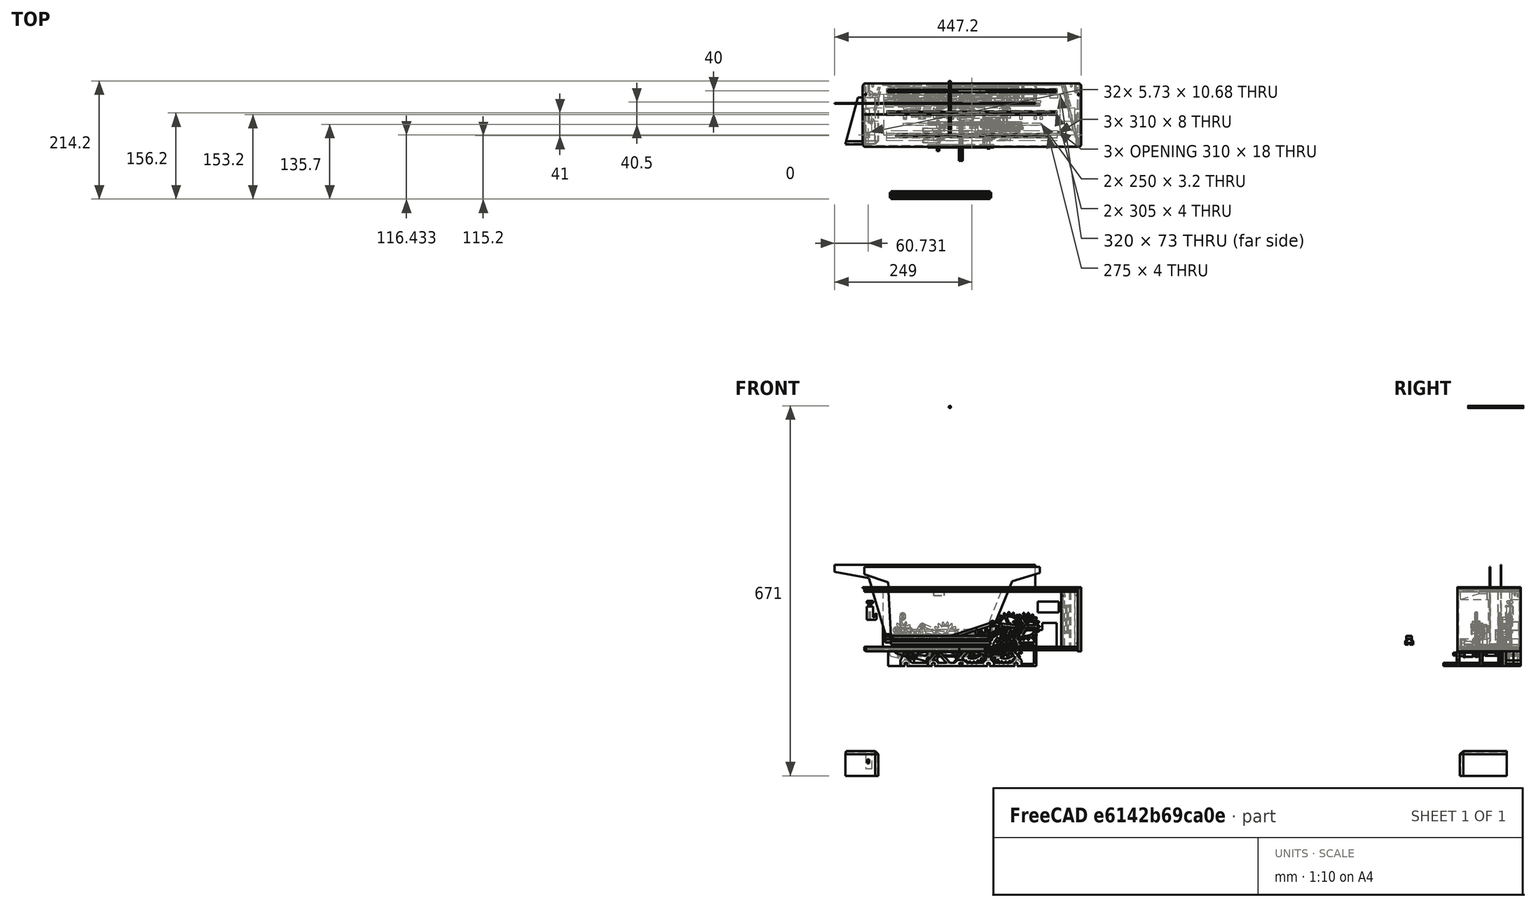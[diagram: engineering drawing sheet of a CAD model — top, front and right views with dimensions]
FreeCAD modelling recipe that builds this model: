
FCSTD DOCUMENT  (FreeCAD 0.22R37668 (Git))
Label: wobbler
License: Creative Commons Attribution-ShareAlike 3.0
LicenseURL: https://creativecommons.org/licenses/by-sa/3.0/
objects: Sketcher::SketchObject×136, PartDesign::Pad×68, PartDesign::Body×68, PartDesign::Pocket×54, PartDesign::FeatureBase×8, PartDesign::Mirrored×7, App::Part×7, PartDesign::FeaturePython×6, PartDesign::Groove×6, PartDesign::Revolution×6, Part::FeaturePython×6, PartDesign::PolarPattern×5, PartDesign::Chamfer×5, PartDesign::MultiTransform×3, Image::ImagePlane×3, PartDesign::Fillet×3, Mesh::Feature×2, PartDesign::LinearPattern×2, PartDesign::Plane×2, App::DocumentObjectGroup×2, +3 more types
note: 532 computed .brp shape members not serialized (recipe doc carries the construction recipe); baked Part::Feature solids carry a one-line shape summary decoded from their .brp

FEATURE [PartDesign::FeaturePython] InvoluteGear  label="M2.5-24T"  # WARN: FeaturePython — macro-defined, semantics opaque (R4)
  AttacherType = Attacher::AttachEngine3D
  Placement = pos=(0,0,0) rot=(1,0,0;1.5708rad)
  Suppressed = false
  angular_backlash = 0.190986
  backlash = 0.1
  beta = 0
  clearance = 0.25
  da = 65
  df = 53.75
  double_helix = false
  dw = 60
  head = 0
  head_fillet = 0
  height = 5
  module = 2.5
  numpoints = 6
  pressure_angle = 20
  properties_from_tool = false
  reversed_backlash = false
  root_fillet = 0
  shift = 0
  simple = false
  teeth = 24
  transverse_pitch = 7.85398
  undercut = false
  version = 0.0.4
  expr: angular_backlash = backlash / dw * 360 ° / pi
  expr: dw = teeth * module
FEATURE [Sketcher::SketchObject] Sketch001
  AttachmentSupport = -> [XY_Plane001]
  FullyConstrained = true
  MapMode = 5
  sketch-geometry (6):
    g0: LineSegment StartX=-2.45 StartY=0 StartZ=0 EndX=-2.45 EndY=-7.9 EndZ=0
    g1: LineSegment StartX=-2.45 StartY=-7.9 StartZ=0 EndX=19.65 EndY=-7.9 EndZ=0
    g2: LineSegment StartX=19.65 StartY=-7.9 StartZ=0 EndX=19.65 EndY=-3 EndZ=0
    g3: LineSegment StartX=19.65 StartY=-3 StartZ=0 EndX=2.45 EndY=-3 EndZ=0
    g4: LineSegment StartX=2.45 StartY=-3 StartZ=0 EndX=2.45 EndY=0 EndZ=0
    g5: LineSegment StartX=2.45 StartY=0 StartZ=0 EndX=-2.45 EndY=0 EndZ=0
  constraints (17):
    c: PointOnObject(g0,g-1)
    c: Vertical(g0)
    c: Coincident(g0,g1)
    c: Horizontal(g1)
    c: Coincident(g1,g2)
    c: Vertical(g2)
    c: Coincident(g2,g3)
    c: Horizontal(g3)
    c: Coincident(g3,g4)
    c: Coincident(g4,g5)
    c: Coincident(g5,g0)
    c: DistanceX(g5,g5) = 4.9
    c: Symmetric(g4,g0,g-2)
    c: Vertical(g4)
    c: DistanceY(g4,g4) = 3
    c: DistanceX(g3,g3) = 17.2
    c: Equal(g2,g5)
FEATURE [PartDesign::Pocket] Pocket
  BaseFeature = -> InvoluteGear
  Direction = (0,0,-1)
  Length = 5.2
  Length2 = 5
  Midplane = true
  Placement = pos=(0,0,0) rot=(1,0,0;1.5708rad)
  Profile = -> Sketch001
  ReferenceAxis = -> Sketch001 [N_Axis]
  Refine = true
  Suppressed = false
  Type = 0
FEATURE [Sketcher::SketchObject] Sketch002
  AttachmentSupport = -> [XZ_Plane002]
  FullyConstrained = true
  MapMode = 5
  Placement = pos=(0,0,0) rot=(1,0,0;1.5708rad)
  sketch-geometry (1):
    g0: Circle CenterX=0 CenterY=0 CenterZ=0 NormalX=0 NormalY=0 NormalZ=1 AngleXU=0 Radius=2.5
  constraints (2):
    c: Coincident(g0,g-1)
    c: Diameter(g0) = 5
FEATURE [PartDesign::Pad] Pad
  Direction = (0,-1,2e-16)
  Length = 56
  Length2 = 10
  Midplane = true
  Placement = pos=(0,0,0) rot=(1,0,0;1.5708rad)
  Profile = -> Sketch002
  ReferenceAxis = -> Sketch002 [N_Axis]
  Refine = true
  Suppressed = false
  Type = 0
FEATURE [Sketcher::SketchObject] Sketch003
  AttachmentSupport = -> [XZ_Plane002]
  FullyConstrained = true
  MapMode = 5
  Placement = pos=(0,0,0) rot=(1,0,0;1.5708rad)
  sketch-geometry (5):
    g0: ArcOfCircle CenterX=17 CenterY=0 CenterZ=0 NormalX=0 NormalY=0 NormalZ=1 AngleXU=0 Radius=7.5 StartAngle=5.94335 EndAngle=7.85398
    g1: ArcOfCircle CenterX=5 CenterY=0 CenterZ=0 NormalX=0 NormalY=0 NormalZ=1 AngleXU=0 Radius=7.5 StartAngle=1.5708 EndAngle=3.14159
    g2: LineSegment StartX=5 StartY=7.5 StartZ=0 EndX=17 EndY=7.5 EndZ=0
    g3: LineSegment StartX=-2.5 StartY=9e-16 StartZ=0 EndX=-2.5 EndY=-2.5 EndZ=0
    g4: LineSegment StartX=-2.5 StartY=-2.5 StartZ=0 EndX=24.0711 EndY=-2.5 EndZ=0
  constraints (15):
    c: PointOnObject(g0,g-1)
    c: PointOnObject(g1,g-1)
    c: PointOnObject(g1,g-1)
    c: Coincident(g2,g0)
    c: Horizontal(g2)
    c: DistanceX(g0) = 17
    c: Diameter(g0) = 15
    c: Tangent(g1,g3) = -1.5708
    c: Coincident(g3,g4)
    c: Coincident(g4,g0)
    c: Horizontal(g4)
    c: DistanceX(g3) = -2.5
    c: DistanceY(g3,g3) = 2.5
    c: Equal(g1,g0)
    c: Tangent(g2,g1) = 1.5708
FEATURE [PartDesign::Pad] Pad001
  BaseFeature = -> Pad
  Direction = (0,-1,2e-16)
  Length = 26
  Length2 = 10
  Midplane = true
  Placement = pos=(0,0,0) rot=(1,0,0;1.5708rad)
  Profile = -> Sketch003
  ReferenceAxis = -> Sketch003 [N_Axis]
  Refine = true
  Suppressed = false
  Type = 0
FEATURE [Sketcher::SketchObject] Sketch004
  AttachmentSupport = -> [XY_Plane002]
  FullyConstrained = true
  MapMode = 5
  sketch-geometry (6):
    g0: LineSegment StartX=-2.5 StartY=18 StartZ=0 EndX=-2.5 EndY=0 EndZ=0
    g1: LineSegment StartX=-2.5 StartY=0 StartZ=0 EndX=19.5 EndY=0 EndZ=0
    g2: LineSegment StartX=19.5 StartY=0 StartZ=0 EndX=19.5 EndY=15 EndZ=0
    g3: LineSegment StartX=19.5 StartY=15 StartZ=0 EndX=2.5 EndY=15 EndZ=0
    g4: LineSegment StartX=2.5 StartY=15 StartZ=0 EndX=2.5 EndY=18 EndZ=0
    g5: LineSegment StartX=2.5 StartY=18 StartZ=0 EndX=-2.5 EndY=18 EndZ=0
  constraints (17):
    c: Vertical(g0)
    c: Coincident(g0,g1)
    c: Horizontal(g1)
    c: Coincident(g1,g2)
    c: Vertical(g2)
    c: Coincident(g2,g3)
    c: Horizontal(g3)
    c: Coincident(g3,g4)
    c: Vertical(g4)
    c: Coincident(g4,g5)
    c: Coincident(g5,g0)
    c: Symmetric(g0,g4,g-2)
    c: DistanceX(g5,g5) = 5
    c: DistanceY(g4,g4) = 3
    c: DistanceY(g0) = 18
    c: PointOnObject(g0,g-1)
    c: DistanceX(g3,g3) = 17
FEATURE [PartDesign::Pad] Pad002
  BaseFeature = -> Pad001
  Direction = (0,0,1)
  Length = 5
  Length2 = 10
  Midplane = true
  Placement = pos=(0,0,0) rot=(1,0,0;1.5708rad)
  Profile = -> Sketch004
  ReferenceAxis = -> Sketch004 [N_Axis]
  Refine = true
  Suppressed = false
  Type = 0
FEATURE [Sketcher::SketchObject] Sketch005
  AttachmentSupport = -> [XZ_Plane002]
  FullyConstrained = true
  MapMode = 5
  Placement = pos=(0,0,0) rot=(1,0,0;1.5708rad)
  sketch-geometry (6):
    g0: ArcOfCircle CenterX=17 CenterY=0 CenterZ=0 NormalX=0 NormalY=0 NormalZ=1 AngleXU=0 Radius=3 StartAngle=5.29807 EndAngle=10.4099
    g1: LineSegment StartX=15.3417 StartY=-2.5 StartZ=0 EndX=-4.65831 EndY=-2.5 EndZ=0
    g2: LineSegment StartX=-4.65831 StartY=-2.5 StartZ=0 EndX=-4.65831 EndY=17.5 EndZ=0
    g3: LineSegment StartX=-4.65831 StartY=17.5 StartZ=0 EndX=38.6583 EndY=17.5 EndZ=0
    g4: LineSegment StartX=38.6583 StartY=17.5 StartZ=0 EndX=38.6583 EndY=-2.5 EndZ=0
    g5: LineSegment StartX=38.6583 StartY=-2.5 StartZ=0 EndX=18.6583 EndY=-2.5 EndZ=0
  constraints (19):
    c: PointOnObject(g0,g-1)
    c: Coincident(g0,g1)
    c: Horizontal(g1)
    c: Coincident(g1,g2)
    c: Vertical(g2)
    c: Coincident(g2,g3)
    c: Horizontal(g3)
    c: Coincident(g3,g4)
    c: Vertical(g4)
    c: Coincident(g4,g5)
    c: Coincident(g5,g0)
    c: Horizontal(g5)
    c: Horizontal(g0,g0)
    c: DistanceY(g1) = -2.5
    c: DistanceX(g0) = 17
    c: Diameter(g0) = 6
    c: Equal(g5,g4)
    c: DistanceX(g1,g1) = 20
    c: Equal(g1,g5)
FEATURE [PartDesign::Pocket] Pocket001
  BaseFeature = -> Pad002
  Direction = (0,1,-2e-16)
  Length = 15
  Length2 = 5
  Midplane = true
  Placement = pos=(0,0,0) rot=(1,0,0;1.5708rad)
  Profile = -> Sketch005
  ReferenceAxis = -> Sketch005 [N_Axis]
  Refine = true
  Suppressed = false
  Type = 0
FEATURE [Sketcher::SketchObject] Sketch006
  AttachmentSupport = -> [XZ_Plane001]
  FullyConstrained = true
  MapMode = 5
  Placement = pos=(0,0,0) rot=(1,0,0;1.5708rad)
  sketch-geometry (7):
    g0: ArcOfCircle CenterX=0 CenterY=0 CenterZ=0 NormalX=0 NormalY=0 NormalZ=1 AngleXU=0 Radius=7 StartAngle=0.608246 EndAngle=1.48615
    g1: ArcOfCircle CenterX=0 CenterY=0 CenterZ=0 NormalX=0 NormalY=0 NormalZ=1 AngleXU=0 Radius=21.5 StartAngle=0.187137 EndAngle=1.90726
    g2: LineSegment StartX=21.1246 StartY=4 StartZ=0 EndX=5.74456 EndY=4 EndZ=0
    g3: LineSegment StartX=0.59182 StartY=6.97494 StartZ=0 EndX=-7.09821 EndY=20.2945 EndZ=0
    g4: LineSegment StartX=0 StartY=0 StartZ=0 EndX=-10.5623 EndY=18.2945 EndZ=0
    g5: LineSegment StartX=-10.5623 StartY=18.2945 StartZ=0 EndX=-7.09821 EndY=20.2945 EndZ=0
    g6: LineSegment StartX=21.1246 StartY=4 StartZ=0 EndX=21.1246 EndY=0 EndZ=0
  constraints (20):
    c: Coincident(g0,g-1)
    c: Coincident(g1,g0)
    c: Coincident(g2,g1)
    c: Coincident(g2,g0)
    c: Coincident(g3,g0)
    c: Coincident(g3,g1)
    c: Coincident(g4,g0)
    c: Coincident(g5,g4)
    c: Coincident(g5,g1)
    c: Parallel(g4,g3)
    c: Perpendicular(g4,g5)
    c: Angle(g-1,g4) = 2.0944
    c: Horizontal(g2)
    c: Coincident(g6,g1)
    c: PointOnObject(g6,g-1)
    c: Vertical(g6)
    c: Equal(g6,g5)
    c: Diameter(g0) = 14
    c: Diameter(g1) = 43
    c: DistanceY(g6,g6) = 4
FEATURE [PartDesign::Pocket] Pocket002  label="120deg-sector"
  BaseFeature = -> Pocket
  Direction = (0,1,-2e-16)
  Length = 5
  Length2 = 5
  Midplane = true
  Placement = pos=(0,0,0) rot=(1,0,0;1.5708rad)
  Profile = -> Sketch006
  ReferenceAxis = -> Sketch006 [N_Axis]
  Refine = true
  Suppressed = false
  Type = 1
FEATURE [PartDesign::PolarPattern] PolarPattern
  Angle = 360
  Axis = -> Sketch006 [N_Axis]
  BaseFeature = -> Pocket002
  Mode = 0
  Occurrences = 3
  Offset = 120
  Originals = -> [Pocket002]
  Placement = pos=(0,0,0) rot=(1,0,0;1.5708rad)
  Refine = true
  Suppressed = false
  TransformMode = 0
FEATURE [PartDesign::Body] Body001  label="M2.5-24t-Crank"
  AllowCompound = false
  Group = -> [InvoluteGear,Sketch001,Pocket,Sketch006,Pocket002,PolarPattern]
  Origin = -> Origin001
  Tip = -> PolarPattern
FEATURE [Sketcher::SketchObject] Sketch007
  AttachmentSupport = -> [XY_Plane003]
  FullyConstrained = true
  MapMode = 5
  sketch-geometry (22):
    g0: Circle CenterX=0 CenterY=0 CenterZ=0 NormalX=0 NormalY=0 NormalZ=1 AngleXU=0 Radius=2.5
    g1: Circle CenterX=10 CenterY=0 CenterZ=0 NormalX=0 NormalY=0 NormalZ=1 AngleXU=0 Radius=2.5
    g2: ArcOfCircle CenterX=0 CenterY=0 CenterZ=0 NormalX=0 NormalY=0 NormalZ=1 AngleXU=0 Radius=5 StartAngle=0.304693 EndAngle=1.7897
    g3: ArcOfCircle CenterX=0 CenterY=0 CenterZ=0 NormalX=0 NormalY=0 NormalZ=1 AngleXU=0 Radius=17 StartAngle=0.438962 EndAngle=2.00604
    g4: ArcOfCircle CenterX=0 CenterY=0 CenterZ=0 NormalX=0 NormalY=0 NormalZ=1 AngleXU=0 Radius=5 StartAngle=2.39909 EndAngle=3.8841
    g5: ArcOfCircle CenterX=0 CenterY=0 CenterZ=0 NormalX=0 NormalY=0 NormalZ=1 AngleXU=0 Radius=17 StartAngle=2.18275 EndAngle=4.10044
    g6: ArcOfCircle CenterX=0 CenterY=0 CenterZ=0 NormalX=0 NormalY=0 NormalZ=1 AngleXU=0 Radius=17 StartAngle=4.27714 EndAngle=5.84422
    g7: ArcOfCircle CenterX=0 CenterY=0 CenterZ=0 NormalX=0 NormalY=0 NormalZ=1 AngleXU=0 Radius=5 StartAngle=4.49348 EndAngle=5.97849
    g8: LineSegment StartX=0 StartY=0 StartZ=0 EndX=-8.46685 EndY=14.665 EndZ=0
    g9: LineSegment StartX=-3.68389 StartY=3.38068 StartZ=0 EndX=-9.76589 EndY=13.915 EndZ=0
    g10: LineSegment StartX=-9.76589 StartY=13.915 StartZ=0 EndX=-7.16781 EndY=15.415 EndZ=0
    g11: LineSegment StartX=-7.16781 StartY=15.415 StartZ=0 EndX=-1.08581 EndY=4.88068 EndZ=0
    g12: LineSegment StartX=-3.68389 StartY=-3.38068 StartZ=0 EndX=-9.76589 EndY=-13.915 EndZ=0
    g13: LineSegment StartX=-7.16781 StartY=-15.415 StartZ=0 EndX=-1.08581 EndY=-4.88068 EndZ=0
    g14: LineSegment StartX=4.7697 StartY=-1.5 StartZ=0 EndX=6.02351 EndY=-1.5 EndZ=0
    g15: LineSegment StartX=4.7697 StartY=1.5 StartZ=0 EndX=6.02351 EndY=1.5 EndZ=0
    g16: LineSegment StartX=15.3883 StartY=7.225 StartZ=0 EndX=8.19375 EndY=3.84707 EndZ=0
    g17: LineSegment StartX=15.3883 StartY=-7.225 StartZ=0 EndX=8.19375 EndY=-3.84707 EndZ=0
    g18: ArcOfCircle CenterX=10 CenterY=0 CenterZ=0 NormalX=0 NormalY=0 NormalZ=1 AngleXU=0 Radius=4.25 StartAngle=2.00976 EndAngle=2.78088
    g19: ArcOfCircle CenterX=10 CenterY=0 CenterZ=0 NormalX=0 NormalY=0 NormalZ=1 AngleXU=0 Radius=4.25 StartAngle=3.50231 EndAngle=4.27343
    g20: LineSegment StartX=0 StartY=0 StartZ=0 EndX=-8.46685 EndY=-14.665 EndZ=0
    g21: LineSegment StartX=-9.76589 StartY=-13.915 StartZ=0 EndX=-7.16781 EndY=-15.415 EndZ=0
  constraints (58):
    c: Coincident(g0,g-1)
    c: PointOnObject(g1,g-1)
    c: DistanceX(g1) = 10
    c: Diameter(g0) = 5
    c: Equal(g0,g1)
    c: Coincident(g2,g0)
    c: Coincident(g3,g0)
    c: Coincident(g4,g0)
    c: Coincident(g5,g0)
    c: Coincident(g6,g0)
    c: Coincident(g7,g0)
    c: Equal(g7,g2)
    c: Equal(g2,g4)
    c: Diameter(g2) = 10
    c: Diameter(g3) = 34
    c: Coincident(g8,g0)
    c: Coincident(g9,g4)
    c: Coincident(g9,g5)
    c: Coincident(g10,g5)
    c: Coincident(g10,g3)
    c: Coincident(g11,g3)
    c: Coincident(g11,g2)
    c: Coincident(g12,g4)
    c: Coincident(g13,g6)
    c: Coincident(g13,g7)
    c: Coincident(g14,g7)
    c: Horizontal(g14)
    c: Coincident(g15,g2)
    c: Horizontal(g15)
    c: Coincident(g16,g3)
    c: Coincident(g17,g6)
    c: Coincident(g18,g1)
    c: Coincident(g18,g15)
    c: Coincident(g19,g1)
    c: Coincident(g19,g14)
    c: Symmetric(g6,g3,g-1)
    c: Tangent(g19,g17) = 1.5708
    c: Tangent(g18,g16) = -1.5708
    c: Symmetric(g14,g15,g-1)
    c: Parallel(g11,g8)
    c: Parallel(g8,g9)
    c: PointOnObject(g8,g10)
    c: Symmetric(g5,g3,g8)
    c: Angle(g-1,g8) = 2.0944
    c: Distance(g10) = 3
    c: DistanceY(g14,g15) = 3
    c: Diameter(g18) = 8.5
    c: Parallel(g13,g12)
    c: Coincident(g20,g0)
    c: Coincident(g21,g6)
    c: Parallel(g13,g20)
    c: PointOnObject(g20,g21)
    c: Equal(g21,g10)
    c: Angle(g20) = -2.0944
    c: Coincident(g5,g12)
    c: PointOnObject(g21,g12)
    c: Symmetric(g21,g6,g20)
    c: Perpendicular(g3,g16)
FEATURE [Sketcher::SketchObject] Sketch008
  AttachmentSupport = -> [XZ_Plane003]
  FullyConstrained = true
  MapMode = 5
  Placement = pos=(0,0,0) rot=(1,0,0;1.5708rad)
  sketch-geometry (4):
    g0: LineSegment StartX=19.2 StartY=6.8 StartZ=0 EndX=19.2 EndY=4.8 EndZ=0
    g1: LineSegment StartX=19.2 StartY=4.8 StartZ=0 EndX=27.2 EndY=4.10009 EndZ=0
    g2: LineSegment StartX=27.2 StartY=4.10009 StartZ=0 EndX=27.2 EndY=6.8 EndZ=0
    g3: LineSegment StartX=27.2 StartY=6.8 StartZ=0 EndX=19.2 EndY=6.8 EndZ=0
  constraints (12):
    c: Coincident(g0,g1)
    c: Coincident(g1,g2)
    c: Coincident(g2,g3)
    c: Coincident(g3,g0)
    c: Vertical(g0)
    c: Vertical(g2)
    c: Horizontal(g3)
    c: DistanceY(g0,g0) = 2
    c: DistanceX(g1,g1) = 8
    c: DistanceX(g0) = 19.2
    c: DistanceY(g0) = 4.8
    c: Angle(g1,g3) = 0.0872665
FEATURE [Sketcher::SketchObject] Sketch009
  AttachmentSupport = -> [XZ_Plane003]
  FullyConstrained = true
  MapMode = 5
  Placement = pos=(0,0,0) rot=(1,0,0;1.5708rad)
  sketch-geometry (14):
    g0: LineSegment StartX=15.5 StartY=1.63397 StartZ=0 EndX=16 EndY=2.5 EndZ=0
    g1: LineSegment StartX=16 StartY=2.5 StartZ=0 EndX=15.5 EndY=3.36603 EndZ=0
    g2: LineSegment StartX=15.5 StartY=3.36603 StartZ=0 EndX=14.5 EndY=3.36603 EndZ=0
    g3: LineSegment StartX=14.5 StartY=3.36603 StartZ=0 EndX=14 EndY=2.5 EndZ=0
    g4: LineSegment StartX=14 StartY=2.5 StartZ=0 EndX=14.5 EndY=1.63397 EndZ=0
    g5: LineSegment StartX=14.5 StartY=1.63397 StartZ=0 EndX=15.5 EndY=1.63397 EndZ=0
    g6: Circle CenterX=15 CenterY=2.5 CenterZ=0 NormalX=0 NormalY=0 NormalZ=1 AngleXU=0 Radius=1
    g7: LineSegment StartX=0.5 StartY=1.63397 StartZ=0 EndX=1 EndY=2.5 EndZ=0
    g8: LineSegment StartX=1 StartY=2.5 StartZ=0 EndX=0.5 EndY=3.36603 EndZ=0
    g9: LineSegment StartX=0.5 StartY=3.36603 StartZ=0 EndX=-0.5 EndY=3.36603 EndZ=0
    g10: LineSegment StartX=-0.5 StartY=3.36603 StartZ=0 EndX=-1 EndY=2.5 EndZ=0
    g11: LineSegment StartX=-1 StartY=2.5 StartZ=0 EndX=-0.5 EndY=1.63397 EndZ=0
    g12: LineSegment StartX=-0.5 StartY=1.63397 StartZ=0 EndX=0.5 EndY=1.63397 EndZ=0
    g13: Circle CenterX=0 CenterY=2.5 CenterZ=0 NormalX=0 NormalY=0 NormalZ=1 AngleXU=0 Radius=1
  constraints (34):
    c: Coincident(g0,g1)
    c: Coincident(g1,g2)
    c: Coincident(g2,g3)
    c: Coincident(g3,g4)
    c: Coincident(g4,g5)
    c: Coincident(g5,g0)
    c: Equal(g0, g1-g5) x5
    c: PointOnObject(g0,g6)
    c: PointOnObject(g1,g6)
    c: PointOnObject(g2,g6)
    c: PointOnObject(g3,g6)
    c: PointOnObject(g4,g6)
    c: PointOnObject(g5,g6)
    c: Horizontal(g5)
    c: Diameter(g6) = 2
    c: DistanceX(g6) = 15
    c: DistanceY(g6) = 2.5
    c: Coincident(g7,g8)
    c: Coincident(g8,g9)
    c: Coincident(g9,g10)
    c: Coincident(g10,g11)
    c: Coincident(g11,g12)
    c: Coincident(g12,g7)
    c: Equal(g7, g8-g12) x5
    c: PointOnObject(g7,g13)
    c: PointOnObject(g8,g13)
    c: PointOnObject(g9,g13)
    c: PointOnObject(g10,g13)
    c: PointOnObject(g11,g13)
    c: PointOnObject(g12,g13)
    c: Horizontal(g12)
    c: Equal(g13,g6)
    c: Horizontal(g13,g6)
    c: PointOnObject(g13,g-2)
FEATURE [Sketcher::SketchObject] Sketch010
  AttachmentOffset = pos=(0,0,5) rot=(0,0,1;0rad)
  AttachmentSupport = -> [XY_Plane003]
  FullyConstrained = true
  MapMode = 5
  Placement = pos=(0,0,5) rot=(0,0,1;0rad)
  sketch-geometry (2):
    g0: Circle CenterX=10 CenterY=0 CenterZ=0 NormalX=0 NormalY=0 NormalZ=1 AngleXU=0 Radius=2.5
    g1: Circle CenterX=10 CenterY=0 CenterZ=0 NormalX=0 NormalY=0 NormalZ=1 AngleXU=0 Radius=4.25
  constraints (5):
    c: PointOnObject(g0,g-1)
    c: Coincident(g1,g0)
    c: DistanceX(g0) = 10
    c: Diameter(g0) = 5
    c: Diameter(g1) = 8.5
FEATURE [Sketcher::SketchObject] Sketch011
  AttachmentSupport = -> [XZ_Plane005]
  FullyConstrained = true
  MapMode = 5
  Placement = pos=(0,0,0) rot=(1,0,0;1.5708rad)
  sketch-geometry (5):
    g0: Circle CenterX=0 CenterY=0 CenterZ=0 NormalX=0 NormalY=0 NormalZ=1 AngleXU=0 Radius=2.65
    g1: ArcOfCircle CenterX=0 CenterY=0 CenterZ=0 NormalX=0 NormalY=0 NormalZ=1 AngleXU=0 Radius=6 StartAngle=6.21647 EndAngle=9.49149
    g2: ArcOfCircle CenterX=0 CenterY=-45 CenterZ=0 NormalX=0 NormalY=0 NormalZ=1 AngleXU=0 Radius=3 StartAngle=3.20831 EndAngle=6.21647
    g3: LineSegment StartX=-5.98665 StartY=-0.4 StartZ=0 EndX=-2.99333 EndY=-45.2 EndZ=0
    g4: LineSegment StartX=2.99333 StartY=-45.2 StartZ=0 EndX=5.98665 EndY=-0.4 EndZ=0
  constraints (11):
    c: PointOnObject(g2,g-2)
    c: Tangent(g4,g1) = -1.5708
    c: Tangent(g3,g1) = -1.5708
    c: Tangent(g4,g2) = -1.5708
    c: Tangent(g3,g2) = -1.5708
    c: Diameter(g0) = 5.3
    c: Diameter(g1) = 12
    c: Diameter(g2) = 6
    c: DistanceY(g2) = -45
    c: Coincident(g1,g0)
    c: Coincident(g0,g-1)
FEATURE [PartDesign::Pad] Pad004
  Direction = (0,-1,2e-16)
  Length = 4
  Length2 = 10
  Placement = pos=(0,0,0) rot=(1,0,0;1.5708rad)
  Profile = -> Sketch011
  ReferenceAxis = -> Sketch011 [N_Axis]
  Suppressed = false
  Type = 0
FEATURE [Sketcher::SketchObject] Sketch012
  AttachmentSupport = -> [XZ_Plane005]
  FullyConstrained = true
  MapMode = 5
  Placement = pos=(0,0,0) rot=(1,0,0;1.5708rad)
  sketch-geometry (1):
    g0: Circle CenterX=0 CenterY=-45 CenterZ=0 NormalX=0 NormalY=0 NormalZ=1 AngleXU=0 Radius=3
  constraints (3):
    c: PointOnObject(g0,g-2)
    c: DistanceY(g0) = -45
    c: Diameter(g0) = 6
FEATURE [PartDesign::Pad] Pad005
  BaseFeature = -> Pad004
  Direction = (0,-1,2e-16)
  Length = 23
  Length2 = 10
  Placement = pos=(0,0,0) rot=(1,0,0;1.5708rad)
  Profile = -> Sketch012
  ReferenceAxis = -> Sketch012 [N_Axis]
  Suppressed = false
  Type = 0
FEATURE [Sketcher::SketchObject] Sketch013
  AttachmentSupport = -> [YZ_Plane005]
  FullyConstrained = true
  MapMode = 5
  Placement = pos=(0,0,0) rot=(0.57735,0.57735,0.57735;2.0944rad)
  sketch-geometry (7):
    g0: LineSegment StartX=-20.134 StartY=-45.5 StartZ=0 EndX=-20.134 EndY=-44.5 EndZ=0
    g1: LineSegment StartX=-20.134 StartY=-44.5 StartZ=0 EndX=-21 EndY=-44 EndZ=0
    g2: LineSegment StartX=-21 StartY=-44 StartZ=0 EndX=-21.866 EndY=-44.5 EndZ=0
    g3: LineSegment StartX=-21.866 StartY=-44.5 StartZ=0 EndX=-21.866 EndY=-45.5 EndZ=0
    g4: LineSegment StartX=-21.866 StartY=-45.5 StartZ=0 EndX=-21 EndY=-46 EndZ=0
    g5: LineSegment StartX=-21 StartY=-46 StartZ=0 EndX=-20.134 EndY=-45.5 EndZ=0
    g6: Circle CenterX=-21 CenterY=-45 CenterZ=0 NormalX=0 NormalY=0 NormalZ=1 AngleXU=0 Radius=1
  constraints (17):
    c: Coincident(g0,g1)
    c: Coincident(g1,g2)
    c: Coincident(g2,g3)
    c: Coincident(g3,g4)
    c: Coincident(g4,g5)
    c: Coincident(g5,g0)
    c: Equal(g0, g1-g5) x5
    c: PointOnObject(g0,g6)
    c: PointOnObject(g1,g6)
    c: PointOnObject(g2,g6)
    c: PointOnObject(g3,g6)
    c: PointOnObject(g4,g6)
    c: PointOnObject(g5,g6)
    c: Vertical(g0)
    c: Diameter(g6) = 2
    c: DistanceY(g6) = -45
    c: DistanceX(g6) = -21
FEATURE [PartDesign::Pocket] Pocket005
  BaseFeature = -> Pad005
  Direction = (-1,0,0)
  Length = 5
  Length2 = 5
  Midplane = true
  Placement = pos=(0,0,0) rot=(1,0,0;1.5708rad)
  Profile = -> Sketch013
  ReferenceAxis = -> Sketch013 [N_Axis]
  Suppressed = false
  Type = 1
FEATURE [PartDesign::Body] Body005  label="Ear"
  AllowCompound = false
  Group = -> [Sketch011,Pad004,Sketch012,Pad005,Sketch013,Pocket005]
  Origin = -> Origin005
  Placement = pos=(-98.8003,-6.5,25.3485) rot=(0,1,0;0.523599rad)
  Tip = -> Pocket005
FEATURE [Sketcher::SketchObject] Sketch014
  AttachmentSupport = -> [XZ_Plane006]
  FullyConstrained = true
  MapMode = 5
  Placement = pos=(0,0,0) rot=(1,0,0;1.5708rad)
  sketch-geometry (2):
    g0: Circle CenterX=0 CenterY=0 CenterZ=0 NormalX=0 NormalY=0 NormalZ=1 AngleXU=0 Radius=3
    g1: Circle CenterX=0 CenterY=0 CenterZ=0 NormalX=0 NormalY=0 NormalZ=1 AngleXU=0 Radius=6
  constraints (4):
    c: Coincident(g0,g-1)
    c: Coincident(g1,g0)
    c: Diameter(g0) = 6
    c: Diameter(g1) = 12
FEATURE [PartDesign::Pad] Pad006
  Direction = (0,-1,2e-16)
  Length = 4
  Length2 = 10
  Midplane = true
  Placement = pos=(0,0,0) rot=(1,0,0;1.5708rad)
  Profile = -> Sketch014
  ReferenceAxis = -> Sketch014 [N_Axis]
  Suppressed = false
  Type = 0
FEATURE [Sketcher::SketchObject] Sketch015
  AttachmentSupport = -> [YZ_Plane006]
  FullyConstrained = true
  MapMode = 5
  Placement = pos=(0,0,0) rot=(0.57735,0.57735,0.57735;2.0944rad)
  sketch-geometry (7):
    g0: LineSegment StartX=0 StartY=-1 StartZ=0 EndX=0.866025 EndY=-0.5 EndZ=0
    g1: LineSegment StartX=0.866025 StartY=-0.5 StartZ=0 EndX=0.866025 EndY=0.5 EndZ=0
    g2: LineSegment StartX=0.866025 StartY=0.5 StartZ=0 EndX=5.8e-13 EndY=1 EndZ=0
    g3: LineSegment StartX=5.8e-13 StartY=1 StartZ=0 EndX=-0.866025 EndY=0.5 EndZ=0
    g4: LineSegment StartX=-0.866025 StartY=0.5 StartZ=0 EndX=-0.866025 EndY=-0.5 EndZ=0
    g5: LineSegment StartX=-0.866025 StartY=-0.5 StartZ=0 EndX=0 EndY=-1 EndZ=0
    g6: Circle CenterX=0 CenterY=0 CenterZ=0 NormalX=0 NormalY=0 NormalZ=1 AngleXU=0 Radius=1
  constraints (16):
    c: Coincident(g0,g1)
    c: Coincident(g1,g2)
    c: Coincident(g2,g3)
    c: Coincident(g3,g4)
    c: Coincident(g4,g5)
    c: Coincident(g5,g0)
    c: Equal(g0, g1-g5) x5
    c: PointOnObject(g0,g6)
    c: PointOnObject(g1,g6)
    c: PointOnObject(g2,g6)
    c: PointOnObject(g3,g6)
    c: PointOnObject(g4,g6)
    c: PointOnObject(g5,g6)
    c: Coincident(g6,g-1)
    c: PointOnObject(g5,g-2)
    c: Diameter(g6) = 2
FEATURE [PartDesign::Pocket] Pocket006
  BaseFeature = -> Pad006
  Direction = (-1,0,0)
  Length = 5
  Length2 = 5
  Midplane = true
  Placement = pos=(0,0,0) rot=(1,0,0;1.5708rad)
  Profile = -> Sketch015
  ReferenceAxis = -> Sketch015 [N_Axis]
  Suppressed = false
  Type = 1
FEATURE [PartDesign::Body] Body006  label="EarDisk"
  AllowCompound = false
  Group = -> [Sketch014,Pad006,Sketch015,Pocket006]
  Origin = -> Origin006
  Placement = pos=(-90.5,-27.5,-4.5) rot=(0,0,1;0rad)
  Tip = -> Pocket006
FEATURE [Sketcher::SketchObject] Sketch016
  AttachmentSupport = -> [YZ_Plane007]
  FullyConstrained = true
  MapMode = 5
  Placement = pos=(0,0,0) rot=(0.57735,0.57735,0.57735;2.0944rad)
  sketch-geometry (27):
    g0: LineSegment StartX=-1 StartY=10.5779 StartZ=0 EndX=-1 EndY=7.57794 EndZ=0
    g1: LineSegment StartX=-1 StartY=7.57794 StartZ=0 EndX=-6.1 EndY=1.5 EndZ=0
    g2: LineSegment StartX=-6.1 StartY=1.5 StartZ=0 EndX=-6.1 EndY=0 EndZ=0
    g3: LineSegment StartX=-6.1 StartY=0 StartZ=0 EndX=6.1 EndY=0 EndZ=0
    g4: LineSegment StartX=6.1 StartY=0 StartZ=0 EndX=6.1 EndY=1.5 EndZ=0
    g5: LineSegment StartX=6.1 StartY=1.5 StartZ=0 EndX=1 EndY=7.57794 EndZ=0
    g6: LineSegment StartX=1 StartY=7.57794 StartZ=0 EndX=1 EndY=10.5779 EndZ=0
    g7: LineSegment StartX=3 StartY=12.2464 StartZ=0 EndX=3 EndY=8.30588 EndZ=0
    g8: LineSegment StartX=3 StartY=8.30588 StartZ=0 EndX=7.2 EndY=3.30052 EndZ=0
    g9: LineSegment StartX=7.2 StartY=3.30052 StartZ=0 EndX=7.2 EndY=-3 EndZ=0
    g10: LineSegment StartX=-7.2 StartY=-3 StartZ=0 EndX=-7.2 EndY=3.30052 EndZ=0
    g11: LineSegment StartX=-7.2 StartY=3.30052 StartZ=0 EndX=-3 EndY=8.30588 EndZ=0
    g12: LineSegment StartX=-3 StartY=8.30588 StartZ=0 EndX=-3 EndY=12.2464 EndZ=0
    g13: LineSegment StartX=-3 StartY=8.30588 StartZ=0 EndX=-1.46791 EndY=7.02031 EndZ=0
    g14: LineSegment StartX=6.1 StartY=0 StartZ=0 EndX=6.1 EndY=-3 EndZ=0
    g15: LineSegment StartX=3 StartY=8.30588 StartZ=0 EndX=1.46791 EndY=7.02031 EndZ=0
    g16: LineSegment StartX=-3 StartY=12.2464 StartZ=0 EndX=-2.4 EndY=12.2464 EndZ=0
    g17: LineSegment StartX=-2.4 StartY=12.2464 StartZ=0 EndX=-1 EndY=10.5779 EndZ=0
    g18: LineSegment StartX=1 StartY=10.5779 StartZ=0 EndX=2.4 EndY=12.2464 EndZ=0
    g19: LineSegment StartX=2.4 StartY=12.2464 StartZ=0 EndX=3 EndY=12.2464 EndZ=0
    g20: LineSegment StartX=2 StartY=-2.0466 StartZ=0 EndX=2 EndY=-1.2 EndZ=0
    g21: LineSegment StartX=2 StartY=-1.2 StartZ=0 EndX=-2 EndY=-1.2 EndZ=0
    g22: LineSegment StartX=-2 StartY=-1.2 StartZ=0 EndX=-2 EndY=-2.0466 EndZ=0
    g23: LineSegment StartX=-2 StartY=-2.0466 StartZ=0 EndX=-1.2 EndY=-3 EndZ=0
    g24: LineSegment StartX=-1.2 StartY=-3 StartZ=0 EndX=-7.2 EndY=-3 EndZ=0
    g25: LineSegment StartX=7.2 StartY=-3 StartZ=0 EndX=1.2 EndY=-3 EndZ=0
    g26: LineSegment StartX=1.2 StartY=-3 StartZ=0 EndX=2 EndY=-2.0466 EndZ=0
  constraints (77):
    c: Coincident(g0,g1)
    c: Coincident(g1,g2)
    c: PointOnObject(g2,g-1)
    c: Vertical(g2)
    c: Coincident(g2,g3)
    c: PointOnObject(g3,g-1)
    c: Coincident(g3,g4)
    c: Vertical(g4)
    c: Coincident(g4,g5)
    c: Coincident(g5,g6)
    c: Vertical(g6)
    c: Coincident(g6,g18)
    c: Coincident(g19,g7)
    c: Vertical(g7)
    c: Coincident(g7,g8)
    c: Coincident(g8,g9)
    c: Vertical(g9)
    c: Coincident(g9,g25)
    c: Vertical(g10)
    c: Coincident(g10,g11)
    c: Coincident(g11,g12)
    c: Vertical(g12)
    c: Coincident(g12,g16)
    c: Coincident(g17,g0)
    c: Vertical(g0)
    c: Coincident(g13,g11)
    c: PointOnObject(g13,g1)
    c: Coincident(g14,g3)
    c: Vertical(g14)
    c: Coincident(g15,g7)
    c: PointOnObject(g15,g5)
    c: Symmetric(g0,g6,g-2)
    c: Symmetric(g4,g1,g-2)
    c: Parallel(g1,g11)
    c: Parallel(g5,g8)
    c: Perpendicular(g1,g13)
    c: Perpendicular(g5,g15)
    c: Equal(g0,g6)
    c: DistanceX(g3,g3) = 12.2
    c: DistanceX(g10,g25) = 14.4
    c: DistanceY(g4,g4) = 1.5
    c: DistanceY(g14,g14) = 3
    c: Angle(g5,g3) = 0.872665
    c: DistanceY(g6,g6) = 3
    c: Equal(g13,g15)
    c: DistanceX(g18,g19) = 2
    c: Symmetric(g9,g10,g-2)
    c: Coincident(g16,g17)
    c: Horizontal(g16)
    c: Coincident(g18,g19)
    c: Horizontal(g19)
    c: Symmetric(g16,g18,g-2)
    c: Equal(g16,g19)
    c: Distance(g15) = 2
    c: DistanceX(g0,g5) = 2
    c: DistanceX(g19,g19) = 0.6
    c: Parallel(g1,g18)
    c: Coincident(g22,g23)
    c: Coincident(g26,g20)
    c: Coincident(g20,g21)
    c: Coincident(g21,g22)
    c: Coincident(g23,g24)
    c: Coincident(g25,g26)
    c: PointOnObject(g14,g25)
    c: Equal(g26,g23)
    c: Horizontal(g25)
    c: DistanceX(g23,g25) = 2.4
    c: Horizontal(g21)
    c: Equal(g20,g22)
    c: Vertical(g22)
    c: Vertical(g20)
    c: Angle(g23,g24) = 0.872665
    c: DistanceY(g25,g20) = 1.8
    c: DistanceX(g21,g21) = 4
    c: Coincident(g24,g10)
    c: Horizontal(g24)
    c: Equal(g24,g25)
FEATURE [PartDesign::Pad] Pad007
  Direction = (1,0,0)
  Length = 180
  Length2 = 10
  Placement = pos=(0,0,0) rot=(0.57735,0.57735,0.57735;2.0944rad)
  Profile = -> Sketch016
  ReferenceAxis = -> Sketch016 [N_Axis]
  Suppressed = false
  Type = 0
FEATURE [Sketcher::SketchObject] Sketch017
  AttachmentSupport = -> [XZ_Plane008]
  FullyConstrained = true
  MapMode = 5
  Placement = pos=(0,0,0) rot=(1,0,0;1.5708rad)
  sketch-geometry (20):
    g0: ArcOfCircle CenterX=52.5 CenterY=0 CenterZ=0 NormalX=0 NormalY=0 NormalZ=1 AngleXU=0 Radius=3.15 StartAngle=5.20871 EndAngle=10.4993
    g1: ArcOfCircle CenterX=52.5 CenterY=0 CenterZ=0 NormalX=0 NormalY=0 NormalZ=1 AngleXU=0 Radius=5 StartAngle=5.31721 EndAngle=6.28319
    g2: ArcOfCircle CenterX=52.5 CenterY=0 CenterZ=0 NormalX=0 NormalY=0 NormalZ=1 AngleXU=0 Radius=5 StartAngle=3.14159 EndAngle=4.10757
    g3: LineSegment StartX=51 StartY=-2.76993 StartZ=0 EndX=49.6569 EndY=-4.11301 EndZ=0
    g4: LineSegment StartX=54 StartY=-2.76993 StartZ=0 EndX=55.3431 EndY=-4.11301 EndZ=0
    g5: LineSegment StartX=52.5 StartY=0 StartZ=0 EndX=52.5 EndY=-1.26993 EndZ=0
    g6: ArcOfCircle CenterX=-52.5 CenterY=0 CenterZ=0 NormalX=0 NormalY=0 NormalZ=1 AngleXU=0 Radius=3.15 StartAngle=5.20871 EndAngle=10.4993
    g7: ArcOfCircle CenterX=-52.5 CenterY=0 CenterZ=0 NormalX=0 NormalY=0 NormalZ=1 AngleXU=0 Radius=5 StartAngle=3.14159 EndAngle=4.10757
    g8: ArcOfCircle CenterX=-52.5 CenterY=0 CenterZ=0 NormalX=0 NormalY=0 NormalZ=1 AngleXU=0 Radius=5 StartAngle=5.31721 EndAngle=6.28319
    g9: LineSegment StartX=-51 StartY=-2.76993 StartZ=0 EndX=-49.6569 EndY=-4.11301 EndZ=0
    g10: LineSegment StartX=-54 StartY=-2.76993 StartZ=0 EndX=-55.3431 EndY=-4.11301 EndZ=0
    g11: LineSegment StartX=-52.5 StartY=0 StartZ=0 EndX=-52.5 EndY=-1.26993 EndZ=0
    g12: LineSegment StartX=-57.5 StartY=6e-16 StartZ=0 EndX=-57.5 EndY=7 EndZ=0
    g13: LineSegment StartX=-57.5 StartY=7 StartZ=0 EndX=-47.5 EndY=7 EndZ=0
    g14: LineSegment StartX=-47.5 StartY=7 StartZ=0 EndX=-47.5 EndY=4 EndZ=0
    g15: LineSegment StartX=-47.5 StartY=4 StartZ=0 EndX=47.5 EndY=4 EndZ=0
    g16: LineSegment StartX=47.5 StartY=4 StartZ=0 EndX=47.5 EndY=7 EndZ=0
    g17: LineSegment StartX=47.5 StartY=7 StartZ=0 EndX=57.5 EndY=7 EndZ=0
    g18: LineSegment StartX=57.5 StartY=7 StartZ=0 EndX=57.5 EndY=-9e-16 EndZ=0
    g19: LineSegment StartX=47.5 StartY=6e-16 StartZ=0 EndX=-47.5 EndY=-1.2e-15 EndZ=0
  constraints (58):
    c: Coincident(g3,g0)
    c: Coincident(g3,g2)
    c: Coincident(g4,g0)
    c: Coincident(g4,g1)
    c: Perpendicular(g3,g4)
    c: Coincident(g0,g2)
    c: Coincident(g0,g1)
    c: PointOnObject(g0,g-1)
    c: Coincident(g5,g0)
    c: Vertical(g5)
    c: Symmetric(g1,g2,g5)
    c: Horizontal(g0,g0)
    c: Diameter(g0) = 6.3
    c: Diameter(g1) = 10
    c: PointOnObject(g5,g4)
    c: DistanceX(g0,g0) = 3
    c: PointOnObject(g1,g-1)
    c: PointOnObject(g2,g-1)
    c: Coincident(g9,g6)
    c: Coincident(g9,g8)
    c: Coincident(g10,g6)
    c: Coincident(g10,g7)
    c: Perpendicular(g9,g10)
    c: Coincident(g6,g8)
    c: Coincident(g6,g7)
    c: Coincident(g11,g6)
    c: Vertical(g11)
    c: Symmetric(g7,g8,g11)
    c: PointOnObject(g11,g10)
    c: Equal(g6,g0)
    c: Equal(g7,g2)
    c: Horizontal(g0,g6)
    c: PointOnObject(g11,g9)
    c: Symmetric(g6,g0,g-2)
    c: DistanceX(g6,g0) = 105
    c: PointOnObject(g7,g-1)
    c: PointOnObject(g8,g-1)
    c: Tangent(g7,g12) = 1.5708
    c: Coincident(g12,g13)
    c: Horizontal(g13)
    c: Coincident(g13,g14)
    c: Vertical(g14)
    c: Coincident(g14,g15)
    c: Horizontal(g15)
    c: Coincident(g15,g16)
    c: Vertical(g16)
    c: Coincident(g16,g17)
    c: Horizontal(g17)
    c: Coincident(g17,g18)
    c: Coincident(g18,g1)
    c: Vertical(g18)
    c: Equal(g18,g12)
    c: Equal(g13,g17)
    c: DistanceY(g15) = 4
    c: DistanceY(g16,g16) = 3
    c: Vertical(g2,g15)
    c: Coincident(g19,g2)
    c: Coincident(g19,g8)
FEATURE [PartDesign::Pad] Pad008
  Direction = (0,-1,2e-16)
  Length = 14.6
  Length2 = 10
  Placement = pos=(0,0,0) rot=(1,0,0;1.5708rad)
  Profile = -> Sketch017
  ReferenceAxis = -> Sketch017 [N_Axis]
  Suppressed = false
  Type = 0
FEATURE [Sketcher::SketchObject] Sketch018
  AttachmentSupport = -> [YZ_Plane008]
  FullyConstrained = true
  MapMode = 5
  Placement = pos=(0,0,0) rot=(0.57735,0.57735,0.57735;2.0944rad)
  sketch-geometry (4):
    g0: LineSegment StartX=-12.5 StartY=1.8 StartZ=0 EndX=-12.5 EndY=0 EndZ=0
    g1: LineSegment StartX=-12.5 StartY=0 StartZ=0 EndX=0 EndY=0 EndZ=0
    g2: LineSegment StartX=0 StartY=0 StartZ=0 EndX=0 EndY=1.8 EndZ=0
    g3: LineSegment StartX=0 StartY=1.8 StartZ=0 EndX=-12.5 EndY=1.8 EndZ=0
  constraints (11):
    c: Coincident(g0,g1)
    c: Coincident(g1,g2)
    c: Coincident(g2,g3)
    c: Coincident(g3,g0)
    c: Vertical(g0)
    c: Vertical(g2)
    c: Horizontal(g1)
    c: Horizontal(g3)
    c: Coincident(g1,g-1)
    c: DistanceX(g1,g1) = 12.5
    c: DistanceY(g2,g2) = 1.8
FEATURE [PartDesign::Pocket] Pocket007
  BaseFeature = -> Pad008
  Direction = (-1,0,0)
  Length = 95
  Length2 = 5
  Midplane = true
  Placement = pos=(0,0,0) rot=(1,0,0;1.5708rad)
  Profile = -> Sketch018
  ReferenceAxis = -> Sketch018 [N_Axis]
  Suppressed = false
  Type = 0
FEATURE [Sketcher::SketchObject] Sketch019
  AttachmentSupport = -> [YZ_Plane008]
  FullyConstrained = true
  MapMode = 5
  Placement = pos=(0,0,0) rot=(0.57735,0.57735,0.57735;2.0944rad)
  sketch-geometry (12):
    g0: LineSegment StartX=-14.6 StartY=8 StartZ=0 EndX=-14.6 EndY=4 EndZ=0
    g1: LineSegment StartX=-14.6 StartY=4 StartZ=0 EndX=-8.4 EndY=4 EndZ=0
    g2: LineSegment StartX=-8.4 StartY=4 StartZ=0 EndX=-8.4 EndY=4.8 EndZ=0
    g3: LineSegment StartX=-8.4 StartY=4.8 StartZ=0 EndX=-9.1 EndY=4.8 EndZ=0
    g4: LineSegment StartX=-9.1 StartY=4.8 StartZ=0 EndX=-9.1 EndY=5.5 EndZ=0
    g5: LineSegment StartX=-9.1 StartY=5.5 StartZ=0 EndX=-5.5 EndY=5.5 EndZ=0
    g6: LineSegment StartX=-5.5 StartY=5.5 StartZ=0 EndX=-5.5 EndY=4.8 EndZ=0
    g7: LineSegment StartX=-5.5 StartY=4.8 StartZ=0 EndX=-6.2 EndY=4.8 EndZ=0
    g8: LineSegment StartX=-6.2 StartY=4.8 StartZ=0 EndX=-6.2 EndY=4 EndZ=0
    g9: LineSegment StartX=-6.2 StartY=4 StartZ=0 EndX=0 EndY=4 EndZ=0
    g10: LineSegment StartX=0 StartY=4 StartZ=0 EndX=0 EndY=8 EndZ=0
    g11: LineSegment StartX=0 StartY=8 StartZ=0 EndX=-14.6 EndY=8 EndZ=0
  constraints (36):
    c: Vertical(g0)
    c: Horizontal(g1)
    c: Coincident(g1,g2)
    c: Vertical(g2)
    c: Coincident(g2,g3)
    c: Horizontal(g3)
    c: Coincident(g3,g4)
    c: Vertical(g4)
    c: Coincident(g4,g5)
    c: Horizontal(g5)
    c: Coincident(g5,g6)
    c: Vertical(g6)
    c: Coincident(g6,g7)
    c: Horizontal(g7)
    c: Coincident(g7,g8)
    c: Vertical(g8)
    c: Coincident(g8,g9)
    c: PointOnObject(g9,g-2)
    c: Horizontal(g9)
    c: Coincident(g9,g10)
    c: PointOnObject(g10,g-2)
    c: Coincident(g10,g11)
    c: Coincident(g11,g0)
    c: Horizontal(g11)
    c: DistanceY(g9) = 4
    c: Horizontal(g8,g1)
    c: Equal(g2,g8)
    c: Equal(g3,g7)
    c: DistanceX(g11,g11) = 14.6
    c: DistanceY(g10,g10) = 4
    c: DistanceY(g6,g6) = 0.7
    c: DistanceY(g8,g8) = 0.8
    c: Coincident(g1,g0)
    c: Equal(g9,g1)
    c: DistanceX(g5,g5) = 3.6
    c: DistanceX(g3,g3) = 0.7
FEATURE [PartDesign::Pocket] Pocket008
  BaseFeature = -> Pocket007
  Direction = (-1,-1e-16,1e-16)
  Length = 5
  Length2 = 5
  Midplane = true
  Placement = pos=(0,0,0) rot=(1,0,0;1.5708rad)
  Profile = -> Sketch019
  ReferenceAxis = -> Sketch019 [N_Axis]
  Suppressed = false
  Type = 1
FEATURE [PartDesign::Body] Body008  label="BottomLink"
  AllowCompound = false
  Group = -> [Sketch017,Pad008,Sketch018,Pocket007,Sketch019,Pocket008]
  Origin = -> Origin008
  Placement = pos=(-52.5,-10.7,0) rot=(0,0,1;0rad)
  Tip = -> Pocket008
FEATURE [PartDesign::FeaturePython] InvoluteGear002  label="M2.5-24T001"  # WARN: FeaturePython — macro-defined, semantics opaque (R4)
  AttacherType = Attacher::AttachEngine3D
  Placement = pos=(0,0,0) rot=(1,0,0;1.5708rad)
  Suppressed = false
  angular_backlash = 0.190986
  backlash = 0.1
  beta = 0
  clearance = 0.25
  da = 65
  df = 53.75
  double_helix = false
  dw = 60
  head = 0
  head_fillet = 0
  height = 5
  module = 2.5
  numpoints = 6
  pressure_angle = 20
  properties_from_tool = false
  reversed_backlash = false
  root_fillet = 0
  shift = 0
  simple = false
  teeth = 24
  transverse_pitch = 7.85398
  undercut = false
  version = 0.0.4
  expr: angular_backlash = backlash / dw * 360 ° / pi
  expr: dw = teeth * module
FEATURE [Sketcher::SketchObject] Sketch021
  AttachmentSupport = -> [XZ_Plane009]
  FullyConstrained = true
  MapMode = 5
  Placement = pos=(0,0,0) rot=(1,0,0;1.5708rad)
  sketch-geometry (14):
    g0: ArcOfCircle CenterX=0 CenterY=0 CenterZ=0 NormalX=0 NormalY=0 NormalZ=1 AngleXU=0 Radius=7 StartAngle=0.608246 EndAngle=1.48615
    g1: ArcOfCircle CenterX=0 CenterY=0 CenterZ=0 NormalX=0 NormalY=0 NormalZ=1 AngleXU=0 Radius=21.5 StartAngle=0.187137 EndAngle=1.90726
    g2: LineSegment StartX=21.1246 StartY=4 StartZ=0 EndX=5.74456 EndY=4 EndZ=0
    g3: LineSegment StartX=0.59182 StartY=6.97494 StartZ=0 EndX=-7.09821 EndY=20.2945 EndZ=0
    g4: LineSegment StartX=0 StartY=0 StartZ=0 EndX=-10.5623 EndY=18.2945 EndZ=0
    g5: LineSegment StartX=-10.5623 StartY=18.2945 StartZ=0 EndX=-7.09821 EndY=20.2945 EndZ=0
    g6: LineSegment StartX=21.1246 StartY=4 StartZ=0 EndX=21.1246 EndY=0 EndZ=0
    g7: LineSegment StartX=0 StartY=-4.15692 StartZ=0 EndX=3.6 EndY=-2.07846 EndZ=0
    g8: LineSegment StartX=3.6 StartY=-2.07846 StartZ=0 EndX=3.6 EndY=2.07846 EndZ=0
    g9: LineSegment StartX=3.6 StartY=2.07846 StartZ=0 EndX=4e-16 EndY=4.15692 EndZ=0
    g10: LineSegment StartX=4e-16 StartY=4.15692 StartZ=0 EndX=-3.6 EndY=2.07846 EndZ=0
    g11: LineSegment StartX=-3.6 StartY=2.07846 StartZ=0 EndX=-3.6 EndY=-2.07846 EndZ=0
    g12: LineSegment StartX=-3.6 StartY=-2.07846 StartZ=0 EndX=0 EndY=-4.15692 EndZ=0
    g13: Circle CenterX=0 CenterY=0 CenterZ=0 NormalX=0 NormalY=0 NormalZ=1 AngleXU=0 Radius=4.15692
  constraints (37):
    c: Coincident(g0,g-1)
    c: Coincident(g1,g0)
    c: Coincident(g2,g1)
    c: Coincident(g2,g0)
    c: Coincident(g3,g0)
    c: Coincident(g3,g1)
    c: Coincident(g4,g0)
    c: Coincident(g5,g4)
    c: Coincident(g5,g1)
    c: Parallel(g4,g3)
    c: Perpendicular(g4,g5)
    c: Angle(g-1,g4) = 2.0944
    c: Horizontal(g2)
    c: Coincident(g6,g1)
    c: PointOnObject(g6,g-1)
    c: Vertical(g6)
    c: Equal(g6,g5)
    c: Diameter(g0) = 14
    c: Diameter(g1) = 43
    c: DistanceY(g6,g6) = 4
    c: Coincident(g7,g8)
    c: Coincident(g8,g9)
    c: Coincident(g9,g10)
    c: Coincident(g10,g11)
    c: Coincident(g11,g12)
    c: Coincident(g12,g7)
    c: Equal(g7, g8-g12) x5
    c: PointOnObject(g7,g13)
    c: PointOnObject(g8,g13)
    c: PointOnObject(g9,g13)
    c: PointOnObject(g10,g13)
    c: PointOnObject(g11,g13)
    c: PointOnObject(g12,g13)
    c: Coincident(g13,g0)
    c: PointOnObject(g12,g-2)
    c: DistanceX(g11,g7) = 7.2
    c: Diameter(g13) = 8.31384
FEATURE [PartDesign::Pocket] Pocket010  label="120deg-sector001"
  BaseFeature = -> InvoluteGear002
  Direction = (0,1,-2e-16)
  Length = 5
  Length2 = 5
  Midplane = true
  Placement = pos=(0,0,0) rot=(1,0,0;1.5708rad)
  Profile = -> Sketch021
  ReferenceAxis = -> Sketch021 [N_Axis]
  Refine = true
  Suppressed = false
  Type = 1
FEATURE [PartDesign::PolarPattern] PolarPattern001
  Angle = 360
  Axis = -> Sketch021 [N_Axis]
  BaseFeature = -> Pocket010
  Mode = 0
  Occurrences = 3
  Offset = 120
  Originals = -> [Pocket010]
  Placement = pos=(0,0,0) rot=(1,0,0;1.5708rad)
  Refine = true
  Suppressed = false
  TransformMode = 0
FEATURE [PartDesign::Body] Body009  label="M2.5-24t-Drive"
  AllowCompound = false
  Group = -> [InvoluteGear002,Sketch021,Pocket010,PolarPattern001]
  Origin = -> Origin009
  Placement = pos=(60,0,0) rot=(0,1,0;0.087266rad)
  Tip = -> PolarPattern001
FEATURE [Sketcher::SketchObject] Sketch022
  AttachmentSupport = -> [XZ_Plane010]
  FullyConstrained = true
  MapMode = 5
  Placement = pos=(0,0,0) rot=(1,0,0;1.5708rad)
  sketch-geometry (8):
    g0: LineSegment StartX=0 StartY=-4.09919 StartZ=0 EndX=3.55 EndY=-2.04959 EndZ=0
    g1: LineSegment StartX=3.55 StartY=-2.04959 StartZ=0 EndX=3.55 EndY=2.04959 EndZ=0
    g2: LineSegment StartX=3.55 StartY=2.04959 StartZ=0 EndX=4e-16 EndY=4.09919 EndZ=0
    g3: LineSegment StartX=4e-16 StartY=4.09919 StartZ=0 EndX=-3.55 EndY=2.04959 EndZ=0
    g4: LineSegment StartX=-3.55 StartY=2.04959 StartZ=0 EndX=-3.55 EndY=-2.04959 EndZ=0
    g5: LineSegment StartX=-3.55 StartY=-2.04959 StartZ=0 EndX=0 EndY=-4.09919 EndZ=0
    g6: Circle CenterX=0 CenterY=0 CenterZ=0 NormalX=0 NormalY=0 NormalZ=1 AngleXU=0 Radius=4.09919
    g7: Circle CenterX=0 CenterY=0 CenterZ=0 NormalX=0 NormalY=0 NormalZ=1 AngleXU=0 Radius=7
  constraints (18):
    c: Coincident(g0,g1)
    c: Coincident(g1,g2)
    c: Coincident(g2,g3)
    c: Coincident(g3,g4)
    c: Coincident(g4,g5)
    c: Coincident(g5,g0)
    c: Equal(g0, g1-g5) x5
    c: PointOnObject(g0,g6)
    c: PointOnObject(g1,g6)
    c: PointOnObject(g2,g6)
    c: PointOnObject(g3,g6)
    c: PointOnObject(g4,g6)
    c: PointOnObject(g5,g6)
    c: Coincident(g6,g-1)
    c: DistanceX(g4,g0) = 7.1
    c: Coincident(g7,g6)
    c: Diameter(g7) = 14
    c: PointOnObject(g0,g-2)
FEATURE [PartDesign::Pad] Pad009
  Direction = (0,-1,2e-16)
  Length = 9
  Length2 = 10
  Placement = pos=(0,0,0) rot=(1,0,0;1.5708rad)
  Profile = -> Sketch022
  ReferenceAxis = -> Sketch022 [N_Axis]
  Suppressed = false
  Type = 0
FEATURE [Sketcher::SketchObject] Sketch023
  AttachmentSupport = -> [XY_Plane010]
  FullyConstrained = true
  MapMode = 5
  sketch-geometry (4):
    g0: LineSegment StartX=5 StartY=-12 StartZ=0 EndX=15 EndY=-12 EndZ=0
    g1: LineSegment StartX=15 StartY=-12 StartZ=0 EndX=15 EndY=-2 EndZ=0
    g2: LineSegment StartX=15 StartY=-2 StartZ=0 EndX=5 EndY=-2 EndZ=0
    g3: LineSegment StartX=5 StartY=-2 StartZ=0 EndX=5 EndY=-12 EndZ=0
  constraints (12):
    c: Coincident(g0,g1)
    c: Coincident(g1,g2)
    c: Coincident(g2,g3)
    c: Coincident(g3,g0)
    c: Horizontal(g0)
    c: Horizontal(g2)
    c: Vertical(g1)
    c: Vertical(g3)
    c: DistanceX(g2) = 5
    c: DistanceY(g2) = -2
    c: DistanceY(g3,g3) = 10
    c: Equal(g3,g0)
FEATURE [PartDesign::Groove] Groove001
  Angle = 360
  Angle2 = 60
  Axis = (0,1,0)
  Base = (0,0,0)
  BaseFeature = -> Pad009
  Placement = pos=(0,0,0) rot=(1,0,0;1.5708rad)
  Profile = -> Sketch023
  ReferenceAxis = -> Sketch023 [V_Axis]
  Suppressed = false
  Type = 0
FEATURE [PartDesign::Body] Body010  label="DriveBushing"
  AllowCompound = false
  Group = -> [Sketch022,Pad009,Sketch023,Groove001]
  Origin = -> Origin010
  Placement = pos=(60,-5,0) rot=(0,0,1;0rad)
  Tip = -> Groove001
FEATURE [Sketcher::SketchObject] Sketch024
  AttachmentSupport = -> [XZ_Plane011]
  FullyConstrained = true
  MapMode = 5
  Placement = pos=(0,0,0) rot=(1,0,0;1.5708rad)
  sketch-geometry (87):
    g0: LineSegment StartX=-30 StartY=-35 StartZ=0 EndX=-30 EndY=-25 EndZ=0
    g1: LineSegment StartX=-30 StartY=-25 StartZ=0 EndX=-3.66638 EndY=3.39966 EndZ=0
    g2: ArcOfCircle CenterX=0 CenterY=0 CenterZ=0 NormalX=0 NormalY=0 NormalZ=1 AngleXU=0 Radius=5 StartAngle=0.635121 EndAngle=2.39392
    g3: ArcOfCircle CenterX=60 CenterY=0 CenterZ=0 NormalX=0 NormalY=0 NormalZ=1 AngleXU=0 Radius=8 StartAngle=0.669738 EndAngle=2.56349
    g4: LineSegment StartX=66.2719 StartY=4.96625 StartZ=0 EndX=90 EndY=-25 EndZ=0
    g5: LineSegment StartX=90 StartY=-25 StartZ=0 EndX=90 EndY=-35 EndZ=0
    g6: LineSegment StartX=90 StartY=-35 StartZ=0 EndX=81.7609 EndY=-35 EndZ=0
    g7: ArcOfCircle CenterX=28.175 CenterY=20.7646 CenterZ=0 NormalX=0 NormalY=0 NormalZ=1 AngleXU=0 Radius=30 StartAngle=3.77671 EndAngle=5.70508
    g8: Circle CenterX=0 CenterY=0 CenterZ=0 NormalX=0 NormalY=0 NormalZ=1 AngleXU=0 Radius=2.7
    g9: Circle CenterX=60 CenterY=0 CenterZ=0 NormalX=0 NormalY=0 NormalZ=1 AngleXU=0 Radius=5.2
    g10: LineSegment StartX=81.7609 StartY=-35 StartZ=0 EndX=83.5218 EndY=-31.95 EndZ=0
    g11: LineSegment StartX=83.5218 StartY=-31.95 StartZ=0 EndX=81.7609 EndY=-28.9 EndZ=0
    g12: LineSegment StartX=81.7609 StartY=-28.9 StartZ=0 EndX=78.2391 EndY=-28.9 EndZ=0
    g13: LineSegment StartX=78.2391 StartY=-28.9 StartZ=0 EndX=76.4782 EndY=-31.95 EndZ=0
    g14: LineSegment StartX=76.4782 StartY=-31.95 StartZ=0 EndX=78.2391 EndY=-35 EndZ=0
    g15: LineSegment StartX=78.2391 StartY=-35 StartZ=0 EndX=81.7609 EndY=-35 EndZ=0
    g16: Circle CenterX=80 CenterY=-31.95 CenterZ=0 NormalX=0 NormalY=0 NormalZ=1 AngleXU=0 Radius=3.52184
    g17: LineSegment StartX=31.7609 StartY=-35 StartZ=0 EndX=33.5218 EndY=-31.95 EndZ=0
    g18: LineSegment StartX=33.5218 StartY=-31.95 StartZ=0 EndX=31.7609 EndY=-28.9 EndZ=0
    g19: LineSegment StartX=31.7609 StartY=-28.9 StartZ=0 EndX=28.2391 EndY=-28.9 EndZ=0
    g20: LineSegment StartX=28.2391 StartY=-28.9 StartZ=0 EndX=26.4782 EndY=-31.95 EndZ=0
    g21: LineSegment StartX=26.4782 StartY=-31.95 StartZ=0 EndX=28.2391 EndY=-35 EndZ=0
    g22: LineSegment StartX=28.2391 StartY=-35 StartZ=0 EndX=31.7609 EndY=-35 EndZ=0
    g23: Circle CenterX=30 CenterY=-31.95 CenterZ=0 NormalX=0 NormalY=0 NormalZ=1 AngleXU=0 Radius=3.52184
    g24: LineSegment StartX=-21.7609 StartY=-35 StartZ=0 EndX=-30 EndY=-35 EndZ=0
    g25: LineSegment StartX=78.2391 StartY=-35 StartZ=0 EndX=31.7609 EndY=-35 EndZ=0
    g26: LineSegment StartX=28.2391 StartY=-35 StartZ=0 EndX=-18.2391 EndY=-35 EndZ=0
    g27: LineSegment StartX=78.716 StartY=-20.4147 StartZ=0 EndX=66.3765 EndY=-4.83115 EndZ=0
    g28: ArcOfCircle CenterX=60 CenterY=0 CenterZ=0 NormalX=0 NormalY=0 NormalZ=1 AngleXU=0 Radius=8 StartAngle=3.77812 EndAngle=5.63481
    g29: LineSegment StartX=41.1694 StartY=-28.9 StartZ=0 EndX=70.2307 EndY=-28.9 EndZ=0
    g30: LineSegment StartX=70.2307 StartY=-28.9 StartZ=0 EndX=78.716 EndY=-20.4147 EndZ=0
    g31: ArcOfCircle CenterX=0 CenterY=0 CenterZ=0 NormalX=0 NormalY=0 NormalZ=1 AngleXU=0 Radius=5 StartAngle=4.16608 EndAngle=5.2157
    g32: LineSegment StartX=-2.59769 StartY=-4.27224 StartZ=0 EndX=-17.5658 EndY=-20.4147 EndZ=0
    g33: LineSegment StartX=-17.5658 StartY=-20.4147 StartZ=0 EndX=-9.08055 EndY=-28.9 EndZ=0
    g34: LineSegment StartX=-9.08055 StartY=-28.9 StartZ=0 EndX=19.3431 EndY=-28.9 EndZ=0
    g35: ArcOfCircle CenterX=28.175 CenterY=20.7646 CenterZ=0 NormalX=0 NormalY=0 NormalZ=1 AngleXU=0 Radius=36 StartAngle=3.91484 EndAngle=4.62408
    g36: ArcOfCircle CenterX=28.175 CenterY=20.7646 CenterZ=0 NormalX=0 NormalY=0 NormalZ=1 AngleXU=0 Radius=36 StartAngle=4.90313 EndAngle=5.49527
    g37: LineSegment StartX=-2.59769 StartY=-4.27224 StartZ=0 EndX=-6.99735 EndY=-0.192648 EndZ=0
    g38: LineSegment StartX=66.3765 StartY=-4.83115 StartZ=0 EndX=71.0804 EndY=-1.10647 EndZ=0
    g39: LineSegment StartX=19.3431 StartY=-28.9 StartZ=0 EndX=25 EndY=-23.2431 EndZ=0
    g40: LineSegment StartX=25 StartY=-23.2431 StartZ=0 EndX=25 EndY=-15.0951 EndZ=0
    g41: LineSegment StartX=35 StartY=-14.5825 StartZ=0 EndX=35 EndY=-22.7306 EndZ=0
    g42: LineSegment StartX=35 StartY=-22.7306 StartZ=0 EndX=41.1694 EndY=-28.9 EndZ=0
    g43: Circle CenterX=30 CenterY=-14.5 CenterZ=0 NormalX=0 NormalY=0 NormalZ=1 AngleXU=0 Radius=3.1
    g44: LineSegment StartX=-30 StartY=-25 StartZ=0 EndX=-33.9 EndY=-28.9 EndZ=0
    g45: LineSegment StartX=-33.9 StartY=-28.9 StartZ=0 EndX=-39.2437 EndY=-28.9 EndZ=0
    g46: LineSegment StartX=-39.2437 StartY=-28.9 StartZ=0 EndX=-57.8988 EndY=-9.53142 EndZ=0
    g47: ArcOfCircle CenterX=-61.5 CenterY=-13 CenterZ=0 NormalX=0 NormalY=0 NormalZ=1 AngleXU=0 Radius=5 StartAngle=0.766636 EndAngle=2.37496
    g48: LineSegment StartX=-65.1012 StartY=-9.53142 StartZ=0 EndX=-80 EndY=-25 EndZ=0
    g49: LineSegment StartX=-80 StartY=-25 StartZ=0 EndX=-80 EndY=-35 EndZ=0
    g50: LineSegment StartX=-80 StartY=-35 StartZ=0 EndX=-71.7609 EndY=-35 EndZ=0
    g51: LineSegment StartX=-18.2391 StartY=-35 StartZ=0 EndX=-16.4782 EndY=-31.95 EndZ=0
    g52: LineSegment StartX=-16.4782 StartY=-31.95 StartZ=0 EndX=-18.2391 EndY=-28.9 EndZ=0
    g53: LineSegment StartX=-18.2391 StartY=-28.9 StartZ=0 EndX=-21.7609 EndY=-28.9 EndZ=0
    g54: LineSegment StartX=-21.7609 StartY=-28.9 StartZ=0 EndX=-23.5218 EndY=-31.95 EndZ=0
    g55: LineSegment StartX=-23.5218 StartY=-31.95 StartZ=0 EndX=-21.7609 EndY=-35 EndZ=0
    g56: LineSegment StartX=-21.7609 StartY=-35 StartZ=0 EndX=-18.2391 EndY=-35 EndZ=0
    g57: Circle CenterX=-20 CenterY=-31.95 CenterZ=0 NormalX=0 NormalY=0 NormalZ=1 AngleXU=0 Radius=3.52184
    g58: LineSegment StartX=-68.2391 StartY=-35 StartZ=0 EndX=-66.4782 EndY=-31.95 EndZ=0
    g59: LineSegment StartX=-66.4782 StartY=-31.95 StartZ=0 EndX=-68.2391 EndY=-28.9 EndZ=0
    g60: LineSegment StartX=-68.2391 StartY=-28.9 StartZ=0 EndX=-71.7609 EndY=-28.9 EndZ=0
    g61: LineSegment StartX=-71.7609 StartY=-28.9 StartZ=0 EndX=-73.5218 EndY=-31.95 EndZ=0
    g62: LineSegment StartX=-73.5218 StartY=-31.95 StartZ=0 EndX=-71.7609 EndY=-35 EndZ=0
    g63: LineSegment StartX=-71.7609 StartY=-35 StartZ=0 EndX=-68.2391 EndY=-35 EndZ=0
    g64: Circle CenterX=-70 CenterY=-31.95 CenterZ=0 NormalX=0 NormalY=0 NormalZ=1 AngleXU=0 Radius=3.52184
    g65: LineSegment StartX=-21.7609 StartY=-35 StartZ=0 EndX=-68.2391 EndY=-35 EndZ=0
    g66: LineSegment StartX=-71.9985 StartY=-23.9 StartZ=0 EndX=-65.9985 EndY=-23.9 EndZ=0
    g67: LineSegment StartX=-46.1857 StartY=-28.9 StartZ=0 EndX=-58.0314 EndY=-16.6012 EndZ=0
    g68: ArcOfCircle CenterX=-61.5 CenterY=-13 CenterZ=0 NormalX=0 NormalY=0 NormalZ=1 AngleXU=0 Radius=5 StartAngle=3.94575 EndAngle=5.47902
    g69: LineSegment StartX=-64.9686 StartY=-16.6012 StartZ=0 EndX=-71.9985 EndY=-23.9 EndZ=0
    g70: Circle CenterX=-61.5 CenterY=-13 CenterZ=0 NormalX=0 NormalY=0 NormalZ=1 AngleXU=0 Radius=2.7
    g71: LineSegment StartX=-65.9985 StartY=-23.9 StartZ=0 EndX=-60.9985 EndY=-28.9 EndZ=0
    g72: LineSegment StartX=-60.9985 StartY=-28.9 StartZ=0 EndX=-46.1857 EndY=-28.9 EndZ=0
    g73: LineSegment StartX=-61.5 StartY=-13 StartZ=0 EndX=-61.5 EndY=-8 EndZ=0
    g74: GeomPoint X=-51.0015 Y=-23.9 Z=0
    g75: Circle CenterX=67.5 CenterY=38 CenterZ=0 NormalX=0 NormalY=0 NormalZ=1 AngleXU=0 Radius=2.7
    g76: ArcOfCircle CenterX=67.5 CenterY=38 CenterZ=0 NormalX=0 NormalY=0 NormalZ=1 AngleXU=0 Radius=5 StartAngle=5.88726 EndAngle=8.36672
    g77: LineSegment StartX=-2.45284 StartY=4.35701 StartZ=0 EndX=65.0472 EndY=42.357 EndZ=0
    g78: LineSegment StartX=90 StartY=-25 StartZ=0 EndX=64.514 EndY=7.18625 EndZ=0
    g79: LineSegment StartX=63.4048 StartY=15.2378 StartZ=0 EndX=72.1132 EndY=36.0717 EndZ=0
    g80: LineSegment StartX=63.143 StartY=35.5472 StartZ=0 EndX=4.3954 EndY=2.47445 EndZ=0
    g81: ArcOfCircle CenterX=67.5 CenterY=38 CenterZ=0 NormalX=0 NormalY=0 NormalZ=1 AngleXU=0 Radius=5 StartAngle=3.65433 EndAngle=4.31647
    g82: LineSegment StartX=65.5717 StartY=33.3868 StartZ=0 EndX=53.9811 EndY=5.65773 EndZ=0
    g83: ArcOfCircle CenterX=28.175 CenterY=20.7646 CenterZ=0 NormalX=0 NormalY=0 NormalZ=1 AngleXU=0 Radius=30 StartAngle=3.79724 EndAngle=5.70508
    g84: ArcOfCircle CenterX=46.6 CenterY=8.743 CenterZ=0 NormalX=0 NormalY=0 NormalZ=1 AngleXU=0 Radius=8 StartAngle=5.70508 EndAngle=5.88726
    g85: ArcOfCircle CenterX=70.7859 CenterY=12.1525 CenterZ=0 NormalX=0 NormalY=0 NormalZ=1 AngleXU=0 Radius=8 StartAngle=2.74567 EndAngle=3.81133
    g86: ArcOfCircle CenterX=-2.21463e-05 CenterY=2.80724e-05 CenterZ=0 NormalX=0 NormalY=0 NormalZ=1 AngleXU=0 Radius=4.99996 StartAngle=2.08354 EndAngle=2.39393
  constraints (224):
    c: Vertical(g0)
    c: Coincident(g0,g1)
    c: Tangent(g1,g2) = 1.5708
    c: Tangent(g3,g4) = 1.5708
    c: Coincident(g4,g5)
    c: Vertical(g5)
    c: Coincident(g5,g6)
    c: Coincident(g24,g0)
    c: Horizontal(g6)
    c: Coincident(g2,g-1)
    c: Diameter(g2) = 10
    c: PointOnObject(g3,g-1)
    c: DistanceX(g3) = 60
    c: Tangent(g7,g2) = 1.5708
    c: Tangent(g7,g3) = 1.5708
    c: Coincident(g8,g2)
    c: Diameter(g8) = 5.4
    c: Coincident(g9,g3)
    c: Diameter(g9) = 10.4
    c: Diameter(g3) = 16
    c: DistanceY(g5,g5) = 10
    c: Equal(g5,g0)
    c: DistanceY(g5) = -35
    c: DistanceX(g0) = -30
    c: DistanceX(g5) = 90
    c: Radius(g7) = 30
    c: PointOnObject(g26,g6)
    c: Coincident(g10,g11)
    c: Coincident(g11,g12)
    c: Coincident(g12,g13)
    c: Coincident(g13,g14)
    c: Coincident(g14,g15)
    c: Coincident(g15,g10)
    c: Equal(g10, g11-g15) x5
    c: PointOnObject(g10,g16)
    c: PointOnObject(g11,g16)
    c: PointOnObject(g12,g16)
    c: PointOnObject(g13,g16)
    c: PointOnObject(g14,g16)
    c: PointOnObject(g15,g16)
    c: Coincident(g17,g18)
    c: Coincident(g18,g19)
    c: Coincident(g19,g20)
    c: Coincident(g20,g21)
    c: Coincident(g21,g22)
    c: Coincident(g22,g17)
    c: Equal(g17, g18-g22) x5
    c: PointOnObject(g17,g23)
    c: PointOnObject(g18,g23)
    c: PointOnObject(g19,g23)
    c: PointOnObject(g20,g23)
    c: PointOnObject(g21,g23)
    c: PointOnObject(g22,g23)
    c: Horizontal(g22)
    c: Equal(g23,g16)
    c: DistanceX(g16,g5) = 10
    c: Coincident(g6,g10)
    c: Horizontal(g15)
    c: Coincident(g14,g25)
    c: Coincident(g25,g17)
    c: Horizontal(g25)
    c: Coincident(g21,g26)
    c: Horizontal(g24)
    c: Equal(g26,g25)
    c: Coincident(g42,g29)
    c: Horizontal(g29)
    c: Coincident(g29,g30)
    c: Coincident(g30,g27)
    c: Coincident(g31,g32)
    c: Coincident(g32,g33)
    c: Coincident(g33,g34)
    c: Coincident(g34,g39)
    c: Horizontal(g34)
    c: Parallel(g32,g1)
    c: Coincident(g31,g2)
    c: Equal(g2,g31)
    c: Coincident(g35,g7)
    c: Coincident(g35,g31)
    c: Coincident(g36,g7)
    c: Coincident(g36,g28)
    c: Coincident(g41,g36)
    c: Coincident(g40,g35)
    c: Equal(g35,g36)
    c: Coincident(g31,g37)
    c: PointOnObject(g37,g1)
    c: Perpendicular(g1,g37)
    c: Coincident(g27,g38)
    c: PointOnObject(g38,g4)
    c: Perpendicular(g4,g38)
    c: Equal(g37,g38)
    c: Distance(g38) = 6
    c: Parallel(g27,g4)
    c: Horizontal(g39,g42)
    c: Horizontal(g42,g18)
    c: Radius(g36) = 36
    c: Coincident(g28,g3)
    c: Equal(g28,g3)
    c: Coincident(g39,g40)
    c: Coincident(g41,g42)
    c: Vertical(g40)
    c: Vertical(g41)
    c: DistanceX(g35,g36) = 10
    c: DistanceX(g23,g36) = 5
    c: Equal(g41,g40)
    c: Angle(g39,g34) = 2.35619
    c: Angle(g29,g42) = 2.35619
    c: Distance(g39) = 8
    c: Angle(g30,g29) = 2.35619
    c: Coincident(g27,g28)
    c: Distance(g30) = 12
    c: Angle(g34,g33) = 2.35619
    c: Equal(g33,g30)
    c: Diameter(g43) = 6.2
    c: Vertical(g43,g23)
    c: DistanceY(g21,g43) = 20.5
    c: Coincident(g0,g44)
    c: Coincident(g44,g45)
    c: Horizontal(g45)
    c: Coincident(g45,g46)
    c: Tangent(g46,g47) = -1.5708
    c: Tangent(g47,g48) = -1.5708
    c: Coincident(g48,g49)
    c: Vertical(g49)
    c: Coincident(g49,g50)
    c: Horizontal(g50)
    c: Coincident(g51,g52)
    c: Coincident(g52,g53)
    c: Coincident(g53,g54)
    c: Coincident(g54,g55)
    c: Coincident(g55,g56)
    c: Coincident(g56,g51)
    c: Equal(g51, g52-g56) x5
    c: PointOnObject(g51,g57)
    c: PointOnObject(g52,g57)
    c: PointOnObject(g53,g57)
    c: PointOnObject(g54,g57)
    c: PointOnObject(g55,g57)
    c: PointOnObject(g56,g57)
    c: DistanceY(g51,g52) = 6.1
    c: Horizontal(g56)
    c: Coincident(g58,g59)
    c: Coincident(g59,g60)
    c: Coincident(g60,g61)
    c: Coincident(g61,g62)
    c: Coincident(g62,g63)
    c: Coincident(g63,g58)
    c: Equal(g58, g59-g63) x5
    c: PointOnObject(g58,g64)
    c: PointOnObject(g59,g64)
    c: PointOnObject(g60,g64)
    c: PointOnObject(g61,g64)
    c: PointOnObject(g62,g64)
    c: PointOnObject(g63,g64)
    c: Horizontal(g63)
    c: Coincident(g51,g26)
    c: Coincident(g55,g24)
    c: DistanceX(g0,g57) = 10
    c: Equal(g64,g57)
    c: Coincident(g24,g65)
    c: Coincident(g65,g58)
    c: Horizontal(g65)
    c: Equal(g65,g26)
    c: Equal(g49,g5)
    c: Coincident(g50,g62)
    c: DistanceX(g49,g64) = 10
    c: DistanceY(g49,g47) = 22
    c: DistanceX(g47) = -61.5
    c: Equal(g47,g2)
    c: Parallel(g44,g39)
    c: Horizontal(g33,g52)
    c: Horizontal(g33,g44)
    c: Horizontal(g66)
    c: Coincident(g66,g71)
    c: Perpendicular(g67,g68) = 4.71239
    c: Coincident(g68,g69)
    c: Coincident(g66,g69)
    c: Parallel(g69,g48)
    c: Horizontal(g67,g45)
    c: Coincident(g68,g47)
    c: Equal(g68,g47)
    c: PointOnObject(g47,g69)
    c: Coincident(g72,g67)
    c: DistanceY(g60,g66) = 5
    c: Coincident(g70,g47)
    c: Equal(g70,g8)
    c: Parallel(g67,g46)
    c: Coincident(g71,g72)
    c: Parallel(g71,g33)
    c: Horizontal(g72)
    c: DistanceX(g66,g66) = 6
    c: Coincident(g73,g47)
    c: PointOnObject(g73,g47)
    c: Vertical(g73)
    c: PointOnObject(g74,g67)
    c: Symmetric(g66,g74,g73)
    c: DistanceX(g75) = 67.5
    c: DistanceY(g75) = 38
    c: Equal(g75,g8)
    c: Coincident(g76,g75)
    c: PointOnObject(g77,g2)
    c: Tangent(g77,g2)
    c: Tangent(g77,g76) = 1.5708
    c: Equal(g76,g2)
    c: Coincident(g4,g78)
    c: Tangent(g79,g76) = -1.5708
    c: PointOnObject(g2,g80)
    c: Perpendicular(g80,g81) = 1.5708
    c: Perpendicular(g81,g82) = 4.71239
    c: Coincident(g3,g83) = 1.5708
    c: Coincident(g83,g80)
    c: Coincident(g83,g7)
    c: Coincident(g81,g75)
    c: Equal(g81,g76)
    c: Coincident(g84,g3)
    c: Tangent(g83,g84)
    c: Tangent(g84,g82) = 1.5708
    c: Equal(g84,g3)
    c: PointOnObject(g78,g4)
    c: Parallel(g79,g82)
    c: Tangent(g85,g79) = 1.5708
    c: Tangent(g85,g78) = 1.5708
    c: Equal(g85,g3)
    c: Coincident(g86,g1)
    c: Tangent(g86,g77) = 1.5708
FEATURE [PartDesign::Pad] Pad010
  Direction = (0,-1,2e-16)
  Length = 5
  Length2 = 10
  Placement = pos=(0,0,0) rot=(1,0,0;1.5708rad)
  Profile = -> Sketch024
  ReferenceAxis = -> Sketch024 [N_Axis]
  Suppressed = false
  Type = 0
FEATURE [PartDesign::Body] Body011  label="Wall001"
  AllowCompound = false
  Group = -> [Sketch024,Pad010]
  Origin = -> Origin011
  Placement = pos=(0,-34,0) rot=(0,0,1;0rad)
  Tip = -> Pad010
FEATURE [Sketcher::SketchObject] Sketch025
  AttachmentSupport = -> [XZ_Plane012]
  FullyConstrained = true
  MapMode = 5
  Placement = pos=(0,0,0) rot=(1,0,0;1.5708rad)
  expr: Constraints[102] = Sketch024.Constraints[102]
  expr: Constraints[109] = Sketch024.Constraints[109]
  expr: Constraints[10] = Sketch024.Constraints[10]
  expr: Constraints[110] = Sketch024.Constraints[110]
  expr: Constraints[112] = Sketch024.Constraints[112]
  expr: Constraints[113] = Sketch024.Constraints[113]
  expr: Constraints[114] = Sketch024.Constraints[114]
  expr: Constraints[115] = Sketch024.Constraints[115]
  expr: Constraints[117] = Sketch024.Constraints[117]
  expr: Constraints[118] = Sketch024.Constraints[118]
  expr: Constraints[12] = Sketch024.Constraints[12]
  expr: Constraints[16] = Sketch024.Constraints[16]
  expr: Constraints[18] = Sketch024.Constraints[18]
  expr: Constraints[19] = Sketch024.Constraints[19]
  expr: Constraints[20] = Sketch024.Constraints[20]
  expr: Constraints[22] = Sketch024.Constraints[22]
  expr: Constraints[23] = Sketch024.Constraints[23]
  expr: Constraints[24] = Sketch024.Constraints[24]
  expr: Constraints[25] = Sketch024.Constraints[25]
  expr: Constraints[292] = <<Sketch024>>.Constraints[122]
  expr: Constraints[293] = <<Sketch024>>.Constraints[120]
  expr: Constraints[63] = Sketch024.Constraints[63]
  expr: Constraints[98] = Sketch024.Constraints[98]
  sketch-geometry (106):
    g0: LineSegment StartX=-30 StartY=-35 StartZ=0 EndX=-30 EndY=-25 EndZ=0
    g1: LineSegment StartX=-30 StartY=-25 StartZ=0 EndX=-3.66638 EndY=3.39966 EndZ=0
    g2: ArcOfCircle CenterX=0 CenterY=0 CenterZ=0 NormalX=0 NormalY=0 NormalZ=1 AngleXU=0 Radius=5 StartAngle=0.635121 EndAngle=2.39392
    g3: ArcOfCircle CenterX=60 CenterY=0 CenterZ=0 NormalX=0 NormalY=0 NormalZ=1 AngleXU=0 Radius=8 StartAngle=0.669738 EndAngle=2.56349
    g4: LineSegment StartX=66.2719 StartY=4.96625 StartZ=0 EndX=90 EndY=-25 EndZ=0
    g5: LineSegment StartX=90 StartY=-25 StartZ=0 EndX=90 EndY=-35 EndZ=0
    g6: LineSegment StartX=90 StartY=-35 StartZ=0 EndX=81.7609 EndY=-35 EndZ=0
    g7: ArcOfCircle CenterX=28.175 CenterY=20.7646 CenterZ=0 NormalX=0 NormalY=0 NormalZ=1 AngleXU=0 Radius=30 StartAngle=3.77671 EndAngle=5.70508
    g8: Circle CenterX=0 CenterY=0 CenterZ=0 NormalX=0 NormalY=0 NormalZ=1 AngleXU=0 Radius=2.7
    g9: Circle CenterX=60 CenterY=0 CenterZ=0 NormalX=0 NormalY=0 NormalZ=1 AngleXU=0 Radius=5.2
    g10: LineSegment StartX=81.7609 StartY=-35 StartZ=0 EndX=83.5218 EndY=-31.95 EndZ=0
    g11: LineSegment StartX=83.5218 StartY=-31.95 StartZ=0 EndX=81.7609 EndY=-28.9 EndZ=0
    g12: LineSegment StartX=81.7609 StartY=-28.9 StartZ=0 EndX=78.2391 EndY=-28.9 EndZ=0
    g13: LineSegment StartX=78.2391 StartY=-28.9 StartZ=0 EndX=76.4782 EndY=-31.95 EndZ=0
    g14: LineSegment StartX=76.4782 StartY=-31.95 StartZ=0 EndX=78.2391 EndY=-35 EndZ=0
    g15: LineSegment StartX=78.2391 StartY=-35 StartZ=0 EndX=81.7609 EndY=-35 EndZ=0
    g16: Circle CenterX=80 CenterY=-31.95 CenterZ=0 NormalX=0 NormalY=0 NormalZ=1 AngleXU=0 Radius=3.52184
    g17: LineSegment StartX=31.7609 StartY=-35 StartZ=0 EndX=33.5218 EndY=-31.95 EndZ=0
    g18: LineSegment StartX=33.5218 StartY=-31.95 StartZ=0 EndX=31.7609 EndY=-28.9 EndZ=0
    g19: LineSegment StartX=31.7609 StartY=-28.9 StartZ=0 EndX=28.2391 EndY=-28.9 EndZ=0
    g20: LineSegment StartX=28.2391 StartY=-28.9 StartZ=0 EndX=26.4782 EndY=-31.95 EndZ=0
    g21: LineSegment StartX=26.4782 StartY=-31.95 StartZ=0 EndX=28.2391 EndY=-35 EndZ=0
    g22: LineSegment StartX=28.2391 StartY=-35 StartZ=0 EndX=31.7609 EndY=-35 EndZ=0
    g23: Circle CenterX=30 CenterY=-31.95 CenterZ=0 NormalX=0 NormalY=0 NormalZ=1 AngleXU=0 Radius=3.52184
    g24: LineSegment StartX=-21.7609 StartY=-35 StartZ=0 EndX=-30 EndY=-35 EndZ=0
    g25: LineSegment StartX=78.2391 StartY=-35 StartZ=0 EndX=31.7609 EndY=-35 EndZ=0
    g26: LineSegment StartX=28.2391 StartY=-35 StartZ=0 EndX=-18.2391 EndY=-35 EndZ=0
    g27: LineSegment StartX=78.716 StartY=-20.4147 StartZ=0 EndX=66.3765 EndY=-4.83115 EndZ=0
    g28: ArcOfCircle CenterX=60 CenterY=0 CenterZ=0 NormalX=0 NormalY=0 NormalZ=1 AngleXU=0 Radius=8 StartAngle=3.77812 EndAngle=5.63481
    g29: LineSegment StartX=41.1694 StartY=-28.9 StartZ=0 EndX=70.2307 EndY=-28.9 EndZ=0
    g30: LineSegment StartX=70.2307 StartY=-28.9 StartZ=0 EndX=78.716 EndY=-20.4147 EndZ=0
    g31: ArcOfCircle CenterX=0 CenterY=0 CenterZ=0 NormalX=0 NormalY=0 NormalZ=1 AngleXU=0 Radius=5 StartAngle=4.16608 EndAngle=5.2157
    g32: LineSegment StartX=-2.59769 StartY=-4.27224 StartZ=0 EndX=-17.5658 EndY=-20.4147 EndZ=0
    g33: LineSegment StartX=-17.5658 StartY=-20.4147 StartZ=0 EndX=-9.08055 EndY=-28.9 EndZ=0
    g34: LineSegment StartX=-9.08055 StartY=-28.9 StartZ=0 EndX=19.3431 EndY=-28.9 EndZ=0
    g35: ArcOfCircle CenterX=28.175 CenterY=20.7646 CenterZ=0 NormalX=0 NormalY=0 NormalZ=1 AngleXU=0 Radius=36 StartAngle=3.91484 EndAngle=4.62408
    g36: ArcOfCircle CenterX=28.175 CenterY=20.7646 CenterZ=0 NormalX=0 NormalY=0 NormalZ=1 AngleXU=0 Radius=36 StartAngle=4.90313 EndAngle=5.49527
    g37: LineSegment StartX=-2.59769 StartY=-4.27224 StartZ=0 EndX=-6.99735 EndY=-0.192648 EndZ=0
    g38: LineSegment StartX=66.3765 StartY=-4.83115 StartZ=0 EndX=71.0804 EndY=-1.10647 EndZ=0
    g39: LineSegment StartX=19.3431 StartY=-28.9 StartZ=0 EndX=25 EndY=-23.2431 EndZ=0
    g40: LineSegment StartX=25 StartY=-23.2431 StartZ=0 EndX=25 EndY=-15.0951 EndZ=0
    g41: LineSegment StartX=35 StartY=-14.5825 StartZ=0 EndX=35 EndY=-22.7306 EndZ=0
    g42: LineSegment StartX=35 StartY=-22.7306 StartZ=0 EndX=41.1694 EndY=-28.9 EndZ=0
    g43: LineSegment StartX=-18.2391 StartY=-35 StartZ=0 EndX=-16.4782 EndY=-31.95 EndZ=0
    g44: LineSegment StartX=-16.4782 StartY=-31.95 StartZ=0 EndX=-18.2391 EndY=-28.9 EndZ=0
    g45: LineSegment StartX=-18.2391 StartY=-28.9 StartZ=0 EndX=-21.7609 EndY=-28.9 EndZ=0
    g46: LineSegment StartX=-21.7609 StartY=-28.9 StartZ=0 EndX=-23.5218 EndY=-31.95 EndZ=0
    g47: LineSegment StartX=-23.5218 StartY=-31.95 StartZ=0 EndX=-21.7609 EndY=-35 EndZ=0
    g48: LineSegment StartX=-21.7609 StartY=-35 StartZ=0 EndX=-18.2391 EndY=-35 EndZ=0
    g49: Circle CenterX=-20 CenterY=-31.95 CenterZ=0 NormalX=0 NormalY=0 NormalZ=1 AngleXU=0 Radius=3.52184
    g50: LineSegment StartX=-68.2391 StartY=-35 StartZ=0 EndX=-66.4782 EndY=-31.95 EndZ=0
    g51: LineSegment StartX=-66.4782 StartY=-31.95 StartZ=0 EndX=-68.2391 EndY=-28.9 EndZ=0
    g52: LineSegment StartX=-68.2391 StartY=-28.9 StartZ=0 EndX=-71.7609 EndY=-28.9 EndZ=0
    g53: LineSegment StartX=-71.7609 StartY=-28.9 StartZ=0 EndX=-73.5218 EndY=-31.95 EndZ=0
    g54: LineSegment StartX=-73.5218 StartY=-31.95 StartZ=0 EndX=-71.7609 EndY=-35 EndZ=0
    g55: LineSegment StartX=-71.7609 StartY=-35 StartZ=0 EndX=-68.2391 EndY=-35 EndZ=0
    g56: Circle CenterX=-70 CenterY=-31.95 CenterZ=0 NormalX=0 NormalY=0 NormalZ=1 AngleXU=0 Radius=3.52184
    g57: LineSegment StartX=-118.239 StartY=-35 StartZ=0 EndX=-116.478 EndY=-31.95 EndZ=0
    g58: LineSegment StartX=-116.478 StartY=-31.95 StartZ=0 EndX=-118.239 EndY=-28.9 EndZ=0
    g59: LineSegment StartX=-118.239 StartY=-28.9 StartZ=0 EndX=-121.761 EndY=-28.9 EndZ=0
    g60: LineSegment StartX=-121.761 StartY=-28.9 StartZ=0 EndX=-123.522 EndY=-31.95 EndZ=0
    g61: LineSegment StartX=-123.522 StartY=-31.95 StartZ=0 EndX=-121.761 EndY=-35 EndZ=0
    g62: LineSegment StartX=-121.761 StartY=-35 StartZ=0 EndX=-118.239 EndY=-35 EndZ=0
    g63: Circle CenterX=-120 CenterY=-31.95 CenterZ=0 NormalX=0 NormalY=0 NormalZ=1 AngleXU=0 Radius=3.52184
    g64: LineSegment StartX=-21.7609 StartY=-35 StartZ=0 EndX=-68.2391 EndY=-35 EndZ=0
    g65: LineSegment StartX=-71.7609 StartY=-35 StartZ=0 EndX=-118.239 EndY=-35 EndZ=0
    g66: LineSegment StartX=-121.761 StartY=-35 StartZ=0 EndX=-130 EndY=-35 EndZ=0
    g67: LineSegment StartX=-130 StartY=-35 StartZ=0 EndX=-130 EndY=-25 EndZ=0
    g68: LineSegment StartX=-130 StartY=-25 StartZ=0 EndX=-94.3834 EndY=39.9054 EndZ=0
    g69: ArcOfCircle CenterX=-90 CenterY=37.5 CenterZ=0 NormalX=0 NormalY=0 NormalZ=1 AngleXU=0 Radius=5 StartAngle=1.17601 EndAngle=2.63971
    g70: LineSegment StartX=-88.0769 StartY=42.1154 StartZ=0 EndX=1.92308 EndY=4.61538 EndZ=0
    g71: ArcOfCircle CenterX=0 CenterY=0 CenterZ=0 NormalX=0 NormalY=0 NormalZ=1 AngleXU=0 Radius=5 StartAngle=0.635121 EndAngle=1.17601
    g72: LineSegment StartX=-92.4054 StartY=33.1166 StartZ=0 EndX=-120.228 EndY=-17.5863 EndZ=0
    g73: LineSegment StartX=-120.228 StartY=-17.5863 StartZ=0 EndX=-108.915 EndY=-28.9 EndZ=0
    g74: LineSegment StartX=-108.915 StartY=-28.9 StartZ=0 EndX=-80.7658 EndY=-28.9 EndZ=0
    g75: LineSegment StartX=-80.7658 StartY=-28.9 StartZ=0 EndX=-75.109 EndY=-23.2431 EndZ=0
    g76: LineSegment StartX=-75.109 StartY=-23.2431 StartZ=0 EndX=-91.2041 EndY=32.6471 EndZ=0
    g77: ArcOfCircle CenterX=-90 CenterY=37.5 CenterZ=0 NormalX=0 NormalY=0 NormalZ=1 AngleXU=0 Radius=5 StartAngle=4.21051 EndAngle=4.46918
    g78: ArcOfCircle CenterX=-90 CenterY=37.5 CenterZ=0 NormalX=0 NormalY=0 NormalZ=1 AngleXU=0 Radius=5 StartAngle=5.51638 EndAngle=5.88839
    g79: LineSegment StartX=-85.3846 StartY=35.5769 StartZ=0 EndX=-53.0769 EndY=22.1154 EndZ=0
    g80: ArcOfCircle CenterX=-48.4615 CenterY=20.1923 CenterZ=0 NormalX=0 NormalY=0 NormalZ=1 AngleXU=0 Radius=5 StartAngle=2.7468 EndAngle=3.79707
    g81: LineSegment StartX=-63.9906 StartY=-23.9503 StartZ=0 EndX=-59.0409 EndY=-28.9 EndZ=0
    g82: LineSegment StartX=-59.0409 StartY=-28.9 StartZ=0 EndX=-34.0658 EndY=-28.9 EndZ=0
    g83: LineSegment StartX=-34.0658 StartY=-28.9 StartZ=0 EndX=-27.8862 EndY=-22.7203 EndZ=0
    g84: LineSegment StartX=-27.8862 StartY=-22.7203 StartZ=0 EndX=-48.1487 EndY=14.4013 EndZ=0
    g85: LineSegment StartX=-48.1487 StartY=14.4013 StartZ=0 EndX=-63.9906 EndY=-23.9503 EndZ=0
    g86: LineSegment StartX=-24.3005 StartY=-18.8534 StartZ=0 EndX=-4.91845 EndY=2.04935 EndZ=0
    g87: LineSegment StartX=0 StartY=0 StartZ=0 EndX=-90 EndY=37.5 EndZ=0
    g88: LineSegment StartX=-90 StartY=37.5 StartZ=0 EndX=-70 EndY=-31.95 EndZ=0
    g89: LineSegment StartX=-70 StartY=-31.95 StartZ=0 EndX=-48.4615 EndY=20.1923 EndZ=0
    g90: GeomPoint X=-64.9569 Y=-26.2895 Z=0
    g91: GeomPoint X=-74.3829 Y=-25.7643 Z=0
    g92: LineSegment StartX=-74.3829 StartY=-25.7643 StartZ=0 EndX=-69.5782 EndY=-24.3806 EndZ=0
    g93: LineSegment StartX=-69.5782 StartY=-24.3806 StartZ=0 EndX=-64.9569 EndY=-26.2895 EndZ=0
    g94: LineSegment StartX=-120.228 StartY=-17.5863 StartZ=0 EndX=-124.612 EndY=-15.1809 EndZ=0
    g95: LineSegment StartX=-70.2926 StartY=-21.9 StartZ=0 EndX=-86.3994 EndY=34.0308 EndZ=0
    g96: LineSegment StartX=-52.4253 StartY=17.1446 StartZ=0 EndX=-68.5535 EndY=-21.9 EndZ=0
    g97: LineSegment StartX=-70.2926 StartY=-21.9 StartZ=0 EndX=-68.5535 EndY=-21.9 EndZ=0
    g98: LineSegment StartX=-48.4615 StartY=20.1923 StartZ=0 EndX=-20 EndY=-31.95 EndZ=0
    g99: LineSegment StartX=-24.3005 StartY=-18.8534 StartZ=0 EndX=-28.6893 EndY=-21.2489 EndZ=0
    g100: LineSegment StartX=-44.1925 StartY=17.5893 StartZ=0 EndX=-24.3005 EndY=-18.8534 EndZ=0
    g101: LineSegment StartX=-4.91845 StartY=2.04935 StartZ=0 EndX=-43.8462 EndY=18.2692 EndZ=0
    g102: ArcOfCircle CenterX=-48.4615 CenterY=20.1923 CenterZ=0 NormalX=0 NormalY=0 NormalZ=1 AngleXU=0 Radius=5 StartAngle=5.73563 EndAngle=5.88839
    g103: Circle CenterX=-48.4615 CenterY=20.1923 CenterZ=0 NormalX=0 NormalY=0 NormalZ=1 AngleXU=0 Radius=2.7
    g104: Circle CenterX=-90 CenterY=37.5 CenterZ=0 NormalX=0 NormalY=0 NormalZ=1 AngleXU=0 Radius=2.7
    g105: Circle CenterX=30 CenterY=-14.5 CenterZ=0 NormalX=0 NormalY=0 NormalZ=1 AngleXU=0 Radius=3.1
  constraints (274):
    c: Vertical(g0)
    c: Coincident(g0,g1)
    c: Tangent(g1,g2) = 1.5708
    c: Tangent(g3,g4) = 1.5708
    c: Coincident(g4,g5)
    c: Vertical(g5)
    c: Coincident(g5,g6)
    c: Coincident(g24,g0)
    c: Horizontal(g6)
    c: Coincident(g2,g-1)
    c: Diameter(g2) = 10
    c: PointOnObject(g3,g-1)
    c: DistanceX(g3) = 60
    c: Tangent(g7,g2) = 1.5708
    c: Tangent(g7,g3) = 1.5708
    c: Coincident(g8,g2)
    c: Diameter(g8) = 5.4
    c: Coincident(g9,g3)
    c: Diameter(g9) = 10.4
    c: Diameter(g3) = 16
    c: DistanceY(g5,g5) = 10
    c: Equal(g5,g0)
    c: DistanceY(g5) = -35
    c: DistanceX(g0) = -30
    c: DistanceX(g5) = 90
    c: Radius(g7) = 30
    c: PointOnObject(g26,g6)
    c: Coincident(g10,g11)
    c: Coincident(g11,g12)
    c: Coincident(g12,g13)
    c: Coincident(g13,g14)
    c: Coincident(g14,g15)
    c: Coincident(g15,g10)
    c: Equal(g10, g11-g15) x5
    c: PointOnObject(g10,g16)
    c: PointOnObject(g11,g16)
    c: PointOnObject(g12,g16)
    c: PointOnObject(g13,g16)
    c: PointOnObject(g14,g16)
    c: PointOnObject(g15,g16)
    c: Coincident(g17,g18)
    c: Coincident(g18,g19)
    c: Coincident(g19,g20)
    c: Coincident(g20,g21)
    c: Coincident(g21,g22)
    c: Coincident(g22,g17)
    c: Equal(g17, g18-g22) x5
    c: PointOnObject(g17,g23)
    c: PointOnObject(g18,g23)
    c: PointOnObject(g19,g23)
    c: PointOnObject(g20,g23)
    c: PointOnObject(g21,g23)
    c: PointOnObject(g22,g23)
    c: Horizontal(g22)
    c: Equal(g23,g16)
    c: DistanceX(g16,g5) = 10
    c: Coincident(g6,g10)
    c: Horizontal(g15)
    c: Coincident(g14,g25)
    c: Coincident(g25,g17)
    c: Horizontal(g25)
    c: Coincident(g21,g26)
    c: Horizontal(g24)
    c: Equal(g26,g25)
    c: Coincident(g42,g29)
    c: Horizontal(g29)
    c: Coincident(g29,g30)
    c: Coincident(g30,g27)
    c: Coincident(g31,g32)
    c: Coincident(g32,g33)
    c: Coincident(g33,g34)
    c: Coincident(g34,g39)
    c: Horizontal(g34)
    c: Parallel(g32,g1)
    c: Coincident(g31,g2)
    c: Equal(g2,g31)
    c: Coincident(g35,g7)
    c: Coincident(g35,g31)
    c: Coincident(g36,g7)
    c: Coincident(g36,g28)
    c: Coincident(g41,g36)
    c: Coincident(g40,g35)
    c: Equal(g35,g36)
    c: Coincident(g31,g37)
    c: PointOnObject(g37,g1)
    c: Perpendicular(g1,g37)
    c: Coincident(g27,g38)
    c: PointOnObject(g38,g4)
    c: Perpendicular(g4,g38)
    c: Equal(g37,g38)
    c: Distance(g38) = 6
    c: Parallel(g27,g4)
    c: Horizontal(g39,g42)
    c: Horizontal(g42,g18)
    c: Radius(g36) = 36
    c: Coincident(g28,g3)
    c: Equal(g28,g3)
    c: Coincident(g39,g40)
    c: Coincident(g41,g42)
    c: Vertical(g40)
    c: Vertical(g41)
    c: DistanceX(g35,g36) = 10
    c: DistanceX(g23,g36) = 5
    c: Equal(g41,g40)
    c: Angle(g39,g34) = 2.35619
    c: Angle(g29,g42) = 2.35619
    c: Distance(g39) = 8
    c: Angle(g30,g29) = 2.35619
    c: Coincident(g27,g28)
    c: Distance(g30) = 12
    c: Angle(g34,g33) = 2.35619
    c: Equal(g33,g30)
    c: Coincident(g43,g44)
    c: Coincident(g44,g45)
    c: Coincident(g45,g46)
    c: Coincident(g46,g47)
    c: Coincident(g47,g48)
    c: Coincident(g48,g43)
    c: Equal(g43, g44-g48) x5
    c: PointOnObject(g43,g49)
    c: PointOnObject(g44,g49)
    c: PointOnObject(g45,g49)
    c: PointOnObject(g46,g49)
    c: PointOnObject(g47,g49)
    c: PointOnObject(g48,g49)
    c: Horizontal(g48)
    c: Coincident(g50,g51)
    c: Coincident(g51,g52)
    c: Coincident(g52,g53)
    c: Coincident(g53,g54)
    c: Coincident(g54,g55)
    c: Coincident(g55,g50)
    c: Equal(g50, g51-g55) x5
    c: PointOnObject(g50,g56)
    c: PointOnObject(g51,g56)
    c: PointOnObject(g52,g56)
    c: PointOnObject(g53,g56)
    c: PointOnObject(g54,g56)
    c: PointOnObject(g55,g56)
    c: Horizontal(g55)
    c: Coincident(g57,g58)
    c: Coincident(g58,g59)
    c: Coincident(g59,g60)
    c: Coincident(g60,g61)
    c: Coincident(g61,g62)
    c: Coincident(g62,g57)
    c: Equal(g57, g58-g62) x5
    c: PointOnObject(g57,g63)
    c: PointOnObject(g58,g63)
    c: PointOnObject(g59,g63)
    c: PointOnObject(g60,g63)
    c: PointOnObject(g61,g63)
    c: PointOnObject(g62,g63)
    c: DistanceY(g57,g58) = 6.1
    c: Horizontal(g62)
    c: Coincident(g24,g64)
    c: Coincident(g64,g50)
    c: Horizontal(g64)
    c: Coincident(g54,g65)
    c: Coincident(g65,g57)
    c: Horizontal(g65)
    c: Coincident(g61,g66)
    c: Horizontal(g66)
    c: Coincident(g66,g67)
    c: Vertical(g67)
    c: Coincident(g67,g68)
    c: Tangent(g68,g69) = 1.5708
    c: Tangent(g69,g70) = 1.5708
    c: DistanceX(g69) = -90
    c: DistanceY(g69) = 37.5
    c: Equal(g67,g5)
    c: Equal(g6,g66)
    c: Coincident(g24,g47)
    c: Coincident(g43,g26)
    c: Equal(g23,g49)
    c: DistanceX(g0,g49) = 10
    c: Equal(g56,g49)
    c: Equal(g64,g26)
    c: Equal(g65,g64)
    c: Coincident(g71,g2)
    c: Coincident(g71,g2)
    c: Tangent(g70,g71) = 1.5708
    c: Equal(g71,g69)
    c: Coincident(g72,g73)
    c: Coincident(g73,g74)
    c: Horizontal(g74)
    c: Coincident(g74,g75)
    c: Coincident(g75,g76)
    c: Coincident(g77,g72)
    c: Coincident(g78,g79)
    c: Perpendicular(g79,g80) = 4.71239
    c: Coincident(g80,g96)
    c: Coincident(g81,g82)
    c: Horizontal(g82)
    c: Coincident(g82,g83)
    c: Coincident(g83,g84)
    c: Coincident(g84,g85)
    c: Coincident(g85,g81)
    c: PointOnObject(g100,g1)
    c: Coincident(g100,g86)
    c: PointOnObject(g86,g1)
    c: Coincident(g87,g2)
    c: Coincident(g87,g69)
    c: PointOnObject(g78,g87)
    c: PointOnObject(g79,g87)
    c: PointOnObject(g101,g87)
    c: Parallel(g72,g68)
    c: Coincident(g78,g77)
    c: Coincident(g95,g78)
    c: Coincident(g77,g76)
    c: Equal(g77,g78)
    c: Coincident(g77,g69)
    c: PointOnObject(g69,g72)
    c: Equal(g77,g69)
    c: Horizontal(g74,g52)
    c: Parallel(g83,g39)
    c: Parallel(g33,g81)
    c: Parallel(g83,g75)
    c: Coincident(g88,g69)
    c: Coincident(g88,g89)
    c: Coincident(g89,g80)
    c: Equal(g80,g69)
    c: Distance(g80,g69) = 45
    c: Parallel(g85,g89)
    c: PointOnObject(g90,g85)
    c: PointOnObject(g91,g76)
    c: Parallel(g76,g88)
    c: Symmetric(g92,g91,g88)
    c: Symmetric(g92,g90,g89)
    c: Coincident(g92,g91)
    c: Coincident(g92,g93)
    c: Coincident(g93,g90)
    c: Equal(g93,g92)
    c: Coincident(g72,g94)
    c: PointOnObject(g94,g68)
    c: Perpendicular(g68,g94)
    c: Equal(g94,g92)
    c: Parallel(g95,g76)
    c: Parallel(g85,g96)
    c: PointOnObject(g92,g95)
    c: PointOnObject(g92,g96)
    c: Coincident(g95,g97)
    c: Coincident(g97,g96)
    c: Horizontal(g97)
    c: Horizontal(g82,g33)
    c: Coincident(g98,g80)
    c: Coincident(g98,g49)
    c: Coincident(g100,g99)
    c: PointOnObject(g99,g84)
    c: Symmetric(g99,g100,g98)
    c: Equal(g99,g93)
    c: Parallel(g84,g98)
    c: Coincident(g86,g101)
    c: Parallel(g100,g84)
    c: PointOnObject(g101,g87)
    c: Coincident(g102,g80)
    c: Coincident(g102,g100)
    c: Coincident(g102,g101)
    c: Equal(g102,g80)
    c: Coincident(g88,g56)
    c: DistanceY(g51,g96) = 7
    c: Distance(g75) = 8
    c: Distance(g81) = 7
    c: Parallel(g73,g81)
    c: Distance(g73) = 16
    c: PointOnObject(g83,g1)
    c: Coincident(g103,g80)
    c: Coincident(g104,g69)
    c: Equal(g104,g103)
    c: Equal(g49,g63)
    c: Equal(g103,g8)
    c: Vertical(g105,g23)
    c: DistanceY(g21,g105) = 20.5
    c: Diameter(g105) = 6.2
FEATURE [PartDesign::Pad] Pad011
  Direction = (0,-1,2e-16)
  Length = 6
  Length2 = 10
  Placement = pos=(0,0,0) rot=(1,0,0;1.5708rad)
  Profile = -> Sketch025
  ReferenceAxis = -> Sketch025 [N_Axis]
  Suppressed = false
  Type = 0
FEATURE [Sketcher::SketchObject] Sketch026
  AttachmentSupport = -> [XZ_Plane012]
  FullyConstrained = true
  MapMode = 5
  Placement = pos=(0,0,0) rot=(1,0,0;1.5708rad)
  sketch-geometry (7):
    g0: Circle CenterX=0 CenterY=0 CenterZ=0 NormalX=0 NormalY=0 NormalZ=1 AngleXU=0 Radius=2.7
    g1: Circle CenterX=-48.4615 CenterY=20.1923 CenterZ=0 NormalX=0 NormalY=0 NormalZ=1 AngleXU=0 Radius=2.7
    g2: Circle CenterX=-90 CenterY=37.5 CenterZ=0 NormalX=0 NormalY=0 NormalZ=1 AngleXU=0 Radius=2.7
    g3: Circle CenterX=0 CenterY=0 CenterZ=0 NormalX=0 NormalY=0 NormalZ=1 AngleXU=0 Radius=5
    g4: Circle CenterX=-48.4615 CenterY=20.1923 CenterZ=0 NormalX=0 NormalY=0 NormalZ=1 AngleXU=0 Radius=5
    g5: Circle CenterX=-90 CenterY=37.5 CenterZ=0 NormalX=0 NormalY=0 NormalZ=1 AngleXU=0 Radius=5
    g6: LineSegment StartX=0 StartY=0 StartZ=0 EndX=-90 EndY=37.5 EndZ=0
  constraints (16):
    c: Coincident(g0,g-1)
    c: Equal(g2,g1)
    c: Equal(g1,g0)
    c: Coincident(g3,g0)
    c: Coincident(g4,g1)
    c: Coincident(g5,g2)
    c: Equal(g5,g4)
    c: Equal(g4,g3)
    c: Coincident(g6,g0)
    c: Coincident(g6,g2)
    c: PointOnObject(g1,g6)
    c: Diameter(g0) = 5.4
    c: Diameter(g3) = 10
    c: Distance(g2,g1) = 45
    c: DistanceX(g2) = -90
    c: DistanceY(g2) = 37.5
FEATURE [PartDesign::Pad] Pad012
  BaseFeature = -> Pad011
  Direction = (0,-1,2e-16)
  Length = 8
  Length2 = 10
  Placement = pos=(0,0,0) rot=(1,0,0;1.5708rad)
  Profile = -> Sketch026
  ReferenceAxis = -> Sketch026 [N_Axis]
  Suppressed = false
  Type = 0
FEATURE [PartDesign::Body] Body012  label="Wall002"
  AllowCompound = false
  Group = -> [Sketch025,Pad011,Sketch026,Pad012]
  Origin = -> Origin012
  Placement = pos=(0,8.5,0) rot=(0,0,1;0rad)
  Tip = -> Pad012
FEATURE [Sketcher::SketchObject] Sketch027
  AttachmentSupport = -> [XZ_Plane013]
  FullyConstrained = true
  MapMode = 5
  Placement = pos=(0,0,0) rot=(1,0,0;1.5708rad)
  sketch-geometry (7):
    g0: LineSegment StartX=3.4641 StartY=0 StartZ=0 EndX=1.73205 EndY=3 EndZ=0
    g1: LineSegment StartX=1.73205 StartY=3 StartZ=0 EndX=-1.73205 EndY=3 EndZ=0
    g2: LineSegment StartX=-1.73205 StartY=3 StartZ=0 EndX=-3.4641 EndY=1.69e-14 EndZ=0
    g3: LineSegment StartX=-3.4641 StartY=1.69e-14 StartZ=0 EndX=-1.73205 EndY=-3 EndZ=0
    g4: LineSegment StartX=-1.73205 StartY=-3 StartZ=0 EndX=1.73205 EndY=-3 EndZ=0
    g5: LineSegment StartX=1.73205 StartY=-3 StartZ=0 EndX=3.4641 EndY=0 EndZ=0
    g6: Circle CenterX=0 CenterY=0 CenterZ=0 NormalX=0 NormalY=0 NormalZ=1 AngleXU=0 Radius=3.4641
  constraints (16):
    c: Coincident(g0,g1)
    c: Coincident(g1,g2)
    c: Coincident(g2,g3)
    c: Coincident(g3,g4)
    c: Coincident(g4,g5)
    c: Coincident(g5,g0)
    c: Equal(g0, g1-g5) x5
    c: PointOnObject(g0,g6)
    c: PointOnObject(g1,g6)
    c: PointOnObject(g2,g6)
    c: PointOnObject(g3,g6)
    c: PointOnObject(g4,g6)
    c: PointOnObject(g5,g6)
    c: Coincident(g6,g-1)
    c: PointOnObject(g5,g-1)
    c: DistanceY(g4,g0) = 6
FEATURE [PartDesign::Pad] Pad013
  Direction = (0,-1,2e-16)
  Length = 115
  Length2 = 10
  Placement = pos=(0,0,0) rot=(1,0,0;1.5708rad)
  Profile = -> Sketch027
  ReferenceAxis = -> Sketch027 [N_Axis]
  Suppressed = false
  Type = 0
FEATURE [PartDesign::Body] Body013  label="HexRod6mm"
  AllowCompound = false
  Group = -> [Sketch027,Pad013]
  Origin = -> Origin013
  Placement = pos=(-20,10,-32) rot=(0,0,1;0rad)
  Tip = -> Pad013
FEATURE [Sketcher::SketchObject] Sketch028
  AttachmentSupport = -> [XZ_Plane014]
  FullyConstrained = true
  MapMode = 5
  Placement = pos=(0,0,0) rot=(1,0,0;1.5708rad)
  sketch-geometry (7):
    g0: LineSegment StartX=4.04145 StartY=0 StartZ=0 EndX=2.02073 EndY=3.5 EndZ=0
    g1: LineSegment StartX=2.02073 StartY=3.5 StartZ=0 EndX=-2.02073 EndY=3.5 EndZ=0
    g2: LineSegment StartX=-2.02073 StartY=3.5 StartZ=0 EndX=-4.04145 EndY=3.6e-15 EndZ=0
    g3: LineSegment StartX=-4.04145 StartY=3.6e-15 StartZ=0 EndX=-2.02073 EndY=-3.5 EndZ=0
    g4: LineSegment StartX=-2.02073 StartY=-3.5 StartZ=0 EndX=2.02073 EndY=-3.5 EndZ=0
    g5: LineSegment StartX=2.02073 StartY=-3.5 StartZ=0 EndX=4.04145 EndY=0 EndZ=0
    g6: Circle CenterX=0 CenterY=0 CenterZ=0 NormalX=0 NormalY=0 NormalZ=1 AngleXU=0 Radius=4.04145
  constraints (16):
    c: Coincident(g0,g1)
    c: Coincident(g1,g2)
    c: Coincident(g2,g3)
    c: Coincident(g3,g4)
    c: Coincident(g4,g5)
    c: Coincident(g5,g0)
    c: Equal(g0, g1-g5) x5
    c: PointOnObject(g0,g6)
    c: PointOnObject(g1,g6)
    c: PointOnObject(g2,g6)
    c: PointOnObject(g3,g6)
    c: PointOnObject(g4,g6)
    c: PointOnObject(g5,g6)
    c: Coincident(g6,g-1)
    c: PointOnObject(g5,g-1)
    c: DistanceY(g4,g0) = 7
FEATURE [PartDesign::Pad] Pad014
  Direction = (0,-1,2e-16)
  Length = 80
  Length2 = 10
  Placement = pos=(0,0,0) rot=(1,0,0;1.5708rad)
  Profile = -> Sketch028
  ReferenceAxis = -> Sketch028 [N_Axis]
  Suppressed = false
  Type = 0
FEATURE [PartDesign::Body] Body014  label="HexRod7mm"
  AllowCompound = false
  Group = -> [Sketch028,Pad014]
  Origin = -> Origin014
  Placement = pos=(60,33,0) rot=(0,0,1;0rad)
  Tip = -> Pad014
FEATURE [Sketcher::SketchObject] Sketch029
  AttachmentSupport = -> [XZ_Plane002]
  FullyConstrained = true
  MapMode = 5
  Placement = pos=(0,0,0) rot=(1,0,0;1.5708rad)
  expr: Constraints[13] = Sketch005.Constraints[13]
  expr: Constraints[14] = Sketch005.Constraints[14]
  expr: Constraints[15] = Sketch005.Constraints[15] + 6 mm
  expr: Constraints[17] = Sketch005.Constraints[17]
  sketch-geometry (6):
    g0: ArcOfCircle CenterX=17 CenterY=0 CenterZ=0 NormalX=0 NormalY=0 NormalZ=1 AngleXU=0 Radius=6 StartAngle=5.85341 EndAngle=9.85455
    g1: LineSegment StartX=11.5456 StartY=-2.5 StartZ=0 EndX=-8.45436 EndY=-2.5 EndZ=0
    g2: LineSegment StartX=-8.45436 StartY=-2.5 StartZ=0 EndX=-8.45436 EndY=17.5 EndZ=0
    g3: LineSegment StartX=-8.45436 StartY=17.5 StartZ=0 EndX=42.4544 EndY=17.5 EndZ=0
    g4: LineSegment StartX=42.4544 StartY=17.5 StartZ=0 EndX=42.4544 EndY=-2.5 EndZ=0
    g5: LineSegment StartX=42.4544 StartY=-2.5 StartZ=0 EndX=22.4544 EndY=-2.5 EndZ=0
  constraints (19):
    c: PointOnObject(g0,g-1)
    c: Coincident(g0,g1)
    c: Horizontal(g1)
    c: Coincident(g1,g2)
    c: Vertical(g2)
    c: Coincident(g2,g3)
    c: Horizontal(g3)
    c: Coincident(g3,g4)
    c: Vertical(g4)
    c: Coincident(g4,g5)
    c: Coincident(g5,g0)
    c: Horizontal(g5)
    c: Horizontal(g0,g0)
    c: DistanceY(g1) = -2.5
    c: DistanceX(g0) = 17
    c: Diameter(g0) = 12
    c: Equal(g5,g4)
    c: DistanceX(g1,g1) = 20
    c: Equal(g1,g5)
FEATURE [PartDesign::Pocket] Pocket011
  BaseFeature = -> Pocket001
  Direction = (0,1,-2e-16)
  Length = 16
  Length2 = 5
  Midplane = true
  Placement = pos=(0,0,0) rot=(1,0,0;1.5708rad)
  Profile = -> Sketch029
  ReferenceAxis = -> Sketch029 [N_Axis]
  Suppressed = false
  Type = 0
FEATURE [PartDesign::Body] Body002  label="CrankShaft"
  AllowCompound = false
  Group = -> [Sketch002,Pad,Sketch003,Pad001,Sketch004,Pad002,Sketch005,Pocket001,Sketch029,Pocket011]
  Origin = -> Origin002
  Placement = pos=(0,-18,0) rot=(0,1,0;2.79253rad)
  Tip = -> Pocket011
FEATURE [Sketcher::SketchObject] Sketch030
  AttachmentSupport = -> [XZ_Plane015]
  FullyConstrained = true
  MapMode = 5
  Placement = pos=(0,0,0) rot=(1,0,0;1.5708rad)
  sketch-geometry (2):
    g0: Circle CenterX=0 CenterY=0 CenterZ=0 NormalX=0 NormalY=0 NormalZ=1 AngleXU=0 Radius=2.6
    g1: Circle CenterX=0 CenterY=0 CenterZ=0 NormalX=0 NormalY=0 NormalZ=1 AngleXU=0 Radius=5
  constraints (4):
    c: Coincident(g0,g-1)
    c: Coincident(g1,g0)
    c: Diameter(g1) = 10
    c: Diameter(g0) = 5.2
FEATURE [PartDesign::Pad] Pad015
  Direction = (0,-1,2e-16)
  Length = 0.4
  Length2 = 10
  Placement = pos=(0,0,0) rot=(1,0,0;1.5708rad)
  Profile = -> Sketch030
  ReferenceAxis = -> Sketch030 [N_Axis]
  Suppressed = false
  Type = 0
FEATURE [PartDesign::Body] Body015  label="Washer5mm"
  AllowCompound = false
  Group = -> [Sketch030,Pad015]
  Origin = -> Origin015
  Tip = -> Pad015
FEATURE [Sketcher::SketchObject] Sketch031
  AttachmentSupport = -> [XY_Plane016]
  FullyConstrained = true
  MapMode = 5
  sketch-geometry (6):
    g0: LineSegment StartX=0 StartY=-1.5 StartZ=0 EndX=4.5 EndY=-1.5 EndZ=0
    g1: LineSegment StartX=4.5 StartY=-1.5 StartZ=0 EndX=4.5 EndY=0 EndZ=0
    g2: LineSegment StartX=4.5 StartY=0 StartZ=0 EndX=2.5 EndY=0 EndZ=0
    g3: LineSegment StartX=2.5 StartY=0 StartZ=0 EndX=2.5 EndY=10.5 EndZ=0
    g4: LineSegment StartX=2.5 StartY=10.5 StartZ=0 EndX=0 EndY=10.5 EndZ=0
    g5: LineSegment StartX=0 StartY=10.5 StartZ=0 EndX=0 EndY=-1.5 EndZ=0
  constraints (18):
    c: PointOnObject(g0,g-2)
    c: Horizontal(g0)
    c: Coincident(g0,g1)
    c: PointOnObject(g1,g-1)
    c: Coincident(g1,g2)
    c: PointOnObject(g2,g-1)
    c: Coincident(g2,g3)
    c: Vertical(g3)
    c: Coincident(g3,g4)
    c: PointOnObject(g4,g-2)
    c: Horizontal(g4)
    c: Coincident(g4,g5)
    c: Coincident(g5,g0)
    c: DistanceX(g3) = 2.5
    c: DistanceY(g3,g3) = 10.5
    c: Vertical(g1)
    c: DistanceY(g1,g1) = 1.5
    c: DistanceX(g2,g2) = 2
FEATURE [PartDesign::Revolution] Revolution
  Angle = 360
  Angle2 = 60
  Axis = (0,1,0)
  Base = (0,0,0)
  Profile = -> Sketch031
  ReferenceAxis = -> Sketch031 [V_Axis]
  Reversed = true
  Suppressed = false
  Type = 0
FEATURE [Sketcher::SketchObject] Sketch032
  AttachmentSupport = -> [XY_Plane016]
  FullyConstrained = true
  MapMode = 5
  sketch-geometry (15):
    g0: LineSegment StartX=-5.5 StartY=0 StartZ=0 EndX=-5.5 EndY=-3 EndZ=0
    g1: LineSegment StartX=-5.5 StartY=-3 StartZ=0 EndX=-2.5 EndY=-3 EndZ=0
    g2: LineSegment StartX=-2.5 StartY=-3 StartZ=0 EndX=-2.5 EndY=0 EndZ=0
    g3: LineSegment StartX=-2.5 StartY=0 StartZ=0 EndX=-5.5 EndY=0 EndZ=0
    g4: LineSegment StartX=2.5 StartY=0 StartZ=0 EndX=2.5 EndY=-3 EndZ=0
    g5: LineSegment StartX=2.5 StartY=-3 StartZ=0 EndX=5.5 EndY=-3 EndZ=0
    g6: LineSegment StartX=5.5 StartY=-3 StartZ=0 EndX=5.5 EndY=0 EndZ=0
    g7: LineSegment StartX=5.5 StartY=0 StartZ=0 EndX=2.5 EndY=0 EndZ=0
    g8: LineSegment StartX=1 StartY=7.42265 StartZ=0 EndX=1 EndY=8.57735 EndZ=0
    g9: LineSegment StartX=1 StartY=8.57735 StartZ=0 EndX=0 EndY=9.1547 EndZ=0
    g10: LineSegment StartX=0 StartY=9.1547 StartZ=0 EndX=-1 EndY=8.57735 EndZ=0
    g11: LineSegment StartX=-1 StartY=8.57735 StartZ=0 EndX=-1 EndY=7.42265 EndZ=0
    g12: LineSegment StartX=-1 StartY=7.42265 StartZ=0 EndX=0 EndY=6.8453 EndZ=0
    g13: LineSegment StartX=0 StartY=6.8453 StartZ=0 EndX=1 EndY=7.42265 EndZ=0
    g14: Circle CenterX=0 CenterY=8 CenterZ=0 NormalX=0 NormalY=0 NormalZ=1 AngleXU=0 Radius=1.1547
  constraints (40):
    c: Coincident(g0,g1)
    c: Coincident(g1,g2)
    c: Coincident(g2,g3)
    c: Coincident(g3,g0)
    c: Vertical(g0)
    c: Vertical(g2)
    c: Horizontal(g1)
    c: Horizontal(g3)
    c: PointOnObject(g0,g-1)
    c: Coincident(g4,g5)
    c: Coincident(g5,g6)
    c: Coincident(g6,g7)
    c: Coincident(g7,g4)
    c: Vertical(g4)
    c: Vertical(g6)
    c: Horizontal(g5)
    c: Horizontal(g7)
    c: Equal(g6,g5)
    c: Equal(g5,g1)
    c: Equal(g1,g2)
    c: Symmetric(g2,g4,g-2)
    c: DistanceX(g2,g4) = 5
    c: DistanceX(g7,g7) = 3
    c: Coincident(g8,g9)
    c: Coincident(g9,g10)
    c: Coincident(g10,g11)
    c: Coincident(g11,g12)
    c: Coincident(g12,g13)
    c: Coincident(g13,g8)
    c: Equal(g8, g9-g13) x5
    c: PointOnObject(g8,g14)
    c: PointOnObject(g9,g14)
    c: PointOnObject(g10,g14)
    c: PointOnObject(g11,g14)
    c: PointOnObject(g12,g14)
    c: PointOnObject(g13,g14)
    c: PointOnObject(g14,g-2)
    c: Vertical(g8)
    c: DistanceX(g11,g8) = 2
    c: DistanceY(g14) = 8
FEATURE [PartDesign::Pocket] Pocket012
  BaseFeature = -> Revolution
  Direction = (0,0,-1)
  Length = 5
  Length2 = 5
  Midplane = true
  Profile = -> Sketch032
  ReferenceAxis = -> Sketch032 [N_Axis]
  Suppressed = false
  Type = 1
FEATURE [PartDesign::Body] Body016  label="EarPin"
  AllowCompound = false
  Group = -> [Sketch031,Revolution,Sketch032,Pocket012]
  Origin = -> Origin016
  Placement = pos=(-75,-10.5,38) rot=(0,0,1;0rad)
  Tip = -> Pocket012
FEATURE [Sketcher::SketchObject] Sketch033
  AttachmentSupport = -> [XY_Plane017]
  FullyConstrained = true
  MapMode = 5
  sketch-geometry (6):
    g0: LineSegment StartX=0 StartY=-2 StartZ=0 EndX=5.5 EndY=-2 EndZ=0
    g1: LineSegment StartX=5.5 StartY=-2 StartZ=0 EndX=5.5 EndY=0 EndZ=0
    g2: LineSegment StartX=5.5 StartY=0 StartZ=0 EndX=2.5 EndY=0 EndZ=0
    g3: LineSegment StartX=2.5 StartY=0 StartZ=0 EndX=2.5 EndY=13.5 EndZ=0
    g4: LineSegment StartX=2.5 StartY=13.5 StartZ=0 EndX=0 EndY=13.5 EndZ=0
    g5: LineSegment StartX=0 StartY=13.5 StartZ=0 EndX=0 EndY=-2 EndZ=0
  constraints (18):
    c: PointOnObject(g0,g-2)
    c: Horizontal(g0)
    c: Coincident(g0,g1)
    c: PointOnObject(g1,g-1)
    c: Coincident(g1,g2)
    c: PointOnObject(g2,g-1)
    c: Coincident(g2,g3)
    c: Vertical(g3)
    c: Coincident(g3,g4)
    c: PointOnObject(g4,g-2)
    c: Horizontal(g4)
    c: Coincident(g4,g5)
    c: Coincident(g5,g0)
    c: DistanceX(g3) = 2.5
    c: DistanceY(g3,g3) = 13.5
    c: Vertical(g1)
    c: DistanceY(g1,g1) = 2
    c: DistanceX(g2,g2) = 3
FEATURE [PartDesign::Revolution] Revolution001
  Angle = 360
  Angle2 = 60
  Axis = (0,1,0)
  Base = (0,0,0)
  Profile = -> Sketch033
  ReferenceAxis = -> Sketch033 [V_Axis]
  Reversed = true
  Suppressed = false
  Type = 0
FEATURE [Sketcher::SketchObject] Sketch034
  AttachmentSupport = -> [XY_Plane017]
  FullyConstrained = true
  MapMode = 5
  sketch-geometry (11):
    g0: LineSegment StartX=2.5 StartY=0 StartZ=0 EndX=2.5 EndY=-4 EndZ=0
    g1: LineSegment StartX=2.5 StartY=-4 StartZ=0 EndX=6.5 EndY=-4 EndZ=0
    g2: LineSegment StartX=6.5 StartY=-4 StartZ=0 EndX=6.5 EndY=0 EndZ=0
    g3: LineSegment StartX=6.5 StartY=0 StartZ=0 EndX=2.5 EndY=0 EndZ=0
    g4: LineSegment StartX=1 StartY=10.4226 StartZ=0 EndX=1 EndY=11.5774 EndZ=0
    g5: LineSegment StartX=1 StartY=11.5774 StartZ=0 EndX=-3.6595e-12 EndY=12.1547 EndZ=0
    g6: LineSegment StartX=-3.6595e-12 StartY=12.1547 StartZ=0 EndX=-1 EndY=11.5774 EndZ=0
    g7: LineSegment StartX=-1 StartY=11.5774 StartZ=0 EndX=-1 EndY=10.4226 EndZ=0
    g8: LineSegment StartX=-1 StartY=10.4226 StartZ=0 EndX=-2.93721e-11 EndY=9.8453 EndZ=0
    g9: LineSegment StartX=-2.93721e-11 StartY=9.8453 StartZ=0 EndX=1 EndY=10.4226 EndZ=0
    g10: Circle CenterX=0 CenterY=11 CenterZ=0 NormalX=0 NormalY=0 NormalZ=1 AngleXU=0 Radius=1.1547
  constraints (29):
    c: Coincident(g0,g1)
    c: Coincident(g1,g2)
    c: Coincident(g2,g3)
    c: Coincident(g3,g0)
    c: Vertical(g0)
    c: Vertical(g2)
    c: Horizontal(g1)
    c: Horizontal(g3)
    c: Equal(g2,g1)
    c: DistanceX(g3,g3) = 4
    c: Coincident(g4,g5)
    c: Coincident(g5,g6)
    c: Coincident(g6,g7)
    c: Coincident(g7,g8)
    c: Coincident(g8,g9)
    c: Coincident(g9,g4)
    c: Equal(g4, g5-g9) x5
    c: PointOnObject(g4,g10)
    c: PointOnObject(g5,g10)
    c: PointOnObject(g6,g10)
    c: PointOnObject(g7,g10)
    c: PointOnObject(g8,g10)
    c: PointOnObject(g9,g10)
    c: PointOnObject(g10,g-2)
    c: Vertical(g4)
    c: DistanceX(g7,g4) = 2
    c: DistanceY(g10) = 11
    c: DistanceX(g0) = 2.5
    c: PointOnObject(g0,g-1)
FEATURE [PartDesign::Pocket] Pocket013
  BaseFeature = -> Revolution001
  Direction = (0,0,-1)
  Length = 5
  Length2 = 5
  Midplane = true
  Profile = -> Sketch034
  ReferenceAxis = -> Sketch034 [N_Axis]
  Suppressed = false
  Type = 1
FEATURE [PartDesign::Body] Body017  label="WheelPin"
  AllowCompound = false
  Group = -> [Sketch033,Revolution001,Sketch034,Pocket013]
  Origin = -> Origin017
  Placement = pos=(-90,8.5,37.5) rot=(0,0,1;3.14159rad)
  Tip = -> Pocket013
FEATURE [PartDesign::FeaturePython] InvoluteGear003  label="m2.5-13T"  # WARN: FeaturePython — macro-defined, semantics opaque (R4)
  AttacherType = Attacher::AttachEngine3D
  Placement = pos=(0,0,0) rot=(1,0,0;1.5708rad)
  Suppressed = false
  angular_backlash = 0.352589
  backlash = 0.1
  beta = 0
  clearance = 0.25
  da = 37.5
  df = 26.25
  double_helix = false
  dw = 32.5
  head = 0
  head_fillet = 0
  height = 5
  module = 2.5
  numpoints = 6
  pressure_angle = 20
  properties_from_tool = false
  reversed_backlash = false
  root_fillet = 0
  shift = 0
  simple = false
  teeth = 13
  transverse_pitch = 7.85398
  undercut = false
  version = 0.0.4
  expr: angular_backlash = backlash / dw * 360 ° / pi
  expr: dw = teeth * module
FEATURE [Sketcher::SketchObject] Sketch035
  AttachmentSupport = -> [XZ_Plane019]
  FullyConstrained = true
  MapMode = 5
  Placement = pos=(0,0,0) rot=(1,0,0;1.5708rad)
  sketch-geometry (14):
    g0: ArcOfCircle CenterX=0 CenterY=0 CenterZ=0 NormalX=0 NormalY=0 NormalZ=1 AngleXU=0 Radius=6 StartAngle=0.339837 EndAngle=1.75456
    g1: ArcOfCircle CenterX=0 CenterY=0 CenterZ=0 NormalX=0 NormalY=0 NormalZ=1 AngleXU=0 Radius=11 StartAngle=0.182835 EndAngle=1.91156
    g2: LineSegment StartX=10.8167 StartY=2 StartZ=0 EndX=5.65685 EndY=2 EndZ=0
    g3: LineSegment StartX=-1.09638 StartY=5.89898 StartZ=0 EndX=-3.67628 EndY=10.3675 EndZ=0
    g4: LineSegment StartX=0 StartY=0 StartZ=0 EndX=-5.40833 EndY=9.3675 EndZ=0
    g5: LineSegment StartX=-5.40833 StartY=9.3675 StartZ=0 EndX=-3.67628 EndY=10.3675 EndZ=0
    g6: LineSegment StartX=10.8167 StartY=2 StartZ=0 EndX=10.8167 EndY=0 EndZ=0
    g7: LineSegment StartX=0 StartY=-4.15692 StartZ=0 EndX=3.6 EndY=-2.07846 EndZ=0
    g8: LineSegment StartX=3.6 StartY=-2.07846 StartZ=0 EndX=3.6 EndY=2.07846 EndZ=0
    g9: LineSegment StartX=3.6 StartY=2.07846 StartZ=0 EndX=-4e-16 EndY=4.15692 EndZ=0
    g10: LineSegment StartX=-4e-16 StartY=4.15692 StartZ=0 EndX=-3.6 EndY=2.07846 EndZ=0
    g11: LineSegment StartX=-3.6 StartY=2.07846 StartZ=0 EndX=-3.6 EndY=-2.07846 EndZ=0
    g12: LineSegment StartX=-3.6 StartY=-2.07846 StartZ=0 EndX=0 EndY=-4.15692 EndZ=0
    g13: Circle CenterX=0 CenterY=0 CenterZ=0 NormalX=0 NormalY=0 NormalZ=1 AngleXU=0 Radius=4.15692
  constraints (37):
    c: Coincident(g0,g-1)
    c: Coincident(g1,g0)
    c: Coincident(g2,g1)
    c: Coincident(g2,g0)
    c: Coincident(g3,g0)
    c: Coincident(g3,g1)
    c: Coincident(g4,g0)
    c: Coincident(g5,g4)
    c: Coincident(g5,g1)
    c: Parallel(g4,g3)
    c: Perpendicular(g4,g5)
    c: Angle(g-1,g4) = 2.0944
    c: Horizontal(g2)
    c: Coincident(g6,g1)
    c: PointOnObject(g6,g-1)
    c: Vertical(g6)
    c: Equal(g6,g5)
    c: Diameter(g0) = 12
    c: Diameter(g1) = 22
    c: DistanceY(g6,g6) = 2
    c: Coincident(g7,g8)
    c: Coincident(g8,g9)
    c: Coincident(g9,g10)
    c: Coincident(g10,g11)
    c: Coincident(g11,g12)
    c: Coincident(g12,g7)
    c: Equal(g7, g8-g12) x5
    c: PointOnObject(g7,g13)
    c: PointOnObject(g8,g13)
    c: PointOnObject(g9,g13)
    c: PointOnObject(g10,g13)
    c: PointOnObject(g11,g13)
    c: PointOnObject(g12,g13)
    c: Coincident(g13,g0)
    c: PointOnObject(g12,g-2)
    c: DistanceX(g11,g7) = 7.2
    c: Diameter(g13) = 8.31384
FEATURE [PartDesign::Pocket] Pocket014  label="120deg-sector002"
  BaseFeature = -> InvoluteGear003
  Direction = (0,1,-2e-16)
  Length = 5
  Length2 = 5
  Midplane = true
  Placement = pos=(0,0,0) rot=(1,0,0;1.5708rad)
  Profile = -> Sketch035
  ReferenceAxis = -> Sketch035 [N_Axis]
  Refine = true
  Suppressed = false
  Type = 1
FEATURE [PartDesign::PolarPattern] PolarPattern002
  Angle = 360
  Axis = -> Sketch035 [N_Axis]
  BaseFeature = -> Pocket014
  Mode = 0
  Occurrences = 3
  Offset = 120
  Originals = -> [Pocket014]
  Placement = pos=(0,0,0) rot=(1,0,0;1.5708rad)
  Refine = true
  Suppressed = false
  TransformMode = 0
FEATURE [PartDesign::Body] Body019  label="M2.5-13T"
  AllowCompound = false
  Group = -> [InvoluteGear003,Sketch035,Pocket014,PolarPattern002]
  Origin = -> Origin019
  Placement = pos=(60,-42,0) rot=(0,1,0;3.22886rad)
  Tip = -> PolarPattern002
FEATURE [Sketcher::SketchObject] Sketch036
  AttachmentSupport = -> [XZ_Plane020]
  FullyConstrained = true
  MapMode = 5
  Placement = pos=(0,0,0) rot=(1,0,0;1.5708rad)
  sketch-geometry (2):
    g0: ArcOfCircle CenterX=0 CenterY=0 CenterZ=0 NormalX=0 NormalY=0 NormalZ=1 AngleXU=0 Radius=3 StartAngle=5.23599 EndAngle=10.472
    g1: LineSegment StartX=-1.5 StartY=-2.59808 StartZ=0 EndX=1.5 EndY=-2.59808 EndZ=0
  constraints (6):
    c: Coincident(g0,g-1)
    c: Coincident(g0,g1)
    c: Coincident(g1,g0)
    c: Horizontal(g1)
    c: Diameter(g0) = 6
    c: DistanceX(g1,g1) = 3
FEATURE [PartDesign::Pad] Pad016
  Direction = (0,-1,2e-16)
  Length = 50
  Length2 = 10
  Placement = pos=(0,0,0) rot=(1,0,0;1.5708rad)
  Profile = -> Sketch036
  ReferenceAxis = -> Sketch036 [N_Axis]
  Suppressed = false
  Type = 0
FEATURE [PartDesign::Body] Body020  label="Pin6mm"
  AllowCompound = false
  Group = -> [Sketch036,Pad016]
  Origin = -> Origin020
  Placement = pos=(30,-32.5,-14.5) rot=(0,0,1;0rad)
  Tip = -> Pad016
FEATURE [Sketcher::SketchObject] Sketch037
  AttachmentSupport = -> [XZ_Plane021]
  FullyConstrained = true
  MapMode = 5
  Placement = pos=(0,0,0) rot=(1,0,0;1.5708rad)
  sketch-geometry (11):
    g0: ArcOfCircle CenterX=0 CenterY=0 CenterZ=0 NormalX=0 NormalY=0 NormalZ=1 AngleXU=0 Radius=3.15 StartAngle=5.20871 EndAngle=10.4993
    g1: ArcOfCircle CenterX=0 CenterY=0 CenterZ=0 NormalX=0 NormalY=0 NormalZ=1 AngleXU=0 Radius=5 StartAngle=5.31721 EndAngle=6.05405
    g2: ArcOfCircle CenterX=0 CenterY=0 CenterZ=0 NormalX=0 NormalY=0 NormalZ=1 AngleXU=0 Radius=5 StartAngle=3.37072 EndAngle=4.10757
    g3: LineSegment StartX=-1.5 StartY=-2.76993 StartZ=0 EndX=-2.84308 EndY=-4.11301 EndZ=0
    g4: LineSegment StartX=1.5 StartY=-2.76993 StartZ=0 EndX=2.84308 EndY=-4.11301 EndZ=0
    g5: LineSegment StartX=0 StartY=0 StartZ=0 EndX=0 EndY=-1.26993 EndZ=0
    g6: LineSegment StartX=-7 StartY=8 StartZ=0 EndX=-7 EndY=11 EndZ=0
    g7: LineSegment StartX=-7 StartY=11 StartZ=0 EndX=7 EndY=11 EndZ=0
    g8: LineSegment StartX=-7 StartY=8 StartZ=0 EndX=-4.86932 EndY=-1.13566 EndZ=0
    g9: LineSegment StartX=7 StartY=11 StartZ=0 EndX=7 EndY=8 EndZ=0
    g10: LineSegment StartX=7 StartY=8 StartZ=0 EndX=4.86932 EndY=-1.13566 EndZ=0
  constraints (29):
    c: Coincident(g3,g0)
    c: Coincident(g3,g2)
    c: Coincident(g4,g0)
    c: Coincident(g4,g1)
    c: Perpendicular(g3,g4)
    c: Coincident(g0,g2)
    c: Coincident(g0,g1)
    c: Coincident(g5,g0)
    c: Vertical(g5)
    c: Symmetric(g1,g2,g5)
    c: Horizontal(g0,g0)
    c: Diameter(g0) = 6.3
    c: Diameter(g1) = 10
    c: PointOnObject(g5,g4)
    c: DistanceX(g0,g0) = 3
    c: Vertical(g6)
    c: Coincident(g6,g7)
    c: Coincident(g7,g9)
    c: DistanceY(g6) = 8
    c: DistanceY(g6,g6) = 3
    c: Coincident(g0,g-1)
    c: Coincident(g6,g8)
    c: Coincident(g9,g10)
    c: Vertical(g9)
    c: Equal(g9,g6)
    c: Tangent(g10,g1) = 1.5708
    c: Tangent(g8,g2) = -1.5708
    c: Symmetric(g6,g7,g-2)
    c: DistanceX(g7,g7) = 14
FEATURE [PartDesign::Pad] Pad017
  Direction = (0,-1,2e-16)
  Length = 14.6
  Length2 = 10
  Placement = pos=(0,0,0) rot=(1,0,0;1.5708rad)
  Profile = -> Sketch037
  ReferenceAxis = -> Sketch037 [N_Axis]
  Suppressed = false
  Type = 0
FEATURE [Sketcher::SketchObject] Sketch039
  AttachmentSupport = -> [YZ_Plane021]
  FullyConstrained = true
  MapMode = 5
  Placement = pos=(0,0,0) rot=(0.57735,0.57735,0.57735;2.0944rad)
  sketch-geometry (12):
    g0: LineSegment StartX=-14.6 StartY=12 StartZ=0 EndX=-14.6 EndY=8 EndZ=0
    g1: LineSegment StartX=-14.6 StartY=8 StartZ=0 EndX=-8.4 EndY=8 EndZ=0
    g2: LineSegment StartX=-8.4 StartY=8 StartZ=0 EndX=-8.4 EndY=8.8 EndZ=0
    g3: LineSegment StartX=-8.4 StartY=8.8 StartZ=0 EndX=-9.1 EndY=8.8 EndZ=0
    g4: LineSegment StartX=-9.1 StartY=8.8 StartZ=0 EndX=-9.1 EndY=9.5 EndZ=0
    g5: LineSegment StartX=-9.1 StartY=9.5 StartZ=0 EndX=-5.5 EndY=9.5 EndZ=0
    g6: LineSegment StartX=-5.5 StartY=9.5 StartZ=0 EndX=-5.5 EndY=8.8 EndZ=0
    g7: LineSegment StartX=-5.5 StartY=8.8 StartZ=0 EndX=-6.2 EndY=8.8 EndZ=0
    g8: LineSegment StartX=-6.2 StartY=8.8 StartZ=0 EndX=-6.2 EndY=8 EndZ=0
    g9: LineSegment StartX=-6.2 StartY=8 StartZ=0 EndX=0 EndY=8 EndZ=0
    g10: LineSegment StartX=0 StartY=8 StartZ=0 EndX=0 EndY=12 EndZ=0
    g11: LineSegment StartX=0 StartY=12 StartZ=0 EndX=-14.6 EndY=12 EndZ=0
  constraints (36):
    c: Vertical(g0)
    c: Horizontal(g1)
    c: Coincident(g1,g2)
    c: Vertical(g2)
    c: Coincident(g2,g3)
    c: Horizontal(g3)
    c: Coincident(g3,g4)
    c: Vertical(g4)
    c: Coincident(g4,g5)
    c: Horizontal(g5)
    c: Coincident(g5,g6)
    c: Vertical(g6)
    c: Coincident(g6,g7)
    c: Horizontal(g7)
    c: Coincident(g7,g8)
    c: Vertical(g8)
    c: Coincident(g8,g9)
    c: PointOnObject(g9,g-2)
    c: Horizontal(g9)
    c: Coincident(g9,g10)
    c: PointOnObject(g10,g-2)
    c: Coincident(g10,g11)
    c: Coincident(g11,g0)
    c: Horizontal(g11)
    c: DistanceY(g9) = 8
    c: Horizontal(g8,g1)
    c: Equal(g2,g8)
    c: Equal(g3,g7)
    c: DistanceX(g11,g11) = 14.6
    c: DistanceY(g10,g10) = 4
    c: DistanceY(g6,g6) = 0.7
    c: DistanceY(g8,g8) = 0.8
    c: Coincident(g1,g0)
    c: Equal(g9,g1)
    c: DistanceX(g5,g5) = 3.6
    c: DistanceX(g3,g3) = 0.7
FEATURE [PartDesign::Pocket] Pocket016
  BaseFeature = -> Pad017
  Direction = (-1,0,0)
  Length = 5
  Length2 = 5
  Midplane = true
  Placement = pos=(0,0,0) rot=(1,0,0;1.5708rad)
  Profile = -> Sketch039
  ReferenceAxis = -> Sketch039 [N_Axis]
  Suppressed = false
  Type = 1
FEATURE [PartDesign::Body] Body021  label="BottomHinge"
  AllowCompound = false
  Group = -> [Sketch037,Pad017,Sketch039,Pocket016]
  Origin = -> Origin021
  Placement = pos=(30,-51.7,-14.5) rot=(0,0,1;0rad)
  Tip = -> Pocket016
FEATURE [Sketcher::SketchObject] Sketch040
  AttachmentSupport = -> [XZ_Plane022]
  FullyConstrained = true
  MapMode = 5
  Placement = pos=(0,0,0) rot=(1,0,0;1.5708rad)
  sketch-geometry (2):
    g0: Circle CenterX=0 CenterY=0 CenterZ=0 NormalX=0 NormalY=0 NormalZ=1 AngleXU=0 Radius=3.05
    g1: Circle CenterX=0 CenterY=0 CenterZ=0 NormalX=0 NormalY=0 NormalZ=1 AngleXU=0 Radius=6
  constraints (4):
    c: Coincident(g0,g-1)
    c: Coincident(g1,g0)
    c: Diameter(g0) = 6.1
    c: Diameter(g1) = 12
FEATURE [PartDesign::Pad] Pad018
  Direction = (0,-1,2e-16)
  Length = 0.6
  Length2 = 10
  Placement = pos=(0,0,0) rot=(1,0,0;1.5708rad)
  Profile = -> Sketch040
  ReferenceAxis = -> Sketch040 [N_Axis]
  Suppressed = false
  Type = 0
FEATURE [PartDesign::Body] Body022  label="Washer6mm"
  AllowCompound = false
  Group = -> [Sketch040,Pad018]
  Origin = -> Origin022
  Placement = pos=(30,-67,-14.5) rot=(0,0,1;0rad)
  Tip = -> Pad018
FEATURE [Sketcher::SketchObject] Sketch041
  AttachmentSupport = -> [XZ_Plane023]
  FullyConstrained = true
  MapMode = 5
  Placement = pos=(0,0,0) rot=(1,0,0;1.5708rad)
  sketch-geometry (1):
    g0: Circle CenterX=0 CenterY=0 CenterZ=0 NormalX=0 NormalY=0 NormalZ=1 AngleXU=0 Radius=2.5
  constraints (2):
    c: Coincident(g0,g-1)
    c: Diameter(g0) = 5
FEATURE [PartDesign::Pad] Pad019
  Direction = (0,-1,2e-16)
  Length = 56
  Length2 = 10
  Midplane = true
  Placement = pos=(0,0,0) rot=(1,0,0;1.5708rad)
  Profile = -> Sketch041
  ReferenceAxis = -> Sketch041 [N_Axis]
  Refine = true
  Suppressed = false
  Type = 0
FEATURE [Sketcher::SketchObject] Sketch042
  AttachmentSupport = -> [XZ_Plane023]
  FullyConstrained = true
  MapMode = 5
  Placement = pos=(0,0,0) rot=(1,0,0;1.5708rad)
  sketch-geometry (5):
    g0: ArcOfCircle CenterX=-4.57107 CenterY=0 CenterZ=0 NormalX=0 NormalY=0 NormalZ=1 AngleXU=0 Radius=7.5 StartAngle=5.94335 EndAngle=7.85398
    g1: LineSegment StartX=-30 StartY=7.5 StartZ=0 EndX=-4.57109 EndY=7.5 EndZ=0
    g2: LineSegment StartX=-33.3952 StartY=-2.5 StartZ=0 EndX=2.5 EndY=-2.5 EndZ=0
    g3: ArcOfCircle CenterX=-30 CenterY=0 CenterZ=0 NormalX=0 NormalY=0 NormalZ=1 AngleXU=0 Radius=7.5 StartAngle=1.5708 EndAngle=3.09252
    g4: LineSegment StartX=-33.3952 StartY=-2.5 StartZ=0 EndX=-37.491 EndY=0.367882 EndZ=0
  constraints (16):
    c: PointOnObject(g0,g-1)
    c: PointOnObject(g3,g-1)
    c: Coincident(g1,g0)
    c: Horizontal(g1)
    c: Diameter(g0) = 15
    c: Coincident(g2,g0)
    c: Horizontal(g2)
    c: Tangent(g1,g3) = 1.5708
    c: DistanceX(g0) = 2.5
    c: DistanceX(g3) = -30
    c: DistanceY(g0) = -2.5
    c: Equal(g3,g0)
    c: Coincident(g2,g4)
    c: Coincident(g4,g3)
    c: Angle(g4,g-1) = 0.610865
    c: Distance(g4) = 5
FEATURE [PartDesign::Pad] Pad020
  BaseFeature = -> Pad019
  Direction = (0,-1,2e-16)
  Length = 26
  Length2 = 10
  Midplane = true
  Placement = pos=(0,0,0) rot=(1,0,0;1.5708rad)
  Profile = -> Sketch042
  ReferenceAxis = -> Sketch042 [N_Axis]
  Refine = true
  Suppressed = false
  Type = 0
FEATURE [Sketcher::SketchObject] Sketch043
  AttachmentOffset = pos=(0,0,-13) rot=(0,0,1;0rad)
  AttachmentSupport = -> [XZ_Plane023]
  FullyConstrained = true
  MapMode = 5
  Placement = pos=(0,13,-2.9e-15) rot=(1,0,0;1.5708rad)
  sketch-geometry (7):
    g0: ArcOfCircle CenterX=-9.36516 CenterY=23.1796 CenterZ=0 NormalX=0 NormalY=0 NormalZ=1 AngleXU=0 Radius=5 StartAngle=0.306362 EndAngle=2.80949
    g1: LineSegment StartX=-22.2 StartY=1.3 StartZ=0 EndX=-14.092 EndY=24.8098 EndZ=0
    g2: LineSegment StartX=2.8 StartY=1.3 StartZ=0 EndX=-4.59798 EndY=24.6876 EndZ=0
    g3: LineSegment StartX=-9.36516 StartY=23.1796 StartZ=0 EndX=0 EndY=0 EndZ=0
    g4: Circle CenterX=-9.36516 CenterY=23.1796 CenterZ=0 NormalX=0 NormalY=0 NormalZ=1 AngleXU=0 Radius=2.7
    g5: LineSegment StartX=-22.2 StartY=1.3 StartZ=0 EndX=2.8 EndY=1.3 EndZ=0
    g6: LineSegment StartX=0 StartY=0 StartZ=0 EndX=134.442 EndY=54.318 EndZ=0
  constraints (18):
    c: Tangent(g0,g1) = 1.5708
    c: Tangent(g0,g2) = -1.5708
    c: Coincident(g3,g0)
    c: Distance(g3) = 25
    c: Angle(g-2,g3) = 0.383972
    c: Diameter(g0) = 10
    c: Coincident(g4,g0)
    c: Diameter(g4) = 5.4
    c: Coincident(g1,g5)
    c: Coincident(g5,g2)
    c: DistanceX(g2) = 2.8
    c: DistanceX(g5,g5) = 25
    c: Coincident(g3,g-1)
    c: Horizontal(g5)
    c: DistanceY(g2) = 1.3
    c: Coincident(g3,g6)
    c: Distance(g6) = 145
    c: Perpendicular(g3,g6)
FEATURE [PartDesign::Pad] Pad021  label="CrankEar"
  BaseFeature = -> Pad020
  Direction = (0,-1,2e-16)
  Length = 4
  Length2 = 10
  Placement = pos=(0,0,0) rot=(1,0,0;1.5708rad)
  Profile = -> Sketch043
  ReferenceAxis = -> Sketch043 [N_Axis]
  Refine = true
  Suppressed = false
  Type = 0
FEATURE [Sketcher::SketchObject] Sketch044
  AttachmentSupport = -> [XZ_Plane023]
  FullyConstrained = true
  MapMode = 5
  Placement = pos=(0,0,0) rot=(1,0,0;1.5708rad)
  sketch-geometry (6):
    g0: LineSegment StartX=-71.6583 StartY=-2.5 StartZ=0 EndX=-71.6583 EndY=37.5 EndZ=0
    g1: LineSegment StartX=-71.6583 StartY=37.5 StartZ=0 EndX=11.6583 EndY=37.5 EndZ=0
    g2: LineSegment StartX=11.6583 StartY=37.5 StartZ=0 EndX=11.6583 EndY=-2.5 EndZ=0
    g3: LineSegment StartX=11.6583 StartY=-2.5 StartZ=0 EndX=-28.3417 EndY=-2.5 EndZ=0
    g4: ArcOfCircle CenterX=-30 CenterY=0 CenterZ=0 NormalX=0 NormalY=0 NormalZ=1 AngleXU=0 Radius=3 StartAngle=5.29807 EndAngle=10.4099
    g5: LineSegment StartX=-31.6583 StartY=-2.5 StartZ=0 EndX=-71.6583 EndY=-2.5 EndZ=0
  constraints (19):
    c: PointOnObject(g4,g-1)
    c: Vertical(g0)
    c: Coincident(g0,g1)
    c: Horizontal(g1)
    c: Coincident(g1,g2)
    c: Vertical(g2)
    c: Coincident(g2,g3)
    c: Coincident(g3,g4)
    c: Horizontal(g3)
    c: DistanceY(g0) = -2.5
    c: Equal(g3,g2)
    c: DistanceX(g4) = -30
    c: Diameter(g4) = 6
    c: Coincident(g4,g5)
    c: Coincident(g5,g0)
    c: Horizontal(g5)
    c: Horizontal(g4,g3)
    c: Equal(g3,g5)
    c: DistanceX(g5,g5) = 40
FEATURE [PartDesign::Pocket] Pocket017
  BaseFeature = -> Pad021
  Direction = (0,1,-2e-16)
  Length = 15
  Length2 = 5
  Midplane = true
  Placement = pos=(0,0,0) rot=(1,0,0;1.5708rad)
  Profile = -> Sketch044
  ReferenceAxis = -> Sketch044 [N_Axis]
  Refine = true
  Suppressed = false
  Type = 0
FEATURE [Sketcher::SketchObject] Sketch045
  AttachmentSupport = -> [XZ_Plane023]
  FullyConstrained = true
  MapMode = 5
  Placement = pos=(0,0,0) rot=(1,0,0;1.5708rad)
  expr: Constraints[11] = Sketch044.Constraints[11]
  expr: Constraints[18] = Sketch044.Constraints[18]
  expr: Constraints[9] = Sketch044.Constraints[9]
  sketch-geometry (6):
    g0: LineSegment StartX=-77.0711 StartY=-2.5 StartZ=0 EndX=-77.0711 EndY=37.5 EndZ=0
    g1: LineSegment StartX=-77.0711 StartY=37.5 StartZ=0 EndX=17.0711 EndY=37.5 EndZ=0
    g2: LineSegment StartX=17.0711 StartY=37.5 StartZ=0 EndX=17.0711 EndY=-2.5 EndZ=0
    g3: LineSegment StartX=17.0711 StartY=-2.5 StartZ=0 EndX=-22.9289 EndY=-2.5 EndZ=0
    g4: ArcOfCircle CenterX=-30 CenterY=0 CenterZ=0 NormalX=0 NormalY=0 NormalZ=1 AngleXU=0 Radius=7.5 StartAngle=5.94335 EndAngle=9.76461
    g5: LineSegment StartX=-37.0711 StartY=-2.5 StartZ=0 EndX=-77.0711 EndY=-2.5 EndZ=0
  constraints (19):
    c: PointOnObject(g4,g-1)
    c: Vertical(g0)
    c: Coincident(g0,g1)
    c: Horizontal(g1)
    c: Coincident(g1,g2)
    c: Vertical(g2)
    c: Coincident(g2,g3)
    c: Coincident(g3,g4)
    c: Horizontal(g3)
    c: DistanceY(g0) = -2.5
    c: Equal(g3,g2)
    c: DistanceX(g4) = -30
    c: Diameter(g4) = 15
    c: Coincident(g4,g5)
    c: Coincident(g5,g0)
    c: Horizontal(g5)
    c: Horizontal(g4,g3)
    c: Equal(g3,g5)
    c: DistanceX(g5,g5) = 40
FEATURE [PartDesign::Pocket] Pocket018
  BaseFeature = -> Pocket017
  Direction = (0,1,-2e-16)
  Length = 16
  Length2 = 5
  Midplane = true
  Placement = pos=(0,0,0) rot=(1,0,0;1.5708rad)
  Profile = -> Sketch045
  ReferenceAxis = -> Sketch045 [N_Axis]
  Refine = true
  Suppressed = false
  Type = 0
FEATURE [PartDesign::Body] Body023  label="CrankShaftL"
  AllowCompound = false
  Group = -> [Sketch041,Pad019,Sketch042,Pad020,Sketch043,Pad021,Sketch044,Pocket017,Sketch045,Pocket018]
  Origin = -> Origin023
  Placement = pos=(-61.5,-59,-13) rot=(0,1,0;0.698132rad)
  Tip = -> Pocket018
FEATURE [Sketcher::SketchObject] Sketch046
  AttachmentSupport = -> [XZ_Plane025]
  FullyConstrained = false
  MapMode = 5
  Placement = pos=(0,0,0) rot=(1,0,0;1.5708rad)
  expr: Constraints[104] = Sketch024.Constraints[150]
  expr: Constraints[126] = Sketch024.Constraints[172]
  expr: Constraints[134] = Sketch024.Constraints[180]
  expr: Constraints[135] = Sketch024.Constraints[181]
  expr: Constraints[136] = Sketch024.Constraints[182]
  expr: Constraints[150] = Sketch024.Constraints[198]
  expr: Constraints[156] = Sketch024.Constraints[205]
  expr: Constraints[47] = Sketch024.Constraints[63]
  expr: Constraints[5] = Sketch024.Constraints[20]
  expr: Constraints[68] = Sketch024.Constraints[109]
  expr: Constraints[69] = Sketch024.Constraints[110]
  expr: Constraints[71] = Sketch024.Constraints[112]
  expr: Constraints[72] = Sketch024.Constraints[113]
  expr: Constraints[73] = Sketch024.Constraints[114]
  expr: Constraints[74] = Sketch024.Constraints[118]
  expr: Constraints[75] = Sketch024.Constraints[120]
  expr: Constraints[77] = Sketch024.Constraints[122]
  expr: Constraints[7] = Sketch024.Constraints[22]
  expr: Constraints[8] = Sketch024.Constraints[23]
  expr: Constraints[9] = Sketch024.Constraints[24]
  sketch-geometry (64):
    g0: LineSegment StartX=-30 StartY=-35 StartZ=0 EndX=-30 EndY=-25 EndZ=0
    g1: LineSegment StartX=90 StartY=-25 StartZ=0 EndX=90 EndY=-35 EndZ=0
    g2: LineSegment StartX=90 StartY=-35 StartZ=0 EndX=81.7609 EndY=-35 EndZ=0
    g3: LineSegment StartX=81.7609 StartY=-35 StartZ=0 EndX=83.5218 EndY=-31.95 EndZ=0
    g4: LineSegment StartX=83.5218 StartY=-31.95 StartZ=0 EndX=81.7609 EndY=-28.9 EndZ=0
    g5: LineSegment StartX=81.7609 StartY=-28.9 StartZ=0 EndX=78.2391 EndY=-28.9 EndZ=0
    g6: LineSegment StartX=78.2391 StartY=-28.9 StartZ=0 EndX=76.4782 EndY=-31.95 EndZ=0
    g7: LineSegment StartX=76.4782 StartY=-31.95 StartZ=0 EndX=78.2391 EndY=-35 EndZ=0
    g8: LineSegment StartX=78.2391 StartY=-35 StartZ=0 EndX=81.7609 EndY=-35 EndZ=0
    g9: Circle CenterX=80 CenterY=-31.95 CenterZ=0 NormalX=0 NormalY=0 NormalZ=1 AngleXU=0 Radius=3.52184
    g10: LineSegment StartX=31.7609 StartY=-35 StartZ=0 EndX=33.5218 EndY=-31.95 EndZ=0
    g11: LineSegment StartX=33.5218 StartY=-31.95 StartZ=0 EndX=31.7609 EndY=-28.9 EndZ=0
    g12: LineSegment StartX=31.7609 StartY=-28.9 StartZ=0 EndX=28.2391 EndY=-28.9 EndZ=0
    g13: LineSegment StartX=28.2391 StartY=-28.9 StartZ=0 EndX=26.4782 EndY=-31.95 EndZ=0
    g14: LineSegment StartX=26.4782 StartY=-31.95 StartZ=0 EndX=28.2391 EndY=-35 EndZ=0
    g15: LineSegment StartX=28.2391 StartY=-35 StartZ=0 EndX=31.7609 EndY=-35 EndZ=0
    g16: Circle CenterX=30 CenterY=-31.95 CenterZ=0 NormalX=0 NormalY=0 NormalZ=1 AngleXU=0 Radius=3.52184
    g17: LineSegment StartX=-21.7609 StartY=-35 StartZ=0 EndX=-30 EndY=-35 EndZ=0
    g18: LineSegment StartX=78.2391 StartY=-35 StartZ=0 EndX=31.7609 EndY=-35 EndZ=0
    g19: LineSegment StartX=28.2391 StartY=-35 StartZ=0 EndX=-18.2391 EndY=-35 EndZ=0
    g20: LineSegment StartX=40.6569 StartY=-28.9 StartZ=0 EndX=70.2307 EndY=-28.9 EndZ=0
    g21: LineSegment StartX=-26 StartY=-23.9 StartZ=0 EndX=-14 EndY=-23.9 EndZ=0
    g22: LineSegment StartX=-14 StartY=-23.9 StartZ=0 EndX=-9 EndY=-28.9 EndZ=0
    g23: LineSegment StartX=-9 StartY=-28.9 StartZ=0 EndX=19.3431 EndY=-28.9 EndZ=0
    g24: LineSegment StartX=19.3431 StartY=-28.9 StartZ=0 EndX=25 EndY=-23.2431 EndZ=0
    g25: LineSegment StartX=25 StartY=-23.2431 StartZ=0 EndX=25 EndY=-14.5 EndZ=0
    g26: LineSegment StartX=35 StartY=-14.5 StartZ=0 EndX=35 EndY=-23.2431 EndZ=0
    g27: LineSegment StartX=35 StartY=-23.2431 StartZ=0 EndX=40.6569 EndY=-28.9 EndZ=0
    g28: Circle CenterX=30 CenterY=-14.5 CenterZ=0 NormalX=0 NormalY=0 NormalZ=1 AngleXU=0 Radius=3.1
    g29: LineSegment StartX=-26 StartY=-23.9 StartZ=0 EndX=-31 EndY=-28.9 EndZ=0
    g30: LineSegment StartX=-31 StartY=-28.9 StartZ=0 EndX=-39.2437 EndY=-28.9 EndZ=0
    g31: LineSegment StartX=-39.2437 StartY=-28.9 StartZ=0 EndX=-57.8988 EndY=-9.53142 EndZ=0
    g32: ArcOfCircle CenterX=-61.5 CenterY=-13 CenterZ=0 NormalX=0 NormalY=0 NormalZ=1 AngleXU=0 Radius=5 StartAngle=0.766636 EndAngle=2.37496
    g33: LineSegment StartX=-65.1012 StartY=-9.53142 StartZ=0 EndX=-80 EndY=-25 EndZ=0
    g34: LineSegment StartX=-80 StartY=-25 StartZ=0 EndX=-80 EndY=-35 EndZ=0
    g35: LineSegment StartX=-80 StartY=-35 StartZ=0 EndX=-71.7609 EndY=-35 EndZ=0
    g36: LineSegment StartX=-18.2391 StartY=-35 StartZ=0 EndX=-16.4782 EndY=-31.95 EndZ=0
    g37: LineSegment StartX=-16.4782 StartY=-31.95 StartZ=0 EndX=-18.2391 EndY=-28.9 EndZ=0
    g38: LineSegment StartX=-18.2391 StartY=-28.9 StartZ=0 EndX=-21.7609 EndY=-28.9 EndZ=0
    g39: LineSegment StartX=-21.7609 StartY=-28.9 StartZ=0 EndX=-23.5218 EndY=-31.95 EndZ=0
    g40: LineSegment StartX=-23.5218 StartY=-31.95 StartZ=0 EndX=-21.7609 EndY=-35 EndZ=0
    g41: LineSegment StartX=-21.7609 StartY=-35 StartZ=0 EndX=-18.2391 EndY=-35 EndZ=0
    g42: Circle CenterX=-20 CenterY=-31.95 CenterZ=0 NormalX=0 NormalY=0 NormalZ=1 AngleXU=0 Radius=3.52184
    g43: LineSegment StartX=-68.2391 StartY=-35 StartZ=0 EndX=-66.4782 EndY=-31.95 EndZ=0
    g44: LineSegment StartX=-66.4782 StartY=-31.95 StartZ=0 EndX=-68.2391 EndY=-28.9 EndZ=0
    g45: LineSegment StartX=-68.2391 StartY=-28.9 StartZ=0 EndX=-71.7609 EndY=-28.9 EndZ=0
    g46: LineSegment StartX=-71.7609 StartY=-28.9 StartZ=0 EndX=-73.5218 EndY=-31.95 EndZ=0
    g47: LineSegment StartX=-73.5218 StartY=-31.95 StartZ=0 EndX=-71.7609 EndY=-35 EndZ=0
    g48: LineSegment StartX=-71.7609 StartY=-35 StartZ=0 EndX=-68.2391 EndY=-35 EndZ=0
    g49: Circle CenterX=-70 CenterY=-31.95 CenterZ=0 NormalX=0 NormalY=0 NormalZ=1 AngleXU=0 Radius=3.52184
    g50: LineSegment StartX=-21.7609 StartY=-35 StartZ=0 EndX=-68.2391 EndY=-35 EndZ=0
    g51: LineSegment StartX=-71.9985 StartY=-23.9 StartZ=0 EndX=-65.9985 EndY=-23.9 EndZ=0
    g52: LineSegment StartX=-46.1857 StartY=-28.9 StartZ=0 EndX=-58.0314 EndY=-16.6012 EndZ=0
    g53: ArcOfCircle CenterX=-61.5 CenterY=-13 CenterZ=0 NormalX=0 NormalY=0 NormalZ=1 AngleXU=0 Radius=5 StartAngle=3.94575 EndAngle=5.47902
    g54: LineSegment StartX=-64.9686 StartY=-16.6012 StartZ=0 EndX=-71.9985 EndY=-23.9 EndZ=0
    g55: Circle CenterX=-61.5 CenterY=-13 CenterZ=0 NormalX=0 NormalY=0 NormalZ=1 AngleXU=0 Radius=2.7
    g56: LineSegment StartX=-65.9985 StartY=-23.9 StartZ=0 EndX=-60.9985 EndY=-28.9 EndZ=0
    g57: LineSegment StartX=-60.9985 StartY=-28.9 StartZ=0 EndX=-46.1857 EndY=-28.9 EndZ=0
    g58: LineSegment StartX=-61.5 StartY=-13 StartZ=0 EndX=-61.5 EndY=-8 EndZ=0
    g59: GeomPoint X=-51.0015 Y=-23.9 Z=0
    g60: ArcOfCircle CenterX=30 CenterY=-14.5 CenterZ=0 NormalX=0 NormalY=0 NormalZ=1 AngleXU=0 Radius=5 StartAngle=6.28319 EndAngle=9.42478
    g61: LineSegment StartX=35 StartY=-23.2431 StartZ=0 EndX=40 EndY=-28.2431 EndZ=0
    g62: LineSegment StartX=40 StartY=-28.2431 StartZ=0 EndX=40 EndY=-35 EndZ=0
    g63: LineSegment StartX=40 StartY=-35 StartZ=0 EndX=31.7609 EndY=-35 EndZ=0
  constraints (165):
    c: Vertical(g0)
    c: Vertical(g1)
    c: Coincident(g1,g2)
    c: Coincident(g17,g0)
    c: Horizontal(g2)
    c: DistanceY(g1,g1) = 10
    c: Equal(g1,g0)
    c: DistanceY(g1) = -35
    c: DistanceX(g0) = -30
    c: DistanceX(g1) = 90
    c: PointOnObject(g19,g2)
    c: Coincident(g3,g4)
    c: Coincident(g4,g5)
    c: Coincident(g5,g6)
    c: Coincident(g6,g7)
    c: Coincident(g7,g8)
    c: Coincident(g8,g3)
    c: Equal(g3, g4-g8) x5
    c: PointOnObject(g3,g9)
    c: PointOnObject(g4,g9)
    c: PointOnObject(g5,g9)
    c: PointOnObject(g6,g9)
    c: PointOnObject(g7,g9)
    c: PointOnObject(g8,g9)
    c: Coincident(g10,g11)
    c: Coincident(g11,g12)
    c: Coincident(g12,g13)
    c: Coincident(g13,g14)
    c: Coincident(g14,g15)
    c: Coincident(g15,g10)
    c: Equal(g10, g11-g15) x5
    c: PointOnObject(g10,g16)
    c: PointOnObject(g11,g16)
    c: PointOnObject(g12,g16)
    c: PointOnObject(g13,g16)
    c: PointOnObject(g14,g16)
    c: PointOnObject(g15,g16)
    c: Horizontal(g15)
    c: Equal(g16,g9)
    c: DistanceX(g9,g1) = 10
    c: Coincident(g2,g3)
    c: Horizontal(g8)
    c: Coincident(g7,g18)
    c: Coincident(g18,g10)
    c: Horizontal(g18)
    c: Coincident(g14,g19)
    c: Horizontal(g17)
    c: Equal(g19,g18)
    c: Coincident(g27,g20)
    c: Horizontal(g20)
    c: Coincident(g21,g22)
    c: Coincident(g22,g23)
    c: Coincident(g23,g24)
    c: Horizontal(g23)
    c: Horizontal(g24,g27)
    c: Horizontal(g27,g11)
    c: Coincident(g24,g25)
    c: Coincident(g26,g27)
    c: Vertical(g25)
    c: Vertical(g26)
    c: DistanceX(g25,g26) = 10
    c: DistanceX(g16,g26) = 5
    c: Equal(g26,g25)
    c: Angle(g24,g23) = 2.35619
    c: Angle(g20,g27) = 2.35619
    c: Distance(g24) = 8
    c: Angle(g23,g22) = 2.35619
    c: Diameter(g28) = 6.2
    c: Vertical(g28,g16)
    c: DistanceY(g14,g28) = 20.5
    c: Coincident(g29,g30)
    c: Horizontal(g30)
    c: Coincident(g30,g31)
    c: Tangent(g31,g32) = -1.5708
    c: Tangent(g32,g33) = -1.5708
    c: Coincident(g33,g34)
    c: Vertical(g34)
    c: Coincident(g34,g35)
    c: Horizontal(g35)
    c: Coincident(g36,g37)
    c: Coincident(g37,g38)
    c: Coincident(g38,g39)
    c: Coincident(g39,g40)
    c: Coincident(g40,g41)
    c: Coincident(g41,g36)
    c: Equal(g36, g37-g41) x5
    c: PointOnObject(g36,g42)
    c: PointOnObject(g37,g42)
    c: PointOnObject(g38,g42)
    c: PointOnObject(g39,g42)
    c: PointOnObject(g40,g42)
    c: PointOnObject(g41,g42)
    c: DistanceY(g36,g37) = 6.1
    c: Horizontal(g41)
    c: Coincident(g43,g44)
    c: Coincident(g44,g45)
    c: Coincident(g45,g46)
    c: Coincident(g46,g47)
    c: Coincident(g47,g48)
    c: Coincident(g48,g43)
    c: Equal(g43, g44-g48) x5
    c: PointOnObject(g43,g49)
    c: PointOnObject(g44,g49)
    c: PointOnObject(g45,g49)
    c: PointOnObject(g46,g49)
    c: PointOnObject(g47,g49)
    c: PointOnObject(g48,g49)
    c: Horizontal(g48)
    c: Coincident(g36,g19)
    c: Coincident(g40,g17)
    c: DistanceX(g0,g42) = 10
    c: Equal(g49,g42)
    c: Coincident(g17,g50)
    c: Coincident(g50,g43)
    c: Horizontal(g50)
    c: Equal(g50,g19)
    c: Equal(g34,g1)
    c: Coincident(g35,g47)
    c: DistanceX(g34,g49) = 10
    c: DistanceY(g34,g32) = 22
    c: DistanceX(g32) = -61.5
    c: Horizontal(g22,g37)
    c: Horizontal(g22,g29)
    c: Horizontal(g51)
    c: Coincident(g51,g56)
    c: Perpendicular(g52,g53) = 4.71239
    c: Coincident(g53,g54)
    c: Coincident(g51,g54)
    c: Parallel(g54,g33)
    c: Horizontal(g52,g30)
    c: Coincident(g53,g32)
    c: Equal(g53,g32)
    c: PointOnObject(g32,g54)
    c: Coincident(g57,g52)
    c: DistanceY(g45,g51) = 5
    c: Coincident(g55,g32)
    c: Parallel(g52,g31)
    c: Coincident(g56,g57)
    c: Parallel(g56,g22)
    c: Horizontal(g57)
    c: DistanceX(g51,g51) = 6
    c: Coincident(g58,g32)
    c: PointOnObject(g58,g32)
    c: Vertical(g58)
    c: PointOnObject(g59,g52)
    c: Symmetric(g51,g59,g58)
    c: Horizontal(g21)
    c: Horizontal(g51,g21)
    c: Diameter(g55) = 5.4
    c: Diameter(g32) = 10
    c: DistanceX(g21,g21) = 12
    c: Coincident(g60,g28)
    c: Coincident(g60,g26)
    c: Tangent(g60,g25) = 1.5708
    c: Coincident(g26,g61)
    c: PointOnObject(g61,g27)
    c: Coincident(g61,g62)
    c: PointOnObject(g62,g18)
    c: Vertical(g62)
    c: Coincident(g62,g63)
    c: Coincident(g63,g10)
    c: DistanceX(g16,g62) = 10
    c: Coincident(g29,g21)
    c: Parallel(g29,g24)
    c: DistanceX(g42,g21) = 6
FEATURE [PartDesign::Pad] Pad022
  Direction = (0,-1,2e-16)
  Length = 5
  Length2 = 10
  Placement = pos=(0,0,0) rot=(1,0,0;1.5708rad)
  Profile = -> Sketch046
  ReferenceAxis = -> Sketch046 [N_Axis]
  Suppressed = false
  Type = 0
FEATURE [PartDesign::Body] Body025  label="Wall000"
  AllowCompound = false
  Group = -> [Sketch046,Pad022]
  Origin = -> Origin025
  Placement = pos=(0,-75.5,0) rot=(0,0,1;0rad)
  Tip = -> Pad022
FEATURE [Sketcher::SketchObject] Sketch047
  AttachmentSupport = -> [XZ_Plane026]
  FullyConstrained = true
  MapMode = 5
  Placement = pos=(0,0,0) rot=(1,0,0;1.5708rad)
  sketch-geometry (6):
    g0: ArcOfCircle CenterX=0 CenterY=0 CenterZ=0 NormalX=0 NormalY=0 NormalZ=1 AngleXU=0 Radius=5 StartAngle=3.66519 EndAngle=8.90118
    g1: ArcOfCircle CenterX=-45 CenterY=0 CenterZ=0 NormalX=0 NormalY=0 NormalZ=1 AngleXU=0 Radius=5 StartAngle=0.523599 EndAngle=5.75959
    g2: LineSegment StartX=-4.33013 StartY=-2.5 StartZ=0 EndX=-40.6699 EndY=-2.5 EndZ=0
    g3: LineSegment StartX=-4.33013 StartY=2.5 StartZ=0 EndX=-40.6699 EndY=2.5 EndZ=0
    g4: Circle CenterX=0 CenterY=0 CenterZ=0 NormalX=0 NormalY=0 NormalZ=1 AngleXU=0 Radius=2.7
    g5: Circle CenterX=-45 CenterY=0 CenterZ=0 NormalX=0 NormalY=0 NormalZ=1 AngleXU=0 Radius=2.7
  constraints (17):
    c: Equal(g0,g1)
    c: Coincident(g0,g-1)
    c: PointOnObject(g1,g-1)
    c: Coincident(g4,g0)
    c: Coincident(g5,g1)
    c: Equal(g5,g4)
    c: Diameter(g4) = 5.4
    c: Diameter(g0) = 10
    c: Coincident(g3,g0)
    c: Coincident(g0,g2)
    c: DistanceY(g0,g0) = 5
    c: DistanceY(g0) = 2.5
    c: Coincident(g3,g1)
    c: Horizontal(g3)
    c: Coincident(g2,g1)
    c: Horizontal(g2)
    c: DistanceX(g1,g0) = 45
FEATURE [PartDesign::Pad] Pad023
  Direction = (0,-1,2e-16)
  Length = 4
  Length2 = 10
  Placement = pos=(0,0,0) rot=(1,0,0;1.5708rad)
  Profile = -> Sketch047
  ReferenceAxis = -> Sketch047 [N_Axis]
  Suppressed = false
  Type = 0
FEATURE [PartDesign::Body] Body026  label="RockerLinkUpper"
  AllowCompound = false
  Group = -> [Sketch047,Pad023]
  Origin = -> Origin026
  Placement = pos=(82.4877,-48,36.2) rot=(0,1,0;0.122173rad)
  Tip = -> Pad023
FEATURE [Sketcher::SketchObject] Sketch048
  AttachmentSupport = -> [XZ_Plane029]
  FullyConstrained = true
  MapMode = 5
  Placement = pos=(0,0,0) rot=(1,0,0;1.5708rad)
  sketch-geometry (6):
    g0: ArcOfCircle CenterX=0 CenterY=0 CenterZ=0 NormalX=0 NormalY=0 NormalZ=1 AngleXU=0 Radius=5 StartAngle=3.66519 EndAngle=8.90118
    g1: ArcOfCircle CenterX=-95 CenterY=0 CenterZ=0 NormalX=0 NormalY=0 NormalZ=1 AngleXU=0 Radius=5 StartAngle=0.523599 EndAngle=5.75959
    g2: LineSegment StartX=-4.33013 StartY=-2.5 StartZ=0 EndX=-90.6699 EndY=-2.5 EndZ=0
    g3: LineSegment StartX=-4.33013 StartY=2.5 StartZ=0 EndX=-90.6699 EndY=2.5 EndZ=0
    g4: Circle CenterX=0 CenterY=0 CenterZ=0 NormalX=0 NormalY=0 NormalZ=1 AngleXU=0 Radius=2.6
    g5: Circle CenterX=-95 CenterY=0 CenterZ=0 NormalX=0 NormalY=0 NormalZ=1 AngleXU=0 Radius=2.6
  constraints (17):
    c: Equal(g0,g1)
    c: Coincident(g0,g-1)
    c: PointOnObject(g1,g-1)
    c: Coincident(g4,g0)
    c: Coincident(g5,g1)
    c: Equal(g5,g4)
    c: Diameter(g4) = 5.2
    c: Diameter(g0) = 10
    c: Coincident(g3,g0)
    c: Coincident(g0,g2)
    c: DistanceY(g0,g0) = 5
    c: DistanceY(g0) = 2.5
    c: Coincident(g3,g1)
    c: Horizontal(g3)
    c: Coincident(g2,g1)
    c: Horizontal(g2)
    c: DistanceX(g1,g0) = 95
FEATURE [PartDesign::Pad] Pad024
  Direction = (0,-1,2e-16)
  Length = 4
  Length2 = 10
  Placement = pos=(0,0,0) rot=(1,0,0;1.5708rad)
  Profile = -> Sketch048
  ReferenceAxis = -> Sketch048 [N_Axis]
  Refine = true
  Suppressed = false
  Type = 0
FEATURE [Sketcher::SketchObject] Sketch049
  AttachmentSupport = -> [XZ_Plane029]
  FullyConstrained = true
  MapMode = 5
  Placement = pos=(0,0,0) rot=(1,0,0;1.5708rad)
  expr: Constraints[0] = Sketch048.Constraints[6]
  expr: Constraints[1] = Sketch048.Constraints[6]
  expr: Constraints[6] = Sketch048.Constraints[7]
  sketch-geometry (4):
    g0: Circle CenterX=0 CenterY=0 CenterZ=0 NormalX=0 NormalY=0 NormalZ=1 AngleXU=0 Radius=2.6
    g1: Circle CenterX=-95 CenterY=0 CenterZ=0 NormalX=0 NormalY=0 NormalZ=1 AngleXU=0 Radius=2.6
    g2: Circle CenterX=0 CenterY=0 CenterZ=0 NormalX=0 NormalY=0 NormalZ=1 AngleXU=0 Radius=5
    g3: Circle CenterX=-95 CenterY=0 CenterZ=0 NormalX=0 NormalY=0 NormalZ=1 AngleXU=0 Radius=5
  constraints (9):
    c: Diameter(g0) = 5.2
    c: Diameter(g1) = 5.2
    c: Diameter(g2) = 10
    c: Coincident(g0,g2)
    c: Coincident(g0,g-1)
    c: Coincident(g3,g1)
    c: Diameter(g3) = 10
    c: PointOnObject(g1,g-1)
    c: DistanceX(g1) = -95
FEATURE [PartDesign::Pad] Pad025
  BaseFeature = -> Pad024
  Direction = (0,-1,2e-16)
  Length = 3
  Length2 = 10
  Placement = pos=(0,0,0) rot=(1,0,0;1.5708rad)
  Profile = -> Sketch049
  ReferenceAxis = -> Sketch049 [N_Axis]
  Refine = true
  Reversed = true
  Suppressed = false
  Type = 0
FEATURE [Sketcher::SketchObject] Sketch050
  AttachmentSupport = -> [XY_Plane029]
  FullyConstrained = true
  MapMode = 5
  sketch-geometry (14):
    g0: LineSegment StartX=0.5 StartY=-1.86603 StartZ=0 EndX=1 EndY=-1 EndZ=0
    g1: LineSegment StartX=1 StartY=-1 StartZ=0 EndX=0.5 EndY=-0.133975 EndZ=0
    g2: LineSegment StartX=0.5 StartY=-0.133975 StartZ=0 EndX=-0.5 EndY=-0.133975 EndZ=0
    g3: LineSegment StartX=-0.5 StartY=-0.133975 StartZ=0 EndX=-1 EndY=-1 EndZ=0
    g4: LineSegment StartX=-1 StartY=-1 StartZ=0 EndX=-0.5 EndY=-1.86603 EndZ=0
    g5: LineSegment StartX=-0.5 StartY=-1.86603 StartZ=0 EndX=0.5 EndY=-1.86603 EndZ=0
    g6: Circle CenterX=0 CenterY=-1 CenterZ=0 NormalX=0 NormalY=0 NormalZ=1 AngleXU=0 Radius=1
    g7: LineSegment StartX=-94.5 StartY=-1.86603 StartZ=0 EndX=-94 EndY=-1 EndZ=0
    g8: LineSegment StartX=-94 StartY=-1 StartZ=0 EndX=-94.5 EndY=-0.133975 EndZ=0
    g9: LineSegment StartX=-94.5 StartY=-0.133975 StartZ=0 EndX=-95.5 EndY=-0.133975 EndZ=0
    g10: LineSegment StartX=-95.5 StartY=-0.133975 StartZ=0 EndX=-96 EndY=-1 EndZ=0
    g11: LineSegment StartX=-96 StartY=-1 StartZ=0 EndX=-95.5 EndY=-1.86603 EndZ=0
    g12: LineSegment StartX=-95.5 StartY=-1.86603 StartZ=0 EndX=-94.5 EndY=-1.86603 EndZ=0
    g13: Circle CenterX=-95 CenterY=-1 CenterZ=0 NormalX=0 NormalY=0 NormalZ=1 AngleXU=0 Radius=1
  constraints (34):
    c: Coincident(g0,g1)
    c: Coincident(g1,g2)
    c: Coincident(g2,g3)
    c: Coincident(g3,g4)
    c: Coincident(g4,g5)
    c: Coincident(g5,g0)
    c: Equal(g0, g1-g5) x5
    c: PointOnObject(g0,g6)
    c: PointOnObject(g1,g6)
    c: PointOnObject(g2,g6)
    c: PointOnObject(g3,g6)
    c: PointOnObject(g4,g6)
    c: PointOnObject(g5,g6)
    c: Horizontal(g5)
    c: Diameter(g6) = 2
    c: Coincident(g7,g8)
    c: Coincident(g8,g9)
    c: Coincident(g9,g10)
    c: Coincident(g10,g11)
    c: Coincident(g11,g12)
    c: Coincident(g12,g7)
    c: Equal(g7, g8-g12) x5
    c: PointOnObject(g7,g13)
    c: PointOnObject(g8,g13)
    c: PointOnObject(g9,g13)
    c: PointOnObject(g10,g13)
    c: PointOnObject(g11,g13)
    c: PointOnObject(g12,g13)
    c: Horizontal(g12)
    c: Equal(g13,g6)
    c: PointOnObject(g6,g-2)
    c: DistanceY(g6,g-1) = 1
    c: Horizontal(g13,g6)
    c: DistanceX(g13,g6) = 95
FEATURE [PartDesign::Pocket] Pocket019
  BaseFeature = -> Pad025
  Direction = (0,0,-1)
  Length = 5
  Length2 = 5
  Midplane = true
  Placement = pos=(0,0,0) rot=(1,0,0;1.5708rad)
  Profile = -> Sketch050
  ReferenceAxis = -> Sketch050 [N_Axis]
  Suppressed = false
  Type = 1
FEATURE [PartDesign::Body] Body027  label="RockerLinkLower"
  AllowCompound = false
  Group = -> [Sketch048,Pad024,Sketch049,Pad025,Sketch050,Pocket019]
  Origin = -> Origin029
  Placement = pos=(37.4855,-42,41.8972) rot=(0,1,0;5.96903rad)
  Tip = -> Pocket019
FEATURE [Sketcher::SketchObject] Sketch051
  AttachmentSupport = -> [XY_Plane030]
  FullyConstrained = true
  MapMode = 5
  sketch-geometry (6):
    g0: LineSegment StartX=0 StartY=-1.5 StartZ=0 EndX=4.5 EndY=-1.5 EndZ=0
    g1: LineSegment StartX=4.5 StartY=-1.5 StartZ=0 EndX=4.5 EndY=0 EndZ=0
    g2: LineSegment StartX=4.5 StartY=0 StartZ=0 EndX=2.5 EndY=0 EndZ=0
    g3: LineSegment StartX=2.5 StartY=0 StartZ=0 EndX=2.5 EndY=17.5 EndZ=0
    g4: LineSegment StartX=2.5 StartY=17.5 StartZ=0 EndX=0 EndY=17.5 EndZ=0
    g5: LineSegment StartX=0 StartY=17.5 StartZ=0 EndX=0 EndY=-1.5 EndZ=0
  constraints (18):
    c: PointOnObject(g0,g-2)
    c: Horizontal(g0)
    c: Coincident(g0,g1)
    c: PointOnObject(g1,g-1)
    c: Coincident(g1,g2)
    c: PointOnObject(g2,g-1)
    c: Coincident(g2,g3)
    c: Vertical(g3)
    c: Coincident(g3,g4)
    c: PointOnObject(g4,g-2)
    c: Horizontal(g4)
    c: Coincident(g4,g5)
    c: Coincident(g5,g0)
    c: DistanceX(g3) = 2.5
    c: DistanceY(g3,g3) = 17.5
    c: Vertical(g1)
    c: DistanceY(g1,g1) = 1.5
    c: DistanceX(g2,g2) = 2
FEATURE [PartDesign::Revolution] Revolution002
  Angle = 360
  Angle2 = 60
  Axis = (0,1,0)
  Base = (0,0,0)
  Profile = -> Sketch051
  ReferenceAxis = -> Sketch051 [V_Axis]
  Reversed = true
  Suppressed = false
  Type = 0
FEATURE [Sketcher::SketchObject] Sketch052
  AttachmentSupport = -> [XY_Plane030]
  FullyConstrained = true
  MapMode = 5
  sketch-geometry (15):
    g0: LineSegment StartX=-5.5 StartY=0 StartZ=0 EndX=-5.5 EndY=-3 EndZ=0
    g1: LineSegment StartX=-5.5 StartY=-3 StartZ=0 EndX=-2.5 EndY=-3 EndZ=0
    g2: LineSegment StartX=-2.5 StartY=-3 StartZ=0 EndX=-2.5 EndY=0 EndZ=0
    g3: LineSegment StartX=-2.5 StartY=0 StartZ=0 EndX=-5.5 EndY=0 EndZ=0
    g4: LineSegment StartX=2.5 StartY=0 StartZ=0 EndX=2.5 EndY=-3 EndZ=0
    g5: LineSegment StartX=2.5 StartY=-3 StartZ=0 EndX=5.5 EndY=-3 EndZ=0
    g6: LineSegment StartX=5.5 StartY=-3 StartZ=0 EndX=5.5 EndY=0 EndZ=0
    g7: LineSegment StartX=5.5 StartY=0 StartZ=0 EndX=2.5 EndY=0 EndZ=0
    g8: LineSegment StartX=1 StartY=7.42265 StartZ=0 EndX=1 EndY=8.57735 EndZ=0
    g9: LineSegment StartX=1 StartY=8.57735 StartZ=0 EndX=0 EndY=9.1547 EndZ=0
    g10: LineSegment StartX=0 StartY=9.1547 StartZ=0 EndX=-1 EndY=8.57735 EndZ=0
    g11: LineSegment StartX=-1 StartY=8.57735 StartZ=0 EndX=-1 EndY=7.42265 EndZ=0
    g12: LineSegment StartX=-1 StartY=7.42265 StartZ=0 EndX=0 EndY=6.8453 EndZ=0
    g13: LineSegment StartX=0 StartY=6.8453 StartZ=0 EndX=1 EndY=7.42265 EndZ=0
    g14: Circle CenterX=0 CenterY=8 CenterZ=0 NormalX=0 NormalY=0 NormalZ=1 AngleXU=0 Radius=1.1547
  constraints (40):
    c: Coincident(g0,g1)
    c: Coincident(g1,g2)
    c: Coincident(g2,g3)
    c: Coincident(g3,g0)
    c: Vertical(g0)
    c: Vertical(g2)
    c: Horizontal(g1)
    c: Horizontal(g3)
    c: PointOnObject(g0,g-1)
    c: Coincident(g4,g5)
    c: Coincident(g5,g6)
    c: Coincident(g6,g7)
    c: Coincident(g7,g4)
    c: Vertical(g4)
    c: Vertical(g6)
    c: Horizontal(g5)
    c: Horizontal(g7)
    c: Equal(g6,g5)
    c: Equal(g5,g1)
    c: Equal(g1,g2)
    c: Symmetric(g2,g4,g-2)
    c: DistanceX(g2,g4) = 5
    c: DistanceX(g7,g7) = 3
    c: Coincident(g8,g9)
    c: Coincident(g9,g10)
    c: Coincident(g10,g11)
    c: Coincident(g11,g12)
    c: Coincident(g12,g13)
    c: Coincident(g13,g8)
    c: Equal(g8, g9-g13) x5
    c: PointOnObject(g8,g14)
    c: PointOnObject(g9,g14)
    c: PointOnObject(g10,g14)
    c: PointOnObject(g11,g14)
    c: PointOnObject(g12,g14)
    c: PointOnObject(g13,g14)
    c: PointOnObject(g14,g-2)
    c: Vertical(g8)
    c: DistanceX(g11,g8) = 2
    c: DistanceY(g14) = 8
FEATURE [PartDesign::Pocket] Pocket020
  BaseFeature = -> Revolution002
  Direction = (0,0,-1)
  Length = 5
  Length2 = 5
  Midplane = true
  Profile = -> Sketch052
  ReferenceAxis = -> Sketch052 [N_Axis]
  Suppressed = false
  Type = 1
FEATURE [PartDesign::Body] Body028  label="EarPinLong"
  AllowCompound = false
  Group = -> [Sketch051,Revolution002,Sketch052,Pocket020]
  Origin = -> Origin030
  Placement = pos=(9,-52.5,26.5) rot=(0,0,1;0rad)
  Tip = -> Pocket020
FEATURE [PartDesign::FeatureBase] Clone003
  BaseFeature = -> Body016
  Suppressed = false
FEATURE [PartDesign::Body] Body029  label="EarPin001"
  AllowCompound = false
  Group = -> [Clone003]
  Origin = -> Origin031
  Placement = pos=(52,-53,37.5) rot=(0,0,1;0rad)
  Tip = -> Clone003
FEATURE [Sketcher::SketchObject] Sketch053
  AttachmentSupport = -> [XZ_Plane007]
  FullyConstrained = true
  MapMode = 5
  Placement = pos=(0,0,0) rot=(1,0,0;1.5708rad)
  sketch-geometry (14):
    g0: LineSegment StartX=3.5 StartY=9 StartZ=0 EndX=3 EndY=9.86603 EndZ=0
    g1: LineSegment StartX=3 StartY=9.86603 StartZ=0 EndX=2 EndY=9.86603 EndZ=0
    g2: LineSegment StartX=2 StartY=9.86603 StartZ=0 EndX=1.5 EndY=9 EndZ=0
    g3: LineSegment StartX=1.5 StartY=9 StartZ=0 EndX=2 EndY=8.13397 EndZ=0
    g4: LineSegment StartX=2 StartY=8.13397 StartZ=0 EndX=3 EndY=8.13397 EndZ=0
    g5: LineSegment StartX=3 StartY=8.13397 StartZ=0 EndX=3.5 EndY=9 EndZ=0
    g6: Circle CenterX=2.5 CenterY=9 CenterZ=0 NormalX=0 NormalY=0 NormalZ=1 AngleXU=0 Radius=1
    g7: LineSegment StartX=178 StartY=8.13397 StartZ=0 EndX=178.5 EndY=9 EndZ=0
    g8: LineSegment StartX=178.5 StartY=9 StartZ=0 EndX=178 EndY=9.86603 EndZ=0
    g9: LineSegment StartX=178 StartY=9.86603 StartZ=0 EndX=177 EndY=9.86603 EndZ=0
    g10: LineSegment StartX=177 StartY=9.86603 StartZ=0 EndX=176.5 EndY=9 EndZ=0
    g11: LineSegment StartX=176.5 StartY=9 StartZ=0 EndX=177 EndY=8.13397 EndZ=0
    g12: LineSegment StartX=177 StartY=8.13397 StartZ=0 EndX=178 EndY=8.13397 EndZ=0
    g13: Circle CenterX=177.5 CenterY=9 CenterZ=0 NormalX=0 NormalY=0 NormalZ=1 AngleXU=0 Radius=1
  constraints (34):
    c: Coincident(g0,g1)
    c: Coincident(g1,g2)
    c: Coincident(g2,g3)
    c: Coincident(g3,g4)
    c: Coincident(g4,g5)
    c: Coincident(g5,g0)
    c: Equal(g0, g1-g5) x5
    c: PointOnObject(g0,g6)
    c: PointOnObject(g1,g6)
    c: PointOnObject(g2,g6)
    c: PointOnObject(g3,g6)
    c: PointOnObject(g4,g6)
    c: PointOnObject(g5,g6)
    c: Diameter(g6) = 2
    c: Coincident(g7,g8)
    c: Coincident(g8,g9)
    c: Coincident(g9,g10)
    c: Coincident(g10,g11)
    c: Coincident(g11,g12)
    c: Coincident(g12,g7)
    c: Equal(g7, g8-g12) x5
    c: PointOnObject(g7,g13)
    c: PointOnObject(g8,g13)
    c: PointOnObject(g9,g13)
    c: PointOnObject(g10,g13)
    c: PointOnObject(g11,g13)
    c: PointOnObject(g12,g13)
    c: Equal(g6,g13)
    c: Horizontal(g12)
    c: Horizontal(g4)
    c: Horizontal(g6,g13)
    c: DistanceY(g6) = 9
    c: DistanceX(g6) = 2.5
    c: DistanceX(g6,g13) = 175
FEATURE [PartDesign::Pocket] Pocket021
  BaseFeature = -> Pad007
  Direction = (0,1,-2e-16)
  Length = 5
  Length2 = 5
  Midplane = true
  Placement = pos=(0,0,0) rot=(0.57735,0.57735,0.57735;2.0944rad)
  Profile = -> Sketch053
  ReferenceAxis = -> Sketch053 [N_Axis]
  Suppressed = false
  Type = 1
FEATURE [PartDesign::Body] Body007  label="LED-Base"
  AllowCompound = false
  Group = -> [Sketch016,Pad007,Sketch053,Pocket021]
  Origin = -> Origin007
  Placement = pos=(-147,-18,7) rot=(0,0,1;0rad)
  Tip = -> Pocket021
FEATURE [PartDesign::FeatureBase] Clone002
  BaseFeature = -> Body007
  Placement = pos=(-127,-18,7) rot=(0,0,1;0rad)
  Suppressed = false
FEATURE [PartDesign::Body] Body024  label="LED-Base001"
  AllowCompound = false
  Group = -> [Clone002]
  Origin = -> Origin024
  Placement = pos=(-30,18,4) rot=(0,-1,0;0rad)
  Tip = -> Clone002
FEATURE [PartDesign::FeaturePython] InvoluteGear001  label="M2,5_18T"  # WARN: FeaturePython — macro-defined, semantics opaque (R4)
  AttacherType = Attacher::AttachEngine3D
  Placement = pos=(0,7e-15,0) rot=(0,0,1;0rad)
  Suppressed = false
  angular_backlash = 0.254648
  backlash = 0.1
  beta = 0
  clearance = 0.25
  da = 50
  df = 38.75
  double_helix = false
  dw = 45
  head = 0
  head_fillet = 0
  height = 5
  module = 2.5
  numpoints = 6
  pressure_angle = 25
  properties_from_tool = false
  reversed_backlash = false
  root_fillet = 0
  shift = 0
  simple = false
  teeth = 18
  transverse_pitch = 7.85398
  undercut = false
  version = 0.0.4
  expr: angular_backlash = backlash / dw * 360 ° / pi
  expr: dw = teeth * module
FEATURE [PartDesign::Pocket] Pocket003
  BaseFeature = -> InvoluteGear001
  Direction = (0,0,-1)
  Length = 5
  Length2 = 5
  Midplane = true
  Placement = pos=(0,7e-15,0) rot=(0,0,1;0rad)
  Profile = -> Sketch007
  ReferenceAxis = -> Sketch007 [N_Axis]
  Refine = true
  Suppressed = false
  Type = 1
FEATURE [PartDesign::Pad] Pad003
  BaseFeature = -> Pocket003
  Direction = (0,0,1)
  Length = 1
  Length2 = 10
  Placement = pos=(0,7e-15,0) rot=(0,0,1;0rad)
  Profile = -> Sketch010
  ReferenceAxis = -> Sketch010 [N_Axis]
  Refine = true
  Suppressed = false
  Type = 0
FEATURE [PartDesign::Groove] Groove
  Angle = 360
  Angle2 = 60
  Axis = (0,2e-16,1)
  Base = (0,0,0)
  BaseFeature = -> Pad003
  Placement = pos=(0,7e-15,0) rot=(0,0,1;0rad)
  Profile = -> Sketch008
  ReferenceAxis = -> Sketch008 [V_Axis]
  Refine = true
  Suppressed = false
  Type = 0
FEATURE [PartDesign::Pocket] Pocket004
  BaseFeature = -> Groove
  Direction = (0,1,-2e-16)
  Length = 11
  Length2 = 5
  Midplane = true
  Placement = pos=(0,7e-15,0) rot=(0,0,1;0rad)
  Profile = -> Sketch009
  ReferenceAxis = -> Sketch009 [N_Axis]
  Refine = true
  Suppressed = false
  Type = 0
FEATURE [PartDesign::Body] Body003  label="M2.5-18T-11mm"
  AllowCompound = false
  Group = -> [InvoluteGear001,Sketch007,Pocket003,Sketch008,Sketch010,Pad003,Groove,Sketch009,Pocket004]
  Origin = -> Origin003
  Placement = pos=(-90,0,37.5) rot=(0.345437,0.663579,-0.663579;2.47638rad)
  Tip = -> Pocket004
FEATURE [PartDesign::FeatureBase] Clone
  BaseFeature = -> Body003
  Placement = pos=(0,0,0) rot=(1,0,0;1.5708rad)
  Suppressed = false
FEATURE [PartDesign::Body] Body004  label="M2.5-18T001"
  AllowCompound = false
  Group = -> [Clone]
  Origin = -> Origin004
  Placement = pos=(-48.5,0,20) rot=(0,1,0;1.0472rad)
  Tip = -> Clone
FEATURE [PartDesign::FeatureBase] Clone001
  BaseFeature = -> Clone
  Placement = pos=(0,0,0) rot=(1,0,0;1.5708rad)
  Suppressed = false
FEATURE [PartDesign::Body] Body018  label="M2.5-18T002"
  AllowCompound = false
  Group = -> [Clone001]
  Origin = -> Origin018
  Placement = pos=(67.5,-43,38) rot=(0,-1,0;6.14356rad)
  Tip = -> Clone001
FEATURE [Sketcher::SketchObject] Sketch057
  AttachmentSupport = -> [XZ_Plane033]
  FullyConstrained = false
  MapMode = 5
  Placement = pos=(0,0,0) rot=(1,0,0;1.5708rad)
  sketch-geometry (16):
    g0: LineSegment StartX=22 StartY=0 StartZ=0 EndX=22 EndY=6.61508 EndZ=0
    g1: LineSegment StartX=-8.07244 StartY=11 StartZ=0 EndX=-12 EndY=0 EndZ=0
    g2: ArcOfCircle CenterX=4.7 CenterY=4 CenterZ=0 NormalX=0 NormalY=0 NormalZ=1 AngleXU=0 Radius=2.75 StartAngle=2.96706 EndAngle=5.63448
    g3: LineSegment StartX=22 StartY=6.61508 StartZ=0 EndX=12.7 EndY=10 EndZ=0
    g4: LineSegment StartX=1.99178 StartY=4.47753 StartZ=0 EndX=3.09965 EndY=10.7606 EndZ=0
    g5: LineSegment StartX=3.09965 StartY=10.7606 StartZ=0 EndX=2.44187 EndY=11 EndZ=0
    g6: ArcOfCircle CenterX=-5.15813 CenterY=5 CenterZ=0 NormalX=0 NormalY=0 NormalZ=1 AngleXU=0 Radius=2.75 StartAngle=3.05433 EndAngle=5.66865
    g7: LineSegment StartX=-7.89767 StartY=5.23968 StartZ=0 EndX=-7.41465 EndY=10.7606 EndZ=0
    g8: LineSegment StartX=-7.41465 StartY=10.7606 StartZ=0 EndX=-8.07244 EndY=11 EndZ=0
    g9: LineSegment StartX=-12 StartY=0 StartZ=0 EndX=22 EndY=0 EndZ=0
    g10: LineSegment StartX=12.7 StartY=10 StartZ=0 EndX=6.89138 EndY=2.33857 EndZ=0
    g11: ArcOfCircle CenterX=29.1832 CenterY=-10.0025 CenterZ=0 NormalX=0 NormalY=0 NormalZ=1 AngleXU=0 Radius=47.5 StartAngle=2.55294 EndAngle=2.94151
    g12: ArcOfCircle CenterX=-8.24272 CenterY=14.9834 CenterZ=0 NormalX=0 NormalY=0 NormalZ=1 AngleXU=0 Radius=2.5 StartAngle=5.69453 EndAngle=8.83612
    g13: ArcOfCircle CenterX=-14.919 CenterY=-1.05864 CenterZ=0 NormalX=0 NormalY=0 NormalZ=1 AngleXU=0 Radius=2.5 StartAngle=2.94151 EndAngle=6.0831
    g14: ArcOfCircle CenterX=29.1832 CenterY=-10.0025 CenterZ=0 NormalX=0 NormalY=0 NormalZ=1 AngleXU=0 Radius=42.5 StartAngle=2.55294 EndAngle=2.94151
    g15: LineSegment StartX=-2.91128 StartY=3.4144 StartZ=0 EndX=2.44187 EndY=11 EndZ=0
  constraints (42):
    c: PointOnObject(g9,g-1)
    c: Coincident(g8,g1)
    c: Diameter(g2) = 5.5
    c: Coincident(g0,g3)
    c: Coincident(g4,g5)
    c: Equal(g2,g6)
    c: Coincident(g7,g8)
    c: Equal(g8,g5)
    c: Coincident(g1,g9)
    c: DistanceY(g5) = 11
    c: DistanceY(g1,g1) = 11
    c: Horizontal(g9)
    c: Coincident(g9,g0)
    c: Vertical(g0)
    c: DistanceY(g3) = 10
    c: Angle(g3,g0) = 1.91986
    c: DistanceY(g2) = 4
    c: Parallel(g5,g3)
    c: Tangent(g2,g4) = 1.5708
    c: Distance(g5) = 0.7
    c: Tangent(g6,g7) = 1.5708
    c: DistanceY(g6) = 5
    c: Parallel(g8,g5)
    c: DistanceX(g0) = 22
    c: DistanceX(g3) = 12.7
    c: DistanceX(g2) = 4.7
    c: Coincident(g3,g10)
    c: Tangent(g10,g2) = 1.5708
    c: Coincident(g11,g14)
    c: Tangent(g14,g13) = 1.5708
    c: Tangent(g14,g12) = 1.5708
    c: Tangent(g11,g13) = -1.5708
    c: Tangent(g11,g12) = -1.5708
    c: Diameter(g12) = 5
    c: Radius(g14) = 42.5
    c: Tangent(g6,g15) = -1.5708
    c: Coincident(g15,g5)
    c: DistanceX(g6,g5) = 7.6
    c: Angle(g9,g7) = 1.48353
    c: Angle(g9,g4) = 1.39626
    c: DistanceX(g1) = -12
    c: DistanceX(g1,g3) = 24.7
FEATURE [PartDesign::Pad] Pad029
  Direction = (0,-1,2e-16)
  Length = 5
  Length2 = 4
  Midplane = true
  Placement = pos=(0,0,0) rot=(1,0,0;1.5708rad)
  Profile = -> Sketch057
  ReferenceAxis = -> Sketch057 [N_Axis]
  Refine = true
  Suppressed = false
  Type = 4
FEATURE [Sketcher::SketchObject] Sketch058
  AttachmentSupport = -> [YZ_Plane033]
  FullyConstrained = true
  MapMode = 5
  Placement = pos=(0,0,0) rot=(0.57735,0.57735,0.57735;2.0944rad)
  sketch-geometry (8):
    g0: LineSegment StartX=0 StartY=0 StartZ=0 EndX=0 EndY=-5.2 EndZ=0
    g1: LineSegment StartX=0 StartY=-5.2 StartZ=0 EndX=-4 EndY=-4.8 EndZ=0
    g2: ArcOfCircle CenterX=0 CenterY=-4.88005 CenterZ=0 NormalX=0 NormalY=0 NormalZ=1 AngleXU=0 Radius=4 StartAngle=4.61272 EndAngle=6.28319
    g3: LineSegment StartX=-4 StartY=-4.8 StartZ=0 EndX=-5 EndY=-5.4 EndZ=0
    g4: LineSegment StartX=-5 StartY=-5.4 StartZ=0 EndX=-5 EndY=-8.4 EndZ=0
    g5: LineSegment StartX=-5 StartY=-8.4 StartZ=0 EndX=-0.398015 EndY=-8.8602 EndZ=0
    g6: LineSegment StartX=4 StartY=-4.88005 StartZ=0 EndX=4 EndY=0 EndZ=0
    g7: LineSegment StartX=4 StartY=0 StartZ=0 EndX=0 EndY=0 EndZ=0
  constraints (22):
    c: Radius(g2) = 4
    c: PointOnObject(g2,g-2)
    c: Coincident(g1,g0)
    c: Coincident(g0,g-1)
    c: DistanceY(g0,g0) = 5.2
    c: Vertical(g0)
    c: Coincident(g1,g3)
    c: Coincident(g3,g4)
    c: Vertical(g4)
    c: Coincident(g4,g5)
    c: Tangent(g2,g6) = -1.5708
    c: Coincident(g6,g7)
    c: Coincident(g7,g0)
    c: Horizontal(g7)
    c: DistanceY(g1) = -4.8
    c: DistanceX(g1) = -4
    c: DistanceX(g3,g1) = 1
    c: DistanceY(g3,g1) = 0.6
    c: DistanceY(g4,g4) = 3
    c: Tangent(g5,g2) = -1.5708
    c: Vertical(g6)
    c: Parallel(g5,g1)
FEATURE [Sketcher::SketchObject] Sketch059
  AttachmentSupport = -> [XY_Plane033]
  FullyConstrained = true
  MapMode = 5
  sketch-geometry (4):
    g0: LineSegment StartX=-23 StartY=0 StartZ=0 EndX=-3 EndY=0 EndZ=0
    g1: LineSegment StartX=-3 StartY=0 StartZ=0 EndX=-3 EndY=20 EndZ=0
    g2: LineSegment StartX=-3 StartY=20 StartZ=0 EndX=-23 EndY=20 EndZ=0
    g3: LineSegment StartX=-23 StartY=20 StartZ=0 EndX=-23 EndY=0 EndZ=0
  constraints (12):
    c: PointOnObject(g0,g-1)
    c: Coincident(g1,g2)
    c: Horizontal(g2)
    c: Coincident(g2,g3)
    c: Coincident(g3,g0)
    c: Vertical(g3)
    c: Equal(g2,g3)
    c: DistanceX(g0,g0) = 20
    c: Coincident(g1,g0)
    c: PointOnObject(g0,g-1)
    c: Vertical(g1)
    c: DistanceX(g0) = -3
FEATURE [PartDesign::Pocket] Pocket024
  BaseFeature = -> Pad029
  Direction = (0,0,-1)
  Length = 5
  Length2 = 5
  Midplane = true
  Placement = pos=(0,0,0) rot=(1,0,0;1.5708rad)
  Profile = -> Sketch059
  ReferenceAxis = -> Sketch059 [N_Axis]
  Refine = true
  Suppressed = false
  Type = 1
FEATURE [PartDesign::Pad] Pad030
  BaseFeature = -> Pocket024
  Direction = (1,0,0)
  Length = 22
  Length2 = 3
  Placement = pos=(0,0,0) rot=(1,0,0;1.5708rad)
  Profile = -> Sketch058
  ReferenceAxis = -> Sketch058 [N_Axis]
  Refine = true
  Suppressed = false
  Type = 4
FEATURE [PartDesign::Body] Body031  label="3Humps_25mm"
  AllowCompound = false
  Group = -> [Sketch057,Pad029,Sketch058,Sketch059,Pocket024,Pad030]
  Origin = -> Origin033
  Placement = pos=(27.4,-39,21.2) rot=(0,-1,0;0.511381rad)
  Tip = -> Pad030
FEATURE [Sketcher::SketchObject] Sketch060
  AttachmentSupport = -> [XZ_Plane034]
  FullyConstrained = true
  MapMode = 5
  Placement = pos=(0,0,0) rot=(1,0,0;1.5708rad)
  sketch-geometry (12):
    g0: LineSegment StartX=22 StartY=0 StartZ=0 EndX=22 EndY=8.59271 EndZ=0
    g1: LineSegment StartX=-5.31908 StartY=15 StartZ=0 EndX=-10.7786 EndY=0 EndZ=0
    g2: ArcOfCircle CenterX=6.55679 CenterY=2.6 CenterZ=0 NormalX=0 NormalY=0 NormalZ=1 AngleXU=0 Radius=2.5 StartAngle=3.14159 EndAngle=5.93412
    g3: LineSegment StartX=22 StartY=8.59271 StartZ=0 EndX=12.6386 EndY=12 EndZ=0
    g4: LineSegment StartX=12.6386 StartY=12 StartZ=0 EndX=8.90602 EndY=1.74495 EndZ=0
    g5: LineSegment StartX=4.05679 StartY=2.6 StartZ=0 EndX=4.05679 EndY=13.829 EndZ=0
    g6: LineSegment StartX=4.05679 StartY=13.829 StartZ=0 EndX=3.58694 EndY=14 EndZ=0
    g7: LineSegment StartX=3.58694 StartY=14 StartZ=0 EndX=-4e-16 EndY=4.14495 EndZ=0
    g8: ArcOfCircle CenterX=-2.34923 CenterY=5 CenterZ=0 NormalX=0 NormalY=0 NormalZ=1 AngleXU=0 Radius=2.5 StartAngle=3.14159 EndAngle=5.93412
    g9: LineSegment StartX=-4.84923 StartY=5 StartZ=0 EndX=-4.84923 EndY=14.829 EndZ=0
    g10: LineSegment StartX=-4.84923 StartY=14.829 StartZ=0 EndX=-5.31908 EndY=15 EndZ=0
    g11: LineSegment StartX=-10.7786 StartY=0 StartZ=0 EndX=22 EndY=0 EndZ=0
  constraints (34):
    c: PointOnObject(g11,g-1)
    c: Coincident(g10,g1)
    c: Diameter(g2) = 5
    c: Coincident(g0,g3)
    c: Coincident(g3,g4)
    c: Tangent(g4,g2) = 1.5708
    c: Coincident(g5,g6)
    c: Coincident(g6,g7)
    c: Tangent(g7,g8) = 1.5708
    c: Equal(g2,g8)
    c: Coincident(g9,g10)
    c: Equal(g10,g6)
    c: Coincident(g1,g11)
    c: DistanceY(g6) = 14
    c: DistanceY(g1,g1) = 15
    c: PointOnObject(g7,g-2)
    c: Horizontal(g11)
    c: Coincident(g11,g0)
    c: Vertical(g0)
    c: DistanceY(g3) = 12
    c: Angle(g3,g0) = 1.91986
    c: Perpendicular(g4,g3)
    c: DistanceY(g2) = 2.6
    c: Vertical(g5)
    c: Parallel(g6,g3)
    c: Tangent(g2,g5) = 1.5708
    c: Distance(g6) = 0.5
    c: Tangent(g8,g9) = 1.5708
    c: DistanceY(g8) = 5
    c: Vertical(g9)
    c: Parallel(g10,g6)
    c: Parallel(g7,g1)
    c: Parallel(g7,g4)
    c: DistanceX(g0) = 22
FEATURE [PartDesign::Pad] Pad031
  Direction = (0,-1,2e-16)
  Length = 5
  Length2 = 4
  Midplane = true
  Placement = pos=(0,0,0) rot=(1,0,0;1.5708rad)
  Profile = -> Sketch060
  ReferenceAxis = -> Sketch060 [N_Axis]
  Refine = true
  Suppressed = false
  Type = 4
FEATURE [Sketcher::SketchObject] Sketch061
  AttachmentSupport = -> [YZ_Plane034]
  FullyConstrained = true
  MapMode = 5
  Placement = pos=(0,0,0) rot=(0.57735,0.57735,0.57735;2.0944rad)
  sketch-geometry (8):
    g0: LineSegment StartX=0 StartY=0 StartZ=0 EndX=0 EndY=-5.2 EndZ=0
    g1: LineSegment StartX=0 StartY=-5.2 StartZ=0 EndX=-4 EndY=-4.8 EndZ=0
    g2: ArcOfCircle CenterX=0 CenterY=-4.88005 CenterZ=0 NormalX=0 NormalY=0 NormalZ=1 AngleXU=0 Radius=4 StartAngle=4.61272 EndAngle=6.28319
    g3: LineSegment StartX=-4 StartY=-4.8 StartZ=0 EndX=-5 EndY=-5.4 EndZ=0
    g4: LineSegment StartX=-5 StartY=-5.4 StartZ=0 EndX=-5 EndY=-8.4 EndZ=0
    g5: LineSegment StartX=-5 StartY=-8.4 StartZ=0 EndX=-0.398015 EndY=-8.8602 EndZ=0
    g6: LineSegment StartX=4 StartY=-4.88005 StartZ=0 EndX=4 EndY=0 EndZ=0
    g7: LineSegment StartX=4 StartY=0 StartZ=0 EndX=0 EndY=0 EndZ=0
  constraints (22):
    c: Radius(g2) = 4
    c: PointOnObject(g2,g-2)
    c: Coincident(g1,g0)
    c: Coincident(g0,g-1)
    c: DistanceY(g0,g0) = 5.2
    c: Vertical(g0)
    c: Coincident(g1,g3)
    c: Coincident(g3,g4)
    c: Vertical(g4)
    c: Coincident(g4,g5)
    c: Tangent(g2,g6) = -1.5708
    c: Coincident(g6,g7)
    c: Coincident(g7,g0)
    c: Horizontal(g7)
    c: DistanceY(g1) = -4.8
    c: DistanceX(g1) = -4
    c: DistanceX(g3,g1) = 1
    c: DistanceY(g3,g1) = 0.6
    c: DistanceY(g4,g4) = 3
    c: Tangent(g5,g2) = -1.5708
    c: Vertical(g6)
    c: Parallel(g5,g1)
FEATURE [Sketcher::SketchObject] Sketch062
  AttachmentSupport = -> [XY_Plane034]
  FullyConstrained = true
  MapMode = 5
  sketch-geometry (4):
    g0: LineSegment StartX=-20 StartY=0 StartZ=0 EndX=0 EndY=0 EndZ=0
    g1: LineSegment StartX=0 StartY=0 StartZ=0 EndX=0 EndY=20 EndZ=0
    g2: LineSegment StartX=0 StartY=20 StartZ=0 EndX=-20 EndY=20 EndZ=0
    g3: LineSegment StartX=-20 StartY=20 StartZ=0 EndX=-20 EndY=0 EndZ=0
  constraints (11):
    c: PointOnObject(g0,g-1)
    c: Coincident(g0,g-1)
    c: Coincident(g0,g1)
    c: PointOnObject(g1,g-2)
    c: Coincident(g1,g2)
    c: Horizontal(g2)
    c: Coincident(g2,g3)
    c: Coincident(g3,g0)
    c: Vertical(g3)
    c: Equal(g2,g3)
    c: DistanceX(g0,g0) = 20
FEATURE [PartDesign::Pocket] Pocket025
  BaseFeature = -> Pad031
  Direction = (0,0,-1)
  Length = 5
  Length2 = 5
  Midplane = true
  Placement = pos=(0,0,0) rot=(1,0,0;1.5708rad)
  Profile = -> Sketch062
  ReferenceAxis = -> Sketch062 [N_Axis]
  Refine = true
  Suppressed = false
  Type = 1
FEATURE [PartDesign::Pad] Pad032
  BaseFeature = -> Pocket025
  Direction = (1,0,0)
  Length = 22
  Length2 = 10
  Placement = pos=(0,0,0) rot=(1,0,0;1.5708rad)
  Profile = -> Sketch061
  ReferenceAxis = -> Sketch061 [N_Axis]
  Refine = true
  Suppressed = false
  Type = 0
FEATURE [PartDesign::Body] Body032  label="3Humps_24mm"
  AllowCompound = false
  Group = -> [Sketch060,Pad031,Sketch061,Sketch062,Pocket025,Pad032]
  Origin = -> Origin034
  Placement = pos=(28.0394,-30,21.317) rot=(0,-1,0;0.523599rad)
  Tip = -> Pad032
FEATURE [Sketcher::SketchObject] Sketch063
  AttachmentSupport = -> [XZ_Plane035]
  FullyConstrained = false
  MapMode = 5
  Placement = pos=(0,0,0) rot=(1,0,0;1.5708rad)
  sketch-geometry (16):
    g0: LineSegment StartX=24 StartY=0 StartZ=0 EndX=24 EndY=5.3812 EndZ=0
    g1: LineSegment StartX=-8.11244 StartY=14 StartZ=0 EndX=-13 EndY=0 EndZ=0
    g2: ArcOfCircle CenterX=8.4 CenterY=4 CenterZ=0 NormalX=0 NormalY=0 NormalZ=1 AngleXU=0 Radius=2.75 StartAngle=3.14159 EndAngle=5.66865
    g3: LineSegment StartX=24 StartY=5.3812 StartZ=0 EndX=16 EndY=10 EndZ=0
    g4: LineSegment StartX=5.65 StartY=4 StartZ=0 EndX=5.65 EndY=13.65 EndZ=0
    g5: LineSegment StartX=5.65 StartY=13.65 StartZ=0 EndX=5.04378 EndY=14 EndZ=0
    g6: ArcOfCircle CenterX=-4.75622 CenterY=5 CenterZ=0 NormalX=0 NormalY=0 NormalZ=1 AngleXU=0 Radius=2.75 StartAngle=3.14159 EndAngle=5.66344
    g7: LineSegment StartX=-7.50622 StartY=5 StartZ=0 EndX=-7.50622 EndY=13.65 EndZ=0
    g8: LineSegment StartX=-7.50622 StartY=13.65 StartZ=0 EndX=-8.11244 EndY=14 EndZ=0
    g9: LineSegment StartX=-13 StartY=0 StartZ=0 EndX=24 EndY=0 EndZ=0
    g10: LineSegment StartX=16 StartY=10 StartZ=0 EndX=10.6469 EndY=2.4144 EndZ=0
    g11: ArcOfCircle CenterX=28.4031 CenterY=-7.65518 CenterZ=0 NormalX=0 NormalY=0 NormalZ=1 AngleXU=0 Radius=47.5 StartAngle=2.23011 EndAngle=2.97894
    g12: ArcOfCircle CenterX=0.837411 CenterY=27.9135 CenterZ=0 NormalX=0 NormalY=0 NormalZ=1 AngleXU=0 Radius=2.5 StartAngle=5.3717 EndAngle=8.51329
    g13: ArcOfCircle CenterX=-16.0029 CenterY=-0.368111 CenterZ=0 NormalX=0 NormalY=0 NormalZ=1 AngleXU=0 Radius=2.5 StartAngle=2.97894 EndAngle=6.12053
    g14: ArcOfCircle CenterX=28.4031 CenterY=-7.65518 CenterZ=0 NormalX=0 NormalY=0 NormalZ=1 AngleXU=0 Radius=42.5 StartAngle=2.23011 EndAngle=2.97894
    g15: LineSegment StartX=-2.51765 StartY=3.40272 StartZ=0 EndX=5.04378 EndY=14 EndZ=0
  constraints (42):
    c: PointOnObject(g9,g-1)
    c: Coincident(g8,g1)
    c: Diameter(g2) = 5.5
    c: Coincident(g0,g3)
    c: Coincident(g4,g5)
    c: Equal(g2,g6)
    c: Coincident(g7,g8)
    c: Equal(g8,g5)
    c: Coincident(g1,g9)
    c: DistanceY(g5) = 14
    c: DistanceY(g1,g1) = 14
    c: Horizontal(g9)
    c: Coincident(g9,g0)
    c: Vertical(g0)
    c: DistanceY(g3) = 10
    c: Angle(g3,g0) = 2.0944
    c: DistanceY(g2) = 4
    c: Parallel(g5,g3)
    c: Tangent(g2,g4) = 1.5708
    c: Distance(g5) = 0.7
    c: Tangent(g6,g7) = 1.5708
    c: DistanceY(g6) = 5
    c: Parallel(g8,g5)
    c: DistanceX(g0) = 24
    c: DistanceX(g3) = 16
    c: Coincident(g3,g10)
    c: Tangent(g10,g2) = 1.5708
    c: Coincident(g11,g14)
    c: Tangent(g14,g13) = 1.5708
    c: Tangent(g14,g12) = 1.5708
    c: Tangent(g11,g13) = -1.5708
    c: Tangent(g11,g12) = -1.5708
    c: Diameter(g12) = 5
    c: Radius(g14) = 42.5
    c: Tangent(g6,g15) = -1.5708
    c: Coincident(g15,g5)
    c: DistanceX(g6,g5) = 9.8
    c: Angle(g9,g7) = 1.5708
    c: Angle(g9,g4) = 1.5708
    c: DistanceX(g1) = -13
    c: DistanceX(g1,g3) = 29
    c: DistanceX(g2,g3) = 7.6
FEATURE [PartDesign::Pad] Pad033
  Direction = (0,-1,2e-16)
  Length = 5
  Length2 = 3
  Midplane = true
  Placement = pos=(0,0,0) rot=(1,0,0;1.5708rad)
  Profile = -> Sketch063
  ReferenceAxis = -> Sketch063 [N_Axis]
  Refine = true
  Suppressed = false
  Type = 4
FEATURE [Sketcher::SketchObject] Sketch064
  AttachmentSupport = -> [YZ_Plane035]
  FullyConstrained = true
  MapMode = 5
  Placement = pos=(0,0,0) rot=(0.57735,0.57735,0.57735;2.0944rad)
  sketch-geometry (8):
    g0: LineSegment StartX=0 StartY=0 StartZ=0 EndX=0 EndY=-5.2 EndZ=0
    g1: LineSegment StartX=0 StartY=-5.2 StartZ=0 EndX=-4 EndY=-4.7 EndZ=0
    g2: ArcOfCircle CenterX=-1 CenterY=-4.76887 CenterZ=0 NormalX=0 NormalY=0 NormalZ=1 AngleXU=0 Radius=4 StartAngle=4.58803 EndAngle=6.28319
    g3: LineSegment StartX=-4 StartY=-4.7 StartZ=0 EndX=-5 EndY=-5.3 EndZ=0
    g4: LineSegment StartX=-5 StartY=-5.3 StartZ=0 EndX=-5 EndY=-8.3 EndZ=0
    g5: LineSegment StartX=-5 StartY=-8.3 StartZ=0 EndX=-1.49614 EndY=-8.73798 EndZ=0
    g6: LineSegment StartX=3 StartY=-4.76887 StartZ=0 EndX=3 EndY=0 EndZ=0
    g7: LineSegment StartX=3 StartY=0 StartZ=0 EndX=0 EndY=0 EndZ=0
  constraints (22):
    c: Radius(g2) = 4
    c: Coincident(g1,g0)
    c: Coincident(g0,g-1)
    c: DistanceY(g0,g0) = 5.2
    c: Vertical(g0)
    c: Coincident(g1,g3)
    c: Coincident(g3,g4)
    c: Vertical(g4)
    c: Coincident(g4,g5)
    c: Tangent(g2,g6) = -1.5708
    c: Coincident(g6,g7)
    c: Coincident(g7,g0)
    c: Horizontal(g7)
    c: DistanceY(g1) = -4.7
    c: DistanceX(g1) = -4
    c: DistanceX(g3,g1) = 1
    c: DistanceY(g3,g1) = 0.6
    c: DistanceY(g4,g4) = 3
    c: Tangent(g5,g2) = -1.5708
    c: Vertical(g6)
    c: Parallel(g5,g1)
    c: DistanceX(g2) = -1
FEATURE [Sketcher::SketchObject] Sketch065
  AttachmentSupport = -> [XY_Plane035]
  FullyConstrained = true
  MapMode = 5
  sketch-geometry (4):
    g0: LineSegment StartX=-19 StartY=0 StartZ=0 EndX=1 EndY=0 EndZ=0
    g1: LineSegment StartX=1 StartY=0 StartZ=0 EndX=1 EndY=20 EndZ=0
    g2: LineSegment StartX=1 StartY=20 StartZ=0 EndX=-19 EndY=20 EndZ=0
    g3: LineSegment StartX=-19 StartY=20 StartZ=0 EndX=-19 EndY=0 EndZ=0
  constraints (12):
    c: PointOnObject(g0,g-1)
    c: Coincident(g1,g2)
    c: Horizontal(g2)
    c: Coincident(g2,g3)
    c: Coincident(g3,g0)
    c: Vertical(g3)
    c: Equal(g2,g3)
    c: DistanceX(g0,g0) = 20
    c: Coincident(g1,g0)
    c: PointOnObject(g0,g-1)
    c: Vertical(g1)
    c: DistanceX(g0) = 1
FEATURE [PartDesign::Pocket] Pocket026
  BaseFeature = -> Pad033
  Direction = (0,0,-1)
  Length = 5
  Length2 = 5
  Midplane = true
  Placement = pos=(0,0,0) rot=(1,0,0;1.5708rad)
  Profile = -> Sketch065
  ReferenceAxis = -> Sketch065 [N_Axis]
  Refine = true
  Suppressed = false
  Type = 1
FEATURE [PartDesign::Pad] Pad034
  BaseFeature = -> Pocket026
  Direction = (1,0,0)
  Length = 24
  Length2 = 2
  Placement = pos=(0,0,0) rot=(1,0,0;1.5708rad)
  Profile = -> Sketch064
  ReferenceAxis = -> Sketch064 [N_Axis]
  Refine = true
  Suppressed = false
  Type = 4
FEATURE [PartDesign::Body] Body033  label="3Humps_29mm"
  AllowCompound = false
  Group = -> [Sketch063,Pad033,Sketch064,Sketch065,Pocket026,Pad034]
  Origin = -> Origin035
  Placement = pos=(27.4,-34,21.2) rot=(0,-1,0;0.511381rad)
  Tip = -> Pad034
FEATURE [Sketcher::SketchObject] Sketch066
  AttachmentSupport = -> [XZ_Plane036]
  FullyConstrained = true
  MapMode = 5
  Placement = pos=(0,0,0) rot=(1,0,0;1.5708rad)
  sketch-geometry (4):
    g0: LineSegment StartX=-1.5 StartY=-4 StartZ=0 EndX=-1.5 EndY=3 EndZ=0
    g1: LineSegment StartX=-1.5 StartY=3 StartZ=0 EndX=1.5 EndY=3 EndZ=0
    g2: LineSegment StartX=-1.5 StartY=-4 StartZ=0 EndX=1.5 EndY=-4 EndZ=0
    g3: LineSegment StartX=1.5 StartY=3 StartZ=0 EndX=1.5 EndY=-4 EndZ=0
  constraints (11):
    c: Vertical(g0)
    c: Coincident(g0,g1)
    c: Coincident(g1,g3)
    c: DistanceY(g0,g0) = 7
    c: Coincident(g0,g2)
    c: Vertical(g3)
    c: Equal(g3,g0)
    c: Symmetric(g0,g1,g-2)
    c: DistanceX(g1,g1) = 3
    c: Coincident(g2,g3)
    c: DistanceY(g2) = -4
FEATURE [PartDesign::Pad] Pad035
  Direction = (0,-1,2e-16)
  Length = 14.6
  Length2 = 10
  Placement = pos=(0,0,0) rot=(1,0,0;1.5708rad)
  Profile = -> Sketch066
  ReferenceAxis = -> Sketch066 [N_Axis]
  Suppressed = false
  Type = 0
FEATURE [Sketcher::SketchObject] Sketch067
  AttachmentSupport = -> [YZ_Plane036]
  FullyConstrained = true
  MapMode = 5
  Placement = pos=(0,0,0) rot=(0.57735,0.57735,0.57735;2.0944rad)
  sketch-geometry (12):
    g0: LineSegment StartX=-14.6 StartY=4 StartZ=0 EndX=-14.6 EndY=0 EndZ=0
    g1: LineSegment StartX=-14.6 StartY=0 StartZ=0 EndX=-8.5 EndY=0 EndZ=0
    g2: LineSegment StartX=-8.5 StartY=0 StartZ=0 EndX=-8.5 EndY=0.8 EndZ=0
    g3: LineSegment StartX=-8.5 StartY=0.8 StartZ=0 EndX=-9.2 EndY=0.8 EndZ=0
    g4: LineSegment StartX=-9.2 StartY=0.8 StartZ=0 EndX=-9.2 EndY=1.7 EndZ=0
    g5: LineSegment StartX=-9.2 StartY=1.7 StartZ=0 EndX=-5.4 EndY=1.7 EndZ=0
    g6: LineSegment StartX=-5.4 StartY=1.7 StartZ=0 EndX=-5.4 EndY=0.8 EndZ=0
    g7: LineSegment StartX=-5.4 StartY=0.8 StartZ=0 EndX=-6.1 EndY=0.8 EndZ=0
    g8: LineSegment StartX=-6.1 StartY=0.8 StartZ=0 EndX=-6.1 EndY=0 EndZ=0
    g9: LineSegment StartX=-6.1 StartY=0 StartZ=0 EndX=0 EndY=0 EndZ=0
    g10: LineSegment StartX=0 StartY=0 StartZ=0 EndX=0 EndY=4 EndZ=0
    g11: LineSegment StartX=0 StartY=4 StartZ=0 EndX=-14.6 EndY=4 EndZ=0
  constraints (35):
    c: Vertical(g0)
    c: Horizontal(g1)
    c: Coincident(g1,g2)
    c: Vertical(g2)
    c: Coincident(g2,g3)
    c: Horizontal(g3)
    c: Coincident(g3,g4)
    c: Vertical(g4)
    c: Coincident(g4,g5)
    c: Horizontal(g5)
    c: Coincident(g5,g6)
    c: Vertical(g6)
    c: Coincident(g6,g7)
    c: Horizontal(g7)
    c: Coincident(g7,g8)
    c: Vertical(g8)
    c: Coincident(g8,g9)
    c: Horizontal(g9)
    c: Coincident(g9,g10)
    c: PointOnObject(g10,g-2)
    c: Coincident(g10,g11)
    c: Coincident(g11,g0)
    c: Horizontal(g11)
    c: Horizontal(g8,g1)
    c: Equal(g2,g8)
    c: Equal(g3,g7)
    c: DistanceX(g11,g11) = 14.6
    c: DistanceY(g10,g10) = 4
    c: DistanceY(g6,g6) = 0.9
    c: DistanceY(g8,g8) = 0.8
    c: Coincident(g1,g0)
    c: Equal(g9,g1)
    c: DistanceX(g5,g5) = 3.8
    c: DistanceX(g3,g3) = 0.7
    c: Coincident(g9,g-1)
FEATURE [PartDesign::Pocket] Pocket027
  BaseFeature = -> Pad035
  Direction = (-1,0,0)
  Length = 5
  Length2 = 5
  Midplane = true
  Placement = pos=(0,0,0) rot=(1,0,0;1.5708rad)
  Profile = -> Sketch067
  ReferenceAxis = -> Sketch067 [N_Axis]
  Suppressed = false
  Type = 1
FEATURE [PartDesign::Body] Body034  label="BottoomLock"
  AllowCompound = false
  Group = -> [Sketch066,Pad035,Sketch067,Pocket027]
  Origin = -> Origin036
  Placement = pos=(39,-51.7,-6.5) rot=(0,0,1;0rad)
  Tip = -> Pocket027
FEATURE [Mesh::Feature] Motor_GW370_Motor_Gearbox  label="Motor-GW370-Motor+Gearbox"
  Placement = pos=(-100,-29.5,-7.7) rot=(-0.092692,0.704063,-0.704063;3.32645rad)
FEATURE [Sketcher::SketchObject] Sketch076
  AttachmentSupport = -> [XZ_Plane039]
  FullyConstrained = true
  MapMode = 5
  Placement = pos=(0,0,0) rot=(1,0,0;1.5708rad)
  sketch-geometry (14):
    g0: LineSegment StartX=24 StartY=13.5 StartZ=0 EndX=-9 EndY=13.5 EndZ=0
    g1: ArcOfCircle CenterX=-9 CenterY=9 CenterZ=0 NormalX=0 NormalY=0 NormalZ=1 AngleXU=0 Radius=4.5 StartAngle=1.5708 EndAngle=4.71239
    g2: LineSegment StartX=-9 StartY=4.5 StartZ=0 EndX=1.8e-15 EndY=4.5 EndZ=0
    g3: ArcOfCircle CenterX=0 CenterY=0 CenterZ=0 NormalX=0 NormalY=0 NormalZ=1 AngleXU=0 Radius=4.5 StartAngle=4.71239 EndAngle=7.85398
    g4: LineSegment StartX=-8e-16 StartY=-4.5 StartZ=0 EndX=-9 EndY=-4.5 EndZ=0
    g5: ArcOfCircle CenterX=-9 CenterY=-9 CenterZ=0 NormalX=0 NormalY=0 NormalZ=1 AngleXU=0 Radius=4.5 StartAngle=1.5708 EndAngle=4.71239
    g6: LineSegment StartX=-9 StartY=-13.5 StartZ=0 EndX=24 EndY=-13.5 EndZ=0
    g7: ArcOfCircle CenterX=24 CenterY=-9 CenterZ=0 NormalX=0 NormalY=0 NormalZ=1 AngleXU=0 Radius=4.5 StartAngle=4.71239 EndAngle=6.28319
    g8: LineSegment StartX=28.5 StartY=-9 StartZ=0 EndX=28.5 EndY=9 EndZ=0
    g9: ArcOfCircle CenterX=24 CenterY=9 CenterZ=0 NormalX=0 NormalY=0 NormalZ=1 AngleXU=0 Radius=4.5 StartAngle=-1.421e-13 EndAngle=1.5708
    g10: Circle CenterX=-9 CenterY=9 CenterZ=0 NormalX=0 NormalY=0 NormalZ=1 AngleXU=0 Radius=1.75
    g11: Circle CenterX=-9 CenterY=-9 CenterZ=0 NormalX=0 NormalY=0 NormalZ=1 AngleXU=0 Radius=1.75
    g12: Circle CenterX=24 CenterY=-9 CenterZ=0 NormalX=0 NormalY=0 NormalZ=1 AngleXU=0 Radius=1.75
    g13: Circle CenterX=24 CenterY=9 CenterZ=0 NormalX=0 NormalY=0 NormalZ=1 AngleXU=0 Radius=1.75
  constraints (33):
    c: Horizontal(g0)
    c: Tangent(g0,g1) = -1.5708
    c: Tangent(g1,g2) = -1.5708
    c: Tangent(g2,g3) = 1.5708
    c: Tangent(g3,g4) = 1.5708
    c: Tangent(g4,g5) = -1.5708
    c: Tangent(g5,g6) = -1.5708
    c: Tangent(g6,g7) = -1.5708
    c: Tangent(g7,g8) = -1.5708
    c: Tangent(g8,g9) = -1.5708
    c: Coincident(g9,g0)
    c: Horizontal(g6)
    c: Horizontal(g2)
    c: Horizontal(g4)
    c: Equal(g5,g1)
    c: Equal(g2,g4)
    c: Equal(g6,g0)
    c: Vertical(g8)
    c: Equal(g9,g7)
    c: Equal(g7,g5)
    c: Coincident(g3,g-1)
    c: Coincident(g10,g1)
    c: Coincident(g11,g5)
    c: Coincident(g12,g7)
    c: Coincident(g13,g9)
    c: Equal(g13,g12)
    c: Equal(g12,g11)
    c: Equal(g11,g10)
    c: Diameter(g10) = 3.5
    c: Diameter(g5) = 9
    c: DistanceY(g5,g1) = 18
    c: DistanceX(g5) = -9
    c: DistanceX(g5,g7) = 33
FEATURE [PartDesign::Pad] Pad036
  Direction = (0,-1,2e-16)
  Length = 7
  Length2 = 10
  Placement = pos=(0,0,0) rot=(1,0,0;1.5708rad)
  Profile = -> Sketch076
  ReferenceAxis = -> Sketch076 [N_Axis]
  Suppressed = false
  Type = 0
FEATURE [Sketcher::SketchObject] Sketch077
  AttachmentSupport = -> [YZ_Plane039]
  FullyConstrained = true
  MapMode = 5
  Placement = pos=(0,0,0) rot=(0.57735,0.57735,0.57735;2.0944rad)
  sketch-geometry (4):
    g0: LineSegment StartX=-7 StartY=0 StartZ=0 EndX=-7 EndY=6.5 EndZ=0
    g1: LineSegment StartX=-7 StartY=6.5 StartZ=0 EndX=0 EndY=4 EndZ=0
    g2: LineSegment StartX=0 StartY=4 StartZ=0 EndX=0 EndY=0 EndZ=0
    g3: LineSegment StartX=0 StartY=0 StartZ=0 EndX=-7 EndY=0 EndZ=0
  constraints (11):
    c: PointOnObject(g0,g-1)
    c: Vertical(g0)
    c: Coincident(g0,g1)
    c: PointOnObject(g1,g-2)
    c: Coincident(g1,g2)
    c: Coincident(g2,g-1)
    c: Coincident(g2,g3)
    c: Coincident(g3,g0)
    c: DistanceX(g3,g3) = 7
    c: DistanceY(g0,g0) = 6.5
    c: DistanceY(g2,g2) = 4
FEATURE [PartDesign::Groove] Groove002
  Angle = 360
  Angle2 = 60
  Axis = (0,1,0)
  Base = (0,0,0)
  BaseFeature = -> Pad036
  Placement = pos=(0,0,0) rot=(1,0,0;1.5708rad)
  Profile = -> Sketch077
  ReferenceAxis = -> Sketch077 [H_Axis]
  Reversed = true
  Suppressed = false
  Type = 0
FEATURE [Sketcher::SketchObject] Sketch078
  AttachmentOffset = pos=(0,-9,-9) rot=(0,0,1;0rad)
  AttachmentSupport = -> [YZ_Plane039]
  FullyConstrained = true
  MapMode = 5
  Placement = pos=(-9,0,-9) rot=(0.57735,0.57735,0.57735;2.0944rad)
  sketch-geometry (4):
    g0: LineSegment StartX=-8 StartY=0 StartZ=0 EndX=-3.2 EndY=0 EndZ=0
    g1: LineSegment StartX=-3.2 StartY=0 StartZ=0 EndX=-6 EndY=2.8 EndZ=0
    g2: LineSegment StartX=-6 StartY=2.8 StartZ=0 EndX=-8 EndY=2.8 EndZ=0
    g3: LineSegment StartX=-8 StartY=2.8 StartZ=0 EndX=-8 EndY=0 EndZ=0
  constraints (12):
    c: Horizontal(g0)
    c: Coincident(g0,g1)
    c: Coincident(g1,g2)
    c: Horizontal(g2)
    c: Coincident(g2,g3)
    c: Vertical(g3)
    c: Coincident(g0,g3)
    c: PointOnObject(g0,g-1)
    c: DistanceX(g2,g2) = 2
    c: Angle(g1,g0) = 0.785398
    c: DistanceY(g3,g3) = 2.8
    c: DistanceX(g1) = -6
FEATURE [PartDesign::Groove] Groove003
  Angle = 360
  Angle2 = 60
  Axis = (0,1,0)
  Base = (-9,0,-9)
  BaseFeature = -> Groove002
  Placement = pos=(0,0,0) rot=(1,0,0;1.5708rad)
  Profile = -> Sketch078
  ReferenceAxis = -> Sketch078 [H_Axis]
  Reversed = true
  Suppressed = false
  Type = 0
FEATURE [PartDesign::Mirrored] Mirrored
  MirrorPlane = -> XY_Plane039
  Placement = pos=(0,0,0) rot=(1,0,0;1.5708rad)
  Suppressed = false
  TransformMode = 0
FEATURE [PartDesign::LinearPattern] LinearPattern
  Direction = -> Sketch078 [N_Axis]
  Length = 33
  Mode = 0
  Occurrences = 2
  Offset = 33
  Placement = pos=(0,0,0) rot=(1,0,0;1.5708rad)
  Suppressed = false
  TransformMode = 0
FEATURE [PartDesign::MultiTransform] MultiTransform
  BaseFeature = -> Groove003
  Originals = -> [Groove003]
  Placement = pos=(0,0,0) rot=(1,0,0;1.5708rad)
  Suppressed = false
  TransformMode = 0
  Transformations = -> [Mirrored,LinearPattern]
FEATURE [Sketcher::SketchObject] Sketch079
  AttachmentSupport = -> [XZ_Plane039]
  FullyConstrained = true
  MapMode = 5
  Placement = pos=(0,0,0) rot=(1,0,0;1.5708rad)
  sketch-geometry (5):
    g0: LineSegment StartX=8.53463 StartY=14 StartZ=0 EndX=4.2 EndY=-14 EndZ=0
    g1: LineSegment StartX=4.2 StartY=-14 StartZ=0 EndX=10.8 EndY=-14 EndZ=0
    g2: LineSegment StartX=13.7346 StartY=14 StartZ=0 EndX=8.53463 EndY=14 EndZ=0
    g3: LineSegment StartX=10.8 StartY=-14 StartZ=0 EndX=9.49426 EndY=-13.3911 EndZ=0
    g4: LineSegment StartX=9.49426 StartY=-13.3911 StartZ=0 EndX=13.7346 EndY=14 EndZ=0
  constraints (15):
    c: Coincident(g0,g1)
    c: Horizontal(g1)
    c: Coincident(g1,g3)
    c: Coincident(g4,g2)
    c: Coincident(g2,g0)
    c: Horizontal(g2)
    c: DistanceY(g4) = 14
    c: DistanceX(g0) = 4.2
    c: DistanceX(g1,g1) = 6.6
    c: Angle(g0,g-2) = 0.153589
    c: DistanceY(g0) = -14
    c: Coincident(g3,g4)
    c: Parallel(g0,g4)
    c: DistanceX(g2,g2) = 5.2
    c: Angle(g3,g1) = 0.436332
FEATURE [PartDesign::Pocket] Pocket034
  BaseFeature = -> MultiTransform
  Direction = (0,1,-2e-16)
  Length = 6
  Length2 = 5
  Placement = pos=(0,0,0) rot=(1,0,0;1.5708rad)
  Profile = -> Sketch079
  ReferenceAxis = -> Sketch079 [N_Axis]
  Reversed = true
  Suppressed = false
  Type = 0
FEATURE [PartDesign::Body] Body037  label="MotorPlate24T"
  AllowCompound = false
  Group = -> [Sketch076,Pad036,Sketch077,Groove002,Sketch078,Groove003,MultiTransform,Mirrored,LinearPattern,Sketch079,Pocket034]
  Origin = -> Origin039
  Placement = pos=(-124.6,8.5,-2) rot=(0,1,0;0.349066rad)
  Tip = -> Pocket034
FEATURE [Sketcher::SketchObject] Sketch080
  AttachmentSupport = -> [XZ_Plane040]
  FullyConstrained = false
  MapMode = 5
  Placement = pos=(0,0,0) rot=(1,0,0;1.5708rad)
  sketch-geometry (11):
    g0: LineSegment StartX=-173.201 StartY=491.297 StartZ=0 EndX=-221.879 EndY=94.2695 EndZ=0
    g1: LineSegment StartX=-221.879 StartY=94.2695 StartZ=0 EndX=125.519 EndY=51.6764 EndZ=0
    g2: LineSegment StartX=125.519 StartY=51.6764 StartZ=0 EndX=174.197 EndY=448.703 EndZ=0
    g3: LineSegment StartX=0.497956 StartY=470 StartZ=0 EndX=-48.1799 EndY=72.973 EndZ=0
    g4: LineSegment StartX=-173.201 StartY=491.297 StartZ=0 EndX=174.197 EndY=448.703 EndZ=0
    g5: LineSegment StartX=-137.511 StartY=83.9255 StartZ=0 EndX=-142.987 EndY=39.26 EndZ=0
    g6: LineSegment StartX=-142.987 StartY=39.26 StartZ=0 EndX=35.6749 EndY=17.3549 EndZ=0
    g7: LineSegment StartX=35.6749 StartY=17.3549 StartZ=0 EndX=41.1512 EndY=62.0204 EndZ=0
    g8: ArcOfCircle CenterX=-1.56e-14 CenterY=465.939 CenterZ=0 NormalX=0 NormalY=0 NormalZ=1 AngleXU=0 Radius=450 StartAngle=4.43091 EndAngle=4.99387
    g9: GeomPoint X=-102.5 Y=4 Z=0
    g10: GeomPoint X=102.5 Y=4 Z=0
  constraints (31):
    c: Coincident(g0,g1)
    c: Coincident(g1,g2)
    c: Perpendicular(g2,g1)
    c: Parallel(g2,g0)
    c: Distance(g2) = 400
    c: Symmetric(g2,g0,g3)
    c: Symmetric(g1,g1,g3)
    c: Equal(g0,g2)
    c: Distance(g1) = 350
    c: Coincident(g0,g4)
    c: Coincident(g4,g2)
    c: PointOnObject(g5,g1)
    c: Coincident(g5,g6)
    c: Coincident(g6,g7)
    c: Parallel(g7,g5)
    c: Parallel(g5,g0)
    c: Parallel(g6,g1)
    c: Symmetric(g5,g7,g3)
    c: Distance(g6) = 180
    c: Distance(g5) = 45
    c: Symmetric(g8,g8,g-2)
    c: DistanceX(g8,g8) = 250
    c: DistanceY(g8) = 33.6482
    c: Radius(g8) = 450
    c: DistanceX(g3) = -48.1799
    c: Symmetric(g10,g9,g-2)
    c: DistanceY(g9) = 4
    c: DistanceX(g9,g10) = 205
    c: PointOnObject(g5,g8)
    c: PointOnObject(g6,g8)
    c: DistanceY(g3) = 470
FEATURE [PartDesign::Body] Body038  label="BackRocker"
  AllowCompound = false
  Group = -> [Sketch080]
  Origin = -> Origin040
  Placement = pos=(-40,0,-35) rot=(0,0,1;0rad)
FEATURE [PartDesign::Mirrored] Mirrored001
  MirrorPlane = -> XY_Plane041
  Placement = pos=(0,0,0) rot=(1,0,0;1.5708rad)
  Suppressed = false
  TransformMode = 0
FEATURE [Sketcher::SketchObject] Sketch081
  AttachmentSupport = -> [XZ_Plane041]
  FullyConstrained = true
  MapMode = 5
  Placement = pos=(0,0,0) rot=(1,0,0;1.5708rad)
  sketch-geometry (16):
    g0: LineSegment StartX=24 StartY=13.55 StartZ=0 EndX=-9 EndY=13.55 EndZ=0
    g1: ArcOfCircle CenterX=-9 CenterY=9.05 CenterZ=0 NormalX=0 NormalY=0 NormalZ=1 AngleXU=0 Radius=4.5 StartAngle=1.5708 EndAngle=3.14159
    g2: ArcOfCircle CenterX=-9 CenterY=-9.05 CenterZ=0 NormalX=0 NormalY=0 NormalZ=1 AngleXU=0 Radius=4.5 StartAngle=3.14159 EndAngle=4.71239
    g3: LineSegment StartX=-9 StartY=-13.55 StartZ=0 EndX=24 EndY=-13.55 EndZ=0
    g4: ArcOfCircle CenterX=24 CenterY=-9.05 CenterZ=0 NormalX=0 NormalY=0 NormalZ=1 AngleXU=0 Radius=4.5 StartAngle=4.71239 EndAngle=6.28319
    g5: LineSegment StartX=28.5 StartY=-9.05 StartZ=0 EndX=28.5 EndY=9.05 EndZ=0
    g6: ArcOfCircle CenterX=24 CenterY=9.05 CenterZ=0 NormalX=0 NormalY=0 NormalZ=1 AngleXU=0 Radius=4.5 StartAngle=0 EndAngle=1.5708
    g7: Circle CenterX=-9 CenterY=9.05 CenterZ=0 NormalX=0 NormalY=0 NormalZ=1 AngleXU=0 Radius=1.7
    g8: Circle CenterX=-9 CenterY=-9.05 CenterZ=0 NormalX=0 NormalY=0 NormalZ=1 AngleXU=0 Radius=1.7
    g9: Circle CenterX=24 CenterY=-9.05 CenterZ=0 NormalX=0 NormalY=0 NormalZ=1 AngleXU=0 Radius=1.7
    g10: Circle CenterX=24 CenterY=9.05 CenterZ=0 NormalX=0 NormalY=0 NormalZ=1 AngleXU=0 Radius=1.7
    g11: LineSegment StartX=-13.5 StartY=-9.05 StartZ=0 EndX=-13.5 EndY=9.05 EndZ=0
    g12: ArcOfCircle CenterX=0 CenterY=0 CenterZ=0 NormalX=0 NormalY=0 NormalZ=1 AngleXU=0 Radius=5 StartAngle=1.5708 EndAngle=4.71239
    g13: ArcOfCircle CenterX=15 CenterY=0 CenterZ=0 NormalX=0 NormalY=0 NormalZ=1 AngleXU=0 Radius=5 StartAngle=4.71239 EndAngle=7.85398
    g14: LineSegment StartX=-8e-16 StartY=5 StartZ=0 EndX=15 EndY=5 EndZ=0
    g15: LineSegment StartX=-9e-16 StartY=-5 StartZ=0 EndX=15 EndY=-5 EndZ=0
  constraints (37):
    c: Horizontal(g0)
    c: Tangent(g0,g1) = -1.5708
    c: Tangent(g2,g3) = -1.5708
    c: Tangent(g3,g4) = -1.5708
    c: Tangent(g4,g5) = -1.5708
    c: Tangent(g5,g6) = -1.5708
    c: Coincident(g6,g0)
    c: Horizontal(g3)
    c: Equal(g2,g1)
    c: Equal(g3,g0)
    c: Vertical(g5)
    c: Equal(g6,g4)
    c: Equal(g4,g2)
    c: Coincident(g7,g1)
    c: Coincident(g8,g2)
    c: Coincident(g9,g4)
    c: Coincident(g10,g6)
    c: Equal(g10,g9)
    c: Equal(g9,g8)
    c: Equal(g8,g7)
    c: Diameter(g7) = 3.4
    c: Diameter(g2) = 9
    c: DistanceY(g2,g1) = 18.1
    c: DistanceX(g2) = -9
    c: DistanceX(g2,g4) = 33
    c: Symmetric(g2,g1,g-1)
    c: Tangent(g2,g11) = 1.5708
    c: Tangent(g11,g1) = 1.5708
    c: Tangent(g12,g14) = 1.5708
    c: Tangent(g12,g15) = -1.5708
    c: Tangent(g13,g14) = 1.5708
    c: Tangent(g13,g15) = -1.5708
    c: Equal(g12,g13)
    c: Coincident(g12,g-1)
    c: PointOnObject(g13,g-1)
    c: Diameter(g13) = 10
    c: DistanceX(g13,g4) = 9
FEATURE [PartDesign::Pad] Pad037
  Direction = (0,-1,2e-16)
  Length = 7
  Length2 = 10
  Placement = pos=(0,0,0) rot=(1,0,0;1.5708rad)
  Profile = -> Sketch081
  ReferenceAxis = -> Sketch081 [N_Axis]
  Suppressed = false
  Type = 0
FEATURE [Sketcher::SketchObject] Sketch082
  AttachmentSupport = -> [YZ_Plane041]
  FullyConstrained = true
  MapMode = 5
  Placement = pos=(0,0,0) rot=(0.57735,0.57735,0.57735;2.0944rad)
  sketch-geometry (4):
    g0: LineSegment StartX=-7 StartY=0 StartZ=0 EndX=-7 EndY=7.5 EndZ=0
    g1: LineSegment StartX=-7 StartY=7.5 StartZ=0 EndX=0 EndY=5 EndZ=0
    g2: LineSegment StartX=0 StartY=5 StartZ=0 EndX=0 EndY=0 EndZ=0
    g3: LineSegment StartX=0 StartY=0 StartZ=0 EndX=-7 EndY=0 EndZ=0
  constraints (11):
    c: PointOnObject(g0,g-1)
    c: Vertical(g0)
    c: Coincident(g0,g1)
    c: PointOnObject(g1,g-2)
    c: Coincident(g1,g2)
    c: Coincident(g2,g-1)
    c: Coincident(g2,g3)
    c: Coincident(g3,g0)
    c: DistanceX(g3,g3) = 7
    c: DistanceY(g0,g0) = 7.5
    c: DistanceY(g2,g2) = 5
FEATURE [PartDesign::Groove] Groove004
  Angle = 360
  Angle2 = 60
  Axis = (0,1,0)
  Base = (0,0,0)
  BaseFeature = -> Pad037
  Placement = pos=(0,0,0) rot=(1,0,0;1.5708rad)
  Profile = -> Sketch082
  ReferenceAxis = -> Sketch082 [H_Axis]
  Reversed = true
  Suppressed = false
  Type = 0
FEATURE [Sketcher::SketchObject] Sketch083
  AttachmentOffset = pos=(0,-9,-9) rot=(0,0,1;0rad)
  AttachmentSupport = -> [YZ_Plane041]
  FullyConstrained = true
  MapMode = 5
  Placement = pos=(-9,0,-9) rot=(0.57735,0.57735,0.57735;2.0944rad)
  sketch-geometry (4):
    g0: LineSegment StartX=-8.5 StartY=0 StartZ=0 EndX=-3.5 EndY=0 EndZ=0
    g1: LineSegment StartX=-3.5 StartY=0 StartZ=0 EndX=-6.5 EndY=3 EndZ=0
    g2: LineSegment StartX=-6.5 StartY=3 StartZ=0 EndX=-8.5 EndY=3 EndZ=0
    g3: LineSegment StartX=-8.5 StartY=3 StartZ=0 EndX=-8.5 EndY=0 EndZ=0
  constraints (12):
    c: Horizontal(g0)
    c: Coincident(g0,g1)
    c: Coincident(g1,g2)
    c: Horizontal(g2)
    c: Coincident(g2,g3)
    c: Vertical(g3)
    c: Coincident(g0,g3)
    c: PointOnObject(g0,g-1)
    c: DistanceX(g2,g2) = 2
    c: Angle(g1,g0) = 0.785398
    c: DistanceY(g3,g3) = 3
    c: DistanceX(g1) = -6.5
FEATURE [PartDesign::Groove] Groove005
  Angle = 360
  Angle2 = 60
  Axis = (0,1,0)
  Base = (-9,0,-9)
  BaseFeature = -> Groove004
  Placement = pos=(0,0,0) rot=(1,0,0;1.5708rad)
  Profile = -> Sketch083
  ReferenceAxis = -> Sketch083 [H_Axis]
  Reversed = true
  Suppressed = false
  Type = 0
FEATURE [PartDesign::LinearPattern] LinearPattern001
  Direction = -> Sketch083 [N_Axis]
  Length = 33
  Mode = 0
  Occurrences = 2
  Offset = 33
  Placement = pos=(0,0,0) rot=(1,0,0;1.5708rad)
  Suppressed = false
  TransformMode = 0
FEATURE [PartDesign::MultiTransform] MultiTransform001
  BaseFeature = -> Groove005
  Originals = -> [Groove005]
  Placement = pos=(0,0,0) rot=(1,0,0;1.5708rad)
  Suppressed = false
  TransformMode = 0
  Transformations = -> [Mirrored001,LinearPattern001]
FEATURE [Sketcher::SketchObject] Sketch084
  AttachmentSupport = -> [XZ_Plane041]
  FullyConstrained = true
  MapMode = 5
  Placement = pos=(0,0,0) rot=(1,0,0;1.5708rad)
  sketch-geometry (8):
    g0: LineSegment StartX=14.4 StartY=14 StartZ=0 EndX=28.003 EndY=-8.55 EndZ=0
    g1: LineSegment StartX=28.003 StartY=-8.55 StartZ=0 EndX=24.8565 EndY=-14 EndZ=0
    g2: LineSegment StartX=20.4 StartY=14 StartZ=0 EndX=14.4 EndY=14 EndZ=0
    g3: LineSegment StartX=24.8565 StartY=-14 StartZ=0 EndX=37.2907 EndY=-14 EndZ=0
    g4: LineSegment StartX=37.2907 StartY=-14 StartZ=0 EndX=20.4 EndY=14 EndZ=0
    g5: LineSegment StartX=-13.9 StartY=14 StartZ=0 EndX=-9.9 EndY=14 EndZ=0
    g6: LineSegment StartX=-9.9 StartY=14 StartZ=0 EndX=-13.9 EndY=-2.40866 EndZ=0
    g7: LineSegment StartX=-13.9 StartY=-2.40866 StartZ=0 EndX=-13.9 EndY=14 EndZ=0
  constraints (24):
    c: Coincident(g0,g1)
    c: Coincident(g1,g3)
    c: Coincident(g4,g2)
    c: Coincident(g2,g0)
    c: Horizontal(g2)
    c: DistanceY(g4) = 14
    c: Angle(g0,g-2) = -0.542797
    c: DistanceY(g0) = -8.55
    c: Coincident(g3,g4)
    c: Parallel(g0,g4)
    c: DistanceX(g2,g2) = 6
    c: Horizontal(g5)
    c: Coincident(g5,g6)
    c: Coincident(g7,g5)
    c: Vertical(g7)
    c: Angle(g6,g-2) = 0.23911
    c: DistanceX(g0) = 14.4
    c: Horizontal(g3)
    c: Angle(g3,g1) = 1.0472
    c: DistanceY(g1) = -14
    c: DistanceX(g5) = -9.9
    c: DistanceY(g5) = 14
    c: Coincident(g6,g7)
    c: DistanceX(g5,g5) = 4
FEATURE [PartDesign::Pocket] Pocket035
  BaseFeature = -> MultiTransform001
  Direction = (0,1,-2e-16)
  Length = 6
  Length2 = 5
  Placement = pos=(0,0,0) rot=(1,0,0;1.5708rad)
  Profile = -> Sketch084
  ReferenceAxis = -> Sketch084 [N_Axis]
  Reversed = true
  Suppressed = false
  Type = 0
FEATURE [PartDesign::Body] Body039  label="MotorPlate19T"
  AllowCompound = false
  Group = -> [Sketch081,Pad037,Sketch082,Groove004,Sketch083,Groove005,MultiTransform001,Mirrored001,LinearPattern001,Sketch084,Pocket035]
  Origin = -> Origin041
  Placement = pos=(-100,8.5,-7.7) rot=(0,1,0;0.261799rad)
  Tip = -> Pocket035
FEATURE [Mesh::Feature] Motor_GW370_Motor_Gearbox001  label="Motor-GW370-Motor+Gearbox001"
  Placement = pos=(98,-30,36.8) rot=(0.57735,-0.57735,0.57735;2.0944rad)
FEATURE [Sketcher::SketchObject] Sketch085
  AttachmentSupport = -> [XZ_Plane042]
  FullyConstrained = true
  MapMode = 5
  Placement = pos=(0,0,0) rot=(1,0,0;1.5708rad)
  sketch-geometry (36):
    g0: LineSegment StartX=-16.25 StartY=-71.8 StartZ=0 EndX=18.5 EndY=-71.8 EndZ=0
    g1: LineSegment StartX=18.5 StartY=-71.8 StartZ=0 EndX=18.5 EndY=13.25 EndZ=0
    g2: LineSegment StartX=14.25 StartY=17.5 StartZ=0 EndX=-14.25 EndY=17.5 EndZ=0
    g3: ArcOfCircle CenterX=14.25 CenterY=13.25 CenterZ=0 NormalX=0 NormalY=0 NormalZ=1 AngleXU=0 Radius=4.25 StartAngle=1e-16 EndAngle=1.5708
    g4: GeomPoint X=18.5 Y=17.5 Z=0
    g5: ArcOfCircle CenterX=-14.25 CenterY=13.25 CenterZ=0 NormalX=0 NormalY=0 NormalZ=1 AngleXU=0 Radius=4.25 StartAngle=1.5708 EndAngle=3.14159
    g6: GeomPoint X=-18.5 Y=17.5 Z=0
    g7: LineSegment StartX=-18.5 StartY=13.25 StartZ=0 EndX=-18.5 EndY=-24 EndZ=0
    g8: LineSegment StartX=-77 StartY=-50.6741 StartZ=0 EndX=-77 EndY=-71.8 EndZ=0
    g9: LineSegment StartX=-16.25 StartY=-71.8 StartZ=0 EndX=-14.4891 EndY=-68.75 EndZ=0
    g10: LineSegment StartX=-14.4891 StartY=-68.75 StartZ=0 EndX=-16.25 EndY=-65.7 EndZ=0
    g11: LineSegment StartX=-16.25 StartY=-65.7 StartZ=0 EndX=-19.7718 EndY=-65.7 EndZ=0
    g12: LineSegment StartX=-19.7718 StartY=-65.7 StartZ=0 EndX=-21.5328 EndY=-68.75 EndZ=0
    g13: LineSegment StartX=-21.5328 StartY=-68.75 StartZ=0 EndX=-19.7718 EndY=-71.8 EndZ=0
    g14: LineSegment StartX=-19.7718 StartY=-71.8 StartZ=0 EndX=-16.25 EndY=-71.8 EndZ=0
    g15: Circle CenterX=-18.0109 CenterY=-68.75 CenterZ=0 NormalX=0 NormalY=0 NormalZ=1 AngleXU=0 Radius=3.52184
    g16: LineSegment StartX=-66.25 StartY=-71.8 StartZ=0 EndX=-64.4891 EndY=-68.75 EndZ=0
    g17: LineSegment StartX=-64.4891 StartY=-68.75 StartZ=0 EndX=-66.25 EndY=-65.7 EndZ=0
    g18: LineSegment StartX=-66.25 StartY=-65.7 StartZ=0 EndX=-69.7718 EndY=-65.7 EndZ=0
    g19: LineSegment StartX=-69.7718 StartY=-65.7 StartZ=0 EndX=-71.5328 EndY=-68.75 EndZ=0
    g20: LineSegment StartX=-71.5328 StartY=-68.75 StartZ=0 EndX=-69.7718 EndY=-71.8 EndZ=0
    g21: LineSegment StartX=-69.7718 StartY=-71.8 StartZ=0 EndX=-66.25 EndY=-71.8 EndZ=0
    g22: Circle CenterX=-68.0109 CenterY=-68.75 CenterZ=0 NormalX=0 NormalY=0 NormalZ=1 AngleXU=0 Radius=3.52184
    g23: LineSegment StartX=-66.25 StartY=-71.8 StartZ=0 EndX=-19.7718 EndY=-71.8 EndZ=0
    g24: LineSegment StartX=-77 StartY=-71.8 StartZ=0 EndX=-69.7718 EndY=-71.8 EndZ=0
    g25: LineSegment StartX=-18.5 StartY=-24 StartZ=0 EndX=-28.531 EndY=-41.3743 EndZ=0
    g26: LineSegment StartX=-14 StartY=13 StartZ=0 EndX=-14 EndY=-29 EndZ=0
    g27: LineSegment StartX=-14 StartY=-29 StartZ=0 EndX=14 EndY=-29 EndZ=0
    g28: LineSegment StartX=14 StartY=-29 StartZ=0 EndX=14 EndY=13 EndZ=0
    g29: LineSegment StartX=14 StartY=13 StartZ=0 EndX=-14 EndY=13 EndZ=0
    g30: ArcOfCircle CenterX=-138 CenterY=398.2 CenterZ=0 NormalX=0 NormalY=0 NormalZ=1 AngleXU=0 Radius=453 StartAngle=4.84746 EndAngle=4.95646
    g31: LineSegment StartX=-14 StartY=-33 StartZ=0 EndX=-14 EndY=-61.2 EndZ=0
    g32: LineSegment StartX=-14 StartY=-61.2 StartZ=0 EndX=-7.4 EndY=-67.8 EndZ=0
    g33: LineSegment StartX=-7.4 StartY=-67.8 StartZ=0 EndX=14 EndY=-67.8 EndZ=0
    g34: LineSegment StartX=14 StartY=-67.8 StartZ=0 EndX=14 EndY=-33 EndZ=0
    g35: LineSegment StartX=14 StartY=-33 StartZ=0 EndX=-14 EndY=-33 EndZ=0
  constraints (93):
    c: Coincident(g0,g1)
    c: Vertical(g1)
    c: Horizontal(g0)
    c: Symmetric(g6,g4,g-2)
    c: DistanceX(g6,g4) = 37
    c: DistanceY(g0) = -71.8
    c: DistanceY(g4) = 17.5
    c: PointOnObject(g4,g1)
    c: PointOnObject(g4,g2)
    c: Tangent(g1,g3) = -1.5708
    c: Tangent(g2,g3) = -1.5708
    c: PointOnObject(g6,g2)
    c: Tangent(g2,g5) = -1.5708
    c: Equal(g5,g3)
    c: Radius(g3) = 4.25
    c: Coincident(g7,g25)
    c: Vertical(g7)
    c: PointOnObject(g6,g7)
    c: Vertical(g8)
    c: DistanceX(g8) = -77
    c: Horizontal(g8,g0)
    c: Coincident(g9,g10)
    c: Coincident(g10,g11)
    c: Coincident(g11,g12)
    c: Coincident(g12,g13)
    c: Coincident(g13,g14)
    c: Coincident(g14,g9)
    c: Equal(g9, g10-g14) x5
    c: PointOnObject(g9,g15)
    c: PointOnObject(g10,g15)
    c: PointOnObject(g11,g15)
    c: PointOnObject(g12,g15)
    c: PointOnObject(g13,g15)
    c: PointOnObject(g14,g15)
    c: Coincident(g14,g0)
    c: Horizontal(g14)
    c: DistanceY(g0,g10) = 6.1
    c: Coincident(g16,g17)
    c: Coincident(g17,g18)
    c: Coincident(g18,g19)
    c: Coincident(g19,g20)
    c: Coincident(g20,g21)
    c: Coincident(g21,g16)
    c: Equal(g16, g17-g21) x5
    c: PointOnObject(g16,g22)
    c: PointOnObject(g17,g22)
    c: PointOnObject(g18,g22)
    c: PointOnObject(g19,g22)
    c: PointOnObject(g20,g22)
    c: PointOnObject(g21,g22)
    c: Equal(g22,g15)
    c: Horizontal(g21)
    c: Coincident(g16,g23)
    c: Coincident(g23,g13)
    c: Horizontal(g23)
    c: DistanceX(g22,g15) = 50
    c: Coincident(g8,g24)
    c: Coincident(g24,g20)
    c: DistanceX(g0,g0) = 34.75
    c: Angle(g25,g-2) = 0.523599
    c: DistanceY(g7) = -24
    c: Tangent(g7,g5) = -1.5708
    c: Coincident(g26,g27)
    c: Coincident(g27,g28)
    c: Coincident(g28,g29)
    c: Coincident(g29,g26)
    c: Vertical(g26)
    c: Vertical(g28)
    c: Horizontal(g27)
    c: Symmetric(g28,g26,g-2)
    c: DistanceX(g29,g29) = 28
    c: DistanceY(g28) = 13
    c: DistanceY(g28,g28) = 42
    c: DistanceX(g30) = -138
    c: DistanceY(g8,g30) = 470
    c: Radius(g30) = 453
    c: Coincident(g30,g25)
    c: Coincident(g8,g30)
    c: Vertical(g31)
    c: Coincident(g31,g32)
    c: Coincident(g32,g33)
    c: Horizontal(g33)
    c: Coincident(g33,g34)
    c: Vertical(g34)
    c: Coincident(g34,g35)
    c: Coincident(g35,g31)
    c: Horizontal(g35)
    c: Vertical(g34,g27)
    c: Equal(g35,g27)
    c: DistanceY(g0,g33) = 4
    c: DistanceY(g34,g27) = 4
    c: Angle(g32) = -0.785398
    c: DistanceY(g31,g31) = 28.2
FEATURE [PartDesign::Pad] Pad038
  Direction = (0,-1,2e-16)
  Length = 33
  Length2 = 10
  Placement = pos=(0,0,0) rot=(1,0,0;1.5708rad)
  Profile = -> Sketch085
  ReferenceAxis = -> Sketch085 [N_Axis]
  Reversed = true
  Suppressed = false
  Type = 0
FEATURE [Sketcher::SketchObject] Sketch086
  AttachmentSupport = -> [XZ_Plane042]
  FullyConstrained = true
  MapMode = 5
  Placement = pos=(0,0,0) rot=(1,0,0;1.5708rad)
  sketch-geometry (12):
    g0: LineSegment StartX=-8 StartY=-71.8 StartZ=0 EndX=-8 EndY=-61.8 EndZ=0
    g1: LineSegment StartX=-8 StartY=-61.8 StartZ=0 EndX=-27 EndY=-37.8 EndZ=0
    g2: LineSegment StartX=-27 StartY=-37.8 StartZ=0 EndX=-79 EndY=-37.8 EndZ=0
    g3: LineSegment StartX=-79 StartY=-37.8 StartZ=0 EndX=-79 EndY=-71.8 EndZ=0
    g4: LineSegment StartX=-79 StartY=-71.8 StartZ=0 EndX=-8 EndY=-71.8 EndZ=0
    g5: LineSegment StartX=-27.8 StartY=-65.6 StartZ=0 EndX=-19.4122 EndY=-57.2122 EndZ=0
    g6: LineSegment StartX=-19.4122 StartY=-57.2122 StartZ=0 EndX=-30.0302 EndY=-43.8 EndZ=0
    g7: LineSegment StartX=-30.0302 StartY=-43.8 StartZ=0 EndX=-62.9 EndY=-51.6 EndZ=0
    g8: LineSegment StartX=-62.9 StartY=-51.6 StartZ=0 EndX=-62.9 EndY=-59.5 EndZ=0
    g9: LineSegment StartX=-62.9 StartY=-59.5 StartZ=0 EndX=-56.8 EndY=-65.6 EndZ=0
    g10: LineSegment StartX=-56.8 StartY=-65.6 StartZ=0 EndX=-27.8 EndY=-65.6 EndZ=0
    g11: LineSegment StartX=-19.4122 StartY=-57.2122 StartZ=0 EndX=-14.6295 EndY=-53.4259 EndZ=0
  constraints (36):
    c: Vertical(g0)
    c: Coincident(g0,g1)
    c: Coincident(g1,g2)
    c: Horizontal(g2)
    c: Coincident(g2,g3)
    c: Vertical(g3)
    c: Coincident(g3,g4)
    c: Coincident(g4,g0)
    c: Horizontal(g4)
    c: DistanceX(g0) = -8
    c: DistanceY(g0) = -71.8
    c: DistanceX(g4,g4) = 71
    c: DistanceY(g0,g0) = 10
    c: DistanceX(g0,g1) = -19
    c: DistanceY(g0,g1) = 24
    c: Coincident(g5,g6)
    c: Coincident(g6,g7)
    c: Coincident(g7,g8)
    c: Vertical(g8)
    c: Coincident(g8,g9)
    c: Coincident(g9,g10)
    c: Coincident(g10,g5)
    c: Horizontal(g10)
    c: DistanceY(g0,g5) = 6.2
    c: Angle(g5) = 0.785398
    c: DistanceX(g5,g0) = 19.8
    c: Parallel(g6,g1)
    c: Coincident(g5,g11)
    c: PointOnObject(g11,g1)
    c: Perpendicular(g11,g1)
    c: Distance(g11) = 6.1
    c: Angle(g9) = -0.785398
    c: DistanceX(g10,g10) = 29
    c: DistanceX(g9,g9) = 6.1
    c: DistanceY(g8,g8) = 7.9
    c: DistanceY(g6,g1) = 6
FEATURE [PartDesign::Pocket] Pocket036  label="Wall3Cuts"
  BaseFeature = -> Pad038
  Direction = (0,1,-2e-16)
  Length = 6.2
  Length2 = 5
  Placement = pos=(0,0,0) rot=(1,0,0;1.5708rad)
  Profile = -> Sketch086
  ReferenceAxis = -> Sketch086 [N_Axis]
  Suppressed = false
  Type = 0
FEATURE [Sketcher::SketchObject] Sketch087
  AttachmentOffset = pos=(0,0,-6.5) rot=(0,0,1;0rad)
  AttachmentSupport = -> [XZ_Plane042]
  FullyConstrained = true
  MapMode = 5
  Placement = pos=(0,6.5,-1.4e-15) rot=(1,0,0;1.5708rad)
  sketch-geometry (14):
    g0: LineSegment StartX=-16.5 StartY=-31 StartZ=0 EndX=-16.5 EndY=13.2 EndZ=0
    g1: ArcOfCircle CenterX=-14.5 CenterY=13.2 CenterZ=0 NormalX=0 NormalY=0 NormalZ=1 AngleXU=0 Radius=2 StartAngle=1.5708 EndAngle=3.14159
    g2: LineSegment StartX=-14.5 StartY=15.2 StartZ=0 EndX=14.5 EndY=15.2 EndZ=0
    g3: ArcOfCircle CenterX=14.5 CenterY=13.2 CenterZ=0 NormalX=0 NormalY=0 NormalZ=1 AngleXU=0 Radius=2 StartAngle=0 EndAngle=1.5708
    g4: LineSegment StartX=16.5 StartY=13.2 StartZ=0 EndX=16.5 EndY=-31 EndZ=0
    g5: LineSegment StartX=16.5 StartY=-31 StartZ=0 EndX=14.5 EndY=-31 EndZ=0
    g6: LineSegment StartX=-16.5 StartY=-31 StartZ=0 EndX=-12.5 EndY=-31 EndZ=0
    g7: LineSegment StartX=-12.5 StartY=-31 StartZ=0 EndX=-12.5 EndY=-60 EndZ=0
    g8: LineSegment StartX=25.5 StartY=-81.7279 StartZ=0 EndX=25.5 EndY=-35 EndZ=0
    g9: LineSegment StartX=25.5 StartY=-35 StartZ=0 EndX=14.5 EndY=-35 EndZ=0
    g10: LineSegment StartX=14.5 StartY=-35 StartZ=0 EndX=14.5 EndY=-31 EndZ=0
    g11: LineSegment StartX=-3.5 StartY=-81.7279 StartZ=0 EndX=25.5 EndY=-81.7279 EndZ=0
    g12: LineSegment StartX=-12.5 StartY=-60 StartZ=0 EndX=-3.5 EndY=-69 EndZ=0
    g13: LineSegment StartX=-3.5 StartY=-69 StartZ=0 EndX=-3.5 EndY=-81.7279 EndZ=0
  constraints (39):
    c: Vertical(g0)
    c: Tangent(g0,g1) = 1.5708
    c: Tangent(g1,g2) = 1.5708
    c: Tangent(g2,g3) = 1.5708
    c: Tangent(g3,g4) = 1.5708
    c: Coincident(g4,g5)
    c: Horizontal(g5)
    c: Equal(g1,g3)
    c: Radius(g3) = 2
    c: Symmetric(g2,g1,g-2)
    c: DistanceX(g0,g3) = 33
    c: Vertical(g4)
    c: DistanceY(g2) = 15.2
    c: DistanceY(g4,g2) = 46.2
    c: Coincident(g0,g6)
    c: Coincident(g6,g7)
    c: Vertical(g7)
    c: Coincident(g7,g12)
    c: Coincident(g11,g8)
    c: Vertical(g8)
    c: Coincident(g8,g9)
    c: Horizontal(g9)
    c: Coincident(g9,g10)
    c: Coincident(g10,g5)
    c: Vertical(g10)
    c: Horizontal(g6)
    c: Horizontal(g4,g0)
    c: DistanceX(g6,g6) = 4
    c: DistanceY(g7,g7) = 29
    c: Equal(g6,g10)
    c: DistanceX(g5,g5) = 2
    c: Coincident(g13,g11)
    c: Horizontal(g11)
    c: Coincident(g12,g13)
    c: Angle(g-2,g12) = 0.785398
    c: Vertical(g13)
    c: DistanceX(g7,g12) = 9
    c: Equal(g7,g11)
    c: Equal(g13,g12)
FEATURE [PartDesign::Pocket] Pocket037  label="MotorCut"
  BaseFeature = -> Pocket036
  Direction = (0,1,-2e-16)
  Length = 5
  Length2 = 5
  Placement = pos=(0,0,0) rot=(1,0,0;1.5708rad)
  Profile = -> Sketch087
  ReferenceAxis = -> Sketch087 [N_Axis]
  Suppressed = false
  Type = 1
FEATURE [Sketcher::SketchObject] Sketch088
  AttachmentOffset = pos=(0,0,-7) rot=(0,0,1;0rad)
  AttachmentSupport = -> [XY_Plane042]
  FullyConstrained = true
  MapMode = 5
  Placement = pos=(0,0,-7) rot=(0,0,1;0rad)
  sketch-geometry (8):
    g0: LineSegment StartX=-19.7 StartY=14 StartZ=0 EndX=-19.7 EndY=11.8 EndZ=0
    g1: LineSegment StartX=-19.7 StartY=11.8 StartZ=0 EndX=-17.5 EndY=11.8 EndZ=0
    g2: LineSegment StartX=-17.5 StartY=11.8 StartZ=0 EndX=-17.5 EndY=14 EndZ=0
    g3: LineSegment StartX=-17.5 StartY=14 StartZ=0 EndX=-19.7 EndY=14 EndZ=0
    g4: LineSegment StartX=17.5 StartY=14 StartZ=0 EndX=17.5 EndY=11.8 EndZ=0
    g5: LineSegment StartX=17.5 StartY=11.8 StartZ=0 EndX=19.7 EndY=11.8 EndZ=0
    g6: LineSegment StartX=19.7 StartY=11.8 StartZ=0 EndX=19.7 EndY=14 EndZ=0
    g7: LineSegment StartX=19.7 StartY=14 StartZ=0 EndX=17.5 EndY=14 EndZ=0
  constraints (23):
    c: Coincident(g0,g1)
    c: Coincident(g1,g2)
    c: Coincident(g2,g3)
    c: Coincident(g3,g0)
    c: Vertical(g0)
    c: Vertical(g2)
    c: Horizontal(g1)
    c: Horizontal(g3)
    c: Coincident(g4,g5)
    c: Coincident(g5,g6)
    c: Coincident(g6,g7)
    c: Coincident(g7,g4)
    c: Vertical(g4)
    c: Vertical(g6)
    c: Horizontal(g5)
    c: Horizontal(g7)
    c: Equal(g5,g6)
    c: Equal(g1,g0)
    c: Equal(g0,g5)
    c: Symmetric(g4,g1,g-2)
    c: DistanceY(g6,g6) = 2.2
    c: DistanceX(g2,g4) = 35
    c: DistanceY(g6) = 14
FEATURE [PartDesign::Pocket] Pocket038  label="MotorMountCut"
  BaseFeature = -> Pocket037
  Direction = (0,0,-1)
  Length = 6
  Length2 = 5
  Placement = pos=(0,0,0) rot=(1,0,0;1.5708rad)
  Profile = -> Sketch088
  ReferenceAxis = -> Sketch088 [N_Axis]
  Reversed = true
  Suppressed = false
  Type = 1
FEATURE [Sketcher::SketchObject] Sketch089
  AttachmentSupport = -> [XY_Plane043]
  FullyConstrained = true
  MapMode = 5
  sketch-geometry (16):
    g0: LineSegment StartX=-17 StartY=0 StartZ=0 EndX=-17 EndY=-2 EndZ=0
    g1: LineSegment StartX=-17 StartY=-2 StartZ=0 EndX=-18.5 EndY=-2 EndZ=0
    g2: LineSegment StartX=-16 StartY=17 StartZ=0 EndX=16 EndY=17 EndZ=0
    g3: LineSegment StartX=18.5 StartY=-2 StartZ=0 EndX=17 EndY=-2 EndZ=0
    g4: LineSegment StartX=17 StartY=-2 StartZ=0 EndX=17 EndY=0 EndZ=0
    g5: LineSegment StartX=17 StartY=0 StartZ=0 EndX=18.5 EndY=0 EndZ=0
    g6: LineSegment StartX=16 StartY=15 StartZ=0 EndX=-16 EndY=15 EndZ=0
    g7: LineSegment StartX=-18.5 StartY=5.7e-15 StartZ=0 EndX=-17 EndY=0 EndZ=0
    g8: ArcOfCircle CenterX=-16 CenterY=15 CenterZ=0 NormalX=0 NormalY=0 NormalZ=1 AngleXU=0 Radius=2 StartAngle=1.5708 EndAngle=2.8113
    g9: ArcOfCircle CenterX=16 CenterY=15 CenterZ=0 NormalX=0 NormalY=0 NormalZ=1 AngleXU=0 Radius=2 StartAngle=0.330297 EndAngle=1.5708
    g10: ArcOfCircle CenterX=-27.75 CenterY=0 CenterZ=0 NormalX=0 NormalY=0 NormalZ=1 AngleXU=0 Radius=46.25 StartAngle=0 EndAngle=0.330297
    g11: ArcOfCircle CenterX=27.75 CenterY=0 CenterZ=0 NormalX=0 NormalY=0 NormalZ=1 AngleXU=0 Radius=46.25 StartAngle=2.8113 EndAngle=3.14159
    g12: ArcOfCircle CenterX=-27.75 CenterY=0 CenterZ=0 NormalX=0 NormalY=0 NormalZ=1 AngleXU=0 Radius=48.25 StartAngle=0 EndAngle=0.330297
    g13: ArcOfCircle CenterX=27.75 CenterY=0 CenterZ=0 NormalX=0 NormalY=0 NormalZ=1 AngleXU=0 Radius=48.25 StartAngle=2.8113 EndAngle=3.14159
    g14: ArcOfCircle CenterX=18.5 CenterY=0 CenterZ=0 NormalX=0 NormalY=0 NormalZ=1 AngleXU=0 Radius=2 StartAngle=4.71239 EndAngle=6.28319
    g15: ArcOfCircle CenterX=-18.5 CenterY=5.7e-15 CenterZ=0 NormalX=0 NormalY=0 NormalZ=1 AngleXU=0 Radius=2 StartAngle=3.14159 EndAngle=4.71239
  constraints (41):
    c: PointOnObject(g0,g-1)
    c: Vertical(g0)
    c: Coincident(g0,g1)
    c: Horizontal(g1)
    c: Horizontal(g2)
    c: Coincident(g3,g4)
    c: Vertical(g4)
    c: Coincident(g4,g5)
    c: PointOnObject(g5,g-1)
    c: Horizontal(g6)
    c: PointOnObject(g7,g-1)
    c: Coincident(g7,g0)
    c: Horizontal(g3)
    c: Symmetric(g4,g0,g-2)
    c: Equal(g7,g5)
    c: DistanceX(g0,g4) = 34
    c: DistanceY(g4,g4) = 2
    c: DistanceX(g5,g5) = 1.5
    c: Tangent(g2,g8) = 1.5708
    c: Tangent(g2,g9) = 1.5708
    c: Coincident(g8,g6)
    c: DistanceY(g5,g6) = 15
    c: PointOnObject(g10,g-1)
    c: Coincident(g10,g5)
    c: Coincident(g10,g6)
    c: PointOnObject(g11,g-1)
    c: Coincident(g11,g7)
    c: Coincident(g11,g6)
    c: Equal(g11,g10)
    c: DistanceX(g6,g6) = 32
    c: Coincident(g12,g10)
    c: Coincident(g13,g11)
    c: Tangent(g13,g8) = -1.5708
    c: Tangent(g12,g9) = -1.5708
    c: Coincident(g9,g6)
    c: Coincident(g14,g5)
    c: Tangent(g14,g3) = 1.5708
    c: Tangent(g14,g12) = -1.5708
    c: Coincident(g15,g7)
    c: Tangent(g15,g1) = 1.5708
    c: Tangent(g15,g13) = -1.5708
FEATURE [PartDesign::Pad] Pad039
  Direction = (0,0,1)
  Length = 15
  Length2 = 10
  Profile = -> Sketch089
  ReferenceAxis = -> Sketch089 [N_Axis]
  Suppressed = false
  Type = 0
FEATURE [PartDesign::Body] Body041  label="MotorMountClip"
  AllowCompound = false
  Group = -> [Sketch089,Pad039]
  Origin = -> Origin043
  Placement = pos=(98,16.5,30) rot=(0,0,1;0rad)
  Tip = -> Pad039
FEATURE [Sketcher::SketchObject] Sketch090
  AttachmentOffset = pos=(0,0,-16) rot=(0,0,1;0rad)
  AttachmentSupport = -> [XZ_Plane042]
  FullyConstrained = true
  MapMode = 5
  Placement = pos=(0,16,-3.6e-15) rot=(1,0,0;1.5708rad)
  sketch-geometry (6):
    g0: LineSegment StartX=-31 StartY=27 StartZ=0 EndX=-31 EndY=-42 EndZ=0
    g1: LineSegment StartX=31 StartY=-73 StartZ=0 EndX=31 EndY=27 EndZ=0
    g2: LineSegment StartX=31 StartY=27 StartZ=0 EndX=-31 EndY=27 EndZ=0
    g3: LineSegment StartX=-31 StartY=-42 StartZ=0 EndX=0 EndY=-42 EndZ=0
    g4: LineSegment StartX=0 StartY=-42 StartZ=0 EndX=0 EndY=-73 EndZ=0
    g5: LineSegment StartX=0 StartY=-73 StartZ=0 EndX=31 EndY=-73 EndZ=0
  constraints (17):
    c: Coincident(g0,g3)
    c: Coincident(g5,g1)
    c: Coincident(g1,g2)
    c: Coincident(g2,g0)
    c: Vertical(g0)
    c: Vertical(g1)
    c: Symmetric(g0,g1,g-2)
    c: Coincident(g3,g4)
    c: Horizontal(g3)
    c: Coincident(g4,g5)
    c: PointOnObject(g4,g-2)
    c: Horizontal(g5)
    c: Vertical(g4)
    c: DistanceX(g3,g3) = 31
    c: DistanceY(g0) = -42
    c: Equal(g4,g3)
    c: DistanceY(g1,g1) = 100
FEATURE [PartDesign::Pocket] Pocket039
  BaseFeature = -> Pocket038
  Direction = (0,1,-2e-16)
  Length = 5
  Length2 = 5
  Placement = pos=(0,0,0) rot=(1,0,0;1.5708rad)
  Profile = -> Sketch090
  ReferenceAxis = -> Sketch090 [N_Axis]
  Suppressed = false
  Type = 1
FEATURE [Sketcher::SketchObject] Sketch091
  AttachmentOffset = pos=(0,0,-19.5) rot=(0,0,1;0rad)
  AttachmentSupport = -> [XZ_Plane042]
  FullyConstrained = true
  MapMode = 5
  Placement = pos=(0,19.5,-4.3e-15) rot=(1,0,0;1.5708rad)
  expr: Constraints[0] = Sketch085.Constraints[5]
  expr: Constraints[2] = Sketch085.Constraints[19]
  expr: Constraints[5] = Sketch085.Constraints[81]
  expr: Constraints[6] = Sketch085.Constraints[82]
  expr: Constraints[7] = Sketch085.Constraints[83] + 7 mm
  sketch-geometry (7):
    g0: LineSegment StartX=-77 StartY=-57.7375 StartZ=0 EndX=-77 EndY=-71.8 EndZ=0
    g1: LineSegment StartX=-77 StartY=-71.8 StartZ=0 EndX=0 EndY=-71.8 EndZ=0
    g2: ArcOfCircle CenterX=-138 CenterY=398.2 CenterZ=0 NormalX=0 NormalY=0 NormalZ=1 AngleXU=0 Radius=460 StartAngle=4.84539 EndAngle=5.01708
    g3: ArcOfCircle CenterX=-138 CenterY=398.2 CenterZ=0 NormalX=0 NormalY=0 NormalZ=1 AngleXU=0 Radius=464.5 StartAngle=4.71239 EndAngle=4.95386
    g4: ArcOfCircle CenterX=-138 CenterY=-61.8 CenterZ=0 NormalX=0 NormalY=0 NormalZ=1 AngleXU=0 Radius=4.5 StartAngle=1.5708 EndAngle=4.71239
    g5: ArcOfCircle CenterX=-28 CenterY=-48.4542 CenterZ=0 NormalX=0 NormalY=0 NormalZ=1 AngleXU=0 Radius=4.5 StartAngle=4.95386 EndAngle=8.09545
    g6: ArcOfCircle CenterX=-138 CenterY=398.2 CenterZ=0 NormalX=0 NormalY=0 NormalZ=1 AngleXU=0 Radius=455.5 StartAngle=4.71239 EndAngle=4.95386
  constraints (21):
    c: DistanceY(g1) = -71.8
    c: Vertical(g0)
    c: DistanceX(g0) = -77
    c: Horizontal(g0,g1)
    c: Coincident(g0,g1)
    c: DistanceX(g2) = -138
    c: DistanceY(g0,g2) = 470
    c: Radius(g2) = 460
    c: Coincident(g0,g2)
    c: PointOnObject(g2,g-2)
    c: PointOnObject(g1,g-2)
    c: Coincident(g3,g6)
    c: Tangent(g6,g5) = 1.5708
    c: Tangent(g6,g4) = 1.5708
    c: Tangent(g3,g5) = -1.5708
    c: Tangent(g3,g4) = -1.5708
    c: Diameter(g5) = 9
    c: PointOnObject(g5,g2)
    c: DistanceX(g2,g5) = 110
    c: Vertical(g4,g2)
    c: Coincident(g3,g2)
FEATURE [PartDesign::Pocket] Pocket040  label="Groove006"
  BaseFeature = -> Pocket039
  Direction = (0,1,-2e-16)
  Length = 23
  Length2 = 5
  Midplane = true
  Placement = pos=(0,0,0) rot=(1,0,0;1.5708rad)
  Profile = -> Sketch091
  ReferenceAxis = -> Sketch091 [N_Axis]
  Suppressed = false
  Type = 0
FEATURE [Sketcher::SketchObject] Sketch092
  AttachmentOffset = pos=(0,19.5,0) rot=(0,0,1;0rad)
  AttachmentSupport = -> [XY_Plane042]
  FullyConstrained = true
  MapMode = 5
  Placement = pos=(0,19.5,0) rot=(0,0,1;0rad)
  sketch-geometry (4):
    g0: LineSegment StartX=-102.5 StartY=7.5 StartZ=0 EndX=-102.5 EndY=-7.5 EndZ=0
    g1: LineSegment StartX=-102.5 StartY=-7.5 StartZ=0 EndX=-22.5 EndY=-7.5 EndZ=0
    g2: LineSegment StartX=-22.5 StartY=-7.5 StartZ=0 EndX=-22.5 EndY=7.5 EndZ=0
    g3: LineSegment StartX=-22.5 StartY=7.5 StartZ=0 EndX=-102.5 EndY=7.5 EndZ=0
  constraints (11):
    c: Coincident(g0,g1)
    c: Coincident(g1,g2)
    c: Coincident(g2,g3)
    c: Coincident(g3,g0)
    c: Vertical(g0)
    c: Horizontal(g1)
    c: Horizontal(g3)
    c: Symmetric(g1,g2,g-1)
    c: DistanceY(g0,g0) = 15
    c: DistanceX(g1,g1) = 80
    c: DistanceX(g1) = -22.5
FEATURE [PartDesign::Pocket] Pocket041
  BaseFeature = -> Pocket040
  Direction = (0,0,-1)
  Length = 5
  Length2 = 5
  Placement = pos=(0,0,0) rot=(1,0,0;1.5708rad)
  Profile = -> Sketch092
  ReferenceAxis = -> Sketch092 [N_Axis]
  Suppressed = false
  Type = 1
FEATURE [PartDesign::Plane] DatumPlane
  AttachmentOffset = pos=(0,0,-2.5) rot=(0,0,1;0rad)
  AttachmentSupport = -> [Sketch091]
  Length = 60
  MapMode = 2
  Placement = pos=(0,22,-4.9e-15) rot=(1,0,0;1.5708rad)
  ResizeMode = 0
  Support = -> [Sketch091]
  Width = 60
FEATURE [PartDesign::FeaturePython] InvoluteGear006  label="M2.5-18T003"  # WARN: FeaturePython — macro-defined, semantics opaque (R4)
  AttacherType = Attacher::AttachEngine3D
  Placement = pos=(0,0,0) rot=(1,0,0;1.5708rad)
  Suppressed = false
  angular_backlash = 0.254648
  backlash = 0.1
  beta = 0
  clearance = 0.25
  da = 50
  df = 38.75
  double_helix = false
  dw = 45
  head = 0
  head_fillet = 0
  height = 5
  module = 2.5
  numpoints = 6
  pressure_angle = 20
  properties_from_tool = false
  reversed_backlash = false
  root_fillet = 0
  shift = 0
  simple = false
  teeth = 18
  transverse_pitch = 7.85398
  undercut = false
  version = 0.0.4
  expr: angular_backlash = backlash / dw * 360 ° / pi
  expr: dw = teeth * module
FEATURE [Sketcher::SketchObject] Sketch093
  AttachmentSupport = -> [XZ_Plane044]
  FullyConstrained = true
  MapMode = 5
  Placement = pos=(0,0,0) rot=(1,0,0;1.5708rad)
  sketch-geometry (7):
    g0: ArcOfCircle CenterX=0 CenterY=0 CenterZ=0 NormalX=0 NormalY=0 NormalZ=1 AngleXU=0 Radius=6 StartAngle=0.429775 EndAngle=1.66462
    g1: ArcOfCircle CenterX=0 CenterY=0 CenterZ=0 NormalX=0 NormalY=0 NormalZ=1 AngleXU=0 Radius=17 StartAngle=0.147594 EndAngle=1.9468
    g2: LineSegment StartX=16.8152 StartY=2.5 StartZ=0 EndX=5.45436 EndY=2.5 EndZ=0
    g3: LineSegment StartX=-0.562115 StartY=5.97361 StartZ=0 EndX=-6.24252 EndY=15.8124 EndZ=0
    g4: LineSegment StartX=0 StartY=0 StartZ=0 EndX=-8.40759 EndY=14.5624 EndZ=0
    g5: LineSegment StartX=-8.40759 StartY=14.5624 StartZ=0 EndX=-6.24252 EndY=15.8124 EndZ=0
    g6: LineSegment StartX=16.8152 StartY=2.5 StartZ=0 EndX=16.8152 EndY=0 EndZ=0
  constraints (20):
    c: Coincident(g2,g1)
    c: Coincident(g2,g0)
    c: Coincident(g3,g0)
    c: Coincident(g3,g1)
    c: Coincident(g5,g4)
    c: Coincident(g5,g1)
    c: Parallel(g4,g3)
    c: Perpendicular(g4,g5)
    c: Angle(g-1,g4) = 2.0944
    c: Horizontal(g2)
    c: Coincident(g6,g1)
    c: PointOnObject(g6,g-1)
    c: Vertical(g6)
    c: Equal(g6,g5)
    c: Diameter(g0) = 12
    c: Diameter(g1) = 34
    c: DistanceY(g6,g6) = 2.5
    c: Coincident(g0,g4)
    c: Coincident(g0,g1)
    c: Coincident(g0,g-1)
FEATURE [PartDesign::Pocket] Pocket042  label="120deg-sector005"
  BaseFeature = -> InvoluteGear006
  Direction = (0,1,-2e-16)
  Length = 5
  Length2 = 5
  Midplane = true
  Placement = pos=(0,0,0) rot=(1,0,0;1.5708rad)
  Profile = -> Sketch093
  ReferenceAxis = -> Sketch093 [N_Axis]
  Refine = true
  Suppressed = false
  Type = 1
FEATURE [PartDesign::PolarPattern] PolarPattern005
  Angle = 360
  Axis = -> Sketch093 [N_Axis]
  BaseFeature = -> Pocket042
  Mode = 0
  Occurrences = 3
  Offset = 120
  Originals = -> [Pocket042]
  Placement = pos=(0,0,0) rot=(1,0,0;1.5708rad)
  Refine = true
  Suppressed = false
  TransformMode = 0
FEATURE [Sketcher::SketchObject] Sketch094
  AttachmentSupport = -> [XZ_Plane044]
  FullyConstrained = true
  MapMode = 5
  Placement = pos=(0,0,0) rot=(1,0,0;1.5708rad)
  sketch-geometry (2):
    g0: ArcOfCircle CenterX=0 CenterY=0 CenterZ=0 NormalX=0 NormalY=0 NormalZ=1 AngleXU=0 Radius=3.05 StartAngle=3.75155 EndAngle=8.81482
    g1: LineSegment StartX=-2.5 StartY=-1.74714 StartZ=0 EndX=-2.5 EndY=1.74714 EndZ=0
  constraints (6):
    c: Coincident(g0,g-1)
    c: Coincident(g0,g1)
    c: Coincident(g1,g0)
    c: Diameter(g0) = 6.1
    c: Vertical(g1)
    c: DistanceX(g0) = -2.5
FEATURE [Sketcher::SketchObject] Sketch095
  AttachmentSupport = -> [XY_Plane044]
  FullyConstrained = true
  MapMode = 5
  sketch-geometry (4):
    g0: LineSegment StartX=0 StartY=0 StartZ=0 EndX=6 EndY=0 EndZ=0
    g1: LineSegment StartX=6 StartY=0 StartZ=0 EndX=4 EndY=6 EndZ=0
    g2: LineSegment StartX=4 StartY=6 StartZ=0 EndX=0 EndY=6 EndZ=0
    g3: LineSegment StartX=0 StartY=6 StartZ=0 EndX=0 EndY=0 EndZ=0
  constraints (11):
    c: Coincident(g-1,g0)
    c: Horizontal(g0)
    c: Coincident(g0,g1)
    c: Coincident(g1,g2)
    c: PointOnObject(g2,g-2)
    c: Horizontal(g2)
    c: Coincident(g2,g3)
    c: Coincident(g3,g0)
    c: DistanceX(g0,g0) = 6
    c: DistanceY(g3,g3) = 6
    c: DistanceX(g2,g2) = 4
FEATURE [PartDesign::Revolution] Revolution005
  Angle = 360
  Angle2 = 60
  Axis = (0,1,0)
  Base = (0,0,0)
  BaseFeature = -> PolarPattern005
  Placement = pos=(0,0,0) rot=(1,0,0;1.5708rad)
  Profile = -> Sketch095
  ReferenceAxis = -> Sketch095 [V_Axis]
  Reversed = true
  Suppressed = false
  Type = 0
FEATURE [PartDesign::Pocket] Pocket043  label="D6Shaft002"
  BaseFeature = -> Revolution005
  Direction = (0,1,-2e-16)
  Length = 5
  Length2 = 5
  Midplane = true
  Placement = pos=(0,0,0) rot=(1,0,0;1.5708rad)
  Profile = -> Sketch094
  ReferenceAxis = -> Sketch094 [N_Axis]
  Suppressed = false
  Type = 1
FEATURE [Sketcher::SketchObject] Sketch096
  AttachmentSupport = -> [YZ_Plane044]
  FullyConstrained = true
  MapMode = 5
  Placement = pos=(0,0,0) rot=(0.57735,0.57735,0.57735;2.0944rad)
  sketch-geometry (7):
    g0: LineSegment StartX=-1.17209 StartY=0 StartZ=0 EndX=-1.83605 EndY=1.15 EndZ=0
    g1: LineSegment StartX=-1.83605 StartY=1.15 StartZ=0 EndX=-3.16395 EndY=1.15 EndZ=0
    g2: LineSegment StartX=-3.16395 StartY=1.15 StartZ=0 EndX=-3.82791 EndY=1.423e-13 EndZ=0
    g3: LineSegment StartX=-3.82791 StartY=1.423e-13 StartZ=0 EndX=-3.16395 EndY=-1.15 EndZ=0
    g4: LineSegment StartX=-3.16395 StartY=-1.15 StartZ=0 EndX=-1.83605 EndY=-1.15 EndZ=0
    g5: LineSegment StartX=-1.83605 StartY=-1.15 StartZ=0 EndX=-1.17209 EndY=0 EndZ=0
    g6: Circle CenterX=-2.5 CenterY=0 CenterZ=0 NormalX=0 NormalY=0 NormalZ=1 AngleXU=0 Radius=1.32791
  constraints (17):
    c: Coincident(g0,g1)
    c: Coincident(g1,g2)
    c: Coincident(g2,g3)
    c: Coincident(g3,g4)
    c: Coincident(g4,g5)
    c: Coincident(g5,g0)
    c: Equal(g0, g1-g5) x5
    c: PointOnObject(g0,g6)
    c: PointOnObject(g1,g6)
    c: PointOnObject(g2,g6)
    c: PointOnObject(g3,g6)
    c: PointOnObject(g4,g6)
    c: PointOnObject(g5,g6)
    c: PointOnObject(g6,g-1)
    c: DistanceX(g6) = -2.5
    c: PointOnObject(g0,g-1)
    c: DistanceY(g4,g0) = 2.3
FEATURE [PartDesign::Pocket] Pocket044
  BaseFeature = -> Pocket043
  Direction = (-1,0,0)
  Length = 24
  Length2 = 5
  Midplane = true
  Placement = pos=(0,0,0) rot=(1,0,0;1.5708rad)
  Profile = -> Sketch096
  ReferenceAxis = -> Sketch096 [N_Axis]
  Suppressed = false
  Type = 0
FEATURE [PartDesign::Body] Body042  label="M2,5-18T-D6mm"
  AllowCompound = false
  Group = -> [InvoluteGear006,Sketch093,Pocket042,PolarPattern005,Sketch094,Sketch095,Revolution005,Pocket043,Sketch096,Pocket044]
  Origin = -> Origin044
  Placement = pos=(98,0,36.8) rot=(0,0,1;0rad)
  Tip = -> Pocket044
FEATURE [Sketcher::SketchObject] Sketch097
  AttachmentSupport = -> [XZ_Plane045]
  FullyConstrained = true
  MapMode = 5
  Placement = pos=(0,0,0) rot=(1,0,0;1.5708rad)
  sketch-geometry (26):
    g0: ArcOfCircle CenterX=0 CenterY=470 CenterZ=0 NormalX=0 NormalY=0 NormalZ=1 AngleXU=0 Radius=453 StartAngle=4.47935 EndAngle=4.5684
    g1: LineSegment StartX=-112 StartY=23.4073 StartZ=0 EndX=-112 EndY=0 EndZ=0
    g2: LineSegment StartX=-112 StartY=0 StartZ=0 EndX=-81.7609 EndY=0 EndZ=0
    g3: LineSegment StartX=-65 StartY=21.6876 StartZ=0 EndX=-65 EndY=6.1 EndZ=0
    g4: LineSegment StartX=-65 StartY=6.1 StartZ=0 EndX=-37.4218 EndY=6.1 EndZ=0
    g5: LineSegment StartX=-37.4218 StartY=6.1 StartZ=0 EndX=-33.5218 EndY=10 EndZ=0
    g6: LineSegment StartX=-33.5218 StartY=10 StartZ=0 EndX=-26.4782 EndY=10 EndZ=0
    g7: LineSegment StartX=-26.4782 StartY=10 StartZ=0 EndX=-22.5782 EndY=6.1 EndZ=0
    g8: LineSegment StartX=-22.5782 StartY=6.1 StartZ=0 EndX=-22.5782 EndY=0 EndZ=0
    g9: LineSegment StartX=-22.5782 StartY=0 StartZ=0 EndX=-28.2391 EndY=0 EndZ=0
    g10: LineSegment StartX=-28.2391 StartY=0 StartZ=0 EndX=-26.4782 EndY=3.05 EndZ=0
    g11: LineSegment StartX=-26.4782 StartY=3.05 StartZ=0 EndX=-28.2391 EndY=6.1 EndZ=0
    g12: LineSegment StartX=-28.2391 StartY=6.1 StartZ=0 EndX=-31.7609 EndY=6.1 EndZ=0
    g13: LineSegment StartX=-31.7609 StartY=6.1 StartZ=0 EndX=-33.5218 EndY=3.05 EndZ=0
    g14: LineSegment StartX=-33.5218 StartY=3.05 StartZ=0 EndX=-31.7609 EndY=0 EndZ=0
    g15: LineSegment StartX=-31.7609 StartY=0 StartZ=0 EndX=-28.2391 EndY=0 EndZ=0
    g16: Circle CenterX=-30 CenterY=3.05 CenterZ=0 NormalX=0 NormalY=0 NormalZ=1 AngleXU=0 Radius=3.52184
    g17: LineSegment StartX=-31.7609 StartY=0 StartZ=0 EndX=-78.2391 EndY=0 EndZ=0
    g18: LineSegment StartX=-78.2391 StartY=0 StartZ=0 EndX=-76.4782 EndY=3.05 EndZ=0
    g19: LineSegment StartX=-76.4782 StartY=3.05 StartZ=0 EndX=-78.2391 EndY=6.1 EndZ=0
    g20: LineSegment StartX=-78.2391 StartY=6.1 StartZ=0 EndX=-81.7609 EndY=6.1 EndZ=0
    g21: LineSegment StartX=-81.7609 StartY=6.1 StartZ=0 EndX=-83.5218 EndY=3.05 EndZ=0
    g22: LineSegment StartX=-83.5218 StartY=3.05 StartZ=0 EndX=-81.7609 EndY=0 EndZ=0
    g23: LineSegment StartX=-81.7609 StartY=0 StartZ=0 EndX=-78.2391 EndY=0 EndZ=0
    g24: Circle CenterX=-80 CenterY=3.05 CenterZ=0 NormalX=0 NormalY=0 NormalZ=1 AngleXU=0 Radius=3.52184
    g25: ArcOfCircle CenterX=-106 CenterY=23.4073 CenterZ=0 NormalX=0 NormalY=0 NormalZ=1 AngleXU=0 Radius=6 StartAngle=1.33776 EndAngle=3.14159
  constraints (68):
    c: PointOnObject(g0,g-2)
    c: DistanceY(g0) = 470
    c: Radius(g0) = 453
    c: Coincident(g1,g2)
    c: PointOnObject(g2,g-1)
    c: Horizontal(g2)
    c: Coincident(g0,g3)
    c: Vertical(g3)
    c: Coincident(g3,g4)
    c: Horizontal(g4)
    c: Coincident(g4,g5)
    c: Coincident(g5,g6)
    c: Horizontal(g6)
    c: Coincident(g6,g7)
    c: Coincident(g7,g8)
    c: PointOnObject(g8,g-1)
    c: Coincident(g8,g9)
    c: Horizontal(g9)
    c: DistanceY(g4) = 6.1
    c: Angle(g5) = 0.785398
    c: DistanceY(g5) = 10
    c: Vertical(g8)
    c: Horizontal(g7,g4)
    c: Angle(g7) = -0.785398
    c: Coincident(g10,g11)
    c: Coincident(g11,g12)
    c: Coincident(g12,g13)
    c: Coincident(g13,g14)
    c: Coincident(g14,g15)
    c: Coincident(g15,g10)
    c: Equal(g10, g11-g15) x5
    c: PointOnObject(g10,g16)
    c: PointOnObject(g11,g16)
    c: PointOnObject(g12,g16)
    c: PointOnObject(g13,g16)
    c: PointOnObject(g14,g16)
    c: PointOnObject(g15,g16)
    c: Coincident(g15,g9)
    c: Horizontal(g15)
    c: Horizontal(g12,g4)
    c: Vertical(g13,g5)
    c: Vertical(g10,g6)
    c: DistanceX(g16) = -30
    c: Coincident(g14,g17)
    c: Horizontal(g17)
    c: Coincident(g18,g19)
    c: Coincident(g19,g20)
    c: Coincident(g20,g21)
    c: Coincident(g21,g22)
    c: Coincident(g22,g23)
    c: Coincident(g23,g18)
    c: Equal(g18, g19-g23) x5
    c: PointOnObject(g18,g24)
    c: PointOnObject(g19,g24)
    c: PointOnObject(g20,g24)
    c: PointOnObject(g21,g24)
    c: PointOnObject(g22,g24)
    c: PointOnObject(g23,g24)
    c: Coincident(g23,g17)
    c: Equal(g24,g16)
    c: DistanceX(g24,g16) = 50
    c: Coincident(g2,g22)
    c: DistanceX(g24,g3) = 15
    c: Vertical(g1)
    c: DistanceX(g1) = -112
    c: Tangent(g25,g1) = -1.5708
    c: Tangent(g25,g0) = 1.5708
    c: Radius(g25) = 6
FEATURE [PartDesign::Pad] Pad040
  Direction = (0,-1,2e-16)
  Length = 27
  Length2 = 10
  Placement = pos=(0,0,0) rot=(1,0,0;1.5708rad)
  Profile = -> Sketch097
  ReferenceAxis = -> Sketch097 [N_Axis]
  Reversed = true
  Suppressed = false
  Type = 0
FEATURE [Sketcher::SketchObject] Sketch098
  AttachmentOffset = pos=(0,0,-13.5) rot=(0,0,1;0rad)
  AttachmentSupport = -> [XZ_Plane045]
  FullyConstrained = true
  MapMode = 5
  Placement = pos=(0,13.5,-3e-15) rot=(1,0,0;1.5708rad)
  expr: Constraints[1] = Sketch097.Constraints[1]
  expr: Constraints[2] = Sketch097.Constraints[2] + 7 mm
  sketch-geometry (5):
    g0: ArcOfCircle CenterX=0 CenterY=470 CenterZ=0 NormalX=0 NormalY=0 NormalZ=1 AngleXU=0 Radius=460 StartAngle=4.4821 EndAngle=4.71239
    g1: ArcOfCircle CenterX=0 CenterY=470 CenterZ=0 NormalX=0 NormalY=0 NormalZ=1 AngleXU=0 Radius=464.5 StartAngle=4.4821 EndAngle=4.62532
    g2: ArcOfCircle CenterX=-105 CenterY=22.144 CenterZ=0 NormalX=0 NormalY=0 NormalZ=1 AngleXU=0 Radius=4.5 StartAngle=1.34051 EndAngle=4.4821
    g3: ArcOfCircle CenterX=-40 CenterY=11.7424 CenterZ=0 NormalX=0 NormalY=0 NormalZ=1 AngleXU=0 Radius=4.5 StartAngle=4.62532 EndAngle=7.76692
    g4: ArcOfCircle CenterX=0 CenterY=470 CenterZ=0 NormalX=0 NormalY=0 NormalZ=1 AngleXU=0 Radius=455.5 StartAngle=4.4821 EndAngle=4.62532
  constraints (14):
    c: PointOnObject(g0,g-2)
    c: DistanceY(g0) = 470
    c: Radius(g0) = 460
    c: PointOnObject(g0,g-2)
    c: DistanceX(g0) = -105
    c: Coincident(g1,g4)
    c: Tangent(g4,g3) = 1.5708
    c: Tangent(g4,g2) = 1.5708
    c: Tangent(g1,g3) = -1.5708
    c: Tangent(g1,g2) = -1.5708
    c: Coincident(g2,g0)
    c: Diameter(g2) = 9
    c: Coincident(g1,g0)
    c: DistanceX(g3) = -40
FEATURE [PartDesign::Pocket] Pocket045  label="RockerGroove"
  BaseFeature = -> Pad040
  Direction = (0,1,-2e-16)
  Length = 23
  Length2 = 5
  Midplane = true
  Placement = pos=(0,0,0) rot=(1,0,0;1.5708rad)
  Profile = -> Sketch098
  ReferenceAxis = -> Sketch098 [N_Axis]
  Suppressed = false
  Type = 0
FEATURE [Sketcher::SketchObject] Sketch099
  AttachmentOffset = pos=(0,0,-13.5) rot=(0,0,1;0rad)
  AttachmentSupport = -> [XZ_Plane045]
  FullyConstrained = true
  MapMode = 5
  Placement = pos=(0,13.5,-3e-15) rot=(1,0,0;1.5708rad)
  sketch-geometry (10):
    g0: LineSegment StartX=-73.1 StartY=0 StartZ=0 EndX=-37.4 EndY=0 EndZ=0
    g1: LineSegment StartX=-37.4 StartY=0 StartZ=0 EndX=-37.4 EndY=90 EndZ=0
    g2: LineSegment StartX=-37.4 StartY=90 StartZ=0 EndX=-127.4 EndY=90 EndZ=0
    g3: LineSegment StartX=-73.1 StartY=0 StartZ=0 EndX=-73.1 EndY=6.1 EndZ=0
    g4: LineSegment StartX=-73.1 StartY=6.1 StartZ=0 EndX=-77 EndY=10 EndZ=0
    g5: LineSegment StartX=-77 StartY=10 StartZ=0 EndX=-83 EndY=10 EndZ=0
    g6: LineSegment StartX=-83 StartY=10 StartZ=0 EndX=-86.9 EndY=6.1 EndZ=0
    g7: LineSegment StartX=-86.9 StartY=6.1 StartZ=0 EndX=-86.9 EndY=0 EndZ=0
    g8: LineSegment StartX=-86.9 StartY=0 StartZ=0 EndX=-127.4 EndY=0 EndZ=0
    g9: LineSegment StartX=-127.4 StartY=0 StartZ=0 EndX=-127.4 EndY=90 EndZ=0
  constraints (30):
    c: Coincident(g0,g1)
    c: Coincident(g1,g2)
    c: Vertical(g1)
    c: Horizontal(g0)
    c: Horizontal(g2)
    c: PointOnObject(g0,g-1)
    c: DistanceX(g0) = -37.4
    c: Coincident(g0,g3)
    c: Vertical(g3)
    c: Coincident(g3,g4)
    c: Coincident(g4,g5)
    c: Horizontal(g5)
    c: Coincident(g5,g6)
    c: Coincident(g6,g7)
    c: PointOnObject(g7,g-1)
    c: Vertical(g7)
    c: Coincident(g7,g8)
    c: Horizontal(g8)
    c: Coincident(g8,g9)
    c: Coincident(g9,g2)
    c: Vertical(g9)
    c: DistanceX(g2,g2) = 90
    c: Angle(g6) = -2.35619
    c: Angle(g4) = 2.35619
    c: Equal(g4,g6)
    c: DistanceY(g4) = 10
    c: DistanceX(g5,g5) = 6
    c: DistanceX(g4) = -77
    c: DistanceY(g3,g3) = 6.1
    c: Equal(g2,g9)
FEATURE [PartDesign::Pocket] Pocket046
  BaseFeature = -> Pocket045
  Direction = (0,1,-2e-16)
  Length = 15
  Length2 = 5
  Midplane = true
  Placement = pos=(0,0,0) rot=(1,0,0;1.5708rad)
  Profile = -> Sketch099
  ReferenceAxis = -> Sketch099 [N_Axis]
  Suppressed = false
  Type = 0
FEATURE [PartDesign::Plane] DatumPlane001
  AttachmentOffset = pos=(0,0,-22) rot=(0,0,1;0rad)
  AttachmentSupport = -> [XZ_Plane045]
  Length = 1543.67
  MapMode = 5
  Placement = pos=(0,22,-4.9e-15) rot=(1,0,0;1.5708rad)
  ResizeMode = 0
  Support = -> [XZ_Plane045]
  Width = 2163.64
FEATURE [Sketcher::SketchObject] Sketch100
  AttachmentSupport = -> [YZ_Plane046]
  FullyConstrained = true
  MapMode = 5
  Placement = pos=(0,0,0) rot=(0.57735,0.57735,0.57735;2.0944rad)
  sketch-geometry (12):
    g0: LineSegment StartX=-7 StartY=0 StartZ=0 EndX=-7 EndY=-1.8 EndZ=0
    g1: LineSegment StartX=-7 StartY=-1.8 StartZ=0 EndX=7 EndY=-1.8 EndZ=0
    g2: LineSegment StartX=7 StartY=-1.8 StartZ=0 EndX=7 EndY=0 EndZ=0
    g3: LineSegment StartX=7 StartY=0 StartZ=0 EndX=1.2 EndY=0 EndZ=0
    g4: LineSegment StartX=1.85 StartY=1.6 StartZ=0 EndX=-1.85 EndY=1.6 EndZ=0
    g5: LineSegment StartX=-1.2 StartY=0 StartZ=0 EndX=-7 EndY=0 EndZ=0
    g6: LineSegment StartX=-1.2 StartY=0.2 StartZ=0 EndX=-1.2 EndY=0 EndZ=0
    g7: LineSegment StartX=1.2 StartY=0 StartZ=0 EndX=1.2 EndY=0.2 EndZ=0
    g8: LineSegment StartX=1.2 StartY=0.2 StartZ=0 EndX=1.85 EndY=1 EndZ=0
    g9: LineSegment StartX=1.85 StartY=1 StartZ=0 EndX=1.85 EndY=1.6 EndZ=0
    g10: LineSegment StartX=-1.85 StartY=1.6 StartZ=0 EndX=-1.85 EndY=1 EndZ=0
    g11: LineSegment StartX=-1.85 StartY=1 StartZ=0 EndX=-1.2 EndY=0.2 EndZ=0
  constraints (33):
    c: PointOnObject(g0,g-1)
    c: Vertical(g0)
    c: Coincident(g0,g1)
    c: Horizontal(g1)
    c: Coincident(g1,g2)
    c: Coincident(g2,g3)
    c: PointOnObject(g3,g-1)
    c: Coincident(g3,g7)
    c: Coincident(g9,g4)
    c: Coincident(g4,g10)
    c: Coincident(g6,g5)
    c: Coincident(g5,g0)
    c: Symmetric(g0,g2,g-2)
    c: Vertical(g2)
    c: DistanceX(g1,g1) = 14
    c: Symmetric(g6,g3,g-2)
    c: Symmetric(g4,g9,g-2)
    c: DistanceY(g2,g2) = 1.8
    c: DistanceY(g9) = 1.6
    c: DistanceX(g6,g3) = 2.4
    c: Coincident(g11,g6)
    c: Coincident(g7,g8)
    c: Coincident(g8,g9)
    c: Coincident(g10,g11)
    c: Equal(g6,g7)
    c: Vertical(g7)
    c: Vertical(g6)
    c: Vertical(g10)
    c: Vertical(g9)
    c: Equal(g9,g10)
    c: DistanceY(g9,g9) = 0.6
    c: DistanceY(g7,g7) = 0.2
    c: DistanceX(g4,g4) = 3.7
FEATURE [PartDesign::Pad] Pad041  label="Prfofile"
  Direction = (1,0,0)
  Length = 182
  Length2 = 10
  Midplane = true
  Placement = pos=(0,0,0) rot=(0.57735,0.57735,0.57735;2.0944rad)
  Profile = -> Sketch100
  ReferenceAxis = -> Sketch100 [N_Axis]
  Refine = true
  Suppressed = false
  Type = 0
FEATURE [Sketcher::SketchObject] Sketch101
  AttachmentSupport = -> [XZ_Plane046]
  FullyConstrained = true
  MapMode = 5
  Placement = pos=(0,0,0) rot=(1,0,0;1.5708rad)
  sketch-geometry (4):
    g0: ArcOfCircle CenterX=-91.5 CenterY=0 CenterZ=0 NormalX=0 NormalY=0 NormalZ=1 AngleXU=0 Radius=3.25 StartAngle=5.69621 EndAngle=10.0118
    g1: LineSegment StartX=-94.206 StartY=-1.8 StartZ=0 EndX=-88.794 EndY=-1.8 EndZ=0
    g2: ArcOfCircle CenterX=91.5 CenterY=0 CenterZ=0 NormalX=0 NormalY=0 NormalZ=1 AngleXU=0 Radius=3.25 StartAngle=5.69621 EndAngle=10.0118
    g3: LineSegment StartX=94.206 StartY=-1.8 StartZ=0 EndX=88.794 EndY=-1.8 EndZ=0
  constraints (13):
    c: PointOnObject(g0,g-1)
    c: Coincident(g0,g1)
    c: Coincident(g1,g0)
    c: Horizontal(g1)
    c: Diameter(g0) = 6.5
    c: DistanceY(g0) = -1.8
    c: Coincident(g2,g3)
    c: Coincident(g3,g2)
    c: Horizontal(g3)
    c: Horizontal(g2,g0)
    c: Equal(g0,g2)
    c: Symmetric(g0,g2,g-2)
    c: DistanceX(g0,g2) = 183
FEATURE [PartDesign::Pad] Pad042  label="Shafts"
  BaseFeature = -> Pad041
  Direction = (0,-1,2e-16)
  Length = 21.6
  Length2 = 10
  Midplane = true
  Placement = pos=(0,0,0) rot=(0.57735,0.57735,0.57735;2.0944rad)
  Profile = -> Sketch101
  ReferenceAxis = -> Sketch101 [N_Axis]
  Refine = true
  Suppressed = false
  Type = 0
FEATURE [Sketcher::SketchObject] Sketch102
  AttachmentSupport = -> [XZ_Plane046]
  FullyConstrained = true
  MapMode = 5
  Placement = pos=(0,0,0) rot=(1,0,0;1.5708rad)
  sketch-geometry (12):
    g0: LineSegment StartX=-90.2 StartY=4 StartZ=0 EndX=-90.2 EndY=0 EndZ=0
    g1: LineSegment StartX=-90.2 StartY=0 StartZ=0 EndX=-70 EndY=0 EndZ=0
    g2: LineSegment StartX=-70 StartY=0 StartZ=0 EndX=-70 EndY=4 EndZ=0
    g3: LineSegment StartX=-70 StartY=4 StartZ=0 EndX=-90.2 EndY=4 EndZ=0
    g4: LineSegment StartX=-50 StartY=4 StartZ=0 EndX=-50 EndY=0 EndZ=0
    g5: LineSegment StartX=-50 StartY=0 StartZ=0 EndX=50 EndY=0 EndZ=0
    g6: LineSegment StartX=50 StartY=0 StartZ=0 EndX=50 EndY=4 EndZ=0
    g7: LineSegment StartX=50 StartY=4 StartZ=0 EndX=-50 EndY=4 EndZ=0
    g8: LineSegment StartX=70 StartY=4 StartZ=0 EndX=70 EndY=0 EndZ=0
    g9: LineSegment StartX=70 StartY=0 StartZ=0 EndX=90.2 EndY=0 EndZ=0
    g10: LineSegment StartX=90.2 StartY=0 StartZ=0 EndX=90.2 EndY=4 EndZ=0
    g11: LineSegment StartX=90.2 StartY=4 StartZ=0 EndX=70 EndY=4 EndZ=0
  constraints (35):
    c: Coincident(g0,g1)
    c: Coincident(g1,g2)
    c: Coincident(g2,g3)
    c: Coincident(g3,g0)
    c: Vertical(g0)
    c: Vertical(g2)
    c: Horizontal(g1)
    c: Horizontal(g3)
    c: PointOnObject(g1,g-1)
    c: Coincident(g4,g5)
    c: Coincident(g5,g6)
    c: Coincident(g6,g7)
    c: Coincident(g7,g4)
    c: Vertical(g4)
    c: Vertical(g6)
    c: Horizontal(g5)
    c: PointOnObject(g5,g-1)
    c: Coincident(g8,g9)
    c: Coincident(g9,g10)
    c: Coincident(g10,g11)
    c: Coincident(g11,g8)
    c: Vertical(g8)
    c: Vertical(g10)
    c: Horizontal(g9)
    c: Horizontal(g11)
    c: PointOnObject(g9,g-1)
    c: Equal(g11,g3)
    c: Symmetric(g4,g6,g-2)
    c: DistanceX(g7,g7) = 100
    c: DistanceX(g2,g4) = 20
    c: DistanceX(g6,g8) = 20
    c: Equal(g8,g6)
    c: Equal(g2,g4)
    c: DistanceX(g0,g10) = 180.4
    c: DistanceY(g6,g6) = 4
FEATURE [Sketcher::SketchObject] Sketch103
  AttachmentOffset = pos=(0,0,7) rot=(0,0,1;0rad)
  AttachmentSupport = -> [XZ_Plane046]
  FullyConstrained = true
  MapMode = 5
  Placement = pos=(0,-7,1.6e-15) rot=(1,0,0;1.5708rad)
  sketch-geometry (2):
    g0: ArcOfCircle CenterX=40 CenterY=0.4 CenterZ=0 NormalX=0 NormalY=0 NormalZ=1 AngleXU=0 Radius=2.5 StartAngle=5.20732 EndAngle=10.5006
    g1: LineSegment StartX=38.8126 StartY=-1.8 StartZ=0 EndX=41.1874 EndY=-1.8 EndZ=0
  constraints (7):
    c: Coincident(g0,g1)
    c: Coincident(g1,g0)
    c: Horizontal(g1)
    c: DistanceY(g0) = -1.8
    c: Diameter(g0) = 5
    c: DistanceY(g0) = 0.4
    c: DistanceX(g0) = 40
FEATURE [PartDesign::Pad] Pad043  label="DriverPin"
  BaseFeature = -> Pad042
  Direction = (0,-1,2e-16)
  Length = 5.5
  Length2 = 10
  Placement = pos=(0,0,0) rot=(0.57735,0.57735,0.57735;2.0944rad)
  Profile = -> Sketch103
  ReferenceAxis = -> Sketch103 [N_Axis]
  Refine = true
  Suppressed = false
  Type = 0
FEATURE [PartDesign::Chamfer] Chamfer
  Angle = 45
  Base = -> Pocket041 [Edge213,Edge121]
  BaseFeature = -> Pocket041
  ChamferType = 1
  FlipDirection = false
  Placement = pos=(0,0,0) rot=(1,0,0;1.5708rad)
  Size = 1
  Size2 = 3
  SupportTransform = false
  Suppressed = false
  UseAllEdges = false
FEATURE [PartDesign::Body] Body040  label="RightMotorMount"
  AllowCompound = false
  Group = -> [Sketch085,Pad038,Sketch086,Pocket036,Sketch087,Pocket037,Sketch088,Pocket038,Sketch090,Pocket039,Sketch091,Pocket040,Sketch092,Pocket041,DatumPlane,Chamfer]
  Origin = -> Origin042
  Placement = pos=(98,2.5,36.8) rot=(0,0,1;0rad)
  Tip = -> Chamfer
FEATURE [Part::FeaturePython] Slice  # WARN: FeaturePython — macro-defined, semantics opaque (R4)
  Base = -> Body040
  Mode = 1
  Tolerance = 0
  Tools = -> [DatumPlane]
FEATURE [Part::FeaturePython] Slice_child0  label="MotorMountSlice0"  # WARN: FeaturePython — macro-defined, semantics opaque (R4)
  Base = -> Slice
  FilterType = 1
  Invert = false
  OverrideMaxVal = 0
  WindowFrom = 80
  WindowTo = 100
  items = 0
FEATURE [Part::FeaturePython] Slice_child1  label="MotorMountSlice1"  # WARN: FeaturePython — macro-defined, semantics opaque (R4)
  Base = -> Slice
  FilterType = 1
  Invert = false
  OverrideMaxVal = 0
  WindowFrom = 80
  WindowTo = 100
  items = 1
FEATURE [App::DocumentObjectGroup] GrExplode_Slice  label="Exploded Slice"
  Group = -> [Slice_child0,Slice_child1]
FEATURE [PartDesign::Chamfer] Chamfer001
  Angle = 45
  Base = -> Pocket046 [Edge31]
  BaseFeature = -> Pocket046
  ChamferType = 1
  FlipDirection = false
  Placement = pos=(0,0,0) rot=(1,0,0;1.5708rad)
  Size = 1
  Size2 = 3
  SupportTransform = false
  Suppressed = false
  UseAllEdges = false
FEATURE [PartDesign::Chamfer] Chamfer002
  Angle = 45
  Base = -> Chamfer001 [Edge121]
  BaseFeature = -> Chamfer001
  ChamferType = 1
  FlipDirection = false
  Placement = pos=(0,0,0) rot=(1,0,0;1.5708rad)
  Size = 3
  Size2 = 1
  SupportTransform = false
  Suppressed = false
  UseAllEdges = false
FEATURE [PartDesign::Body] Body043  label="LeftRockerGroove"
  AllowCompound = false
  Group = -> [Sketch097,Pad040,Sketch098,Pocket045,Sketch099,Pocket046,Chamfer001,Chamfer002]
  Origin = -> Origin045
  Placement = pos=(-40,8.5,-35) rot=(0,0,1;0rad)
  Tip = -> Chamfer002
FEATURE [Part::FeaturePython] Slice001  # WARN: FeaturePython — macro-defined, semantics opaque (R4)
  Base = -> Body043
  Mode = 1
  Tolerance = 0
  Tools = -> [DatumPlane001]
FEATURE [Part::FeaturePython] Slice001_child0  label="LeftRockGrooveSlice1"  # WARN: FeaturePython — macro-defined, semantics opaque (R4)
  Base = -> Slice001
  FilterType = 1
  Invert = false
  OverrideMaxVal = 0
  WindowFrom = 80
  WindowTo = 100
  items = 0
FEATURE [Part::FeaturePython] Slice001_child1  label="LeftRockGrooveSlice2"  # WARN: FeaturePython — macro-defined, semantics opaque (R4)
  Base = -> Slice001
  FilterType = 1
  Invert = false
  OverrideMaxVal = 0
  WindowFrom = 80
  WindowTo = 100
  items = 1
FEATURE [App::DocumentObjectGroup] GrExplode_Slice001  label="Exploded Slice001"
  Group = -> [Slice001_child0,Slice001_child1]
FEATURE [PartDesign::FeatureBase] Clone004
  BaseFeature = -> Body007
  Suppressed = false
FEATURE [PartDesign::Body] Body045  label="LED-Base002"
  AllowCompound = false
  Group = -> [Clone004]
  Origin = -> Origin047
  Placement = pos=(-130,22,-12.7) rot=(0,0,1;0rad)
  Tip = -> Clone004
FEATURE [Sketcher::SketchObject] Sketch104
  AttachmentSupport = -> [YZ_Plane048]
  FullyConstrained = true
  MapMode = 5
  Placement = pos=(0,0,0) rot=(0.57735,0.57735,0.57735;2.0944rad)
  sketch-geometry (6):
    g0: LineSegment StartX=-1.9 StartY=2.2 StartZ=0 EndX=-1.9 EndY=3.43431 EndZ=0
    g1: LineSegment StartX=-1.9 StartY=3.43431 StartZ=0 EndX=-1.33431 EndY=4 EndZ=0
    g2: LineSegment StartX=-1.33431 StartY=4 StartZ=0 EndX=1.33431 EndY=4 EndZ=0
    g3: LineSegment StartX=1.33431 StartY=4 StartZ=0 EndX=1.9 EndY=3.43431 EndZ=0
    g4: LineSegment StartX=1.9 StartY=3.43431 StartZ=0 EndX=1.9 EndY=2.2 EndZ=0
    g5: LineSegment StartX=1.9 StartY=2.2 StartZ=0 EndX=-1.9 EndY=2.2 EndZ=0
  constraints (17):
    c: Coincident(g0,g1)
    c: Coincident(g1,g2)
    c: Horizontal(g2)
    c: Coincident(g2,g3)
    c: Coincident(g3,g4)
    c: Vertical(g4)
    c: Coincident(g4,g5)
    c: Coincident(g5,g0)
    c: Vertical(g0)
    c: Symmetric(g0,g4,g-2)
    c: DistanceX(g5,g5) = 3.8
    c: DistanceY(g4) = 2.2
    c: Angle(g1) = 0.785398
    c: Angle(g3) = -0.785398
    c: Equal(g0,g4)
    c: DistanceY(g2) = 4
    c: Distance(g3) = 0.8
FEATURE [PartDesign::Revolution] Revolution006
  Angle = 360
  Angle2 = 60
  Axis = (0,1,0)
  Base = (0,0,0)
  Placement = pos=(0,0,0) rot=(0.57735,0.57735,0.57735;2.0944rad)
  Profile = -> Sketch104
  ReferenceAxis = -> Sketch104 [H_Axis]
  Suppressed = false
  Type = 0
FEATURE [PartDesign::Body] Body046  label="RockerRoller"
  AllowCompound = false
  Group = -> [Sketch104,Revolution006]
  Origin = -> Origin048
  Placement = pos=(-131.5,12.5,-15.8) rot=(0,0,1;0rad)
  Tip = -> Revolution006
FEATURE [Sketcher::SketchObject] Sketch105
  AttachmentOffset = pos=(0,0,7.3) rot=(0,0,1;0rad)
  AttachmentSupport = -> [XZ_Plane046]
  FullyConstrained = true
  MapMode = 5
  Placement = pos=(0,-7.3,1.6e-15) rot=(1,0,0;1.5708rad)
  sketch-geometry (6):
    g0: LineSegment StartX=-90.6282 StartY=-1.8 StartZ=0 EndX=-92.3718 EndY=-1.8 EndZ=0
    g1: ArcOfCircle CenterX=-91.5 CenterY=0 CenterZ=0 NormalX=0 NormalY=0 NormalZ=1 AngleXU=0 Radius=2 StartAngle=5.16342 EndAngle=10.5445
    g2: LineSegment StartX=-96.5 StartY=5 StartZ=0 EndX=-96.5 EndY=-5 EndZ=0
    g3: LineSegment StartX=-96.5 StartY=-5 StartZ=0 EndX=-86.5 EndY=-5 EndZ=0
    g4: LineSegment StartX=-86.5 StartY=-5 StartZ=0 EndX=-86.5 EndY=5 EndZ=0
    g5: LineSegment StartX=-86.5 StartY=5 StartZ=0 EndX=-96.5 EndY=5 EndZ=0
  constraints (18):
    c: Horizontal(g0)
    c: Coincident(g1,g0)
    c: Diameter(g1) = 4
    c: DistanceY(g0) = -1.8
    c: PointOnObject(g1,g-1)
    c: DistanceX(g1) = -91.5
    c: Coincident(g1,g0)
    c: Coincident(g2,g3)
    c: Coincident(g3,g4)
    c: Coincident(g4,g5)
    c: Coincident(g5,g2)
    c: Vertical(g2)
    c: Vertical(g4)
    c: Horizontal(g3)
    c: Horizontal(g5)
    c: Symmetric(g2,g3,g1)
    c: Equal(g4,g5)
    c: DistanceX(g5,g5) = 10
FEATURE [PartDesign::Pocket] Pocket047  label="Fenders"
  BaseFeature = -> Pad043
  Direction = (0,1,-2e-16)
  Length = 5
  Length2 = 5
  Placement = pos=(0,0,0) rot=(0.57735,0.57735,0.57735;2.0944rad)
  Profile = -> Sketch105
  ReferenceAxis = -> Sketch105 [N_Axis]
  Refine = true
  Reversed = true
  Suppressed = false
  Type = 0
FEATURE [PartDesign::Mirrored] Mirrored002
  MirrorPlane = -> XZ_Plane046
  Placement = pos=(0,0,0) rot=(0.57735,0.57735,0.57735;2.0944rad)
  Suppressed = false
  TransformMode = 0
FEATURE [PartDesign::Mirrored] Mirrored003
  MirrorPlane = -> YZ_Plane046
  Placement = pos=(0,0,0) rot=(0.57735,0.57735,0.57735;2.0944rad)
  Suppressed = false
  TransformMode = 0
FEATURE [PartDesign::MultiTransform] MultiTransform002
  BaseFeature = -> Pocket047
  Originals = -> [Pocket047]
  Placement = pos=(0,0,0) rot=(0.57735,0.57735,0.57735;2.0944rad)
  Refine = true
  Suppressed = false
  TransformMode = 0
  Transformations = -> [Mirrored002,Mirrored003]
FEATURE [PartDesign::Pocket] Pocket048  label="TopFlat"
  BaseFeature = -> MultiTransform002
  Direction = (0,1,-2e-16)
  Length = 14.4
  Length2 = 5
  Midplane = true
  Placement = pos=(0,0,0) rot=(0.57735,0.57735,0.57735;2.0944rad)
  Profile = -> Sketch102
  ReferenceAxis = -> Sketch102 [N_Axis]
  Suppressed = false
  Type = 0
FEATURE [PartDesign::Body] Body044  label="BotLinkRocker"
  AllowCompound = false
  Group = -> [Sketch100,Pad041,Sketch101,Pad042,Sketch102,Sketch105,Sketch103,Pad043,Pocket047,MultiTransform002,Mirrored002,Mirrored003,Pocket048]
  Origin = -> Origin046
  Placement = pos=(-40,22,-15.8) rot=(0,0,1;0rad)
  Tip = -> Pocket048
FEATURE [PartDesign::FeaturePython] InvoluteGear007  label="m2.5-11T"  # WARN: FeaturePython — macro-defined, semantics opaque (R4)
  AttacherType = Attacher::AttachEngine3D
  Placement = pos=(0,0,0) rot=(1,0,0;1.5708rad)
  Suppressed = false
  angular_backlash = 0.416697
  backlash = 0.1
  beta = 0
  clearance = 0.25
  da = 32.5
  df = 21.25
  double_helix = false
  dw = 27.5
  head = 0
  head_fillet = 0
  height = 5
  module = 2.5
  numpoints = 6
  pressure_angle = 20
  properties_from_tool = false
  reversed_backlash = false
  root_fillet = 0
  shift = 0
  simple = false
  teeth = 11
  transverse_pitch = 7.85398
  undercut = false
  version = 0.0.4
  expr: angular_backlash = backlash / dw * 360 ° / pi
  expr: dw = teeth * module
FEATURE [Sketcher::SketchObject] Sketch106
  AttachmentSupport = -> [XZ_Plane049]
  FullyConstrained = true
  MapMode = 5
  Placement = pos=(0,0,0) rot=(1,0,0;1.5708rad)
  sketch-geometry (8):
    g0: ArcOfCircle CenterX=0 CenterY=0 CenterZ=0 NormalX=0 NormalY=0 NormalZ=1 AngleXU=0 Radius=4.5 StartAngle=0.339837 EndAngle=1.75456
    g1: ArcOfCircle CenterX=0 CenterY=0 CenterZ=0 NormalX=0 NormalY=0 NormalZ=1 AngleXU=0 Radius=8.5 StartAngle=0.1774 EndAngle=1.917
    g2: LineSegment StartX=8.3666 StartY=1.5 StartZ=0 EndX=4.24264 EndY=1.5 EndZ=0
    g3: LineSegment StartX=-0.822282 StartY=4.42423 StartZ=0 EndX=-2.88426 EndY=7.99569 EndZ=0
    g4: LineSegment StartX=0 StartY=0 StartZ=0 EndX=-4.1833 EndY=7.24569 EndZ=0
    g5: LineSegment StartX=-4.1833 StartY=7.24569 StartZ=0 EndX=-2.88426 EndY=7.99569 EndZ=0
    g6: LineSegment StartX=8.3666 StartY=1.5 StartZ=0 EndX=8.3666 EndY=0 EndZ=0
    g7: Circle CenterX=0 CenterY=0 CenterZ=0 NormalX=0 NormalY=0 NormalZ=1 AngleXU=0 Radius=2.5
  constraints (22):
    c: Coincident(g2,g1)
    c: Coincident(g2,g0)
    c: Coincident(g3,g0)
    c: Coincident(g3,g1)
    c: Coincident(g5,g4)
    c: Coincident(g5,g1)
    c: Parallel(g4,g3)
    c: Perpendicular(g4,g5)
    c: Angle(g-1,g4) = 2.0944
    c: Horizontal(g2)
    c: Coincident(g6,g1)
    c: PointOnObject(g6,g-1)
    c: Vertical(g6)
    c: Equal(g6,g5)
    c: Diameter(g0) = 9
    c: Diameter(g1) = 17
    c: DistanceY(g6,g6) = 1.5
    c: Diameter(g7) = 5
    c: Coincident(g0,g1)
    c: Coincident(g0,g7)
    c: Coincident(g0,g4)
    c: Coincident(g0,g-1)
FEATURE [Sketcher::SketchObject] Sketch107
  AttachmentSupport = -> [XZ_Plane050]
  FullyConstrained = true
  MapMode = 5
  Placement = pos=(0,0,0) rot=(1,0,0;1.5708rad)
  sketch-geometry (19):
    g0: ArcOfCircle CenterX=0 CenterY=0 CenterZ=0 NormalX=0 NormalY=0 NormalZ=1 AngleXU=0 Radius=5 StartAngle=0.699038 EndAngle=3.32416
    g1: ArcOfCircle CenterX=35.5 CenterY=7.5 CenterZ=0 NormalX=0 NormalY=0 NormalZ=1 AngleXU=0 Radius=27 StartAngle=3.84063 EndAngle=5.12642
    g2: ArcOfCircle CenterX=47.569 CenterY=-19.9652 CenterZ=0 NormalX=0 NormalY=0 NormalZ=1 AngleXU=0 Radius=3 StartAngle=0.313861 EndAngle=1.98482
    g3: ArcOfCircle CenterX=52.2 CenterY=-34.2325 CenterZ=0 NormalX=0 NormalY=0 NormalZ=1 AngleXU=0 Radius=3 StartAngle=4.98301 EndAngle=6.59705
    g4: LineSegment StartX=50.4225 StartY=-19.039 StartZ=0 EndX=55.0534 EndY=-33.3063 EndZ=0
    g5: ArcOfCircle CenterX=40.6222 CenterY=7.5 CenterZ=0 NormalX=0 NormalY=0 NormalZ=1 AngleXU=0 Radius=46.3087 StartAngle=3.32416 EndAngle=4.98301
    g6: Circle CenterX=0 CenterY=0 CenterZ=0 NormalX=0 NormalY=0 NormalZ=1 AngleXU=0 Radius=2.65
    g7: LineSegment StartX=35.5 StartY=7.5 StartZ=0 EndX=50.2059 EndY=-37.8062 EndZ=0
    g8: LineSegment StartX=55.0534 StartY=-33.3063 StartZ=0 EndX=49.3466 EndY=-35.1587 EndZ=0
    g9: LineSegment StartX=3.82731 StartY=3.21741 StartZ=0 EndX=14.8325 EndY=-9.874 EndZ=0
    g10: LineSegment StartX=10.2436 StartY=-23.3673 StartZ=0 EndX=15.1261 EndY=-14.1846 EndZ=0
    g11: ArcOfCircle CenterX=59.9551 CenterY=34.2547 CenterZ=0 NormalX=0 NormalY=0 NormalZ=1 AngleXU=0 Radius=66 StartAngle=3.79128 EndAngle=3.96568
    g12: ArcOfCircle CenterX=4.33525 CenterY=-8 CenterZ=0 NormalX=0 NormalY=0 NormalZ=1 AngleXU=0 Radius=3.85 StartAngle=0.649683 EndAngle=3.54528
    g13: ArcOfCircle CenterX=40.6222 CenterY=7.5 CenterZ=0 NormalX=0 NormalY=0 NormalZ=1 AngleXU=0 Radius=43.3087 StartAngle=3.54528 EndAngle=3.93497
    g14: ArcOfCircle CenterX=35.5 CenterY=7.5 CenterZ=0 NormalX=0 NormalY=0 NormalZ=1 AngleXU=0 Radius=30 StartAngle=4.32548 EndAngle=4.83229
    g15: LineSegment StartX=39.0883 StartY=-22.2846 StartZ=0 EndX=43.4481 EndY=-35.7164 EndZ=0
    g16: ArcOfCircle CenterX=40.6222 CenterY=7.5 CenterZ=0 NormalX=0 NormalY=0 NormalZ=1 AngleXU=0 Radius=43.3087 StartAngle=4.18965 EndAngle=4.77769
    g17: LineSegment StartX=39.0883 StartY=-22.2846 StartZ=0 EndX=44.5883 EndY=-20.4994 EndZ=0
    g18: LineSegment StartX=19 StartY=-30.025 StartZ=0 EndX=24.1802 EndY=-20.2824 EndZ=0
  constraints (53):
    c: Coincident(g0,g-1)
    c: Equal(g3,g2)
    c: Radius(g2) = 3
    c: Tangent(g4,g3) = 1.5708
    c: Tangent(g2,g4) = 1.5708
    c: Tangent(g2,g1) = 1.5708
    c: DistanceX(g1) = 35.5
    c: DistanceY(g1) = 7.5
    c: Radius(g1) = 27
    c: Distance(g3,g2) = 15
    c: Diameter(g0) = 10
    c: Coincident(g6,g0)
    c: Diameter(g6) = 5.3
    c: Coincident(g7,g1)
    c: PointOnObject(g7,g5)
    c: Parallel(g7,g4)
    c: Tangent(g5,g0) = -1.5708
    c: Tangent(g5,g3) = -1.5708
    c: Coincident(g3,g8)
    c: PointOnObject(g8,g7)
    c: Perpendicular(g8,g7)
    c: Distance(g8) = 6
    c: DistanceX(g3) = 52.2
    c: Tangent(g0,g9) = 1.5708
    c: Tangent(g9,g1) = -1.5708
    c: Horizontal(g5,g1)
    c: Tangent(g11,g12) = 1.5708
    c: Tangent(g12,g13) = -1.5708
    c: Coincident(g13,g10)
    c: Coincident(g15,g16)
    c: Coincident(g14,g15)
    c: Parallel(g15,g7)
    c: Coincident(g14,g17)
    c: PointOnObject(g17,g7)
    c: Perpendicular(g17,g7)
    c: DistanceX(g17,g17) = 5.5
    c: Coincident(g16,g5)
    c: Coincident(g14,g1)
    c: PointOnObject(g3,g16)
    c: PointOnObject(g2,g14)
    c: Coincident(g16,g18)
    c: Coincident(g18,g14)
    c: DistanceX(g16) = 19
    c: Angle(g18) = 1.0821
    c: Parallel(g18,g10)
    c: Equal(g13,g16)
    c: Coincident(g13,g5)
    c: Distance(g10,g16) = 11
    c: Coincident(g11,g10)
    c: Distance(g10) = 10.4
    c: Diameter(g12) = 7.7
    c: DistanceY(g12) = -8
    c: Radius(g11) = 66
FEATURE [PartDesign::Pad] Pad044  label="Contour"
  Direction = (0,-1,2e-16)
  Length = 12
  Length2 = 10
  Placement = pos=(0,0,0) rot=(1,0,0;1.5708rad)
  Profile = -> Sketch107
  ReferenceAxis = -> Sketch107 [N_Axis]
  Suppressed = false
  Type = 0
FEATURE [Sketcher::SketchObject] Sketch108
  AttachmentSupport = -> [XZ_Plane049]
  FullyConstrained = true
  MapMode = 5
  Placement = pos=(0,0,0) rot=(1,0,0;1.5708rad)
  sketch-geometry (1):
    g0: Circle CenterX=0 CenterY=0 CenterZ=0 NormalX=0 NormalY=0 NormalZ=1 AngleXU=0 Radius=3.5
  constraints (2):
    c: Coincident(g0,g-1)
    c: Diameter(g0) = 7
FEATURE [PartDesign::Pad] Pad045
  BaseFeature = -> InvoluteGear007
  Direction = (0,-1,2e-16)
  Length = 0.5
  Length2 = 10
  Placement = pos=(0,0,0) rot=(1,0,0;1.5708rad)
  Profile = -> Sketch108
  ReferenceAxis = -> Sketch108 [N_Axis]
  Reversed = true
  Suppressed = false
  Type = 0
FEATURE [PartDesign::Pocket] Pocket049  label="120deg-sector006"
  BaseFeature = -> Pad045
  Direction = (0,1,-2e-16)
  Length = 5
  Length2 = 5
  Midplane = true
  Placement = pos=(0,0,0) rot=(1,0,0;1.5708rad)
  Profile = -> Sketch106
  ReferenceAxis = -> Sketch106 [N_Axis]
  Refine = true
  Suppressed = false
  Type = 1
FEATURE [PartDesign::PolarPattern] PolarPattern006
  Angle = 360
  Axis = -> Sketch106 [N_Axis]
  BaseFeature = -> Pocket049
  Mode = 0
  Occurrences = 3
  Offset = 120
  Originals = -> [Pocket049]
  Placement = pos=(0,0,0) rot=(1,0,0;1.5708rad)
  Refine = true
  Suppressed = false
  TransformMode = 0
FEATURE [PartDesign::Body] Body047  label="M2.5-11T"
  AllowCompound = false
  Group = -> [InvoluteGear007,Sketch106,Sketch108,Pad045,Pocket049,PolarPattern006]
  Origin = -> Origin049
  Placement = pos=(-125.5,0.5,30) rot=(0,1,0;3.40339rad)
  Tip = -> PolarPattern006
FEATURE [Sketcher::SketchObject] Sketch109
  AttachmentOffset = pos=(0,0,8) rot=(0,0,1;0rad)
  AttachmentSupport = -> [XZ_Plane050]
  FullyConstrained = true
  MapMode = 5
  Placement = pos=(0,-8,1.8e-15) rot=(1,0,0;1.5708rad)
  sketch-geometry (1):
    g0: Circle CenterX=0 CenterY=0 CenterZ=0 NormalX=0 NormalY=0 NormalZ=1 AngleXU=0 Radius=19
  constraints (2):
    c: Coincident(g0,g-1)
    c: Diameter(g0) = 38
FEATURE [PartDesign::Pocket] Pocket050  label="T11Cut"
  BaseFeature = -> Pad044
  Direction = (0,1,-2e-16)
  Length = 5
  Length2 = 5
  Placement = pos=(0,0,0) rot=(1,0,0;1.5708rad)
  Profile = -> Sketch109
  ReferenceAxis = -> Sketch109 [N_Axis]
  Reversed = true
  Suppressed = false
  Type = 1
FEATURE [Sketcher::SketchObject] Sketch110
  AttachmentOffset = pos=(0,0,1) rot=(0,0,1;0rad)
  AttachmentSupport = -> [XZ_Plane050]
  FullyConstrained = true
  MapMode = 5
  Placement = pos=(0,-1,2e-16) rot=(1,0,0;1.5708rad)
  sketch-geometry (10):
    g0: LineSegment StartX=29.8639 StartY=7.5 StartZ=0 EndX=5.85268 EndY=-36.3573 EndZ=0
    g1: LineSegment StartX=5.85268 StartY=-36.3573 StartZ=0 EndX=10.063 EndY=-38.6624 EndZ=0
    g2: LineSegment StartX=10.063 StartY=-38.6624 StartZ=0 EndX=28.4816 EndY=-5.02003 EndZ=0
    g3: LineSegment StartX=28.4816 StartY=-5.02003 StartZ=0 EndX=36.6157 EndY=-5.02003 EndZ=0
    g4: LineSegment StartX=36.6157 StartY=-5.02003 StartZ=0 EndX=47.252 EndY=-41.8701 EndZ=0
    g5: LineSegment StartX=47.252 StartY=-41.8701 StartZ=0 EndX=51.8637 EndY=-40.539 EndZ=0
    g6: LineSegment StartX=51.8637 StartY=-40.539 StartZ=0 EndX=37.998 EndY=7.5 EndZ=0
    g7: LineSegment StartX=37.998 StartY=7.5 StartZ=0 EndX=29.8639 EndY=7.5 EndZ=0
    g8: LineSegment StartX=35.5 StartY=7.5 StartZ=0 EndX=49.5578 EndY=-41.2045 EndZ=0
    g9: LineSegment StartX=32.6 StartY=7.5 StartZ=0 EndX=7.95783 EndY=-37.5098 EndZ=0
  constraints (30):
    c: Coincident(g0,g1)
    c: Coincident(g1,g2)
    c: Coincident(g2,g3)
    c: Coincident(g3,g4)
    c: Coincident(g4,g5)
    c: Coincident(g5,g6)
    c: Coincident(g6,g7)
    c: Coincident(g7,g0)
    c: PointOnObject(g8,g5)
    c: DistanceX(g8) = 35.5
    c: DistanceY(g8) = 7.5
    c: Symmetric(g4,g5,g8)
    c: Perpendicular(g0,g1)
    c: Distance(g1) = 4.8
    c: Equal(g1,g5)
    c: Perpendicular(g6,g5)
    c: Parallel(g8,g4)
    c: Parallel(g3,g7)
    c: Parallel(g2,g0)
    c: Horizontal(g7)
    c: PointOnObject(g8,g7)
    c: Equal(g2,g4)
    c: Distance(g6) = 50
    c: Angle(g6) = 1.85179
    c: Equal(g3,g7)
    c: PointOnObject(g9,g7)
    c: Symmetric(g1,g0,g9)
    c: PointOnObject(g9,g1)
    c: DistanceX(g9,g8) = 2.9
    c: Angle(g-1,g9) = 1.06989
FEATURE [PartDesign::Pocket] Pocket051  label="ArmCutSnap"
  BaseFeature = -> Pocket050
  Direction = (0,1,-2e-16)
  Length = 5
  Length2 = 5
  Placement = pos=(0,0,0) rot=(1,0,0;1.5708rad)
  Profile = -> Sketch110
  ReferenceAxis = -> Sketch110 [N_Axis]
  Suppressed = false
  Type = 1
FEATURE [Sketcher::SketchObject] Sketch111
  AttachmentOffset = pos=(0,0,1) rot=(0,0,1;0rad)
  AttachmentSupport = -> [XZ_Plane050]
  FullyConstrained = true
  MapMode = 5
  Placement = pos=(0,-1,2e-16) rot=(1,0,0;1.5708rad)
  expr: Constraints[10] = Sketch110.Constraints[10]
  expr: Constraints[22] = Sketch110.Constraints[22]
  expr: Constraints[23] = Sketch110.Constraints[23]
  expr: Constraints[28] = Sketch110.Constraints[28]
  expr: Constraints[29] = Sketch110.Constraints[29]
  expr: Constraints[9] = Sketch110.Constraints[9]
  sketch-geometry (10):
    g0: LineSegment StartX=29.6358 StartY=7.5 StartZ=0 EndX=5.62467 EndY=-36.3573 EndZ=0
    g1: LineSegment StartX=5.62467 StartY=-36.3573 StartZ=0 EndX=10.1858 EndY=-38.8545 EndZ=0
    g2: LineSegment StartX=10.1858 StartY=-38.8545 StartZ=0 EndX=28.1384 EndY=-6.06337 EndZ=0
    g3: LineSegment StartX=28.1384 StartY=-6.06337 StartZ=0 EndX=36.7087 EndY=-6.06337 EndZ=0
    g4: LineSegment StartX=36.7087 StartY=-6.06337 StartZ=0 EndX=47.0758 EndY=-41.981 EndZ=0
    g5: LineSegment StartX=47.0758 StartY=-41.981 StartZ=0 EndX=52.0719 EndY=-40.539 EndZ=0
    g6: LineSegment StartX=52.0719 StartY=-40.539 StartZ=0 EndX=38.2061 EndY=7.5 EndZ=0
    g7: LineSegment StartX=38.2061 StartY=7.5 StartZ=0 EndX=29.6358 EndY=7.5 EndZ=0
    g8: LineSegment StartX=35.5 StartY=7.5 StartZ=0 EndX=49.5738 EndY=-41.26 EndZ=0
    g9: LineSegment StartX=32.6 StartY=7.5 StartZ=0 EndX=7.90525 EndY=-37.6059 EndZ=0
  constraints (30):
    c: Coincident(g0,g1)
    c: Coincident(g1,g2)
    c: Coincident(g2,g3)
    c: Coincident(g3,g4)
    c: Coincident(g4,g5)
    c: Coincident(g5,g6)
    c: Coincident(g6,g7)
    c: Coincident(g7,g0)
    c: PointOnObject(g8,g5)
    c: DistanceX(g8) = 35.5
    c: DistanceY(g8) = 7.5
    c: Symmetric(g4,g5,g8)
    c: Perpendicular(g0,g1)
    c: Distance(g1) = 5.2
    c: Equal(g1,g5)
    c: Perpendicular(g6,g5)
    c: Parallel(g8,g4)
    c: Parallel(g3,g7)
    c: Parallel(g2,g0)
    c: Horizontal(g7)
    c: PointOnObject(g8,g7)
    c: Equal(g2,g4)
    c: Distance(g6) = 50
    c: Angle(g6) = 1.85179
    c: Equal(g3,g7)
    c: PointOnObject(g9,g7)
    c: Symmetric(g1,g0,g9)
    c: PointOnObject(g9,g1)
    c: DistanceX(g9,g8) = 2.9
    c: Angle(g-1,g9) = 1.06989
FEATURE [PartDesign::Pocket] Pocket052  label="ArmCut"
  BaseFeature = -> Pocket051
  Direction = (0,1,-2e-16)
  Length = 6.2
  Length2 = 5
  Placement = pos=(0,0,0) rot=(1,0,0;1.5708rad)
  Profile = -> Sketch111
  ReferenceAxis = -> Sketch111 [N_Axis]
  Reversed = true
  Suppressed = false
  Type = 0
FEATURE [PartDesign::Body] Body048  label="RockerDrivePlate"
  AllowCompound = false
  Group = -> [Sketch107,Pad044,Sketch109,Pocket050,Sketch110,Pocket051,Sketch111,Pocket052]
  Origin = -> Origin050
  Placement = pos=(-125.5,9.5,30) rot=(0,0,1;0rad)
  Tip = -> Pocket052
FEATURE [Sketcher::SketchObject] Sketch112
  AttachmentSupport = -> [XZ_Plane051]
  FullyConstrained = true
  MapMode = 5
  Placement = pos=(0,0,0) rot=(1,0,0;1.5708rad)
  sketch-geometry (1):
    g0: Circle CenterX=0 CenterY=0 CenterZ=0 NormalX=0 NormalY=0 NormalZ=1 AngleXU=0 Radius=2.5
  constraints (2):
    c: Coincident(g0,g-1)
    c: Diameter(g0) = 5
FEATURE [PartDesign::Pad] Pad046
  Direction = (0,-1,2e-16)
  Length = 15
  Length2 = 10
  Placement = pos=(0,0,0) rot=(1,0,0;1.5708rad)
  Profile = -> Sketch112
  ReferenceAxis = -> Sketch112 [N_Axis]
  Refine = true
  Suppressed = false
  Type = 0
FEATURE [Sketcher::SketchObject] Sketch113
  AttachmentSupport = -> [XZ_Plane051]
  FullyConstrained = true
  MapMode = 5
  Placement = pos=(0,0,0) rot=(1,0,0;1.5708rad)
  sketch-geometry (1):
    g0: Circle CenterX=0 CenterY=0 CenterZ=0 NormalX=0 NormalY=0 NormalZ=1 AngleXU=0 Radius=5
  constraints (2):
    c: Coincident(g0,g-1)
    c: Diameter(g0) = 10
FEATURE [PartDesign::Pad] Pad047
  BaseFeature = -> Pad046
  Direction = (0,-1,2e-16)
  Length = 0.5
  Length2 = 10
  Placement = pos=(0,0,0) rot=(1,0,0;1.5708rad)
  Profile = -> Sketch113
  ReferenceAxis = -> Sketch113 [N_Axis]
  Refine = true
  Suppressed = false
  Type = 0
FEATURE [Sketcher::SketchObject] Sketch114
  AttachmentSupport = -> [XZ_Plane051]
  FullyConstrained = true
  MapMode = 5
  Placement = pos=(0,0,0) rot=(1,0,0;1.5708rad)
  sketch-geometry (4):
    g0: ArcOfCircle CenterX=0 CenterY=0 CenterZ=0 NormalX=0 NormalY=0 NormalZ=1 AngleXU=0 Radius=5.5 StartAngle=1.5708 EndAngle=4.71239
    g1: ArcOfCircle CenterX=24 CenterY=0 CenterZ=0 NormalX=0 NormalY=0 NormalZ=1 AngleXU=0 Radius=5.5 StartAngle=4.71239 EndAngle=7.85398
    g2: LineSegment StartX=2.02815e-08 StartY=-5.5 StartZ=0 EndX=24 EndY=-5.5 EndZ=0
    g3: LineSegment StartX=24 StartY=5.5 StartZ=0 EndX=0 EndY=5.5 EndZ=0
  constraints (11):
    c: Coincident(g0,g-1)
    c: PointOnObject(g0,g-2)
    c: PointOnObject(g1,g-1)
    c: Coincident(g0,g2)
    c: Horizontal(g2)
    c: Coincident(g3,g0)
    c: Horizontal(g3)
    c: Tangent(g1,g3) = -1.5708
    c: Diameter(g0) = 11
    c: DistanceX(g1) = 24
    c: Tangent(g2,g1) = -1.5708
FEATURE [PartDesign::Pad] Pad048
  BaseFeature = -> Pad047
  Direction = (0,-1,2e-16)
  Length = 2.5
  Length2 = 10
  Placement = pos=(0,0,0) rot=(1,0,0;1.5708rad)
  Profile = -> Sketch114
  ReferenceAxis = -> Sketch114 [N_Axis]
  Reversed = true
  Suppressed = false
  Type = 0
FEATURE [Sketcher::SketchObject] Sketch115
  AttachmentSupport = -> [XZ_Plane051]
  FullyConstrained = true
  MapMode = 5
  Placement = pos=(0,0,0) rot=(1,0,0;1.5708rad)
  sketch-geometry (1):
    g0: Circle CenterX=24 CenterY=0 CenterZ=0 NormalX=0 NormalY=0 NormalZ=1 AngleXU=0 Radius=5.5
  constraints (3):
    c: PointOnObject(g0,g-1)
    c: Diameter(g0) = 11
    c: DistanceX(g0) = 24
FEATURE [PartDesign::Pad] Pad049
  BaseFeature = -> Pad048
  Direction = (0,-1,2e-16)
  Length = 3
  Length2 = 10
  Placement = pos=(0,0,0) rot=(1,0,0;1.5708rad)
  Profile = -> Sketch115
  ReferenceAxis = -> Sketch115 [N_Axis]
  Reversed = true
  Suppressed = false
  Type = 0
FEATURE [Sketcher::SketchObject] Sketch116
  AttachmentSupport = -> [XZ_Plane051]
  FullyConstrained = true
  MapMode = 5
  Placement = pos=(0,0,0) rot=(1,0,0;1.5708rad)
  sketch-geometry (1):
    g0: Circle CenterX=24 CenterY=0 CenterZ=0 NormalX=0 NormalY=0 NormalZ=1 AngleXU=0 Radius=2.5
  constraints (3):
    c: PointOnObject(g0,g-1)
    c: Diameter(g0) = 5
    c: DistanceX(g0) = 24
FEATURE [PartDesign::Pad] Pad050
  BaseFeature = -> Pad049
  Direction = (0,-1,2e-16)
  Length = 9
  Length2 = 10
  Placement = pos=(0,0,0) rot=(1,0,0;1.5708rad)
  Profile = -> Sketch116
  ReferenceAxis = -> Sketch116 [N_Axis]
  Reversed = true
  Suppressed = false
  Type = 0
FEATURE [PartDesign::Body] Body049  label="RockerCrank"
  AllowCompound = false
  Group = -> [Sketch112,Pad046,Sketch113,Pad047,Sketch114,Pad048,Sketch115,Pad049,Sketch116,Pad050]
  Origin = -> Origin051
  Placement = pos=(-125.5,10.5,30) rot=(0,-1,0;1.5708rad)
  Tip = -> Pad050
FEATURE [Sketcher::SketchObject] Sketch117
  AttachmentSupport = -> [XZ_Plane052]
  FullyConstrained = true
  MapMode = 5
  Placement = pos=(0,0,0) rot=(1,0,0;1.5708rad)
  sketch-geometry (21):
    g0: ArcOfCircle CenterX=-12 CenterY=0 CenterZ=0 NormalX=0 NormalY=0 NormalZ=1 AngleXU=0 Radius=2.7 StartAngle=1.5708 EndAngle=4.71239
    g1: ArcOfCircle CenterX=12 CenterY=0 CenterZ=0 NormalX=0 NormalY=0 NormalZ=1 AngleXU=0 Radius=2.7 StartAngle=4.71239 EndAngle=7.85398
    g2: LineSegment StartX=-12 StartY=2.7 StartZ=0 EndX=12 EndY=2.7 EndZ=0
    g3: LineSegment StartX=-12 StartY=-2.7 StartZ=0 EndX=12 EndY=-2.7 EndZ=0
    g4: ArcOfCircle CenterX=-12 CenterY=0 CenterZ=0 NormalX=0 NormalY=0 NormalZ=1 AngleXU=0 Radius=5.5 StartAngle=1.5708 EndAngle=4.71239
    g5: LineSegment StartX=-12 StartY=5.5 StartZ=0 EndX=12 EndY=5.5 EndZ=0
    g6: LineSegment StartX=-12 StartY=-5.5 StartZ=0 EndX=12 EndY=-5.5 EndZ=0
    g7: ArcOfCircle CenterX=12 CenterY=0 CenterZ=0 NormalX=0 NormalY=0 NormalZ=1 AngleXU=0 Radius=5.5 StartAngle=4.71239 EndAngle=5.72065
    g8: ArcOfCircle CenterX=12 CenterY=0 CenterZ=0 NormalX=0 NormalY=0 NormalZ=1 AngleXU=0 Radius=5.5 StartAngle=0.562536 EndAngle=1.5708
    g9: LineSegment StartX=18.3443 StartY=2 StartZ=0 EndX=121.5 EndY=2 EndZ=0
    g10: LineSegment StartX=121.5 StartY=-2 StartZ=0 EndX=18.3443 EndY=-2 EndZ=0
    g11: ArcOfCircle CenterX=18.3443 CenterY=4 CenterZ=0 NormalX=0 NormalY=0 NormalZ=1 AngleXU=0 Radius=2 StartAngle=3.70413 EndAngle=4.71239
    g12: ArcOfCircle CenterX=18.3443 CenterY=-4 CenterZ=0 NormalX=0 NormalY=0 NormalZ=1 AngleXU=0 Radius=2 StartAngle=1.5708 EndAngle=2.57906
    g13: Circle CenterX=125.5 CenterY=-45.4 CenterZ=0 NormalX=0 NormalY=0 NormalZ=1 AngleXU=0 Radius=2.7
    g14: ArcOfCircle CenterX=125.5 CenterY=-45.4 CenterZ=0 NormalX=0 NormalY=0 NormalZ=1 AngleXU=0 Radius=5.5 StartAngle=2.25438 EndAngle=7.17039
    g15: ArcOfCircle CenterX=119.5 CenterY=-38.0345 CenterZ=0 NormalX=0 NormalY=0 NormalZ=1 AngleXU=0 Radius=4 StartAngle=5.39598 EndAngle=6.28319
    g16: ArcOfCircle CenterX=131.5 CenterY=-38.0345 CenterZ=0 NormalX=0 NormalY=0 NormalZ=1 AngleXU=0 Radius=4 StartAngle=3.14159 EndAngle=4.0288
    g17: ArcOfCircle CenterX=121.5 CenterY=-4 CenterZ=0 NormalX=0 NormalY=0 NormalZ=1 AngleXU=0 Radius=2 StartAngle=0 EndAngle=1.5708
    g18: ArcOfCircle CenterX=121.5 CenterY=-4 CenterZ=0 NormalX=0 NormalY=0 NormalZ=1 AngleXU=0 Radius=6 StartAngle=1e-16 EndAngle=1.5708
    g19: LineSegment StartX=123.5 StartY=-4 StartZ=0 EndX=123.5 EndY=-38.0345 EndZ=0
    g20: LineSegment StartX=127.5 StartY=-4 StartZ=0 EndX=127.5 EndY=-38.0345 EndZ=0
  constraints (49):
    c: Tangent(g0,g2) = 1.5708
    c: Tangent(g0,g3) = -1.5708
    c: Tangent(g1,g2) = 1.5708
    c: Tangent(g1,g3) = -1.5708
    c: Equal(g0,g1)
    c: PointOnObject(g0,g-1)
    c: Symmetric(g0,g1,g-2)
    c: DistanceX(g3,g3) = 24
    c: Diameter(g1) = 5.4
    c: Tangent(g4,g5) = 1.5708
    c: Tangent(g4,g6) = -1.5708
    c: Tangent(g8,g5) = 1.5708
    c: Tangent(g7,g6) = -1.5708
    c: Horizontal(g6)
    c: Coincident(g7,g1)
    c: Coincident(g8,g1)
    c: Diameter(g4) = 11
    c: Horizontal(g9)
    c: Horizontal(g10)
    c: Radius(g11) = 2
    c: Tangent(g11,g9) = -1.5708
    c: Tangent(g11,g8) = 1.5708
    c: Tangent(g12,g10) = -1.5708
    c: Tangent(g12,g7) = 1.5708
    c: Equal(g12,g11)
    c: Symmetric(g10,g9,g-1)
    c: DistanceY(g10,g9) = 4
    c: Coincident(g4,g0)
    c: Diameter(g13) = 5.4
    c: DistanceY(g13) = -45.4
    c: DistanceX(g13) = 125.5
    c: Coincident(g14,g13)
    c: Diameter(g14) = 11
    c: Equal(g16,g15)
    c: Tangent(g15,g14) = 1.5708
    c: Tangent(g16,g14) = 1.5708
    c: Horizontal(g15,g15)
    c: Horizontal(g15,g16)
    c: Horizontal(g16,g16)
    c: Coincident(g18,g17)
    c: Tangent(g17,g10) = -1.5708
    c: Tangent(g18,g9) = 1.5708
    c: Radius(g17) = 2
    c: Tangent(g17,g19) = 1.5708
    c: Tangent(g18,g20) = 1.5708
    c: Tangent(g20,g16) = -1.5708
    c: Tangent(g15,g19) = 1.5708
    c: DistanceX(g15,g16) = 4
    c: Radius(g15) = 4
FEATURE [PartDesign::Pad] Pad051
  Direction = (0,-1,2e-16)
  Length = 2.5
  Length2 = 10
  Placement = pos=(0,0,0) rot=(1,0,0;1.5708rad)
  Profile = -> Sketch117
  ReferenceAxis = -> Sketch117 [N_Axis]
  Suppressed = false
  Type = 0
FEATURE [PartDesign::Body] Body050  label="ElasticRockerLink"
  AllowCompound = false
  Group = -> [Sketch117,Pad051]
  Origin = -> Origin052
  Placement = pos=(-125.5,14,30) rot=(0,0,1;0rad)
  Tip = -> Pad051
FEATURE [Sketcher::SketchObject] Sketch118
  AttachmentSupport = -> [XZ_Plane053]
  FullyConstrained = true
  MapMode = 5
  Placement = pos=(0,0,0) rot=(1,0,0;1.5708rad)
  sketch-geometry (2):
    g0: Circle CenterX=0 CenterY=0 CenterZ=0 NormalX=0 NormalY=0 NormalZ=1 AngleXU=0 Radius=2.4
    g1: Circle CenterX=0 CenterY=0 CenterZ=0 NormalX=0 NormalY=0 NormalZ=1 AngleXU=0 Radius=5.5
  constraints (4):
    c: Coincident(g0,g-1)
    c: Coincident(g1,g0)
    c: Diameter(g1) = 11
    c: Diameter(g0) = 4.8
FEATURE [PartDesign::Pad] Pad052
  Direction = (0,-1,2e-16)
  Length = 1
  Length2 = 10
  Placement = pos=(0,0,0) rot=(1,0,0;1.5708rad)
  Profile = -> Sketch118
  ReferenceAxis = -> Sketch118 [N_Axis]
  Suppressed = false
  Type = 0
FEATURE [PartDesign::Body] Body051  label="LockRing5mm"
  AllowCompound = false
  Group = -> [Sketch118,Pad052]
  Origin = -> Origin053
  Placement = pos=(-125.5,17.5,56) rot=(0,0,1;0rad)
  Tip = -> Pad052
FEATURE [Sketcher::SketchObject] Sketch119
  AttachmentSupport = -> [XY_Plane054]
  FullyConstrained = true
  MapMode = 5
  sketch-geometry (47):
    g0: LineSegment StartX=-198 StartY=30.5 StartZ=0 EndX=-198 EndY=-74.5 EndZ=0
    g1: LineSegment StartX=-193 StartY=-79.5 StartZ=0 EndX=193 EndY=-79.5 EndZ=0
    g2: LineSegment StartX=198 StartY=-74.5 StartZ=0 EndX=198 EndY=30.5 EndZ=0
    g3: LineSegment StartX=193 StartY=35.5 StartZ=0 EndX=-193 EndY=35.5 EndZ=0
    g4: LineSegment StartX=-90 StartY=23 StartZ=0 EndX=-90 EndY=21 EndZ=0
    g5: LineSegment StartX=-90 StartY=21 StartZ=0 EndX=90 EndY=21 EndZ=0
    g6: LineSegment StartX=90 StartY=21 StartZ=0 EndX=90 EndY=23 EndZ=0
    g7: LineSegment StartX=90 StartY=23 StartZ=0 EndX=-90 EndY=23 EndZ=0
    g8: LineSegment StartX=-152.5 StartY=24 StartZ=0 EndX=-152.5 EndY=20 EndZ=0
    g9: LineSegment StartX=-152.5 StartY=20 StartZ=0 EndX=152.5 EndY=20 EndZ=0
    g10: LineSegment StartX=152.5 StartY=20 StartZ=0 EndX=152.5 EndY=24 EndZ=0
    g11: LineSegment StartX=152.5 StartY=24 StartZ=0 EndX=-152.5 EndY=24 EndZ=0
    g12: LineSegment StartX=0 StartY=24 StartZ=0 EndX=0 EndY=20 EndZ=0
    g13: LineSegment StartX=-90 StartY=-17 StartZ=0 EndX=-90 EndY=-19 EndZ=0
    g14: LineSegment StartX=-90 StartY=-19 StartZ=0 EndX=90 EndY=-19 EndZ=0
    g15: LineSegment StartX=90 StartY=-19 StartZ=0 EndX=90 EndY=-17 EndZ=0
    g16: LineSegment StartX=90 StartY=-17 StartZ=0 EndX=-90 EndY=-17 EndZ=0
    g17: LineSegment StartX=-152.5 StartY=-16 StartZ=0 EndX=-152.5 EndY=-20 EndZ=0
    g18: LineSegment StartX=-152.5 StartY=-20 StartZ=0 EndX=152.5 EndY=-20 EndZ=0
    g19: LineSegment StartX=152.5 StartY=-20 StartZ=0 EndX=152.5 EndY=-16 EndZ=0
    g20: LineSegment StartX=152.5 StartY=-16 StartZ=0 EndX=-152.5 EndY=-16 EndZ=0
    g21: LineSegment StartX=0 StartY=-16 StartZ=0 EndX=0 EndY=-20 EndZ=0
    g22: LineSegment StartX=-90 StartY=-58 StartZ=0 EndX=-90 EndY=-60 EndZ=0
    g23: LineSegment StartX=-90 StartY=-60 StartZ=0 EndX=90 EndY=-60 EndZ=0
    g24: LineSegment StartX=90 StartY=-60 StartZ=0 EndX=90 EndY=-58 EndZ=0
    g25: LineSegment StartX=90 StartY=-58 StartZ=0 EndX=-90 EndY=-58 EndZ=0
    g26: LineSegment StartX=-137.5 StartY=-57 StartZ=0 EndX=-137.5 EndY=-61 EndZ=0
    g27: LineSegment StartX=-137.5 StartY=-61 StartZ=0 EndX=137.5 EndY=-61 EndZ=0
    g28: LineSegment StartX=137.5 StartY=-61 StartZ=0 EndX=137.5 EndY=-57 EndZ=0
    g29: LineSegment StartX=137.5 StartY=-57 StartZ=0 EndX=-137.5 EndY=-57 EndZ=0
    g30: LineSegment StartX=0 StartY=-57 StartZ=0 EndX=0 EndY=-61 EndZ=0
    g31: ArcOfCircle CenterX=193 CenterY=-74.5 CenterZ=0 NormalX=0 NormalY=0 NormalZ=1 AngleXU=0 Radius=5 StartAngle=4.71239 EndAngle=6.28319
    g32: GeomPoint X=198 Y=-79.5 Z=0
    g33: ArcOfCircle CenterX=-193 CenterY=30.5 CenterZ=0 NormalX=0 NormalY=0 NormalZ=1 AngleXU=0 Radius=5 StartAngle=1.5708 EndAngle=3.14159
    g34: GeomPoint X=-198 Y=35.5 Z=0
    g35: ArcOfCircle CenterX=-193 CenterY=-74.5 CenterZ=0 NormalX=0 NormalY=0 NormalZ=1 AngleXU=0 Radius=5 StartAngle=3.14159 EndAngle=4.71239
    g36: GeomPoint X=-198 Y=-79.5 Z=0
    g37: ArcOfCircle CenterX=193 CenterY=30.5 CenterZ=0 NormalX=0 NormalY=0 NormalZ=1 AngleXU=0 Radius=5 StartAngle=0 EndAngle=1.5708
    g38: GeomPoint X=198 Y=35.5 Z=0
    g39: LineSegment StartX=-194 StartY=17 StartZ=0 EndX=-194 EndY=14 EndZ=0
    g40: LineSegment StartX=-194 StartY=14 StartZ=0 EndX=-192 EndY=14 EndZ=0
    g41: LineSegment StartX=-192 StartY=14 StartZ=0 EndX=-192 EndY=17 EndZ=0
    g42: LineSegment StartX=-192 StartY=17 StartZ=0 EndX=-194 EndY=17 EndZ=0
    g43: LineSegment StartX=192 StartY=17 StartZ=0 EndX=192 EndY=14 EndZ=0
    g44: LineSegment StartX=192 StartY=14 StartZ=0 EndX=194 EndY=14 EndZ=0
    g45: LineSegment StartX=194 StartY=14 StartZ=0 EndX=194 EndY=17 EndZ=0
    g46: LineSegment StartX=194 StartY=17 StartZ=0 EndX=192 EndY=17 EndZ=0
  constraints (129):
    c: Vertical(g0)
    c: Vertical(g2)
    c: Horizontal(g1)
    c: DistanceY(g36,g34) = 115
    c: DistanceY(g38) = 35.5
    c: DistanceX(g36,g32) = 396
    c: Coincident(g4,g5)
    c: Coincident(g5,g6)
    c: Coincident(g6,g7)
    c: Coincident(g7,g4)
    c: Vertical(g4)
    c: Vertical(g6)
    c: Horizontal(g7)
    c: DistanceX(g5,g5) = 180
    c: DistanceY(g6,g6) = 2
    c: DistanceX(g5) = 90
    c: DistanceY(g5) = 21
    c: Coincident(g8,g9)
    c: Coincident(g9,g10)
    c: Coincident(g10,g11)
    c: Coincident(g11,g8)
    c: Vertical(g8)
    c: Vertical(g10)
    c: Horizontal(g11)
    c: DistanceY(g10,g10) = 4
    c: DistanceY(g9) = 20
    c: PointOnObject(g12,g11)
    c: PointOnObject(g12,g9)
    c: Symmetric(g4,g5,g12)
    c: Symmetric(g9,g8,g12)
    c: DistanceX(g11,g11) = 305
    c: Symmetric(g34,g38,g-2)
    c: Horizontal(g9)
    c: Coincident(g13,g14)
    c: Coincident(g22,g23)
    c: Coincident(g14,g15)
    c: Coincident(g23,g24)
    c: Coincident(g15,g16)
    c: Coincident(g24,g25)
    c: Coincident(g16,g13)
    c: Coincident(g25,g22)
    c: Vertical(g13)
    c: Vertical(g22)
    c: Vertical(g15)
    c: Vertical(g24)
    c: Horizontal(g16)
    c: Horizontal(g25)
    c: Equal(g5,g14)
    c: Equal(g5,g23)
    c: Equal(g6,g15)
    c: Equal(g6,g24)
    c: Coincident(g17,g18)
    c: Coincident(g26,g27)
    c: Coincident(g18,g19)
    c: Coincident(g27,g28)
    c: Coincident(g19,g20)
    c: Coincident(g28,g29)
    c: Coincident(g20,g17)
    c: Coincident(g29,g26)
    c: Vertical(g17)
    c: Vertical(g26)
    c: Vertical(g19)
    c: Vertical(g28)
    c: Horizontal(g20)
    c: Horizontal(g29)
    c: Equal(g10,g19)
    c: Equal(g10,g28)
    c: PointOnObject(g21,g20)
    c: PointOnObject(g30,g29)
    c: PointOnObject(g21,g18)
    c: PointOnObject(g30,g27)
    c: Symmetric(g13,g14,g21)
    c: Symmetric(g22,g23,g30)
    c: Symmetric(g18,g17,g21)
    c: Symmetric(g27,g26,g30)
    c: Horizontal(g18)
    c: Horizontal(g27)
    c: DistanceY(g18,g14) = 1
    c: DistanceY(g15) = -17
    c: DistanceY(g27,g23) = 1
    c: DistanceY(g28) = -57
    c: PointOnObject(g30,g-2)
    c: PointOnObject(g21,g-2)
    c: DistanceX(g29,g29) = 275
    c: DistanceX(g20,g20) = 305
    c: PointOnObject(g32,g1)
    c: PointOnObject(g32,g2)
    c: Tangent(g1,g31) = -1.5708
    c: Tangent(g2,g31) = -1.5708
    c: PointOnObject(g34,g0)
    c: PointOnObject(g34,g3)
    c: Tangent(g0,g33) = -1.5708
    c: Tangent(g3,g33) = -1.5708
    c: PointOnObject(g36,g0)
    c: PointOnObject(g36,g1)
    c: Tangent(g0,g35) = -1.5708
    c: Tangent(g1,g35) = -1.5708
    c: PointOnObject(g38,g2)
    c: PointOnObject(g38,g3)
    c: Tangent(g2,g37) = -1.5708
    c: Tangent(g3,g37) = -1.5708
    c: Equal(g37,g31)
    c: Equal(g31,g35)
    c: Equal(g35,g33)
    c: Radius(g33) = 5
    c: Coincident(g39,g40)
    c: Coincident(g40,g41)
    c: Coincident(g41,g42)
    c: Coincident(g42,g39)
    c: Vertical(g39)
    c: Vertical(g41)
    c: Horizontal(g40)
    c: Horizontal(g42)
    c: Distance(g39,g41) = 2
    c: Distance(g40,g42) = 3
    c: DistanceY(g40) = 14
    c: DistanceX(g0,g39) = 4
    c: Coincident(g43,g44)
    c: Coincident(g44,g45)
    c: Coincident(g45,g46)
    c: Coincident(g46,g43)
    c: Vertical(g43)
    c: Vertical(g45)
    c: Horizontal(g44)
    c: Horizontal(g46)
    c: Distance(g43,g45) = 2
    c: Distance(g44,g46) = 3
    c: DistanceX(g45,g2) = 4
    c: DistanceY(g43) = 14
FEATURE [PartDesign::Pad] Pad053
  Direction = (0,0,1)
  Length = 2
  Length2 = 10
  Profile = -> Sketch119
  ReferenceAxis = -> Sketch119 [N_Axis]
  Suppressed = false
  Type = 0
FEATURE [PartDesign::Body] Body052  label="Erdboden"
  AllowCompound = false
  Group = -> [Sketch119,Pad053]
  Origin = -> Origin054
  Placement = pos=(0,0,106) rot=(0,0,1;0rad)
  Tip = -> Pad053
FEATURE [Image::ImagePlane] Turm
  Placement = pos=(-1,0,-197) rot=(1,0,0;1.5708rad)
  XSize = 268
  YSize = 495
FEATURE [App::Part] Part  label="Bild3"
  Group = -> [Turm]
  Origin = -> Origin055
  Placement = pos=(-40,22,435) rot=(0,1,0;-0.038397rad)
FEATURE [Sketcher::SketchObject] Sketch120
  AttachmentSupport = -> [XZ_Plane056]
  FullyConstrained = true
  MapMode = 5
  Placement = pos=(0,0,0) rot=(1,0,0;1.5708rad)
  sketch-geometry (8):
    g0: LineSegment StartX=1.2 StartY=29 StartZ=0 EndX=5.5 EndY=29 EndZ=0
    g1: LineSegment StartX=5.5 StartY=29 StartZ=0 EndX=5.5 EndY=25 EndZ=0
    g2: LineSegment StartX=5.5 StartY=25 StartZ=0 EndX=2.2 EndY=25 EndZ=0
    g3: LineSegment StartX=2.2 StartY=25 StartZ=0 EndX=2.2 EndY=19 EndZ=0
    g4: LineSegment StartX=2.2 StartY=19 StartZ=0 EndX=6 EndY=19 EndZ=0
    g5: LineSegment StartX=6 StartY=19 StartZ=0 EndX=6 EndY=-5 EndZ=0
    g6: LineSegment StartX=6 StartY=-5 StartZ=0 EndX=1.2 EndY=-5 EndZ=0
    g7: LineSegment StartX=1.2 StartY=-5 StartZ=0 EndX=1.2 EndY=29 EndZ=0
  constraints (24):
    c: Horizontal(g0)
    c: Coincident(g0,g1)
    c: Coincident(g1,g2)
    c: Horizontal(g2)
    c: Coincident(g2,g3)
    c: Vertical(g3)
    c: Coincident(g3,g4)
    c: Horizontal(g4)
    c: Coincident(g4,g5)
    c: Vertical(g5)
    c: Coincident(g5,g6)
    c: Coincident(g6,g7)
    c: Coincident(g7,g0)
    c: Horizontal(g6)
    c: DistanceX(g0) = 1.2
    c: Vertical(g7)
    c: DistanceY(g6) = -5
    c: DistanceY(g7,g7) = 34
    c: DistanceX(g0) = 5.5
    c: DistanceX(g2) = 2.2
    c: Vertical(g1)
    c: DistanceY(g1,g1) = 4
    c: DistanceX(g5) = 6
    c: DistanceY(g3,g3) = 6
FEATURE [PartDesign::Revolution] Revolution007
  Angle = 360
  Angle2 = 60
  Axis = (0,2e-16,1)
  Base = (0,0,0)
  Placement = pos=(0,0,0) rot=(1,0,0;1.5708rad)
  Profile = -> Sketch120
  ReferenceAxis = -> Sketch120 [V_Axis]
  Refine = true
  Reversed = true
  Suppressed = false
  Type = 0
FEATURE [Sketcher::SketchObject] Sketch121
  AttachmentSupport = -> [XZ_Plane056]
  FullyConstrained = true
  MapMode = 5
  Placement = pos=(0,0,0) rot=(1,0,0;1.5708rad)
  sketch-geometry (12):
    g0: LineSegment StartX=3 StartY=-5 StartZ=0 EndX=9.9 EndY=-5 EndZ=0
    g1: ArcOfCircle CenterX=9.9 CenterY=-2.9 CenterZ=0 NormalX=0 NormalY=0 NormalZ=1 AngleXU=0 Radius=2.1 StartAngle=4.71239 EndAngle=6.28319
    g2: LineSegment StartX=12 StartY=-2.9 StartZ=0 EndX=12 EndY=5.5 EndZ=0
    g3: LineSegment StartX=11.5 StartY=6 StartZ=0 EndX=10.5 EndY=6 EndZ=0
    g4: LineSegment StartX=10 StartY=5.5 StartZ=0 EndX=10 EndY=2.1 EndZ=0
    g5: ArcOfCircle CenterX=7.9 CenterY=2.1 CenterZ=0 NormalX=0 NormalY=0 NormalZ=1 AngleXU=0 Radius=2.1 StartAngle=3.14159 EndAngle=6.28319
    g6: LineSegment StartX=5.8 StartY=2.1 StartZ=0 EndX=3 EndY=2.1 EndZ=0
    g7: LineSegment StartX=3 StartY=2.1 StartZ=0 EndX=3 EndY=-5 EndZ=0
    g8: ArcOfCircle CenterX=10.5 CenterY=5.5 CenterZ=0 NormalX=0 NormalY=0 NormalZ=1 AngleXU=0 Radius=0.5 StartAngle=1.5708 EndAngle=3.14159
    g9: GeomPoint X=10 Y=6 Z=0
    g10: ArcOfCircle CenterX=11.5 CenterY=5.5 CenterZ=0 NormalX=0 NormalY=0 NormalZ=1 AngleXU=0 Radius=0.5 StartAngle=0 EndAngle=1.5708
    g11: GeomPoint X=12 Y=6 Z=0
  constraints (31):
    c: Horizontal(g0)
    c: Tangent(g0,g1) = -1.5708
    c: Tangent(g1,g2) = -1.5708
    c: Horizontal(g3)
    c: Vertical(g4)
    c: Tangent(g4,g5) = 1.5708
    c: Coincident(g5,g6)
    c: Horizontal(g6)
    c: Coincident(g6,g7)
    c: Coincident(g7,g0)
    c: Vertical(g7)
    c: DistanceX(g0) = 3
    c: DistanceY(g0) = -5
    c: Diameter(g5) = 4.2
    c: Tangent(g5,g-1)
    c: DistanceX(g1) = 12
    c: Vertical(g2)
    c: Horizontal(g5,g5)
    c: Equal(g5,g1)
    c: DistanceY(g0,g11) = 11
    c: PointOnObject(g9,g3)
    c: PointOnObject(g9,g4)
    c: Tangent(g3,g8) = -1.5708
    c: Tangent(g4,g8) = -1.5708
    c: PointOnObject(g11,g2)
    c: PointOnObject(g11,g3)
    c: Tangent(g2,g10) = -1.5708
    c: Tangent(g3,g10) = -1.5708
    c: Equal(g10,g8)
    c: Radius(g8) = 0.5
    c: DistanceX(g4) = 10
FEATURE [PartDesign::Pad] Pad054
  BaseFeature = -> Revolution007
  Direction = (0,-1,2e-16)
  Length = 3
  Length2 = 10
  Midplane = true
  Placement = pos=(0,0,0) rot=(1,0,0;1.5708rad)
  Profile = -> Sketch121
  ReferenceAxis = -> Sketch121 [N_Axis]
  Refine = true
  Suppressed = false
  Type = 0
FEATURE [PartDesign::Fillet] Fillet
  Base = -> Pad054 [Edge29,Edge22,Face1,Edge5]
  BaseFeature = -> Pad054
  Placement = pos=(0,0,0) rot=(1,0,0;1.5708rad)
  Radius = 0.9
  SupportTransform = false
  Suppressed = false
  UseAllEdges = false
FEATURE [PartDesign::Fillet] Fillet001
  Base = -> Fillet [Edge35]
  BaseFeature = -> Fillet
  Placement = pos=(0,0,0) rot=(1,0,0;1.5708rad)
  Radius = 1.5
  SupportTransform = false
  Suppressed = false
  UseAllEdges = false
FEATURE [PartDesign::Body] Body053  label="Bilderhaken"
  AllowCompound = false
  Group = -> [Sketch120,Revolution007,Sketch121,Pad054,Fillet,Fillet001]
  Origin = -> Origin056
  Placement = pos=(-185,15.5,54) rot=(0,0,1;0rad)
  Tip = -> Fillet001
FEATURE [Sketcher::SketchObject] Sketch122
  AttachmentSupport = -> [XY_Plane059]
  FullyConstrained = true
  MapMode = 5
  sketch-geometry (131):
    g0: LineSegment StartX=-195 StartY=35.5 StartZ=0 EndX=-195 EndY=-11.3 EndZ=0
    g1: LineSegment StartX=-195 StartY=-77.5 StartZ=0 EndX=195 EndY=-77.5 EndZ=0
    g2: LineSegment StartX=195 StartY=-77.5 StartZ=0 EndX=195 EndY=-20.5 EndZ=0
    g3: LineSegment StartX=195 StartY=35.5 StartZ=0 EndX=189 EndY=35.5 EndZ=0
    g4: LineSegment StartX=-189 StartY=35.5 StartZ=0 EndX=-189 EndY=20.5 EndZ=0
    g5: LineSegment StartX=-189 StartY=20.5 StartZ=0 EndX=-185.8 EndY=20.5 EndZ=0
    g6: LineSegment StartX=-185.8 StartY=20.5 StartZ=0 EndX=-185.8 EndY=35.5 EndZ=0
    g7: LineSegment StartX=185.8 StartY=35.5 StartZ=0 EndX=185.8 EndY=20.5 EndZ=0
    g8: LineSegment StartX=185.8 StartY=20.5 StartZ=0 EndX=189 EndY=20.5 EndZ=0
    g9: LineSegment StartX=189 StartY=20.5 StartZ=0 EndX=189 EndY=35.5 EndZ=0
    g10: LineSegment StartX=-189 StartY=35.5 StartZ=0 EndX=-195 EndY=35.5 EndZ=0
    g11: LineSegment StartX=-188.044 StartY=-63.1077 StartZ=0 EndX=-191.135 EndY=-62.2795 EndZ=0
    g12: LineSegment StartX=-191.135 StartY=-62.2795 StartZ=0 EndX=-188.495 EndY=-52.427 EndZ=0
    g13: LineSegment StartX=-188.495 StartY=-52.427 StartZ=0 EndX=-185.404 EndY=-53.2553 EndZ=0
    g14: LineSegment StartX=-185.404 StartY=-53.2553 StartZ=0 EndX=-188.044 EndY=-63.1077 EndZ=0
    g15: LineSegment StartX=-185.404 StartY=-53.2553 StartZ=0 EndX=-181.488 EndY=-38.6408 EndZ=0
    g16: LineSegment StartX=-181.488 StartY=-38.6408 StartZ=0 EndX=-184.579 EndY=-37.8126 EndZ=0
    g17: LineSegment StartX=-184.579 StartY=-37.8126 StartZ=0 EndX=-181.939 EndY=-27.9601 EndZ=0
    g18: LineSegment StartX=-181.939 StartY=-27.9601 StartZ=0 EndX=-178.848 EndY=-28.7884 EndZ=0
    g19: LineSegment StartX=-178.848 StartY=-28.7884 StartZ=0 EndX=-181.488 EndY=-38.6408 EndZ=0
    g20: LineSegment StartX=-178.848 StartY=-28.7884 StartZ=0 EndX=-174.932 EndY=-14.1739 EndZ=0
    g21: LineSegment StartX=-174.932 StartY=-14.1739 StartZ=0 EndX=-178.023 EndY=-13.3457 EndZ=0
    g22: LineSegment StartX=-178.023 StartY=-13.3457 StartZ=0 EndX=-175.383 EndY=-3.49324 EndZ=0
    g23: LineSegment StartX=-175.383 StartY=-3.49324 StartZ=0 EndX=-172.292 EndY=-4.32146 EndZ=0
    g24: LineSegment StartX=-172.292 StartY=-4.32146 StartZ=0 EndX=-174.932 EndY=-14.1739 EndZ=0
    g25: LineSegment StartX=-172.292 StartY=-4.32146 StartZ=0 EndX=-168.376 EndY=10.293 EndZ=0
    g26: LineSegment StartX=-168.376 StartY=10.293 StartZ=0 EndX=-171.467 EndY=11.1212 EndZ=0
    g27: LineSegment StartX=-171.467 StartY=11.1212 StartZ=0 EndX=-168.827 EndY=20.9737 EndZ=0
    g28: LineSegment StartX=-168.827 StartY=20.9737 StartZ=0 EndX=-165.736 EndY=20.1454 EndZ=0
    g29: LineSegment StartX=-165.736 StartY=20.1454 StartZ=0 EndX=-168.376 EndY=10.293 EndZ=0
    g30: LineSegment StartX=191.9 StartY=-77.5 StartZ=0 EndX=188.044 EndY=-63.1077 EndZ=0
    g31: LineSegment StartX=188.044 StartY=-63.1077 StartZ=0 EndX=191.135 EndY=-62.2795 EndZ=0
    g32: LineSegment StartX=191.135 StartY=-62.2795 StartZ=0 EndX=188.495 EndY=-52.427 EndZ=0
    g33: LineSegment StartX=188.495 StartY=-52.427 StartZ=0 EndX=185.404 EndY=-53.2553 EndZ=0
    g34: LineSegment StartX=185.404 StartY=-53.2553 StartZ=0 EndX=188.044 EndY=-63.1077 EndZ=0
    g35: LineSegment StartX=185.404 StartY=-53.2553 StartZ=0 EndX=181.488 EndY=-38.6408 EndZ=0
    g36: LineSegment StartX=181.488 StartY=-38.6408 StartZ=0 EndX=184.579 EndY=-37.8126 EndZ=0
    g37: LineSegment StartX=184.579 StartY=-37.8126 StartZ=0 EndX=181.939 EndY=-27.9601 EndZ=0
    g38: LineSegment StartX=181.939 StartY=-27.9601 StartZ=0 EndX=178.848 EndY=-28.7884 EndZ=0
    g39: LineSegment StartX=178.848 StartY=-28.7884 StartZ=0 EndX=181.488 EndY=-38.6408 EndZ=0
    g40: LineSegment StartX=178.848 StartY=-28.7884 StartZ=0 EndX=174.932 EndY=-14.1739 EndZ=0
    g41: LineSegment StartX=174.932 StartY=-14.1739 StartZ=0 EndX=178.023 EndY=-13.3457 EndZ=0
    g42: LineSegment StartX=178.023 StartY=-13.3457 StartZ=0 EndX=175.383 EndY=-3.49324 EndZ=0
    g43: LineSegment StartX=175.383 StartY=-3.49324 StartZ=0 EndX=172.292 EndY=-4.32146 EndZ=0
    g44: LineSegment StartX=172.292 StartY=-4.32146 StartZ=0 EndX=174.932 EndY=-14.1739 EndZ=0
    g45: LineSegment StartX=172.292 StartY=-4.32146 StartZ=0 EndX=168.376 EndY=10.293 EndZ=0
    g46: LineSegment StartX=168.376 StartY=10.293 StartZ=0 EndX=171.467 EndY=11.1212 EndZ=0
    g47: LineSegment StartX=171.467 StartY=11.1212 StartZ=0 EndX=168.827 EndY=20.9737 EndZ=0
    g48: LineSegment StartX=168.827 StartY=20.9737 StartZ=0 EndX=165.736 EndY=20.1454 EndZ=0
    g49: LineSegment StartX=165.736 StartY=20.1454 StartZ=0 EndX=168.376 EndY=10.293 EndZ=0
    g50: LineSegment StartX=-188.044 StartY=-63.1077 StartZ=0 EndX=-191.9 EndY=-77.5 EndZ=0
    g51: LineSegment StartX=-169.847 StartY=29.5293 StartZ=0 EndX=-166.756 EndY=28.7011 EndZ=0
    g52: LineSegment StartX=-166.756 StartY=28.7011 StartZ=0 EndX=-168.361 EndY=22.7123 EndZ=0
    g53: LineSegment StartX=-168.361 StartY=22.7123 StartZ=0 EndX=-171.452 EndY=23.5406 EndZ=0
    g54: LineSegment StartX=-171.452 StartY=23.5406 StartZ=0 EndX=-169.847 EndY=29.5293 EndZ=0
    g55: LineSegment StartX=-176.059 StartY=6.34707 StartZ=0 EndX=-177.664 EndY=0.35833 EndZ=0
    g56: LineSegment StartX=-177.664 StartY=0.35833 StartZ=0 EndX=-174.573 EndY=-0.469891 EndZ=0
    g57: LineSegment StartX=-174.573 StartY=-0.469891 StartZ=0 EndX=-172.968 EndY=5.51885 EndZ=0
    g58: LineSegment StartX=-172.968 StartY=5.51885 StartZ=0 EndX=-176.059 EndY=6.34707 EndZ=0
    g59: LineSegment StartX=-172.968 StartY=5.51885 StartZ=0 EndX=-168.361 EndY=22.7123 EndZ=0
    g60: LineSegment StartX=172.968 StartY=5.51885 StartZ=0 EndX=174.573 EndY=-0.469891 EndZ=0
    g61: LineSegment StartX=174.573 StartY=-0.469891 StartZ=0 EndX=177.664 EndY=0.35833 EndZ=0
    g62: LineSegment StartX=177.664 StartY=0.35833 StartZ=0 EndX=176.059 EndY=6.34707 EndZ=0
    g63: LineSegment StartX=176.059 StartY=6.34707 StartZ=0 EndX=172.968 EndY=5.51885 EndZ=0
    g64: LineSegment StartX=172.968 StartY=5.51885 StartZ=0 EndX=168.361 EndY=22.7123 EndZ=0
    g65: LineSegment StartX=168.361 StartY=22.7123 StartZ=0 EndX=171.452 EndY=23.5406 EndZ=0
    g66: LineSegment StartX=171.452 StartY=23.5406 StartZ=0 EndX=169.847 EndY=29.5293 EndZ=0
    g67: LineSegment StartX=169.847 StartY=29.5293 StartZ=0 EndX=166.756 EndY=28.7011 EndZ=0
    g68: LineSegment StartX=166.756 StartY=28.7011 StartZ=0 EndX=168.361 EndY=22.7123 EndZ=0
    g69: LineSegment StartX=-189 StartY=-20.5 StartZ=0 EndX=-189 EndY=-35.5 EndZ=0
    g70: LineSegment StartX=-189 StartY=-35.5 StartZ=0 EndX=-185.8 EndY=-35.5 EndZ=0
    g71: LineSegment StartX=-185.8 StartY=-35.5 StartZ=0 EndX=-185.8 EndY=-20.5 EndZ=0
    g72: LineSegment StartX=185.8 StartY=-20.5 StartZ=0 EndX=185.8 EndY=-35.5 EndZ=0
    g73: LineSegment StartX=185.8 StartY=-35.5 StartZ=0 EndX=189 EndY=-35.5 EndZ=0
    g74: LineSegment StartX=189 StartY=-35.5 StartZ=0 EndX=189 EndY=-20.5 EndZ=0
    g75: LineSegment StartX=-185.8 StartY=-20.5 StartZ=0 EndX=-185.8 EndY=-11.3 EndZ=0
    g76: LineSegment StartX=-185.8 StartY=-11.3 StartZ=0 EndX=-195 EndY=-11.3 EndZ=0
    g77: LineSegment StartX=-195 StartY=-20.5 StartZ=0 EndX=-189 EndY=-20.5 EndZ=0
    g78: LineSegment StartX=-195 StartY=-20.5 StartZ=0 EndX=-195 EndY=-77.5 EndZ=0
    g79: LineSegment StartX=189 StartY=-20.5 StartZ=0 EndX=195 EndY=-20.5 EndZ=0
    g80: LineSegment StartX=195 StartY=-11.3 StartZ=0 EndX=185.8 EndY=-11.3 EndZ=0
    g81: LineSegment StartX=185.8 StartY=-11.3 StartZ=0 EndX=185.8 EndY=-20.5 EndZ=0
    g82: LineSegment StartX=195 StartY=-11.3 StartZ=0 EndX=195 EndY=35.5 EndZ=0
    g83: Circle CenterX=-180 CenterY=31.5 CenterZ=0 NormalX=0 NormalY=0 NormalZ=1 AngleXU=0 Radius=2
    g84: Circle CenterX=180 CenterY=31.5 CenterZ=0 NormalX=0 NormalY=0 NormalZ=1 AngleXU=0 Radius=2
    g85: Circle CenterX=0 CenterY=31.5 CenterZ=0 NormalX=0 NormalY=0 NormalZ=1 AngleXU=0 Radius=2
    g86: LineSegment StartX=185.8 StartY=35.5 StartZ=0 EndX=162 EndY=35.5 EndZ=0
    g87: LineSegment StartX=162 StartY=35.5 StartZ=0 EndX=162 EndY=32.5 EndZ=0
    g88: LineSegment StartX=162 StartY=32.5 StartZ=0 EndX=153 EndY=32.5 EndZ=0
    g89: LineSegment StartX=153 StartY=32.5 StartZ=0 EndX=153 EndY=35.5 EndZ=0
    g90: LineSegment StartX=-162 StartY=35.5 StartZ=0 EndX=-185.8 EndY=35.5 EndZ=0
    g91: LineSegment StartX=-162 StartY=32.5 StartZ=0 EndX=-162 EndY=35.5 EndZ=0
    g92: LineSegment StartX=-112 StartY=32.5 StartZ=0 EndX=-162 EndY=32.5 EndZ=0
    g93: LineSegment StartX=153 StartY=35.5 StartZ=0 EndX=-112 EndY=35.5 EndZ=0
    g94: LineSegment StartX=-112 StartY=35.5 StartZ=0 EndX=-112 EndY=32.5 EndZ=0
    g95: LineSegment StartX=141 StartY=14.5 StartZ=0 EndX=141 EndY=9.5 EndZ=0
    g96: LineSegment StartX=141 StartY=9.5 StartZ=0 EndX=156 EndY=9.5 EndZ=0
    g97: LineSegment StartX=156 StartY=9.5 StartZ=0 EndX=156 EndY=14.5 EndZ=0
    g98: LineSegment StartX=156 StartY=14.5 StartZ=0 EndX=141 EndY=14.5 EndZ=0
    g99: LineSegment StartX=-60 StartY=15.5 StartZ=0 EndX=-45 EndY=15.5 EndZ=0
    g100: LineSegment StartX=-45 StartY=15.5 StartZ=0 EndX=-45 EndY=10.5 EndZ=0
    g101: LineSegment StartX=-45 StartY=10.5 StartZ=0 EndX=-60 EndY=10.5 EndZ=0
    g102: LineSegment StartX=-60 StartY=10.5 StartZ=0 EndX=-60 EndY=15.5 EndZ=0
    g103: LineSegment StartX=56 StartY=-57.5 StartZ=0 EndX=61 EndY=-57.5 EndZ=0
    g104: LineSegment StartX=61 StartY=-57.5 StartZ=0 EndX=61 EndY=-42.5 EndZ=0
    g105: LineSegment StartX=61 StartY=-42.5 StartZ=0 EndX=56 EndY=-42.5 EndZ=0
    g106: LineSegment StartX=56 StartY=-42.5 StartZ=0 EndX=56 EndY=-57.5 EndZ=0
    g107: LineSegment StartX=86 StartY=-29.5 StartZ=0 EndX=91 EndY=-29.5 EndZ=0
    g108: LineSegment StartX=91 StartY=-29.5 StartZ=0 EndX=91 EndY=-14.5 EndZ=0
    g109: LineSegment StartX=91 StartY=-14.5 StartZ=0 EndX=86 EndY=-14.5 EndZ=0
    g110: LineSegment StartX=86 StartY=-14.5 StartZ=0 EndX=86 EndY=-29.5 EndZ=0
    g111: LineSegment StartX=-160 StartY=15.5 StartZ=0 EndX=-160 EndY=10.5 EndZ=0
    g112: LineSegment StartX=-160 StartY=10.5 StartZ=0 EndX=-116 EndY=10.5 EndZ=0
    g113: LineSegment StartX=-116 StartY=10.5 StartZ=0 EndX=-116 EndY=15.5 EndZ=0
    g114: LineSegment StartX=-116 StartY=15.5 StartZ=0 EndX=-160 EndY=15.5 EndZ=0
    g115: LineSegment StartX=112 StartY=-24.5 StartZ=0 EndX=112 EndY=-29.5 EndZ=0
    g116: LineSegment StartX=112 StartY=-29.5 StartZ=0 EndX=117 EndY=-29.5 EndZ=0
    g117: LineSegment StartX=117 StartY=-29.5 StartZ=0 EndX=117 EndY=-24.5 EndZ=0
    g118: LineSegment StartX=117 StartY=-24.5 StartZ=0 EndX=112 EndY=-24.5 EndZ=0
    g119: LineSegment StartX=123 StartY=-24.5 StartZ=0 EndX=123 EndY=-29.5 EndZ=0
    g120: LineSegment StartX=123 StartY=-29.5 StartZ=0 EndX=128 EndY=-29.5 EndZ=0
    g121: LineSegment StartX=128 StartY=-29.5 StartZ=0 EndX=128 EndY=-24.5 EndZ=0
    g122: LineSegment StartX=128 StartY=-24.5 StartZ=0 EndX=123 EndY=-24.5 EndZ=0
    g123: LineSegment StartX=-38 StartY=-24.5 StartZ=0 EndX=-38 EndY=-29.5 EndZ=0
    g124: LineSegment StartX=-38 StartY=-29.5 StartZ=0 EndX=-33 EndY=-29.5 EndZ=0
    g125: LineSegment StartX=-33 StartY=-29.5 StartZ=0 EndX=-33 EndY=-24.5 EndZ=0
    g126: LineSegment StartX=-33 StartY=-24.5 StartZ=0 EndX=-38 EndY=-24.5 EndZ=0
    g127: LineSegment StartX=-27 StartY=-24.5 StartZ=0 EndX=-27 EndY=-29.5 EndZ=0
    g128: LineSegment StartX=-27 StartY=-29.5 StartZ=0 EndX=-22 EndY=-29.5 EndZ=0
    g129: LineSegment StartX=-22 StartY=-29.5 StartZ=0 EndX=-22 EndY=-24.5 EndZ=0
    g130: LineSegment StartX=-22 StartY=-24.5 StartZ=0 EndX=-27 EndY=-24.5 EndZ=0
  constraints (379):
    c: Coincident(g78,g1)
    c: Coincident(g1,g2)
    c: Coincident(g82,g3)
    c: Coincident(g10,g0)
    c: Vertical(g0)
    c: Vertical(g2)
    c: Horizontal(g3)
    c: Symmetric(g1,g78,g-2)
    c: DistanceX(g1,g1) = 390
    c: DistanceY(g2,g82) = 113
    c: DistanceY(g82) = 35.5
    c: Coincident(g4,g5)
    c: Coincident(g5,g6)
    c: Vertical(g4)
    c: Vertical(g6)
    c: Horizontal(g5)
    c: PointOnObject(g4,g3)
    c: Coincident(g7,g8)
    c: Coincident(g8,g9)
    c: Vertical(g7)
    c: Vertical(g9)
    c: Horizontal(g8)
    c: Equal(g8,g5)
    c: DistanceX(g5,g5) = 3.2
    c: DistanceX(g10,g10) = 6
    c: Coincident(g4,g10)
    c: Horizontal(g10)
    c: Coincident(g6,g90)
    c: Coincident(g86,g7)
    c: Horizontal(g7,g3)
    c: Equal(g3,g10)
    c: Coincident(g9,g3)
    c: DistanceY(g6,g6) = 15
    c: Equal(g7,g6)
    c: Coincident(g11,g12)
    c: Coincident(g12,g13)
    c: Coincident(g13,g14)
    c: Coincident(g13,g15)
    c: Coincident(g15,g16)
    c: Coincident(g16,g17)
    c: Coincident(g17,g18)
    c: Coincident(g18,g19)
    c: Coincident(g19,g15)
    c: Coincident(g18,g20)
    c: Coincident(g20,g21)
    c: Coincident(g21,g22)
    c: Coincident(g22,g23)
    c: Coincident(g23,g24)
    c: Coincident(g24,g20)
    c: Coincident(g23,g25)
    c: Coincident(g25,g26)
    c: Coincident(g26,g27)
    c: Coincident(g27,g28)
    c: Coincident(g28,g29)
    c: Coincident(g29,g25)
    c: Parallel(g29,g25)
    c: Parallel(g25,g24)
    c: Parallel(g24,g20)
    c: Parallel(g20,g19)
    c: Parallel(g19,g15)
    c: Parallel(g15,g14)
    c: Parallel(g14,g12)
    c: Parallel(g12,g17)
    c: Parallel(g17,g22)
    c: Parallel(g22,g27)
    c: Parallel(g23,g26)
    c: Parallel(g26,g28)
    c: Parallel(g28,g21)
    c: Parallel(g21,g18)
    c: Parallel(g18,g16)
    c: Parallel(g16,g13)
    c: Parallel(g13,g11)
    c: Equal(g13,g18)
    c: Equal(g18,g23)
    c: Equal(g23,g28)
    c: Equal(g15,g20)
    c: Equal(g20,g25)
    c: Equal(g29,g24)
    c: Equal(g24,g19)
    c: Equal(g19,g14)
    c: Distance(g11) = 3.2
    c: Coincident(g30,g31)
    c: Coincident(g31,g32)
    c: Coincident(g32,g33)
    c: Coincident(g33,g34)
    c: Coincident(g34,g30)
    c: Coincident(g33,g35)
    c: Coincident(g35,g36)
    c: Coincident(g36,g37)
    c: Coincident(g37,g38)
    c: Coincident(g38,g39)
    c: Coincident(g39,g35)
    c: Coincident(g38,g40)
    c: Coincident(g40,g41)
    c: Coincident(g41,g42)
    c: Coincident(g42,g43)
    c: Coincident(g43,g44)
    c: Coincident(g44,g40)
    c: Coincident(g43,g45)
    c: Coincident(g45,g46)
    c: Coincident(g46,g47)
    c: Coincident(g47,g48)
    c: Coincident(g48,g49)
    c: Coincident(g49,g45)
    c: Parallel(g49,g45)
    c: Parallel(g45,g44)
    c: Parallel(g40,g39)
    c: Parallel(g34,g30)
    c: Parallel(g34,g32)
    c: Parallel(g32,g37)
    c: Parallel(g37,g42)
    c: Parallel(g42,g47)
    c: Parallel(g43,g46)
    c: Parallel(g46,g48)
    c: Parallel(g48,g41)
    c: Parallel(g41,g38)
    c: Parallel(g38,g36)
    c: Parallel(g36,g33)
    c: Parallel(g33,g31)
    c: Perpendicular(g30,g31)
    c: Equal(g33,g38)
    c: Equal(g38,g43)
    c: Equal(g43,g48)
    c: Equal(g35,g40)
    c: Equal(g40,g45)
    c: Equal(g49,g44)
    c: Equal(g44,g39)
    c: Equal(g39,g34)
    c: Equal(g35,g15)
    c: Equal(g34,g14)
    c: Equal(g31,g11)
    c: Angle(g30) = 1.8326
    c: Distance(g14) = 10.2
    c: Distance(g25) = 15.13
    c: Parallel(g44,g40)
    c: Parallel(g35,g39)
    c: Parallel(g34,g35)
    c: Coincident(g14,g50)
    c: PointOnObject(g50,g1)
    c: DistanceX(g78,g50) = 3.1
    c: Distance(g50) = 14.9
    c: Parallel(g50,g14)
    c: Coincident(g11,g14)
    c: Perpendicular(g14,g11)
    c: Angle(g50) = -1.8326
    c: Symmetric(g50,g30,g-2)
    c: Equal(g30,g50)
    c: Coincident(g51,g52)
    c: Coincident(g52,g53)
    c: Coincident(g53,g54)
    c: Coincident(g54,g51)
    c: Coincident(g55,g56)
    c: Coincident(g56,g57)
    c: Coincident(g57,g58)
    c: Coincident(g58,g55)
    c: Coincident(g57,g59)
    c: Coincident(g59,g52)
    c: Parallel(g52,g59)
    c: Parallel(g59,g57)
    c: Equal(g57,g52)
    c: Parallel(g52,g54)
    c: Parallel(g54,g55)
    c: Parallel(g56,g58)
    c: Parallel(g58,g53)
    c: Parallel(g53,g51)
    c: Perpendicular(g52,g51)
    c: PointOnObject(g27,g59)
    c: Parallel(g59,g27)
    c: Distance(g52) = 6.2
    c: Equal(g58,g53)
    c: Equal(g53,g28)
    c: Distance(g59) = 17.8
    c: Distance(g52,g27) = 1.8
    c: Coincident(g60,g61)
    c: Coincident(g61,g62)
    c: Coincident(g62,g63)
    c: Coincident(g63,g60)
    c: Coincident(g60,g64)
    c: Coincident(g64,g65)
    c: Coincident(g65,g66)
    c: Coincident(g66,g67)
    c: Coincident(g67,g68)
    c: Coincident(g68,g64)
    c: Parallel(g60,g64)
    c: Parallel(g64,g68)
    c: Parallel(g68,g62)
    c: Parallel(g62,g66)
    c: Parallel(g65,g63)
    c: Parallel(g63,g61)
    c: Parallel(g61,g67)
    c: Equal(g65,g63)
    c: Perpendicular(g68,g67)
    c: Equal(g65,g48)
    c: PointOnObject(g47,g64)
    c: Parallel(g64,g47)
    c: Equal(g62,g66)
    c: Equal(g64,g59)
    c: Equal(g52,g68)
    c: Horizontal(g67,g51)
    c: Coincident(g69,g70)
    c: Coincident(g70,g71)
    c: Vertical(g69)
    c: Vertical(g71)
    c: Horizontal(g70)
    c: Equal(g6,g69)
    c: Symmetric(g69,g4,g-1)
    c: Coincident(g72,g73)
    c: Coincident(g73,g74)
    c: Vertical(g72)
    c: Vertical(g74)
    c: Horizontal(g73)
    c: Equal(g9,g74)
    c: Symmetric(g8,g74,g-1)
    c: Coincident(g75,g76)
    c: Vertical(g75)
    c: Horizontal(g76)
    c: Horizontal(g77)
    c: Coincident(g75,g71)
    c: Equal(g76,g75)
    c: Coincident(g0,g76)
    c: Coincident(g77,g78)
    c: Coincident(g77,g69)
    c: Equal(g71,g69)
    c: Vertical(g77,g0)
    c: Vertical(g78)
    c: Vertical(g5,g75)
    c: Coincident(g80,g81)
    c: Horizontal(g79)
    c: Horizontal(g80)
    c: Vertical(g81)
    c: Coincident(g81,g72)
    c: Equal(g81,g80)
    c: Coincident(g80,g82)
    c: Vertical(g82)
    c: Vertical(g80,g2)
    c: Coincident(g74,g79)
    c: Coincident(g79,g2)
    c: Vertical(g80,g7)
    c: Horizontal(g74,g72)
    c: Diameter(g83) = 4
    c: DistanceY(g83,g6) = 4
    c: DistanceX(g4,g83) = 9
    c: Equal(g84,g83)
    c: Symmetric(g83,g84,g-2)
    c: PointOnObject(g85,g-2)
    c: Equal(g85,g84)
    c: Horizontal(g84,g85)
    c: Coincident(g86,g87)
    c: Horizontal(g86)
    c: Coincident(g87,g88)
    c: Coincident(g88,g89)
    c: Horizontal(g88)
    c: Coincident(g89,g93)
    c: Vertical(g89)
    c: Vertical(g87)
    c: DistanceX(g88,g88) = 9
    c: DistanceY(g87,g87) = 3
    c: Horizontal(g89,g86)
    c: Coincident(g91,g90)
    c: Horizontal(g90)
    c: Coincident(g92,g91)
    c: Coincident(g94,g92)
    c: Horizontal(g92)
    c: Coincident(g93,g94)
    c: Horizontal(g93)
    c: Vertical(g91)
    c: Vertical(g94)
    c: Symmetric(g90,g86,g-2)
    c: DistanceX(g90,g86) = 324
    c: Equal(g91,g87)
    c: DistanceX(g92,g92) = 50
    c: Coincident(g95,g96)
    c: Coincident(g96,g97)
    c: Coincident(g97,g98)
    c: Coincident(g98,g95)
    c: Vertical(g95)
    c: Vertical(g97)
    c: Horizontal(g96)
    c: Horizontal(g98)
    c: DistanceY(g95,g95) = 5
    c: DistanceY(g95,g89) = 21
    c: DistanceX(g96,g96) = 15
    c: DistanceX(g97,g3) = 39
    c: Coincident(g99,g100)
    c: Coincident(g100,g101)
    c: Coincident(g101,g102)
    c: Coincident(g102,g99)
    c: Horizontal(g99)
    c: Horizontal(g101)
    c: Vertical(g100)
    c: Vertical(g102)
    c: Distance(g100,g102) = 15
    c: Distance(g99,g101) = 5
    c: DistanceX(g100) = -45
    c: Coincident(g103,g104)
    c: Coincident(g104,g105)
    c: Coincident(g105,g106)
    c: Coincident(g106,g103)
    c: Horizontal(g103)
    c: Horizontal(g105)
    c: Vertical(g104)
    c: Vertical(g106)
    c: DistanceX(g105,g105) = 5
    c: DistanceY(g104,g104) = 15
    c: DistanceY(g1,g103) = 20
    c: DistanceX(g103) = 56
    c: Coincident(g107,g108)
    c: Coincident(g108,g109)
    c: Coincident(g109,g110)
    c: Coincident(g110,g107)
    c: Horizontal(g107)
    c: Horizontal(g109)
    c: Vertical(g108)
    c: Vertical(g110)
    c: Distance(g108,g110) = 5
    c: Distance(g107,g109) = 15
    c: DistanceY(g104,g107) = 13
    c: DistanceX(g104,g107) = 25
    c: Coincident(g111,g112)
    c: Coincident(g112,g113)
    c: Coincident(g113,g114)
    c: Coincident(g114,g111)
    c: Vertical(g111)
    c: Vertical(g113)
    c: Horizontal(g112)
    c: Horizontal(g114)
    c: Distance(g111,g113) = 44
    c: Distance(g112,g114) = 5
    c: Horizontal(g99,g113)
    c: DistanceY(g111,g0) = 20
    c: DistanceX(g0,g111) = 35
    c: Coincident(g115,g116)
    c: Coincident(g116,g117)
    c: Coincident(g117,g118)
    c: Coincident(g118,g115)
    c: Vertical(g115)
    c: Vertical(g117)
    c: Horizontal(g116)
    c: Horizontal(g118)
    c: Distance(g115,g117) = 5
    c: Distance(g116,g118) = 5
    c: Coincident(g119,g120)
    c: Coincident(g120,g121)
    c: Coincident(g121,g122)
    c: Coincident(g122,g119)
    c: Vertical(g119)
    c: Vertical(g121)
    c: Horizontal(g120)
    c: Horizontal(g122)
    c: Distance(g119,g121) = 5
    c: Distance(g120,g122) = 5
    c: Coincident(g123,g124)
    c: Coincident(g124,g125)
    c: Coincident(g125,g126)
    c: Coincident(g126,g123)
    c: Vertical(g123)
    c: Vertical(g125)
    c: Horizontal(g124)
    c: Horizontal(g126)
    c: Distance(g123,g125) = 5
    c: Distance(g124,g126) = 5
    c: Coincident(g127,g128)
    c: Coincident(g128,g129)
    c: Coincident(g129,g130)
    c: Coincident(g130,g127)
    c: Vertical(g127)
    c: Vertical(g129)
    c: Horizontal(g128)
    c: Horizontal(g130)
    c: Distance(g127,g129) = 5
    c: Distance(g128,g130) = 5
    c: Horizontal(g125,g127)
    c: Horizontal(g129,g115)
    c: Horizontal(g115,g119)
    c: DistanceX(g116,g119) = 6
    c: DistanceX(g124,g127) = 6
    c: DistanceX(g127,g119) = 150
    c: Horizontal(g107,g115)
    c: DistanceX(g128) = -22
FEATURE [PartDesign::Pad] Pad055
  Direction = (0,0,1)
  Length = 3
  Length2 = 10
  Profile = -> Sketch122
  ReferenceAxis = -> Sketch122 [N_Axis]
  Reversed = true
  Suppressed = false
  Type = 0
FEATURE [PartDesign::Body] Body054  label="Floor3mmA"
  AllowCompound = false
  Group = -> [Sketch122,Pad055]
  Origin = -> Origin059
  Tip = -> Pad055
FEATURE [Sketcher::SketchObject] Sketch124
  AttachmentSupport = -> [YZ_Plane061]
  FullyConstrained = true
  MapMode = 5
  Placement = pos=(0,0,0) rot=(0.57735,0.57735,0.57735;2.0944rad)
  sketch-geometry (40):
    g0: LineSegment StartX=0 StartY=0 StartZ=0 EndX=15 EndY=0 EndZ=0
    g1: LineSegment StartX=15 StartY=0 StartZ=0 EndX=15 EndY=-5.9 EndZ=0
    g2: LineSegment StartX=15 StartY=-5.9 StartZ=0 EndX=25 EndY=-5.9 EndZ=0
    g3: LineSegment StartX=25 StartY=-5.9 StartZ=0 EndX=25 EndY=0 EndZ=0
    g4: LineSegment StartX=25 StartY=0 StartZ=0 EndX=40.3333 EndY=0 EndZ=0
    g5: LineSegment StartX=40.3333 StartY=0 StartZ=0 EndX=40.3333 EndY=-5.9 EndZ=0
    g6: LineSegment StartX=40.3333 StartY=-5.9 StartZ=0 EndX=50.3333 EndY=-5.9 EndZ=0
    g7: LineSegment StartX=50.3333 StartY=-5.9 StartZ=0 EndX=50.3333 EndY=0 EndZ=0
    g8: LineSegment StartX=50.3333 StartY=0 StartZ=0 EndX=65.6667 EndY=0 EndZ=0
    g9: LineSegment StartX=65.6667 StartY=0 StartZ=0 EndX=65.6667 EndY=-5.9 EndZ=0
    g10: LineSegment StartX=65.6667 StartY=-5.9 StartZ=0 EndX=75.6667 EndY=-5.9 EndZ=0
    g11: LineSegment StartX=75.6667 StartY=-5.9 StartZ=0 EndX=75.6667 EndY=0 EndZ=0
    g12: LineSegment StartX=75.6667 StartY=0 StartZ=0 EndX=91 EndY=0 EndZ=0
    g13: LineSegment StartX=91 StartY=0 StartZ=0 EndX=91 EndY=-5.9 EndZ=0
    g14: LineSegment StartX=91 StartY=-5.9 StartZ=0 EndX=101 EndY=-5.9 EndZ=0
    g15: LineSegment StartX=101 StartY=-5.9 StartZ=0 EndX=101 EndY=0 EndZ=0
    g16: LineSegment StartX=101 StartY=0 StartZ=0 EndX=116 EndY=0 EndZ=0
    g17: LineSegment StartX=0 StartY=100 StartZ=0 EndX=15 EndY=100 EndZ=0
    g18: LineSegment StartX=15 StartY=100 StartZ=0 EndX=15 EndY=105.9 EndZ=0
    g19: LineSegment StartX=15 StartY=105.9 StartZ=0 EndX=25 EndY=105.9 EndZ=0
    g20: LineSegment StartX=25 StartY=105.9 StartZ=0 EndX=25 EndY=100 EndZ=0
    g21: LineSegment StartX=25 StartY=100 StartZ=0 EndX=40.3333 EndY=100 EndZ=0
    g22: LineSegment StartX=40.3333 StartY=100 StartZ=0 EndX=40.3333 EndY=105.9 EndZ=0
    g23: LineSegment StartX=40.3333 StartY=105.9 StartZ=0 EndX=50.3333 EndY=105.9 EndZ=0
    g24: LineSegment StartX=50.3333 StartY=105.9 StartZ=0 EndX=50.3333 EndY=100 EndZ=0
    g25: LineSegment StartX=50.3333 StartY=100 StartZ=0 EndX=65.6667 EndY=100 EndZ=0
    g26: LineSegment StartX=65.6667 StartY=100 StartZ=0 EndX=65.6667 EndY=105.9 EndZ=0
    g27: LineSegment StartX=65.6667 StartY=105.9 StartZ=0 EndX=75.6667 EndY=105.9 EndZ=0
    g28: LineSegment StartX=75.6667 StartY=105.9 StartZ=0 EndX=75.6667 EndY=100 EndZ=0
    g29: LineSegment StartX=75.6667 StartY=100 StartZ=0 EndX=91 EndY=100 EndZ=0
    g30: LineSegment StartX=91 StartY=100 StartZ=0 EndX=91 EndY=105.9 EndZ=0
    g31: LineSegment StartX=91 StartY=105.9 StartZ=0 EndX=101 EndY=105.9 EndZ=0
    g32: LineSegment StartX=101 StartY=105.9 StartZ=0 EndX=101 EndY=100 EndZ=0
    g33: LineSegment StartX=101 StartY=100 StartZ=0 EndX=116 EndY=100 EndZ=0
    g34: LineSegment StartX=0 StartY=100 StartZ=0 EndX=0 EndY=0 EndZ=0
    g35: LineSegment StartX=116 StartY=0 StartZ=0 EndX=116 EndY=6 EndZ=0
    g36: LineSegment StartX=116 StartY=6 StartZ=0 EndX=109.8 EndY=6 EndZ=0
    g37: LineSegment StartX=109.8 StartY=6 StartZ=0 EndX=109.8 EndY=9 EndZ=0
    g38: LineSegment StartX=109.8 StartY=9 StartZ=0 EndX=116 EndY=9 EndZ=0
    g39: LineSegment StartX=116 StartY=9 StartZ=0 EndX=116 EndY=100 EndZ=0
  constraints (119):
    c: Coincident(g-1,g0)
    c: PointOnObject(g0,g-1)
    c: Coincident(g0,g1)
    c: Vertical(g1)
    c: Coincident(g1,g2)
    c: Horizontal(g2)
    c: Coincident(g2,g3)
    c: PointOnObject(g3,g-1)
    c: Vertical(g3)
    c: Coincident(g3,g4)
    c: PointOnObject(g4,g-1)
    c: Coincident(g4,g5)
    c: Vertical(g5)
    c: Coincident(g5,g6)
    c: Horizontal(g6)
    c: Coincident(g6,g7)
    c: PointOnObject(g7,g-1)
    c: Vertical(g7)
    c: Coincident(g7,g8)
    c: PointOnObject(g8,g-1)
    c: Coincident(g8,g9)
    c: Vertical(g9)
    c: Coincident(g9,g10)
    c: Horizontal(g10)
    c: Coincident(g10,g11)
    c: PointOnObject(g11,g-1)
    c: Vertical(g11)
    c: Coincident(g11,g12)
    c: PointOnObject(g12,g-1)
    c: Coincident(g12,g13)
    c: Vertical(g13)
    c: Coincident(g13,g14)
    c: Horizontal(g14)
    c: Coincident(g14,g15)
    c: PointOnObject(g15,g-1)
    c: Coincident(g15,g16)
    c: PointOnObject(g16,g-1)
    c: Coincident(g16,g35)
    c: Equal(g0,g16)
    c: DistanceX(g0,g0) = 15
    c: Vertical(g15)
    c: Equal(g15,g11)
    c: Equal(g11,g7)
    c: Equal(g7,g3)
    c: DistanceY(g15,g15) = 5.9
    c: Coincident(g17,g18)
    c: Vertical(g18)
    c: Coincident(g18,g19)
    c: Horizontal(g19)
    c: Coincident(g19,g20)
    c: Vertical(g20)
    c: Coincident(g20,g21)
    c: Coincident(g21,g22)
    c: Vertical(g22)
    c: Coincident(g22,g23)
    c: Horizontal(g23)
    c: Coincident(g23,g24)
    c: Vertical(g24)
    c: Coincident(g24,g25)
    c: Coincident(g25,g26)
    c: Vertical(g26)
    c: Coincident(g26,g27)
    c: Horizontal(g27)
    c: Coincident(g27,g28)
    c: Vertical(g28)
    c: Coincident(g28,g29)
    c: Coincident(g29,g30)
    c: Vertical(g30)
    c: Coincident(g30,g31)
    c: Horizontal(g31)
    c: Coincident(g31,g32)
    c: Coincident(g32,g33)
    c: Equal(g17,g33)
    c: Vertical(g32)
    c: Equal(g32,g28)
    c: Equal(g28,g24)
    c: Equal(g24,g20)
    c: Horizontal(g33)
    c: Horizontal(g29)
    c: Horizontal(g25)
    c: Horizontal(g21)
    c: Horizontal(g17)
    c: Equal(g32,g30)
    c: Equal(g30,g26)
    c: Equal(g26,g22)
    c: Equal(g22,g18)
    c: Coincident(g17,g34)
    c: Coincident(g34,g0)
    c: Vertical(g34)
    c: DistanceY(g34,g34) = 100
    c: Coincident(g39,g33)
    c: DistanceX(g16) = 116
    c: Equal(g32,g15)
    c: Equal(g14,g10)
    c: Equal(g10,g6)
    c: Equal(g6,g2)
    c: Equal(g4,g8)
    c: Equal(g8,g12)
    c: DistanceX(g14,g14) = 10
    c: Equal(g31,g27)
    c: Equal(g27,g23)
    c: Equal(g23,g19)
    c: Equal(g25,g21)
    c: Equal(g21,g29)
    c: Equal(g31,g14)
    c: Equal(g17,g0)
    c: Coincident(g35,g36)
    c: Vertical(g35)
    c: Coincident(g36,g37)
    c: Coincident(g37,g38)
    c: Vertical(g37)
    c: Coincident(g38,g39)
    c: Vertical(g39)
    c: Horizontal(g36)
    c: Horizontal(g38)
    c: DistanceY(g35,g35) = 6
    c: DistanceX(g36,g36) = 6.2
    c: DistanceY(g37,g37) = 3
    c: Vertical(g35,g38)
FEATURE [PartDesign::Pad] Pad057
  Direction = (1,0,0)
  Length = 3
  Length2 = 10
  Placement = pos=(0,0,0) rot=(0.57735,0.57735,0.57735;2.0944rad)
  Profile = -> Sketch124
  ReferenceAxis = -> Sketch124 [N_Axis]
  Reversed = true
  Suppressed = false
  Type = 0
FEATURE [PartDesign::Body] Body056  label="InnenWandA"
  AllowCompound = false
  Group = -> [Sketch124,Pad057]
  Origin = -> Origin061
  Placement = pos=(-192,-77.5,0) rot=(0,0,-1;0.261799rad)
  Tip = -> Pad057
FEATURE [PartDesign::FeatureBase] Clone005
  BaseFeature = -> Body056
  Placement = pos=(-192,-77.5,0) rot=(0,0,-1;0.261799rad)
  Suppressed = false
FEATURE [PartDesign::Body] Body057  label="InnenWandB"
  AllowCompound = false
  Group = -> [Clone005]
  Origin = -> Origin062
  Placement = pos=(-1.2e-14,0,100) rot=(0,1,0;3.14159rad)
  Tip = -> Clone005
FEATURE [Sketcher::SketchObject] Sketch125
  AttachmentSupport = -> [YZ_Plane063]
  FullyConstrained = true
  MapMode = 5
  Placement = pos=(0,0,0) rot=(0.57735,0.57735,0.57735;2.0944rad)
  sketch-geometry (30):
    g0: LineSegment StartX=0 StartY=0 StartZ=0 EndX=-6 EndY=0 EndZ=0
    g1: LineSegment StartX=-6 StartY=0 StartZ=0 EndX=-6 EndY=-5.9 EndZ=0
    g2: LineSegment StartX=-6 StartY=-5.9 StartZ=0 EndX=-12 EndY=-5.9 EndZ=0
    g3: LineSegment StartX=-12 StartY=-5.9 StartZ=0 EndX=-12 EndY=0 EndZ=0
    g4: LineSegment StartX=-12 StartY=0 StartZ=0 EndX=-30 EndY=0 EndZ=0
    g5: LineSegment StartX=-30 StartY=0 StartZ=0 EndX=-30 EndY=-5.9 EndZ=0
    g6: LineSegment StartX=-30 StartY=-5.9 StartZ=0 EndX=-36 EndY=-5.9 EndZ=0
    g7: LineSegment StartX=-36 StartY=-5.9 StartZ=0 EndX=-36 EndY=0 EndZ=0
    g8: LineSegment StartX=-36 StartY=0 StartZ=0 EndX=-42 EndY=0 EndZ=0
    g9: LineSegment StartX=-42 StartY=0 StartZ=0 EndX=-42 EndY=100 EndZ=0
    g10: LineSegment StartX=4e-16 StartY=100 StartZ=0 EndX=-6 EndY=100 EndZ=0
    g11: LineSegment StartX=-6 StartY=100 StartZ=0 EndX=-6 EndY=105.9 EndZ=0
    g12: LineSegment StartX=-6 StartY=105.9 StartZ=0 EndX=-12 EndY=105.9 EndZ=0
    g13: LineSegment StartX=-12 StartY=105.9 StartZ=0 EndX=-12 EndY=100 EndZ=0
    g14: LineSegment StartX=-12 StartY=100 StartZ=0 EndX=-30 EndY=100 EndZ=0
    g15: LineSegment StartX=-30 StartY=100 StartZ=0 EndX=-30 EndY=105.9 EndZ=0
    g16: LineSegment StartX=-30 StartY=105.9 StartZ=0 EndX=-36 EndY=105.9 EndZ=0
    g17: LineSegment StartX=-36 StartY=105.9 StartZ=0 EndX=-36 EndY=100 EndZ=0
    g18: LineSegment StartX=-36 StartY=100 StartZ=0 EndX=-42 EndY=100 EndZ=0
    g19: LineSegment StartX=-27 StartY=75 StartZ=0 EndX=-27 EndY=25 EndZ=0
    g20: LineSegment StartX=-27 StartY=25 StartZ=0 EndX=-15 EndY=25 EndZ=0
    g21: LineSegment StartX=-15 StartY=25 StartZ=0 EndX=-15 EndY=75 EndZ=0
    g22: LineSegment StartX=-15 StartY=75 StartZ=0 EndX=-27 EndY=75 EndZ=0
    g23: LineSegment StartX=-27 StartY=50 StartZ=0 EndX=-15 EndY=50 EndZ=0
    g24: LineSegment StartX=-21 StartY=75 StartZ=0 EndX=-21 EndY=25 EndZ=0
    g25: LineSegment StartX=0 StartY=6 StartZ=0 EndX=0 EndY=0 EndZ=0
    g26: LineSegment StartX=-5 StartY=6 StartZ=0 EndX=0 EndY=6 EndZ=0
    g27: LineSegment StartX=-5 StartY=9 StartZ=0 EndX=-5 EndY=6 EndZ=0
    g28: LineSegment StartX=4e-16 StartY=100 StartZ=0 EndX=4e-16 EndY=9 EndZ=0
    g29: LineSegment StartX=4e-16 StartY=9 StartZ=0 EndX=-5 EndY=9 EndZ=0
  constraints (85):
    c: Coincident(g-1,g0)
    c: PointOnObject(g0,g-1)
    c: Coincident(g0,g1)
    c: Vertical(g1)
    c: Coincident(g1,g2)
    c: Horizontal(g2)
    c: Coincident(g2,g3)
    c: PointOnObject(g3,g-1)
    c: Vertical(g3)
    c: Coincident(g3,g4)
    c: PointOnObject(g4,g-1)
    c: Coincident(g4,g5)
    c: Vertical(g5)
    c: Coincident(g5,g6)
    c: Horizontal(g6)
    c: Coincident(g6,g7)
    c: PointOnObject(g7,g-1)
    c: Vertical(g7)
    c: Coincident(g7,g8)
    c: PointOnObject(g8,g-1)
    c: Coincident(g8,g9)
    c: Vertical(g9)
    c: Equal(g8,g0)
    c: DistanceX(g0,g0) = 6
    c: Equal(g2,g6)
    c: DistanceX(g6,g6) = 6
    c: DistanceX(g4,g4) = 18
    c: Equal(g1,g5)
    c: DistanceY(g1,g1) = 5.9
    c: Coincident(g10,g11)
    c: Vertical(g11)
    c: Coincident(g11,g12)
    c: Horizontal(g12)
    c: Coincident(g12,g13)
    c: Vertical(g13)
    c: Coincident(g13,g14)
    c: Coincident(g14,g15)
    c: Vertical(g15)
    c: Coincident(g15,g16)
    c: Horizontal(g16)
    c: Coincident(g16,g17)
    c: Vertical(g17)
    c: Coincident(g17,g18)
    c: Equal(g18,g10)
    c: Equal(g12,g16)
    c: Equal(g11,g15)
    c: Horizontal(g10)
    c: Horizontal(g14)
    c: Horizontal(g13,g10)
    c: Horizontal(g10,g17)
    c: Horizontal(g18)
    c: Equal(g10,g0)
    c: Equal(g14,g4)
    c: Equal(g16,g6)
    c: Equal(g11,g1)
    c: Coincident(g9,g18)
    c: Coincident(g10,g28)
    c: Coincident(g25,g0)
    c: DistanceY(g25,g28) = 100
    c: Coincident(g19,g20)
    c: Coincident(g20,g21)
    c: Coincident(g21,g22)
    c: Coincident(g22,g19)
    c: Vertical(g19)
    c: Horizontal(g20)
    c: Symmetric(g19,g19,g23)
    c: Symmetric(g21,g21,g23)
    c: Symmetric(g22,g22,g24)
    c: Symmetric(g20,g20,g24)
    c: Symmetric(g0,g10,g23)
    c: Symmetric(g8,g0,g24)
    c: DistanceX(g20,g20) = 12
    c: DistanceY(g19,g19) = 50
    c: Coincident(g26,g25)
    c: Coincident(g27,g26)
    c: Coincident(g29,g27)
    c: Coincident(g28,g29)
    c: Vertical(g25)
    c: Horizontal(g26)
    c: Vertical(g27)
    c: Horizontal(g29)
    c: DistanceY(g27,g27) = 3
    c: Vertical(g28)
    c: DistanceY(g25,g25) = 6
    c: DistanceX(g26,g26) = 5
FEATURE [PartDesign::Pad] Pad058
  Direction = (1,0,0)
  Length = 3
  Length2 = 10
  Placement = pos=(0,0,0) rot=(0.57735,0.57735,0.57735;2.0944rad)
  Profile = -> Sketch125
  ReferenceAxis = -> Sketch125 [N_Axis]
  Suppressed = false
  Type = 0
FEATURE [PartDesign::Body] Body058  label="InnenWandC"
  AllowCompound = false
  Group = -> [Sketch125,Pad058]
  Origin = -> Origin063
  Placement = pos=(-168.2,35,0) rot=(0,0,-1;0.261799rad)
  Tip = -> Pad058
FEATURE [PartDesign::FeatureBase] Clone006
  BaseFeature = -> Body058
  Placement = pos=(-168.2,35,0) rot=(0,0,-1;0.261799rad)
  Suppressed = false
FEATURE [PartDesign::Body] Body059  label="InnenWandD"
  AllowCompound = false
  Group = -> [Clone006]
  Origin = -> Origin064
  Placement = pos=(-1.2e-14,0,100) rot=(0,1,0;3.14159rad)
  Tip = -> Clone006
FEATURE [Sketcher::SketchObject] Sketch126
  AttachmentSupport = -> [XY_Plane065]
  FullyConstrained = true
  MapMode = 5
  expr: Constraints[10] = Sketch122.Constraints[10]
  expr: Constraints[131] = Sketch122.Constraints[131]
  expr: Constraints[132] = Sketch122.Constraints[132]
  expr: Constraints[133] = Sketch122.Constraints[133]
  expr: Constraints[139] = Sketch122.Constraints[139]
  expr: Constraints[140] = Sketch122.Constraints[140]
  expr: Constraints[144] = Sketch122.Constraints[144]
  expr: Constraints[168] = Sketch122.Constraints[168]
  expr: Constraints[171] = Sketch122.Constraints[171]
  expr: Constraints[172] = Sketch122.Constraints[172]
  expr: Constraints[23] = Sketch122.Constraints[23]
  expr: Constraints[24] = Sketch122.Constraints[24]
  expr: Constraints[32] = Sketch122.Constraints[32]
  expr: Constraints[80] = Sketch122.Constraints[80]
  expr: Constraints[8] = Sketch122.Constraints[8]
  expr: Constraints[9] = Sketch122.Constraints[9]
  sketch-geometry (170):
    g0: LineSegment StartX=-195 StartY=35.5 StartZ=0 EndX=-195 EndY=17 EndZ=0
    g1: LineSegment StartX=-195 StartY=-77.5 StartZ=0 EndX=195 EndY=-77.5 EndZ=0
    g2: LineSegment StartX=195 StartY=-77.5 StartZ=0 EndX=195 EndY=-20.5 EndZ=0
    g3: LineSegment StartX=195 StartY=35.5 StartZ=0 EndX=189 EndY=35.5 EndZ=0
    g4: LineSegment StartX=-189 StartY=35.5 StartZ=0 EndX=-189 EndY=20.5 EndZ=0
    g5: LineSegment StartX=-189 StartY=20.5 StartZ=0 EndX=-185.8 EndY=20.5 EndZ=0
    g6: LineSegment StartX=-185.8 StartY=20.5 StartZ=0 EndX=-185.8 EndY=35.5 EndZ=0
    g7: LineSegment StartX=185.8 StartY=35.5 StartZ=0 EndX=185.8 EndY=20.5 EndZ=0
    g8: LineSegment StartX=185.8 StartY=20.5 StartZ=0 EndX=189 EndY=20.5 EndZ=0
    g9: LineSegment StartX=189 StartY=20.5 StartZ=0 EndX=189 EndY=35.5 EndZ=0
    g10: LineSegment StartX=-189 StartY=35.5 StartZ=0 EndX=-195 EndY=35.5 EndZ=0
    g11: LineSegment StartX=-188.044 StartY=-63.1077 StartZ=0 EndX=-191.135 EndY=-62.2795 EndZ=0
    g12: LineSegment StartX=-191.135 StartY=-62.2795 StartZ=0 EndX=-188.495 EndY=-52.427 EndZ=0
    g13: LineSegment StartX=-188.495 StartY=-52.427 StartZ=0 EndX=-185.404 EndY=-53.2553 EndZ=0
    g14: LineSegment StartX=-185.404 StartY=-53.2553 StartZ=0 EndX=-188.044 EndY=-63.1077 EndZ=0
    g15: LineSegment StartX=-185.404 StartY=-53.2553 StartZ=0 EndX=-181.488 EndY=-38.6408 EndZ=0
    g16: LineSegment StartX=-181.488 StartY=-38.6408 StartZ=0 EndX=-184.579 EndY=-37.8126 EndZ=0
    g17: LineSegment StartX=-184.579 StartY=-37.8126 StartZ=0 EndX=-181.939 EndY=-27.9601 EndZ=0
    g18: LineSegment StartX=-181.939 StartY=-27.9601 StartZ=0 EndX=-178.848 EndY=-28.7884 EndZ=0
    g19: LineSegment StartX=-178.848 StartY=-28.7884 StartZ=0 EndX=-181.488 EndY=-38.6408 EndZ=0
    g20: LineSegment StartX=-178.848 StartY=-28.7884 StartZ=0 EndX=-174.932 EndY=-14.1739 EndZ=0
    g21: LineSegment StartX=-174.932 StartY=-14.1739 StartZ=0 EndX=-178.023 EndY=-13.3457 EndZ=0
    g22: LineSegment StartX=-178.023 StartY=-13.3457 StartZ=0 EndX=-175.383 EndY=-3.49324 EndZ=0
    g23: LineSegment StartX=-175.383 StartY=-3.49324 StartZ=0 EndX=-172.292 EndY=-4.32146 EndZ=0
    g24: LineSegment StartX=-172.292 StartY=-4.32146 StartZ=0 EndX=-174.932 EndY=-14.1739 EndZ=0
    g25: LineSegment StartX=-172.292 StartY=-4.32146 StartZ=0 EndX=-168.376 EndY=10.293 EndZ=0
    g26: LineSegment StartX=-168.376 StartY=10.293 StartZ=0 EndX=-171.467 EndY=11.1212 EndZ=0
    g27: LineSegment StartX=-171.467 StartY=11.1212 StartZ=0 EndX=-168.827 EndY=20.9737 EndZ=0
    g28: LineSegment StartX=-168.827 StartY=20.9737 StartZ=0 EndX=-165.736 EndY=20.1454 EndZ=0
    g29: LineSegment StartX=-165.736 StartY=20.1454 StartZ=0 EndX=-168.376 EndY=10.293 EndZ=0
    g30: LineSegment StartX=191.9 StartY=-77.5 StartZ=0 EndX=188.044 EndY=-63.1077 EndZ=0
    g31: LineSegment StartX=188.044 StartY=-63.1077 StartZ=0 EndX=191.135 EndY=-62.2795 EndZ=0
    g32: LineSegment StartX=191.135 StartY=-62.2795 StartZ=0 EndX=188.495 EndY=-52.427 EndZ=0
    g33: LineSegment StartX=188.495 StartY=-52.427 StartZ=0 EndX=185.404 EndY=-53.2553 EndZ=0
    g34: LineSegment StartX=185.404 StartY=-53.2553 StartZ=0 EndX=188.044 EndY=-63.1077 EndZ=0
    g35: LineSegment StartX=185.404 StartY=-53.2553 StartZ=0 EndX=181.488 EndY=-38.6408 EndZ=0
    g36: LineSegment StartX=181.488 StartY=-38.6408 StartZ=0 EndX=184.579 EndY=-37.8126 EndZ=0
    g37: LineSegment StartX=184.579 StartY=-37.8126 StartZ=0 EndX=181.939 EndY=-27.9601 EndZ=0
    g38: LineSegment StartX=181.939 StartY=-27.9601 StartZ=0 EndX=178.848 EndY=-28.7884 EndZ=0
    g39: LineSegment StartX=178.848 StartY=-28.7884 StartZ=0 EndX=181.488 EndY=-38.6408 EndZ=0
    g40: LineSegment StartX=178.848 StartY=-28.7884 StartZ=0 EndX=174.932 EndY=-14.1739 EndZ=0
    g41: LineSegment StartX=174.932 StartY=-14.1739 StartZ=0 EndX=178.023 EndY=-13.3457 EndZ=0
    g42: LineSegment StartX=178.023 StartY=-13.3457 StartZ=0 EndX=175.383 EndY=-3.49324 EndZ=0
    g43: LineSegment StartX=175.383 StartY=-3.49324 StartZ=0 EndX=172.292 EndY=-4.32146 EndZ=0
    g44: LineSegment StartX=172.292 StartY=-4.32146 StartZ=0 EndX=174.932 EndY=-14.1739 EndZ=0
    g45: LineSegment StartX=172.292 StartY=-4.32146 StartZ=0 EndX=168.376 EndY=10.293 EndZ=0
    g46: LineSegment StartX=168.376 StartY=10.293 StartZ=0 EndX=171.467 EndY=11.1212 EndZ=0
    g47: LineSegment StartX=171.467 StartY=11.1212 StartZ=0 EndX=168.827 EndY=20.9737 EndZ=0
    g48: LineSegment StartX=168.827 StartY=20.9737 StartZ=0 EndX=165.736 EndY=20.1454 EndZ=0
    g49: LineSegment StartX=165.736 StartY=20.1454 StartZ=0 EndX=168.376 EndY=10.293 EndZ=0
    g50: LineSegment StartX=-188.044 StartY=-63.1077 StartZ=0 EndX=-191.9 EndY=-77.5 EndZ=0
    g51: LineSegment StartX=-169.847 StartY=29.5293 StartZ=0 EndX=-166.756 EndY=28.7011 EndZ=0
    g52: LineSegment StartX=-166.756 StartY=28.7011 StartZ=0 EndX=-168.361 EndY=22.7123 EndZ=0
    g53: LineSegment StartX=-168.361 StartY=22.7123 StartZ=0 EndX=-171.452 EndY=23.5406 EndZ=0
    g54: LineSegment StartX=-171.452 StartY=23.5406 StartZ=0 EndX=-169.847 EndY=29.5293 EndZ=0
    g55: LineSegment StartX=-176.059 StartY=6.34707 StartZ=0 EndX=-177.664 EndY=0.35833 EndZ=0
    g56: LineSegment StartX=-177.664 StartY=0.35833 StartZ=0 EndX=-174.573 EndY=-0.469891 EndZ=0
    g57: LineSegment StartX=-174.573 StartY=-0.469891 StartZ=0 EndX=-172.968 EndY=5.51885 EndZ=0
    g58: LineSegment StartX=-172.968 StartY=5.51885 StartZ=0 EndX=-176.059 EndY=6.34707 EndZ=0
    g59: LineSegment StartX=-172.968 StartY=5.51885 StartZ=0 EndX=-168.361 EndY=22.7123 EndZ=0
    g60: LineSegment StartX=172.968 StartY=5.51885 StartZ=0 EndX=174.573 EndY=-0.469891 EndZ=0
    g61: LineSegment StartX=174.573 StartY=-0.469891 StartZ=0 EndX=177.664 EndY=0.35833 EndZ=0
    g62: LineSegment StartX=177.664 StartY=0.35833 StartZ=0 EndX=176.059 EndY=6.34707 EndZ=0
    g63: LineSegment StartX=176.059 StartY=6.34707 StartZ=0 EndX=172.968 EndY=5.51885 EndZ=0
    g64: LineSegment StartX=172.968 StartY=5.51885 StartZ=0 EndX=168.361 EndY=22.7123 EndZ=0
    g65: LineSegment StartX=168.361 StartY=22.7123 StartZ=0 EndX=171.452 EndY=23.5406 EndZ=0
    g66: LineSegment StartX=171.452 StartY=23.5406 StartZ=0 EndX=169.847 EndY=29.5293 EndZ=0
    g67: LineSegment StartX=169.847 StartY=29.5293 StartZ=0 EndX=166.756 EndY=28.7011 EndZ=0
    g68: LineSegment StartX=166.756 StartY=28.7011 StartZ=0 EndX=168.361 EndY=22.7123 EndZ=0
    g69: LineSegment StartX=-189 StartY=-20.5 StartZ=0 EndX=-189 EndY=-35.5 EndZ=0
    g70: LineSegment StartX=-189 StartY=-35.5 StartZ=0 EndX=-185.8 EndY=-35.5 EndZ=0
    g71: LineSegment StartX=-185.8 StartY=-35.5 StartZ=0 EndX=-185.8 EndY=-20.5 EndZ=0
    g72: LineSegment StartX=185.8 StartY=-20.5 StartZ=0 EndX=185.8 EndY=-35.5 EndZ=0
    g73: LineSegment StartX=185.8 StartY=-35.5 StartZ=0 EndX=189 EndY=-35.5 EndZ=0
    g74: LineSegment StartX=189 StartY=-35.5 StartZ=0 EndX=189 EndY=-20.5 EndZ=0
    g75: LineSegment StartX=-185.8 StartY=-20.5 StartZ=0 EndX=-185.8 EndY=-11.3 EndZ=0
    g76: LineSegment StartX=-185.8 StartY=-11.3 StartZ=0 EndX=-195 EndY=-11.3 EndZ=0
    g77: LineSegment StartX=-195 StartY=-20.5 StartZ=0 EndX=-189 EndY=-20.5 EndZ=0
    g78: LineSegment StartX=-195 StartY=-20.5 StartZ=0 EndX=-195 EndY=-77.5 EndZ=0
    g79: LineSegment StartX=189 StartY=-20.5 StartZ=0 EndX=195 EndY=-20.5 EndZ=0
    g80: LineSegment StartX=195 StartY=-11.3 StartZ=0 EndX=185.8 EndY=-11.3 EndZ=0
    g81: LineSegment StartX=185.8 StartY=-11.3 StartZ=0 EndX=185.8 EndY=-20.5 EndZ=0
    g82: LineSegment StartX=195 StartY=-11.3 StartZ=0 EndX=195 EndY=14 EndZ=0
    g83: LineSegment StartX=-195 StartY=14 StartZ=0 EndX=-192 EndY=14 EndZ=0
    g84: LineSegment StartX=-192 StartY=14 StartZ=0 EndX=-192 EndY=17 EndZ=0
    g85: LineSegment StartX=-192 StartY=17 StartZ=0 EndX=-195 EndY=17 EndZ=0
    g86: LineSegment StartX=-195 StartY=14 StartZ=0 EndX=-195 EndY=-11.3 EndZ=0
    g87: LineSegment StartX=192 StartY=17 StartZ=0 EndX=192 EndY=14 EndZ=0
    g88: LineSegment StartX=192 StartY=14 StartZ=0 EndX=195 EndY=14 EndZ=0
    g89: LineSegment StartX=195 StartY=17 StartZ=0 EndX=192 EndY=17 EndZ=0
    g90: LineSegment StartX=195 StartY=17 StartZ=0 EndX=195 EndY=35.5 EndZ=0
    g91: LineSegment StartX=-155 StartY=26 StartZ=0 EndX=-155 EndY=18 EndZ=0
    g92: LineSegment StartX=-155 StartY=18 StartZ=0 EndX=155 EndY=18 EndZ=0
    g93: LineSegment StartX=155 StartY=18 StartZ=0 EndX=155 EndY=26 EndZ=0
    g94: LineSegment StartX=155 StartY=26 StartZ=0 EndX=-155 EndY=26 EndZ=0
    g95: LineSegment StartX=-155 StartY=-14 StartZ=0 EndX=-155 EndY=-22 EndZ=0
    g96: LineSegment StartX=155 StartY=-22 StartZ=0 EndX=155 EndY=-14 EndZ=0
    g97: LineSegment StartX=155 StartY=-14 StartZ=0 EndX=-155 EndY=-14 EndZ=0
    g98: LineSegment StartX=-155 StartY=-22 StartZ=0 EndX=155 EndY=-22 EndZ=0
    g99: LineSegment StartX=-155 StartY=-55 StartZ=0 EndX=-155 EndY=-63 EndZ=0
    g100: LineSegment StartX=155 StartY=-63 StartZ=0 EndX=155 EndY=-55 EndZ=0
    g101: LineSegment StartX=155 StartY=-55 StartZ=0 EndX=-155 EndY=-55 EndZ=0
    g102: LineSegment StartX=-155 StartY=-63 StartZ=0 EndX=155 EndY=-63 EndZ=0
    g103: LineSegment StartX=-70 StartY=15 StartZ=0 EndX=-70 EndY=13 EndZ=0
    g104: LineSegment StartX=-70 StartY=13 StartZ=0 EndX=-50 EndY=13 EndZ=0
    g105: LineSegment StartX=-50 StartY=13 StartZ=0 EndX=-50 EndY=15 EndZ=0
    g106: LineSegment StartX=-50 StartY=15 StartZ=0 EndX=-70 EndY=15 EndZ=0
    g107: LineSegment StartX=-70 StartY=31 StartZ=0 EndX=-70 EndY=29 EndZ=0
    g108: LineSegment StartX=-70 StartY=29 StartZ=0 EndX=-50 EndY=29 EndZ=0
    g109: LineSegment StartX=-50 StartY=29 StartZ=0 EndX=-50 EndY=31 EndZ=0
    g110: LineSegment StartX=-50 StartY=31 StartZ=0 EndX=-70 EndY=31 EndZ=0
    g111: LineSegment StartX=-70 StartY=-9 StartZ=0 EndX=-70 EndY=-11 EndZ=0
    g112: LineSegment StartX=-70 StartY=-11 StartZ=0 EndX=-50 EndY=-11 EndZ=0
    g113: LineSegment StartX=-50 StartY=-11 StartZ=0 EndX=-50 EndY=-9 EndZ=0
    g114: LineSegment StartX=-50 StartY=-9 StartZ=0 EndX=-70 EndY=-9 EndZ=0
    g115: LineSegment StartX=-70 StartY=-25 StartZ=0 EndX=-70 EndY=-27 EndZ=0
    g116: LineSegment StartX=-70 StartY=-27 StartZ=0 EndX=-50 EndY=-27 EndZ=0
    g117: LineSegment StartX=-50 StartY=-27 StartZ=0 EndX=-50 EndY=-25 EndZ=0
    g118: LineSegment StartX=-50 StartY=-25 StartZ=0 EndX=-70 EndY=-25 EndZ=0
    g119: LineSegment StartX=-70 StartY=-50 StartZ=0 EndX=-70 EndY=-52 EndZ=0
    g120: LineSegment StartX=-70 StartY=-52 StartZ=0 EndX=-50 EndY=-52 EndZ=0
    g121: LineSegment StartX=-50 StartY=-52 StartZ=0 EndX=-50 EndY=-50 EndZ=0
    g122: LineSegment StartX=-50 StartY=-50 StartZ=0 EndX=-70 EndY=-50 EndZ=0
    g123: LineSegment StartX=-70 StartY=-66 StartZ=0 EndX=-70 EndY=-68 EndZ=0
    g124: LineSegment StartX=-70 StartY=-68 StartZ=0 EndX=-50 EndY=-68 EndZ=0
    g125: LineSegment StartX=-50 StartY=-68 StartZ=0 EndX=-50 EndY=-66 EndZ=0
    g126: LineSegment StartX=-50 StartY=-66 StartZ=0 EndX=-70 EndY=-66 EndZ=0
    g127: LineSegment StartX=-50 StartY=29 StartZ=0 EndX=-50 EndY=15 EndZ=0
    g128: LineSegment StartX=-50 StartY=-11 StartZ=0 EndX=-50 EndY=-25 EndZ=0
    g129: LineSegment StartX=-50 StartY=-52 StartZ=0 EndX=-50 EndY=-66 EndZ=0
    g130: LineSegment StartX=-70 StartY=29 StartZ=0 EndX=-70 EndY=26 EndZ=0
    g131: LineSegment StartX=-70 StartY=18 StartZ=0 EndX=-70 EndY=15 EndZ=0
    g132: LineSegment StartX=-70 StartY=-11 StartZ=0 EndX=-70 EndY=-14 EndZ=0
    g133: LineSegment StartX=-70 StartY=-52 StartZ=0 EndX=-70 EndY=-55 EndZ=0
    g134: LineSegment StartX=70 StartY=15 StartZ=0 EndX=70 EndY=13 EndZ=0
    g135: LineSegment StartX=70 StartY=13 StartZ=0 EndX=50 EndY=13 EndZ=0
    g136: LineSegment StartX=50 StartY=13 StartZ=0 EndX=50 EndY=15 EndZ=0
    g137: LineSegment StartX=50 StartY=15 StartZ=0 EndX=70 EndY=15 EndZ=0
    g138: LineSegment StartX=70 StartY=31 StartZ=0 EndX=70 EndY=29 EndZ=0
    g139: LineSegment StartX=70 StartY=29 StartZ=0 EndX=50 EndY=29 EndZ=0
    g140: LineSegment StartX=50 StartY=29 StartZ=0 EndX=50 EndY=31 EndZ=0
    g141: LineSegment StartX=50 StartY=31 StartZ=0 EndX=70 EndY=31 EndZ=0
    g142: LineSegment StartX=70 StartY=-9 StartZ=0 EndX=70 EndY=-11 EndZ=0
    g143: LineSegment StartX=70 StartY=-11 StartZ=0 EndX=50 EndY=-11 EndZ=0
    g144: LineSegment StartX=50 StartY=-11 StartZ=0 EndX=50 EndY=-9 EndZ=0
    g145: LineSegment StartX=50 StartY=-9 StartZ=0 EndX=70 EndY=-9 EndZ=0
    g146: LineSegment StartX=70 StartY=-25 StartZ=0 EndX=70 EndY=-27 EndZ=0
    g147: LineSegment StartX=70 StartY=-27 StartZ=0 EndX=50 EndY=-27 EndZ=0
    g148: LineSegment StartX=50 StartY=-27 StartZ=0 EndX=50 EndY=-25 EndZ=0
    g149: LineSegment StartX=50 StartY=-25 StartZ=0 EndX=70 EndY=-25 EndZ=0
    g150: LineSegment StartX=70 StartY=-50 StartZ=0 EndX=70 EndY=-52 EndZ=0
    g151: LineSegment StartX=70 StartY=-52 StartZ=0 EndX=50 EndY=-52 EndZ=0
    g152: LineSegment StartX=50 StartY=-52 StartZ=0 EndX=50 EndY=-50 EndZ=0
    g153: LineSegment StartX=50 StartY=-50 StartZ=0 EndX=70 EndY=-50 EndZ=0
    g154: LineSegment StartX=70 StartY=-66 StartZ=0 EndX=70 EndY=-68 EndZ=0
    g155: LineSegment StartX=70 StartY=-68 StartZ=0 EndX=50 EndY=-68 EndZ=0
    g156: LineSegment StartX=50 StartY=-68 StartZ=0 EndX=50 EndY=-66 EndZ=0
    g157: LineSegment StartX=50 StartY=-66 StartZ=0 EndX=70 EndY=-66 EndZ=0
    g158: LineSegment StartX=50 StartY=29 StartZ=0 EndX=50 EndY=15 EndZ=0
    g159: LineSegment StartX=50 StartY=-11 StartZ=0 EndX=50 EndY=-25 EndZ=0
    g160: LineSegment StartX=50 StartY=-52 StartZ=0 EndX=50 EndY=-66 EndZ=0
    g161: LineSegment StartX=70 StartY=29 StartZ=0 EndX=70 EndY=26 EndZ=0
    g162: LineSegment StartX=70 StartY=18 StartZ=0 EndX=70 EndY=15 EndZ=0
    g163: LineSegment StartX=70 StartY=-11 StartZ=0 EndX=70 EndY=-14 EndZ=0
    g164: LineSegment StartX=70 StartY=-52 StartZ=0 EndX=70 EndY=-55 EndZ=0
    g165: LineSegment StartX=-162 StartY=35.5 StartZ=0 EndX=-185.8 EndY=35.5 EndZ=0
    g166: LineSegment StartX=-162 StartY=32.5 StartZ=0 EndX=-162 EndY=35.5 EndZ=0
    g167: LineSegment StartX=162 StartY=32.5 StartZ=0 EndX=-162 EndY=32.5 EndZ=0
    g168: LineSegment StartX=185.8 StartY=35.5 StartZ=0 EndX=162 EndY=35.5 EndZ=0
    g169: LineSegment StartX=162 StartY=35.5 StartZ=0 EndX=162 EndY=32.5 EndZ=0
  constraints (489):
    c: Coincident(g78,g1)
    c: Coincident(g1,g2)
    c: Coincident(g90,g3)
    c: Coincident(g10,g0)
    c: Vertical(g0)
    c: Vertical(g2)
    c: Horizontal(g3)
    c: Symmetric(g1,g78,g-2)
    c: DistanceX(g1,g1) = 390
    c: DistanceY(g2,g90) = 113
    c: DistanceY(g90) = 35.5
    c: Coincident(g4,g5)
    c: Coincident(g5,g6)
    c: Vertical(g4)
    c: Vertical(g6)
    c: Horizontal(g5)
    c: PointOnObject(g4,g3)
    c: Coincident(g7,g8)
    c: Coincident(g8,g9)
    c: Vertical(g7)
    c: Vertical(g9)
    c: Horizontal(g8)
    c: Equal(g8,g5)
    c: DistanceX(g5,g5) = 3.2
    c: DistanceX(g10,g10) = 6
    c: Coincident(g4,g10)
    c: Horizontal(g10)
    c: Coincident(g6,g165)
    c: Coincident(g168,g7)
    c: Horizontal(g7,g3)
    c: Equal(g3,g10)
    c: Coincident(g9,g3)
    c: DistanceY(g6,g6) = 15
    c: Equal(g7,g6)
    c: Coincident(g11,g12)
    c: Coincident(g12,g13)
    c: Coincident(g13,g14)
    c: Coincident(g13,g15)
    c: Coincident(g15,g16)
    c: Coincident(g16,g17)
    c: Coincident(g17,g18)
    c: Coincident(g18,g19)
    c: Coincident(g19,g15)
    c: Coincident(g18,g20)
    c: Coincident(g20,g21)
    c: Coincident(g21,g22)
    c: Coincident(g22,g23)
    c: Coincident(g23,g24)
    c: Coincident(g24,g20)
    c: Coincident(g23,g25)
    c: Coincident(g25,g26)
    c: Coincident(g26,g27)
    c: Coincident(g27,g28)
    c: Coincident(g28,g29)
    c: Coincident(g29,g25)
    c: Parallel(g29,g25)
    c: Parallel(g25,g24)
    c: Parallel(g24,g20)
    c: Parallel(g20,g19)
    c: Parallel(g19,g15)
    c: Parallel(g15,g14)
    c: Parallel(g14,g12)
    c: Parallel(g12,g17)
    c: Parallel(g17,g22)
    c: Parallel(g22,g27)
    c: Parallel(g23,g26)
    c: Parallel(g26,g28)
    c: Parallel(g28,g21)
    c: Parallel(g21,g18)
    c: Parallel(g18,g16)
    c: Parallel(g16,g13)
    c: Parallel(g13,g11)
    c: Equal(g13,g18)
    c: Equal(g18,g23)
    c: Equal(g23,g28)
    c: Equal(g15,g20)
    c: Equal(g20,g25)
    c: Equal(g29,g24)
    c: Equal(g24,g19)
    c: Equal(g19,g14)
    c: Distance(g11) = 3.2
    c: Coincident(g30,g31)
    c: Coincident(g31,g32)
    c: Coincident(g32,g33)
    c: Coincident(g33,g34)
    c: Coincident(g34,g30)
    c: Coincident(g33,g35)
    c: Coincident(g35,g36)
    c: Coincident(g36,g37)
    c: Coincident(g37,g38)
    c: Coincident(g38,g39)
    c: Coincident(g39,g35)
    c: Coincident(g38,g40)
    c: Coincident(g40,g41)
    c: Coincident(g41,g42)
    c: Coincident(g42,g43)
    c: Coincident(g43,g44)
    c: Coincident(g44,g40)
    c: Coincident(g43,g45)
    c: Coincident(g45,g46)
    c: Coincident(g46,g47)
    c: Coincident(g47,g48)
    c: Coincident(g48,g49)
    c: Coincident(g49,g45)
    c: Parallel(g49,g45)
    c: Parallel(g45,g44)
    c: Parallel(g40,g39)
    c: Parallel(g34,g30)
    c: Parallel(g34,g32)
    c: Parallel(g32,g37)
    c: Parallel(g37,g42)
    c: Parallel(g42,g47)
    c: Parallel(g43,g46)
    c: Parallel(g46,g48)
    c: Parallel(g48,g41)
    c: Parallel(g41,g38)
    c: Parallel(g38,g36)
    c: Parallel(g36,g33)
    c: Parallel(g33,g31)
    c: Perpendicular(g30,g31)
    c: Equal(g33,g38)
    c: Equal(g38,g43)
    c: Equal(g43,g48)
    c: Equal(g35,g40)
    c: Equal(g40,g45)
    c: Equal(g49,g44)
    c: Equal(g44,g39)
    c: Equal(g39,g34)
    c: Equal(g35,g15)
    c: Equal(g34,g14)
    c: Equal(g31,g11)
    c: Angle(g30) = 1.8326
    c: Distance(g14) = 10.2
    c: Distance(g25) = 15.13
    c: Parallel(g44,g40)
    c: Parallel(g35,g39)
    c: Parallel(g34,g35)
    c: Coincident(g14,g50)
    c: PointOnObject(g50,g1)
    c: DistanceX(g78,g50) = 3.1
    c: Distance(g50) = 14.9
    c: Parallel(g50,g14)
    c: Coincident(g11,g14)
    c: Perpendicular(g14,g11)
    c: Angle(g50) = -1.8326
    c: Symmetric(g50,g30,g-2)
    c: Equal(g30,g50)
    c: Coincident(g51,g52)
    c: Coincident(g52,g53)
    c: Coincident(g53,g54)
    c: Coincident(g54,g51)
    c: Coincident(g55,g56)
    c: Coincident(g56,g57)
    c: Coincident(g57,g58)
    c: Coincident(g58,g55)
    c: Coincident(g57,g59)
    c: Coincident(g59,g52)
    c: Parallel(g52,g59)
    c: Parallel(g59,g57)
    c: Equal(g57,g52)
    c: Parallel(g52,g54)
    c: Parallel(g54,g55)
    c: Parallel(g56,g58)
    c: Parallel(g58,g53)
    c: Parallel(g53,g51)
    c: Perpendicular(g52,g51)
    c: PointOnObject(g27,g59)
    c: Parallel(g59,g27)
    c: Distance(g52) = 6.2
    c: Equal(g58,g53)
    c: Equal(g53,g28)
    c: Distance(g59) = 17.8
    c: Distance(g52,g27) = 1.8
    c: Coincident(g60,g61)
    c: Coincident(g61,g62)
    c: Coincident(g62,g63)
    c: Coincident(g63,g60)
    c: Coincident(g60,g64)
    c: Coincident(g64,g65)
    c: Coincident(g65,g66)
    c: Coincident(g66,g67)
    c: Coincident(g67,g68)
    c: Coincident(g68,g64)
    c: Parallel(g60,g64)
    c: Parallel(g64,g68)
    c: Parallel(g68,g62)
    c: Parallel(g62,g66)
    c: Parallel(g65,g63)
    c: Parallel(g63,g61)
    c: Parallel(g61,g67)
    c: Equal(g65,g63)
    c: Perpendicular(g68,g67)
    c: Equal(g65,g48)
    c: PointOnObject(g47,g64)
    c: Parallel(g64,g47)
    c: Equal(g62,g66)
    c: Equal(g64,g59)
    c: Equal(g52,g68)
    c: Horizontal(g67,g51)
    c: Coincident(g69,g70)
    c: Coincident(g70,g71)
    c: Vertical(g69)
    c: Vertical(g71)
    c: Horizontal(g70)
    c: Equal(g6,g69)
    c: Symmetric(g69,g4,g-1)
    c: Coincident(g72,g73)
    c: Coincident(g73,g74)
    c: Vertical(g72)
    c: Vertical(g74)
    c: Horizontal(g73)
    c: Equal(g9,g74)
    c: Symmetric(g8,g74,g-1)
    c: Coincident(g75,g76)
    c: Vertical(g75)
    c: Horizontal(g76)
    c: Horizontal(g77)
    c: Coincident(g75,g71)
    c: Equal(g76,g75)
    c: Coincident(g86,g76)
    c: Coincident(g77,g78)
    c: Coincident(g77,g69)
    c: Equal(g71,g69)
    c: Vertical(g77,g86)
    c: Vertical(g78)
    c: Vertical(g5,g75)
    c: Coincident(g80,g81)
    c: Horizontal(g79)
    c: Horizontal(g80)
    c: Vertical(g81)
    c: Coincident(g81,g72)
    c: Equal(g81,g80)
    c: Coincident(g80,g82)
    c: Vertical(g82)
    c: Vertical(g80,g2)
    c: Coincident(g74,g79)
    c: Coincident(g79,g2)
    c: Vertical(g80,g7)
    c: Horizontal(g74,g72)
    c: Coincident(g83,g84)
    c: Coincident(g84,g85)
    c: Vertical(g84)
    c: Horizontal(g83)
    c: Horizontal(g85)
    c: Equal(g83,g84)
    c: Equal(g84,g85)
    c: Vertical(g86)
    c: Coincident(g86,g83)
    c: Coincident(g0,g85)
    c: DistanceX(g83,g83) = 3
    c: DistanceY(g0,g0) = 18.5
    c: Coincident(g87,g88)
    c: Coincident(g89,g87)
    c: Vertical(g87)
    c: Horizontal(g88)
    c: Horizontal(g89)
    c: Equal(g89,g87)
    c: Equal(g88,g83)
    c: Coincident(g89,g90)
    c: Coincident(g88,g82)
    c: Equal(g87,g88)
    c: Equal(g0,g90)
    c: Vertical(g90)
    c: Coincident(g91,g92)
    c: Coincident(g92,g93)
    c: Coincident(g93,g94)
    c: Coincident(g94,g91)
    c: Vertical(g91)
    c: Vertical(g93)
    c: Horizontal(g94)
    c: Symmetric(g91,g92,g-2)
    c: DistanceY(g93,g93) = 8
    c: DistanceX(g94,g94) = 310
    c: DistanceY(g92) = 18
    c: Coincident(g95,g98)
    c: Coincident(g99,g102)
    c: Coincident(g98,g96)
    c: Coincident(g102,g100)
    c: Coincident(g96,g97)
    c: Coincident(g100,g101)
    c: Coincident(g97,g95)
    c: Coincident(g101,g99)
    c: Vertical(g95)
    c: Vertical(g99)
    c: Vertical(g96)
    c: Vertical(g100)
    c: Horizontal(g97)
    c: Horizontal(g101)
    c: DistanceY(g96,g96) = 8
    c: DistanceY(g100,g100) = 8
    c: Equal(g101,g97)
    c: Equal(g97,g94)
    c: Vertical(g91,g95)
    c: Vertical(g95,g99)
    c: Equal(g99,g95)
    c: Equal(g95,g91)
    c: DistanceY(g96) = -14
    c: DistanceY(g100) = -55
    c: Coincident(g103,g104)
    c: Coincident(g104,g105)
    c: Coincident(g105,g106)
    c: Coincident(g106,g103)
    c: Vertical(g103)
    c: Vertical(g105)
    c: Horizontal(g104)
    c: Horizontal(g106)
    c: Coincident(g107,g108)
    c: Coincident(g108,g109)
    c: Coincident(g109,g110)
    c: Coincident(g110,g107)
    c: Vertical(g107)
    c: Vertical(g109)
    c: Horizontal(g108)
    c: Horizontal(g110)
    c: Coincident(g111,g112)
    c: Coincident(g112,g113)
    c: Coincident(g113,g114)
    c: Coincident(g114,g111)
    c: Vertical(g111)
    c: Vertical(g113)
    c: Horizontal(g112)
    c: Horizontal(g114)
    c: Coincident(g115,g116)
    c: Coincident(g116,g117)
    c: Coincident(g117,g118)
    c: Coincident(g118,g115)
    c: Vertical(g115)
    c: Vertical(g117)
    c: Horizontal(g116)
    c: Horizontal(g118)
    c: Coincident(g119,g120)
    c: Coincident(g120,g121)
    c: Coincident(g121,g122)
    c: Coincident(g122,g119)
    c: Vertical(g119)
    c: Vertical(g121)
    c: Horizontal(g120)
    c: Horizontal(g122)
    c: Coincident(g123,g124)
    c: Coincident(g124,g125)
    c: Coincident(g125,g126)
    c: Coincident(g126,g123)
    c: Vertical(g123)
    c: Vertical(g125)
    c: Horizontal(g124)
    c: Horizontal(g126)
    c: Equal(g125,g121)
    c: Equal(g121,g117)
    c: Equal(g117,g113)
    c: Equal(g113,g105)
    c: Equal(g105,g109)
    c: DistanceY(g109,g109) = 2
    c: Equal(g110,g106)
    c: Equal(g106,g114)
    c: Equal(g114,g118)
    c: Equal(g118,g122)
    c: Equal(g122,g126)
    c: DistanceX(g110,g110) = 20
    c: Vertical(g105,g108)
    c: DistanceY(g105,g108) = 14
    c: Coincident(g108,g127)
    c: Coincident(g112,g128)
    c: Vertical(g128)
    c: Coincident(g120,g129)
    c: Coincident(g129,g125)
    c: Vertical(g129)
    c: Equal(g129,g128)
    c: Equal(g128,g127)
    c: Vertical(g104,g113)
    c: Coincident(g117,g128)
    c: Vertical(g116,g121)
    c: Coincident(g107,g130)
    c: Vertical(g130)
    c: Coincident(g131,g103)
    c: Vertical(g131)
    c: Equal(g131,g130)
    c: Coincident(g111,g132)
    c: Vertical(g132)
    c: Coincident(g119,g133)
    c: Vertical(g133)
    c: Equal(g133,g132)
    c: Equal(g132,g131)
    c: Coincident(g105,g127)
    c: PointOnObject(g130,g94)
    c: PointOnObject(g131,g92)
    c: PointOnObject(g132,g97)
    c: DistanceX(g109) = -50
    c: PointOnObject(g133,g101)
    c: Coincident(g134,g135)
    c: Coincident(g135,g136)
    c: Coincident(g136,g137)
    c: Coincident(g137,g134)
    c: Vertical(g134)
    c: Vertical(g136)
    c: Horizontal(g135)
    c: Horizontal(g137)
    c: Coincident(g138,g139)
    c: Coincident(g139,g140)
    c: Coincident(g140,g141)
    c: Coincident(g141,g138)
    c: Vertical(g138)
    c: Vertical(g140)
    c: Horizontal(g139)
    c: Horizontal(g141)
    c: Coincident(g142,g143)
    c: Coincident(g143,g144)
    c: Coincident(g144,g145)
    c: Coincident(g145,g142)
    c: Vertical(g142)
    c: Vertical(g144)
    c: Horizontal(g143)
    c: Horizontal(g145)
    c: Coincident(g146,g147)
    c: Coincident(g147,g148)
    c: Coincident(g148,g149)
    c: Coincident(g149,g146)
    c: Vertical(g146)
    c: Vertical(g148)
    c: Horizontal(g147)
    c: Horizontal(g149)
    c: Coincident(g150,g151)
    c: Coincident(g151,g152)
    c: Coincident(g152,g153)
    c: Coincident(g153,g150)
    c: Vertical(g150)
    c: Vertical(g152)
    c: Horizontal(g151)
    c: Horizontal(g153)
    c: Coincident(g154,g155)
    c: Coincident(g155,g156)
    c: Coincident(g156,g157)
    c: Coincident(g157,g154)
    c: Vertical(g154)
    c: Vertical(g156)
    c: Horizontal(g155)
    c: Horizontal(g157)
    c: Equal(g156,g152)
    c: Equal(g152,g148)
    c: Equal(g148,g144)
    c: Equal(g144,g136)
    c: Equal(g136,g140)
    c: Equal(g141,g137)
    c: Equal(g137,g145)
    c: Equal(g145,g149)
    c: Equal(g149,g153)
    c: Equal(g153,g157)
    c: Coincident(g139,g158)
    c: Coincident(g143,g159)
    c: Vertical(g159)
    c: Coincident(g151,g160)
    c: Coincident(g160,g156)
    c: Vertical(g160)
    c: Equal(g160,g159)
    c: Equal(g159,g158)
    c: Coincident(g148,g159)
    c: Coincident(g138,g161)
    c: Vertical(g161)
    c: Coincident(g162,g134)
    c: Vertical(g162)
    c: Equal(g162,g161)
    c: Coincident(g142,g163)
    c: Vertical(g163)
    c: Coincident(g150,g164)
    c: Vertical(g164)
    c: Equal(g164,g163)
    c: Equal(g163,g162)
    c: Coincident(g136,g158)
    c: PointOnObject(g161,g94)
    c: PointOnObject(g162,g92)
    c: PointOnObject(g163,g97)
    c: PointOnObject(g164,g101)
    c: Vertical(g150,g146)
    c: Vertical(g134,g142)
    c: Vertical(g158)
    c: Equal(g141,g110)
    c: Symmetric(g109,g140,g-2)
    c: Equal(g158,g127)
    c: Coincident(g166,g165)
    c: Horizontal(g165)
    c: Coincident(g167,g166)
    c: Coincident(g169,g167)
    c: Horizontal(g167)
    c: Coincident(g168,g169)
    c: Horizontal(g168)
    c: Vertical(g166)
    c: Vertical(g169)
    c: DistanceY(g169,g169) = 3
    c: Symmetric(g168,g165,g-2)
    c: DistanceX(g167,g167) = 324
FEATURE [PartDesign::Pad] Pad059
  Direction = (0,0,1)
  Length = 3
  Length2 = 10
  Profile = -> Sketch126
  ReferenceAxis = -> Sketch126 [N_Axis]
  Suppressed = false
  Type = 0
FEATURE [PartDesign::Body] Body060  label="Floor3mmB"
  AllowCompound = false
  Group = -> [Sketch126,Pad059]
  Origin = -> Origin065
  Placement = pos=(0,0,100) rot=(0,0,1;0rad)
  Tip = -> Pad059
FEATURE [Sketcher::SketchObject] Sketch127
  AttachmentSupport = -> [XY_Plane066]
  FullyConstrained = true
  MapMode = 5
  expr: Constraints[10] = Sketch126.Constraints[10]
  expr: Constraints[132] = Sketch126.Constraints[131]
  expr: Constraints[133] = Sketch126.Constraints[132]
  expr: Constraints[134] = Sketch126.Constraints[133]
  expr: Constraints[140] = Sketch126.Constraints[139]
  expr: Constraints[141] = Sketch126.Constraints[140]
  expr: Constraints[145] = Sketch126.Constraints[144]
  expr: Constraints[169] = Sketch126.Constraints[168]
  expr: Constraints[172] = Sketch126.Constraints[171]
  expr: Constraints[173] = Sketch126.Constraints[172]
  expr: Constraints[209] = Sketch126.Constraints[249]
  expr: Constraints[210] = Sketch126.Constraints[250]
  expr: Constraints[229] = Sketch126.Constraints[271]
  expr: Constraints[230] = Sketch126.Constraints[272]
  expr: Constraints[231] = Sketch126.Constraints[273]
  expr: Constraints[23] = Sketch126.Constraints[23]
  expr: Constraints[244] = Sketch126.Constraints[288]
  expr: Constraints[245] = Sketch126.Constraints[289]
  expr: Constraints[24] = Sketch126.Constraints[24]
  expr: Constraints[250] = Sketch126.Constraints[296]
  expr: Constraints[251] = Sketch126.Constraints[297]
  expr: Constraints[33] = Sketch126.Constraints[32]
  expr: Constraints[81] = Sketch126.Constraints[80]
  expr: Constraints[8] = Sketch126.Constraints[8]
  expr: Constraints[9] = Sketch126.Constraints[9]
  sketch-geometry (128):
    g0: LineSegment StartX=-195 StartY=35.5 StartZ=0 EndX=-195 EndY=17 EndZ=0
    g1: LineSegment StartX=-195 StartY=-77.5 StartZ=0 EndX=195 EndY=-77.5 EndZ=0
    g2: LineSegment StartX=195 StartY=-77.5 StartZ=0 EndX=195 EndY=14 EndZ=0
    g3: LineSegment StartX=195 StartY=35.5 StartZ=0 EndX=189 EndY=35.5 EndZ=0
    g4: LineSegment StartX=-189 StartY=35.5 StartZ=0 EndX=-189 EndY=20.5 EndZ=0
    g5: LineSegment StartX=-189 StartY=20.5 StartZ=0 EndX=-185.8 EndY=20.5 EndZ=0
    g6: LineSegment StartX=-185.8 StartY=20.5 StartZ=0 EndX=-185.8 EndY=35.5 EndZ=0
    g7: LineSegment StartX=185.8 StartY=35.5 StartZ=0 EndX=185.8 EndY=20.5 EndZ=0
    g8: LineSegment StartX=185.8 StartY=20.5 StartZ=0 EndX=189 EndY=20.5 EndZ=0
    g9: LineSegment StartX=189 StartY=20.5 StartZ=0 EndX=189 EndY=35.5 EndZ=0
    g10: LineSegment StartX=-189 StartY=35.5 StartZ=0 EndX=-195 EndY=35.5 EndZ=0
    g11: LineSegment StartX=185.8 StartY=35.5 StartZ=0 EndX=-185.8 EndY=35.5 EndZ=0
    g12: LineSegment StartX=-188.044 StartY=-63.1077 StartZ=0 EndX=-191.135 EndY=-62.2795 EndZ=0
    g13: LineSegment StartX=-191.135 StartY=-62.2795 StartZ=0 EndX=-188.495 EndY=-52.427 EndZ=0
    g14: LineSegment StartX=-188.495 StartY=-52.427 StartZ=0 EndX=-185.404 EndY=-53.2553 EndZ=0
    g15: LineSegment StartX=-185.404 StartY=-53.2553 StartZ=0 EndX=-188.044 EndY=-63.1077 EndZ=0
    g16: LineSegment StartX=-185.404 StartY=-53.2553 StartZ=0 EndX=-181.488 EndY=-38.6408 EndZ=0
    g17: LineSegment StartX=-181.488 StartY=-38.6408 StartZ=0 EndX=-184.579 EndY=-37.8126 EndZ=0
    g18: LineSegment StartX=-184.579 StartY=-37.8126 StartZ=0 EndX=-181.939 EndY=-27.9601 EndZ=0
    g19: LineSegment StartX=-181.939 StartY=-27.9601 StartZ=0 EndX=-178.848 EndY=-28.7884 EndZ=0
    g20: LineSegment StartX=-178.848 StartY=-28.7884 StartZ=0 EndX=-181.488 EndY=-38.6408 EndZ=0
    g21: LineSegment StartX=-178.848 StartY=-28.7884 StartZ=0 EndX=-174.932 EndY=-14.1739 EndZ=0
    g22: LineSegment StartX=-174.932 StartY=-14.1739 StartZ=0 EndX=-178.023 EndY=-13.3457 EndZ=0
    g23: LineSegment StartX=-178.023 StartY=-13.3457 StartZ=0 EndX=-175.383 EndY=-3.49324 EndZ=0
    g24: LineSegment StartX=-175.383 StartY=-3.49324 StartZ=0 EndX=-172.292 EndY=-4.32146 EndZ=0
    g25: LineSegment StartX=-172.292 StartY=-4.32146 StartZ=0 EndX=-174.932 EndY=-14.1739 EndZ=0
    g26: LineSegment StartX=-172.292 StartY=-4.32146 StartZ=0 EndX=-168.376 EndY=10.293 EndZ=0
    g27: LineSegment StartX=-168.376 StartY=10.293 StartZ=0 EndX=-171.467 EndY=11.1212 EndZ=0
    g28: LineSegment StartX=-171.467 StartY=11.1212 StartZ=0 EndX=-168.827 EndY=20.9737 EndZ=0
    g29: LineSegment StartX=-168.827 StartY=20.9737 StartZ=0 EndX=-165.736 EndY=20.1454 EndZ=0
    g30: LineSegment StartX=-165.736 StartY=20.1454 StartZ=0 EndX=-168.376 EndY=10.293 EndZ=0
    g31: LineSegment StartX=191.9 StartY=-77.5 StartZ=0 EndX=188.044 EndY=-63.1077 EndZ=0
    g32: LineSegment StartX=188.044 StartY=-63.1077 StartZ=0 EndX=191.135 EndY=-62.2795 EndZ=0
    g33: LineSegment StartX=191.135 StartY=-62.2795 StartZ=0 EndX=188.495 EndY=-52.427 EndZ=0
    g34: LineSegment StartX=188.495 StartY=-52.427 StartZ=0 EndX=185.404 EndY=-53.2553 EndZ=0
    g35: LineSegment StartX=185.404 StartY=-53.2553 StartZ=0 EndX=188.044 EndY=-63.1077 EndZ=0
    g36: LineSegment StartX=185.404 StartY=-53.2553 StartZ=0 EndX=181.488 EndY=-38.6408 EndZ=0
    g37: LineSegment StartX=181.488 StartY=-38.6408 StartZ=0 EndX=184.579 EndY=-37.8126 EndZ=0
    g38: LineSegment StartX=184.579 StartY=-37.8126 StartZ=0 EndX=181.939 EndY=-27.9601 EndZ=0
    g39: LineSegment StartX=181.939 StartY=-27.9601 StartZ=0 EndX=178.848 EndY=-28.7884 EndZ=0
    g40: LineSegment StartX=178.848 StartY=-28.7884 StartZ=0 EndX=181.488 EndY=-38.6408 EndZ=0
    g41: LineSegment StartX=178.848 StartY=-28.7884 StartZ=0 EndX=174.932 EndY=-14.1739 EndZ=0
    g42: LineSegment StartX=174.932 StartY=-14.1739 StartZ=0 EndX=178.023 EndY=-13.3457 EndZ=0
    g43: LineSegment StartX=178.023 StartY=-13.3457 StartZ=0 EndX=175.383 EndY=-3.49324 EndZ=0
    g44: LineSegment StartX=175.383 StartY=-3.49324 StartZ=0 EndX=172.292 EndY=-4.32146 EndZ=0
    g45: LineSegment StartX=172.292 StartY=-4.32146 StartZ=0 EndX=174.932 EndY=-14.1739 EndZ=0
    g46: LineSegment StartX=172.292 StartY=-4.32146 StartZ=0 EndX=168.376 EndY=10.293 EndZ=0
    g47: LineSegment StartX=168.376 StartY=10.293 StartZ=0 EndX=171.467 EndY=11.1212 EndZ=0
    g48: LineSegment StartX=171.467 StartY=11.1212 StartZ=0 EndX=168.827 EndY=20.9737 EndZ=0
    g49: LineSegment StartX=168.827 StartY=20.9737 StartZ=0 EndX=165.736 EndY=20.1454 EndZ=0
    g50: LineSegment StartX=165.736 StartY=20.1454 StartZ=0 EndX=168.376 EndY=10.293 EndZ=0
    g51: LineSegment StartX=-188.044 StartY=-63.1077 StartZ=0 EndX=-191.9 EndY=-77.5 EndZ=0
    g52: LineSegment StartX=-169.847 StartY=29.5293 StartZ=0 EndX=-166.756 EndY=28.7011 EndZ=0
    g53: LineSegment StartX=-166.756 StartY=28.7011 StartZ=0 EndX=-168.361 EndY=22.7123 EndZ=0
    g54: LineSegment StartX=-168.361 StartY=22.7123 StartZ=0 EndX=-171.452 EndY=23.5406 EndZ=0
    g55: LineSegment StartX=-171.452 StartY=23.5406 StartZ=0 EndX=-169.847 EndY=29.5293 EndZ=0
    g56: LineSegment StartX=-176.059 StartY=6.34707 StartZ=0 EndX=-177.664 EndY=0.35833 EndZ=0
    g57: LineSegment StartX=-177.664 StartY=0.35833 StartZ=0 EndX=-174.573 EndY=-0.469891 EndZ=0
    g58: LineSegment StartX=-174.573 StartY=-0.469891 StartZ=0 EndX=-172.968 EndY=5.51885 EndZ=0
    g59: LineSegment StartX=-172.968 StartY=5.51885 StartZ=0 EndX=-176.059 EndY=6.34707 EndZ=0
    g60: LineSegment StartX=-172.968 StartY=5.51885 StartZ=0 EndX=-168.361 EndY=22.7123 EndZ=0
    g61: LineSegment StartX=172.968 StartY=5.51885 StartZ=0 EndX=174.573 EndY=-0.469891 EndZ=0
    g62: LineSegment StartX=174.573 StartY=-0.469891 StartZ=0 EndX=177.664 EndY=0.35833 EndZ=0
    g63: LineSegment StartX=177.664 StartY=0.35833 StartZ=0 EndX=176.059 EndY=6.34707 EndZ=0
    g64: LineSegment StartX=176.059 StartY=6.34707 StartZ=0 EndX=172.968 EndY=5.51885 EndZ=0
    g65: LineSegment StartX=172.968 StartY=5.51885 StartZ=0 EndX=168.361 EndY=22.7123 EndZ=0
    g66: LineSegment StartX=168.361 StartY=22.7123 StartZ=0 EndX=171.452 EndY=23.5406 EndZ=0
    g67: LineSegment StartX=171.452 StartY=23.5406 StartZ=0 EndX=169.847 EndY=29.5293 EndZ=0
    g68: LineSegment StartX=169.847 StartY=29.5293 StartZ=0 EndX=166.756 EndY=28.7011 EndZ=0
    g69: LineSegment StartX=166.756 StartY=28.7011 StartZ=0 EndX=168.361 EndY=22.7123 EndZ=0
    g70: LineSegment StartX=-195 StartY=14 StartZ=0 EndX=-195 EndY=-77.5 EndZ=0
    g71: LineSegment StartX=-195 StartY=14 StartZ=0 EndX=-192 EndY=14 EndZ=0
    g72: LineSegment StartX=-192 StartY=14 StartZ=0 EndX=-192 EndY=17 EndZ=0
    g73: LineSegment StartX=-192 StartY=17 StartZ=0 EndX=-195 EndY=17 EndZ=0
    g74: LineSegment StartX=192 StartY=17 StartZ=0 EndX=192 EndY=14 EndZ=0
    g75: LineSegment StartX=192 StartY=14 StartZ=0 EndX=195 EndY=14 EndZ=0
    g76: LineSegment StartX=195 StartY=17 StartZ=0 EndX=192 EndY=17 EndZ=0
    g77: LineSegment StartX=195 StartY=17 StartZ=0 EndX=195 EndY=35.5 EndZ=0
    g78: LineSegment StartX=-155 StartY=26 StartZ=0 EndX=-155 EndY=18 EndZ=0
    g79: LineSegment StartX=155 StartY=18 StartZ=0 EndX=155 EndY=26 EndZ=0
    g80: LineSegment StartX=-155 StartY=-14 StartZ=0 EndX=-155 EndY=-22 EndZ=0
    g81: LineSegment StartX=155 StartY=-22 StartZ=0 EndX=155 EndY=-14 EndZ=0
    g82: LineSegment StartX=-155 StartY=-55 StartZ=0 EndX=-155 EndY=-63 EndZ=0
    g83: LineSegment StartX=155 StartY=-63 StartZ=0 EndX=155 EndY=-55 EndZ=0
    g84: LineSegment StartX=-189 StartY=35.5 StartZ=0 EndX=-185.8 EndY=35.5 EndZ=0
    g85: LineSegment StartX=185.8 StartY=35.5 StartZ=0 EndX=189 EndY=35.5 EndZ=0
    g86: LineSegment StartX=-70 StartY=26 StartZ=0 EndX=-155 EndY=26 EndZ=0
    g87: LineSegment StartX=-70 StartY=31 StartZ=0 EndX=-70 EndY=26 EndZ=0
    g88: LineSegment StartX=-155 StartY=18 StartZ=0 EndX=-70 EndY=18 EndZ=0
    g89: LineSegment StartX=-70 StartY=18 StartZ=0 EndX=-70 EndY=13 EndZ=0
    g90: LineSegment StartX=-70 StartY=-14 StartZ=0 EndX=-155 EndY=-14 EndZ=0
    g91: LineSegment StartX=-70 StartY=-9 StartZ=0 EndX=-70 EndY=-14 EndZ=0
    g92: LineSegment StartX=-155 StartY=-22 StartZ=0 EndX=-70 EndY=-22 EndZ=0
    g93: LineSegment StartX=-70 StartY=-22 StartZ=0 EndX=-70 EndY=-27 EndZ=0
    g94: LineSegment StartX=-70 StartY=-55 StartZ=0 EndX=-155 EndY=-55 EndZ=0
    g95: LineSegment StartX=-70 StartY=-50 StartZ=0 EndX=-70 EndY=-55 EndZ=0
    g96: LineSegment StartX=-155 StartY=-63 StartZ=0 EndX=-70 EndY=-63 EndZ=0
    g97: LineSegment StartX=-70 StartY=-63 StartZ=0 EndX=-70 EndY=-68 EndZ=0
    g98: LineSegment StartX=70 StartY=31 StartZ=0 EndX=-70 EndY=31 EndZ=0
    g99: LineSegment StartX=155 StartY=26 StartZ=0 EndX=70 EndY=26 EndZ=0
    g100: LineSegment StartX=70 StartY=26 StartZ=0 EndX=70 EndY=31 EndZ=0
    g101: LineSegment StartX=-70 StartY=13 StartZ=0 EndX=70 EndY=13 EndZ=0
    g102: LineSegment StartX=70 StartY=13 StartZ=0 EndX=70 EndY=18 EndZ=0
    g103: LineSegment StartX=70 StartY=18 StartZ=0 EndX=155 EndY=18 EndZ=0
    g104: LineSegment StartX=70 StartY=-9 StartZ=0 EndX=-70 EndY=-9 EndZ=0
    g105: LineSegment StartX=155 StartY=-14 StartZ=0 EndX=70 EndY=-14 EndZ=0
    g106: LineSegment StartX=70 StartY=-14 StartZ=0 EndX=70 EndY=-9 EndZ=0
    g107: LineSegment StartX=-70 StartY=-27 StartZ=0 EndX=70 EndY=-27 EndZ=0
    g108: LineSegment StartX=70 StartY=-27 StartZ=0 EndX=70 EndY=-22 EndZ=0
    g109: LineSegment StartX=70 StartY=-22 StartZ=0 EndX=155 EndY=-22 EndZ=0
    g110: LineSegment StartX=70 StartY=-50 StartZ=0 EndX=-70 EndY=-50 EndZ=0
    g111: LineSegment StartX=155 StartY=-55 StartZ=0 EndX=70 EndY=-55 EndZ=0
    g112: LineSegment StartX=70 StartY=-55 StartZ=0 EndX=70 EndY=-50 EndZ=0
    g113: LineSegment StartX=-70 StartY=-68 StartZ=0 EndX=70 EndY=-68 EndZ=0
    g114: LineSegment StartX=70 StartY=-68 StartZ=0 EndX=70 EndY=-63 EndZ=0
    g115: LineSegment StartX=70 StartY=-63 StartZ=0 EndX=155 EndY=-63 EndZ=0
    g116: LineSegment StartX=-125 StartY=3.6 StartZ=0 EndX=-125 EndY=0.4 EndZ=0
    g117: LineSegment StartX=-125 StartY=0.4 StartZ=0 EndX=125 EndY=0.4 EndZ=0
    g118: LineSegment StartX=125 StartY=0.4 StartZ=0 EndX=125 EndY=3.6 EndZ=0
    g119: LineSegment StartX=125 StartY=3.6 StartZ=0 EndX=-125 EndY=3.6 EndZ=0
    g120: LineSegment StartX=-125 StartY=3.6 StartZ=0 EndX=-125 EndY=18 EndZ=0
    g121: LineSegment StartX=-125 StartY=0.4 StartZ=0 EndX=-125 EndY=-14 EndZ=0
    g122: LineSegment StartX=-125 StartY=-36.9 StartZ=0 EndX=-125 EndY=-40.1 EndZ=0
    g123: LineSegment StartX=-125 StartY=-40.1 StartZ=0 EndX=125 EndY=-40.1 EndZ=0
    g124: LineSegment StartX=125 StartY=-40.1 StartZ=0 EndX=125 EndY=-36.9 EndZ=0
    g125: LineSegment StartX=125 StartY=-36.9 StartZ=0 EndX=-125 EndY=-36.9 EndZ=0
    g126: LineSegment StartX=-125 StartY=-36.9 StartZ=0 EndX=-125 EndY=-22 EndZ=0
    g127: LineSegment StartX=-125 StartY=-40.1 StartZ=0 EndX=-125 EndY=-55 EndZ=0
  constraints (369):
    c: Coincident(g70,g1)
    c: Coincident(g1,g2)
    c: Coincident(g77,g3)
    c: Coincident(g10,g0)
    c: Vertical(g0)
    c: Vertical(g2)
    c: Horizontal(g3)
    c: Symmetric(g1,g70,g-2)
    c: DistanceX(g1,g1) = 390
    c: DistanceY(g2,g77) = 113
    c: DistanceY(g77) = 35.5
    c: Coincident(g4,g5)
    c: Coincident(g5,g6)
    c: Vertical(g4)
    c: Vertical(g6)
    c: Horizontal(g5)
    c: PointOnObject(g4,g3)
    c: Coincident(g7,g8)
    c: Coincident(g8,g9)
    c: Vertical(g7)
    c: Vertical(g9)
    c: Horizontal(g8)
    c: Equal(g8,g5)
    c: DistanceX(g5,g5) = 3.2
    c: DistanceX(g10,g10) = 6
    c: Coincident(g4,g10)
    c: Horizontal(g10)
    c: Coincident(g6,g11)
    c: Coincident(g11,g7)
    c: Horizontal(g7,g3)
    c: Equal(g3,g10)
    c: Horizontal(g11)
    c: Coincident(g9,g3)
    c: DistanceY(g6,g6) = 15
    c: Equal(g7,g6)
    c: Coincident(g12,g13)
    c: Coincident(g13,g14)
    c: Coincident(g14,g15)
    c: Coincident(g14,g16)
    c: Coincident(g16,g17)
    c: Coincident(g17,g18)
    c: Coincident(g18,g19)
    c: Coincident(g19,g20)
    c: Coincident(g20,g16)
    c: Coincident(g19,g21)
    c: Coincident(g21,g22)
    c: Coincident(g22,g23)
    c: Coincident(g23,g24)
    c: Coincident(g24,g25)
    c: Coincident(g25,g21)
    c: Coincident(g24,g26)
    c: Coincident(g26,g27)
    c: Coincident(g27,g28)
    c: Coincident(g28,g29)
    c: Coincident(g29,g30)
    c: Coincident(g30,g26)
    c: Parallel(g30,g26)
    c: Parallel(g26,g25)
    c: Parallel(g25,g21)
    c: Parallel(g21,g20)
    c: Parallel(g20,g16)
    c: Parallel(g16,g15)
    c: Parallel(g15,g13)
    c: Parallel(g13,g18)
    c: Parallel(g18,g23)
    c: Parallel(g23,g28)
    c: Parallel(g24,g27)
    c: Parallel(g27,g29)
    c: Parallel(g29,g22)
    c: Parallel(g22,g19)
    c: Parallel(g19,g17)
    c: Parallel(g17,g14)
    c: Parallel(g14,g12)
    c: Equal(g14,g19)
    c: Equal(g19,g24)
    c: Equal(g24,g29)
    c: Equal(g16,g21)
    c: Equal(g21,g26)
    c: Equal(g30,g25)
    c: Equal(g25,g20)
    c: Equal(g20,g15)
    c: Distance(g12) = 3.2
    c: Coincident(g31,g32)
    c: Coincident(g32,g33)
    c: Coincident(g33,g34)
    c: Coincident(g34,g35)
    c: Coincident(g35,g31)
    c: Coincident(g34,g36)
    c: Coincident(g36,g37)
    c: Coincident(g37,g38)
    c: Coincident(g38,g39)
    c: Coincident(g39,g40)
    c: Coincident(g40,g36)
    c: Coincident(g39,g41)
    c: Coincident(g41,g42)
    c: Coincident(g42,g43)
    c: Coincident(g43,g44)
    c: Coincident(g44,g45)
    c: Coincident(g45,g41)
    c: Coincident(g44,g46)
    c: Coincident(g46,g47)
    c: Coincident(g47,g48)
    c: Coincident(g48,g49)
    c: Coincident(g49,g50)
    c: Coincident(g50,g46)
    c: Parallel(g50,g46)
    c: Parallel(g46,g45)
    c: Parallel(g41,g40)
    c: Parallel(g35,g31)
    c: Parallel(g35,g33)
    c: Parallel(g33,g38)
    c: Parallel(g38,g43)
    c: Parallel(g43,g48)
    c: Parallel(g44,g47)
    c: Parallel(g47,g49)
    c: Parallel(g49,g42)
    c: Parallel(g42,g39)
    c: Parallel(g39,g37)
    c: Parallel(g37,g34)
    c: Parallel(g34,g32)
    c: Perpendicular(g31,g32)
    c: Equal(g34,g39)
    c: Equal(g39,g44)
    c: Equal(g44,g49)
    c: Equal(g36,g41)
    c: Equal(g41,g46)
    c: Equal(g50,g45)
    c: Equal(g45,g40)
    c: Equal(g40,g35)
    c: Equal(g36,g16)
    c: Equal(g35,g15)
    c: Equal(g32,g12)
    c: Angle(g31) = 1.8326
    c: Distance(g15) = 10.2
    c: Distance(g26) = 15.13
    c: Parallel(g45,g41)
    c: Parallel(g36,g40)
    c: Parallel(g35,g36)
    c: Coincident(g15,g51)
    c: PointOnObject(g51,g1)
    c: DistanceX(g70,g51) = 3.1
    c: Distance(g51) = 14.9
    c: Parallel(g51,g15)
    c: Coincident(g12,g15)
    c: Perpendicular(g15,g12)
    c: Angle(g51) = -1.8326
    c: Symmetric(g51,g31,g-2)
    c: Equal(g31,g51)
    c: Coincident(g52,g53)
    c: Coincident(g53,g54)
    c: Coincident(g54,g55)
    c: Coincident(g55,g52)
    c: Coincident(g56,g57)
    c: Coincident(g57,g58)
    c: Coincident(g58,g59)
    c: Coincident(g59,g56)
    c: Coincident(g58,g60)
    c: Coincident(g60,g53)
    c: Parallel(g53,g60)
    c: Parallel(g60,g58)
    c: Equal(g58,g53)
    c: Parallel(g53,g55)
    c: Parallel(g55,g56)
    c: Parallel(g57,g59)
    c: Parallel(g59,g54)
    c: Parallel(g54,g52)
    c: Perpendicular(g53,g52)
    c: PointOnObject(g28,g60)
    c: Parallel(g60,g28)
    c: Distance(g53) = 6.2
    c: Equal(g59,g54)
    c: Equal(g54,g29)
    c: Distance(g60) = 17.8
    c: Distance(g53,g28) = 1.8
    c: Coincident(g61,g62)
    c: Coincident(g62,g63)
    c: Coincident(g63,g64)
    c: Coincident(g64,g61)
    c: Coincident(g61,g65)
    c: Coincident(g65,g66)
    c: Coincident(g66,g67)
    c: Coincident(g67,g68)
    c: Coincident(g68,g69)
    c: Coincident(g69,g65)
    c: Parallel(g61,g65)
    c: Parallel(g65,g69)
    c: Parallel(g69,g63)
    c: Parallel(g63,g67)
    c: Parallel(g66,g64)
    c: Parallel(g64,g62)
    c: Parallel(g62,g68)
    c: Equal(g66,g64)
    c: Perpendicular(g69,g68)
    c: Equal(g66,g49)
    c: PointOnObject(g48,g65)
    c: Parallel(g65,g48)
    c: Equal(g63,g67)
    c: Equal(g65,g60)
    c: Equal(g53,g69)
    c: Horizontal(g68,g52)
    c: Vertical(g70)
    c: Coincident(g71,g72)
    c: Coincident(g72,g73)
    c: Vertical(g72)
    c: Horizontal(g71)
    c: Horizontal(g73)
    c: Equal(g71,g72)
    c: Equal(g72,g73)
    c: Coincident(g0,g73)
    c: DistanceX(g71,g71) = 3
    c: DistanceY(g0,g0) = 18.5
    c: Coincident(g74,g75)
    c: Coincident(g76,g74)
    c: Vertical(g74)
    c: Horizontal(g75)
    c: Horizontal(g76)
    c: Equal(g76,g74)
    c: Equal(g75,g71)
    c: Coincident(g76,g77)
    c: Equal(g74,g75)
    c: Equal(g0,g77)
    c: Vertical(g77)
    c: Coincident(g78,g88)
    c: Coincident(g103,g79)
    c: Coincident(g79,g99)
    c: Coincident(g86,g78)
    c: Vertical(g78)
    c: Vertical(g79)
    c: Symmetric(g78,g103,g-2)
    c: DistanceY(g79,g79) = 8
    c: DistanceX(g86,g99) = 310
    c: DistanceY(g103) = 18
    c: Coincident(g80,g92)
    c: Coincident(g82,g96)
    c: Coincident(g109,g81)
    c: Coincident(g115,g83)
    c: Coincident(g81,g105)
    c: Coincident(g83,g111)
    c: Coincident(g90,g80)
    c: Coincident(g94,g82)
    c: Vertical(g80)
    c: Vertical(g82)
    c: Vertical(g81)
    c: Vertical(g83)
    c: DistanceY(g81,g81) = 8
    c: DistanceY(g83,g83) = 8
    c: Vertical(g78,g80)
    c: Vertical(g80,g82)
    c: Equal(g82,g80)
    c: Equal(g80,g78)
    c: DistanceY(g81) = -14
    c: DistanceY(g83) = -55
    c: Coincident(g70,g71)
    c: Coincident(g4,g84)
    c: Coincident(g84,g6)
    c: Coincident(g7,g85)
    c: Coincident(g85,g3)
    c: Coincident(g75,g2)
    c: Coincident(g87,g86)
    c: Horizontal(g86)
    c: Coincident(g98,g87)
    c: Coincident(g88,g89)
    c: Coincident(g89,g101)
    c: Coincident(g91,g90)
    c: Horizontal(g90)
    c: Coincident(g104,g91)
    c: Coincident(g92,g93)
    c: Coincident(g93,g107)
    c: Coincident(g95,g94)
    c: Horizontal(g94)
    c: Coincident(g110,g95)
    c: Coincident(g96,g97)
    c: Coincident(g97,g113)
    c: Coincident(g100,g98)
    c: Coincident(g99,g100)
    c: Horizontal(g99)
    c: Coincident(g101,g102)
    c: Coincident(g102,g103)
    c: Coincident(g106,g104)
    c: Horizontal(g104)
    c: Coincident(g105,g106)
    c: Horizontal(g105)
    c: Coincident(g107,g108)
    c: Coincident(g108,g109)
    c: Coincident(g112,g110)
    c: Horizontal(g110)
    c: Coincident(g111,g112)
    c: Horizontal(g111)
    c: Coincident(g113,g114)
    c: Coincident(g114,g115)
    c: Horizontal(g115)
    c: Horizontal(g113)
    c: Horizontal(g107)
    c: Horizontal(g109)
    c: Horizontal(g103)
    c: Horizontal(g101)
    c: Vertical(g100)
    c: Vertical(g102)
    c: Vertical(g106)
    c: Vertical(g108)
    c: Vertical(g112)
    c: Vertical(g114)
    c: Equal(g114,g112)
    c: Equal(g112,g108)
    c: Equal(g108,g106)
    c: Equal(g106,g102)
    c: Equal(g102,g100)
    c: Vertical(g99,g101)
    c: Vertical(g101,g105)
    c: Vertical(g105,g107)
    c: Vertical(g107,g111)
    c: Vertical(g111,g113)
    c: DistanceY(g100,g100) = 5
    c: Symmetric(g98,g87,g-2)
    c: DistanceX(g98,g98) = 140
    c: Vertical(g87)
    c: Vertical(g89)
    c: Vertical(g91)
    c: Vertical(g93)
    c: Vertical(g95)
    c: Vertical(g97)
    c: Equal(g98,g101)
    c: Equal(g101,g104)
    c: Equal(g104,g107)
    c: Equal(g107,g110)
    c: Equal(g110,g113)
    c: Horizontal(g96)
    c: Horizontal(g92)
    c: Horizontal(g88)
    c: Equal(g87,g91)
    c: Equal(g91,g93)
    c: Equal(g93,g95)
    c: Equal(g105,g103)
    c: Equal(g103,g111)
    c: Coincident(g116,g117)
    c: Coincident(g117,g118)
    c: Coincident(g118,g119)
    c: Coincident(g119,g116)
    c: Vertical(g116)
    c: Vertical(g118)
    c: Horizontal(g117)
    c: Distance(g116,g118) = 250
    c: Distance(g117,g119) = 3.2
    c: Symmetric(g116,g118,g-2)
    c: Coincident(g116,g120)
    c: PointOnObject(g120,g88)
    c: Vertical(g120)
    c: Coincident(g116,g121)
    c: PointOnObject(g121,g90)
    c: Vertical(g121)
    c: Equal(g121,g120)
    c: Coincident(g122,g123)
    c: Coincident(g123,g124)
    c: Coincident(g124,g125)
    c: Coincident(g125,g122)
    c: Vertical(g122)
    c: Vertical(g124)
    c: Horizontal(g123)
    c: Horizontal(g125)
    c: Equal(g125,g119)
    c: Equal(g116,g122)
    c: Vertical(g122,g116)
    c: Coincident(g122,g126)
    c: PointOnObject(g126,g92)
    c: Vertical(g126)
    c: Coincident(g122,g127)
    c: PointOnObject(g127,g94)
    c: Vertical(g127)
    c: Equal(g127,g126)
FEATURE [PartDesign::Pad] Pad060
  Direction = (0,0,1)
  Length = 3
  Length2 = 10
  Profile = -> Sketch127
  ReferenceAxis = -> Sketch127 [N_Axis]
  Suppressed = false
  Type = 0
FEATURE [PartDesign::Body] Body061  label="Floor3mmC"
  AllowCompound = false
  Group = -> [Sketch127,Pad060]
  Origin = -> Origin066
  Placement = pos=(0,0,103) rot=(0,0,1;0rad)
  Tip = -> Pad060
FEATURE [Sketcher::SketchObject] Sketch128
  AttachmentSupport = -> [XY_Plane067]
  FullyConstrained = true
  MapMode = 5
  expr: Constraints[129] = Sketch122.Constraints[131]
  expr: Constraints[130] = Sketch122.Constraints[132]
  expr: Constraints[131] = Sketch122.Constraints[133]
  expr: Constraints[137] = Sketch122.Constraints[139]
  expr: Constraints[138] = Sketch122.Constraints[140]
  expr: Constraints[142] = Sketch122.Constraints[144]
  expr: Constraints[166] = Sketch122.Constraints[168]
  expr: Constraints[169] = Sketch122.Constraints[171]
  expr: Constraints[170] = Sketch122.Constraints[172]
  expr: Constraints[198] = Sketch122.Constraints[239]
  expr: Constraints[199] = Sketch122.Constraints[240]
  expr: Constraints[200] = Sketch122.Constraints[241]
  expr: Constraints[20] = Sketch122.Constraints[23]
  expr: Constraints[21] = Sketch122.Constraints[24]
  expr: Constraints[30] = Sketch122.Constraints[32]
  expr: Constraints[5] = Sketch122.Constraints[8]
  expr: Constraints[6] = Sketch122.Constraints[9]
  expr: Constraints[78] = Sketch122.Constraints[80]
  expr: Constraints[7] = Sketch122.Constraints[10]
  sketch-geometry (79):
    g0: LineSegment StartX=-195 StartY=-77.5 StartZ=0 EndX=195 EndY=-77.5 EndZ=0
    g1: LineSegment StartX=195 StartY=-77.5 StartZ=0 EndX=195 EndY=35.5 EndZ=0
    g2: LineSegment StartX=195 StartY=35.5 StartZ=0 EndX=189 EndY=35.5 EndZ=0
    g3: LineSegment StartX=-189 StartY=35.5 StartZ=0 EndX=-189 EndY=20.5 EndZ=0
    g4: LineSegment StartX=-189 StartY=20.5 StartZ=0 EndX=-185.8 EndY=20.5 EndZ=0
    g5: LineSegment StartX=-185.8 StartY=20.5 StartZ=0 EndX=-185.8 EndY=35.5 EndZ=0
    g6: LineSegment StartX=185.8 StartY=35.5 StartZ=0 EndX=185.8 EndY=20.5 EndZ=0
    g7: LineSegment StartX=185.8 StartY=20.5 StartZ=0 EndX=189 EndY=20.5 EndZ=0
    g8: LineSegment StartX=189 StartY=20.5 StartZ=0 EndX=189 EndY=35.5 EndZ=0
    g9: LineSegment StartX=-189 StartY=35.5 StartZ=0 EndX=-195 EndY=35.5 EndZ=0
    g10: LineSegment StartX=185.8 StartY=35.5 StartZ=0 EndX=-185.8 EndY=35.5 EndZ=0
    g11: LineSegment StartX=-188.044 StartY=-63.1077 StartZ=0 EndX=-191.135 EndY=-62.2795 EndZ=0
    g12: LineSegment StartX=-191.135 StartY=-62.2795 StartZ=0 EndX=-188.495 EndY=-52.427 EndZ=0
    g13: LineSegment StartX=-188.495 StartY=-52.427 StartZ=0 EndX=-185.404 EndY=-53.2553 EndZ=0
    g14: LineSegment StartX=-185.404 StartY=-53.2553 StartZ=0 EndX=-188.044 EndY=-63.1077 EndZ=0
    g15: LineSegment StartX=-185.404 StartY=-53.2553 StartZ=0 EndX=-181.488 EndY=-38.6408 EndZ=0
    g16: LineSegment StartX=-181.488 StartY=-38.6408 StartZ=0 EndX=-184.579 EndY=-37.8126 EndZ=0
    g17: LineSegment StartX=-184.579 StartY=-37.8126 StartZ=0 EndX=-181.939 EndY=-27.9601 EndZ=0
    g18: LineSegment StartX=-181.939 StartY=-27.9601 StartZ=0 EndX=-178.848 EndY=-28.7884 EndZ=0
    g19: LineSegment StartX=-178.848 StartY=-28.7884 StartZ=0 EndX=-181.488 EndY=-38.6408 EndZ=0
    g20: LineSegment StartX=-178.848 StartY=-28.7884 StartZ=0 EndX=-174.932 EndY=-14.1739 EndZ=0
    g21: LineSegment StartX=-174.932 StartY=-14.1739 StartZ=0 EndX=-178.023 EndY=-13.3457 EndZ=0
    g22: LineSegment StartX=-178.023 StartY=-13.3457 StartZ=0 EndX=-175.383 EndY=-3.49324 EndZ=0
    g23: LineSegment StartX=-175.383 StartY=-3.49324 StartZ=0 EndX=-172.292 EndY=-4.32146 EndZ=0
    g24: LineSegment StartX=-172.292 StartY=-4.32146 StartZ=0 EndX=-174.932 EndY=-14.1739 EndZ=0
    g25: LineSegment StartX=-172.292 StartY=-4.32146 StartZ=0 EndX=-168.376 EndY=10.293 EndZ=0
    g26: LineSegment StartX=-168.376 StartY=10.293 StartZ=0 EndX=-171.467 EndY=11.1212 EndZ=0
    g27: LineSegment StartX=-171.467 StartY=11.1212 StartZ=0 EndX=-168.827 EndY=20.9737 EndZ=0
    g28: LineSegment StartX=-168.827 StartY=20.9737 StartZ=0 EndX=-165.736 EndY=20.1454 EndZ=0
    g29: LineSegment StartX=-165.736 StartY=20.1454 StartZ=0 EndX=-168.376 EndY=10.293 EndZ=0
    g30: LineSegment StartX=191.9 StartY=-77.5 StartZ=0 EndX=188.044 EndY=-63.1077 EndZ=0
    g31: LineSegment StartX=188.044 StartY=-63.1077 StartZ=0 EndX=191.135 EndY=-62.2795 EndZ=0
    g32: LineSegment StartX=191.135 StartY=-62.2795 StartZ=0 EndX=188.495 EndY=-52.427 EndZ=0
    g33: LineSegment StartX=188.495 StartY=-52.427 StartZ=0 EndX=185.404 EndY=-53.2553 EndZ=0
    g34: LineSegment StartX=185.404 StartY=-53.2553 StartZ=0 EndX=188.044 EndY=-63.1077 EndZ=0
    g35: LineSegment StartX=185.404 StartY=-53.2553 StartZ=0 EndX=181.488 EndY=-38.6408 EndZ=0
    g36: LineSegment StartX=181.488 StartY=-38.6408 StartZ=0 EndX=184.579 EndY=-37.8126 EndZ=0
    g37: LineSegment StartX=184.579 StartY=-37.8126 StartZ=0 EndX=181.939 EndY=-27.9601 EndZ=0
    g38: LineSegment StartX=181.939 StartY=-27.9601 StartZ=0 EndX=178.848 EndY=-28.7884 EndZ=0
    g39: LineSegment StartX=178.848 StartY=-28.7884 StartZ=0 EndX=181.488 EndY=-38.6408 EndZ=0
    g40: LineSegment StartX=178.848 StartY=-28.7884 StartZ=0 EndX=174.932 EndY=-14.1739 EndZ=0
    g41: LineSegment StartX=174.932 StartY=-14.1739 StartZ=0 EndX=178.023 EndY=-13.3457 EndZ=0
    g42: LineSegment StartX=178.023 StartY=-13.3457 StartZ=0 EndX=175.383 EndY=-3.49324 EndZ=0
    g43: LineSegment StartX=175.383 StartY=-3.49324 StartZ=0 EndX=172.292 EndY=-4.32146 EndZ=0
    g44: LineSegment StartX=172.292 StartY=-4.32146 StartZ=0 EndX=174.932 EndY=-14.1739 EndZ=0
    g45: LineSegment StartX=172.292 StartY=-4.32146 StartZ=0 EndX=168.376 EndY=10.293 EndZ=0
    g46: LineSegment StartX=168.376 StartY=10.293 StartZ=0 EndX=171.467 EndY=11.1212 EndZ=0
    g47: LineSegment StartX=171.467 StartY=11.1212 StartZ=0 EndX=168.827 EndY=20.9737 EndZ=0
    g48: LineSegment StartX=168.827 StartY=20.9737 StartZ=0 EndX=165.736 EndY=20.1454 EndZ=0
    g49: LineSegment StartX=165.736 StartY=20.1454 StartZ=0 EndX=168.376 EndY=10.293 EndZ=0
    g50: LineSegment StartX=-188.044 StartY=-63.1077 StartZ=0 EndX=-191.9 EndY=-77.5 EndZ=0
    g51: LineSegment StartX=-169.847 StartY=29.5293 StartZ=0 EndX=-166.756 EndY=28.7011 EndZ=0
    g52: LineSegment StartX=-166.756 StartY=28.7011 StartZ=0 EndX=-168.361 EndY=22.7123 EndZ=0
    g53: LineSegment StartX=-168.361 StartY=22.7123 StartZ=0 EndX=-171.452 EndY=23.5406 EndZ=0
    g54: LineSegment StartX=-171.452 StartY=23.5406 StartZ=0 EndX=-169.847 EndY=29.5293 EndZ=0
    g55: LineSegment StartX=-176.059 StartY=6.34707 StartZ=0 EndX=-177.664 EndY=0.35833 EndZ=0
    g56: LineSegment StartX=-177.664 StartY=0.35833 StartZ=0 EndX=-174.573 EndY=-0.469891 EndZ=0
    g57: LineSegment StartX=-174.573 StartY=-0.469891 StartZ=0 EndX=-172.968 EndY=5.51885 EndZ=0
    g58: LineSegment StartX=-172.968 StartY=5.51885 StartZ=0 EndX=-176.059 EndY=6.34707 EndZ=0
    g59: LineSegment StartX=-172.968 StartY=5.51885 StartZ=0 EndX=-168.361 EndY=22.7123 EndZ=0
    g60: LineSegment StartX=172.968 StartY=5.51885 StartZ=0 EndX=174.573 EndY=-0.469891 EndZ=0
    g61: LineSegment StartX=174.573 StartY=-0.469891 StartZ=0 EndX=177.664 EndY=0.35833 EndZ=0
    g62: LineSegment StartX=177.664 StartY=0.35833 StartZ=0 EndX=176.059 EndY=6.34707 EndZ=0
    g63: LineSegment StartX=176.059 StartY=6.34707 StartZ=0 EndX=172.968 EndY=5.51885 EndZ=0
    g64: LineSegment StartX=172.968 StartY=5.51885 StartZ=0 EndX=168.361 EndY=22.7123 EndZ=0
    g65: LineSegment StartX=168.361 StartY=22.7123 StartZ=0 EndX=171.452 EndY=23.5406 EndZ=0
    g66: LineSegment StartX=171.452 StartY=23.5406 StartZ=0 EndX=169.847 EndY=29.5293 EndZ=0
    g67: LineSegment StartX=169.847 StartY=29.5293 StartZ=0 EndX=166.756 EndY=28.7011 EndZ=0
    g68: LineSegment StartX=166.756 StartY=28.7011 StartZ=0 EndX=168.361 EndY=22.7123 EndZ=0
    g69: LineSegment StartX=-195 StartY=35.5 StartZ=0 EndX=-195 EndY=-77.5 EndZ=0
    g70: Circle CenterX=-180 CenterY=31.5 CenterZ=0 NormalX=0 NormalY=0 NormalZ=1 AngleXU=0 Radius=2
    g71: Circle CenterX=180 CenterY=31.5 CenterZ=0 NormalX=0 NormalY=0 NormalZ=1 AngleXU=0 Radius=2
    g72: Circle CenterX=0 CenterY=31.5 CenterZ=0 NormalX=0 NormalY=0 NormalZ=1 AngleXU=0 Radius=2
    g73: LineSegment StartX=-189 StartY=35.5 StartZ=0 EndX=-185.8 EndY=35.5 EndZ=0
    g74: LineSegment StartX=185.8 StartY=35.5 StartZ=0 EndX=189 EndY=35.5 EndZ=0
    g75: LineSegment StartX=-160 StartY=15.5 StartZ=0 EndX=-160 EndY=-57.5 EndZ=0
    g76: LineSegment StartX=-160 StartY=-57.5 StartZ=0 EndX=160 EndY=-57.5 EndZ=0
    g77: LineSegment StartX=160 StartY=-57.5 StartZ=0 EndX=160 EndY=15.5 EndZ=0
    g78: LineSegment StartX=160 StartY=15.5 StartZ=0 EndX=-160 EndY=15.5 EndZ=0
  constraints (224):
    c: Coincident(g69,g0)
    c: Coincident(g0,g1)
    c: Vertical(g1)
    c: Horizontal(g2)
    c: Symmetric(g0,g69,g-2)
    c: DistanceX(g0,g0) = 390
    c: DistanceY(g1,g2) = 113
    c: DistanceY(g2) = 35.5
    c: Coincident(g3,g4)
    c: Coincident(g4,g5)
    c: Vertical(g3)
    c: Vertical(g5)
    c: Horizontal(g4)
    c: PointOnObject(g3,g2)
    c: Coincident(g6,g7)
    c: Coincident(g7,g8)
    c: Vertical(g6)
    c: Vertical(g8)
    c: Horizontal(g7)
    c: Equal(g7,g4)
    c: DistanceX(g4,g4) = 3.2
    c: DistanceX(g9,g9) = 6
    c: Coincident(g3,g9)
    c: Horizontal(g9)
    c: Coincident(g5,g10)
    c: Coincident(g10,g6)
    c: Horizontal(g6,g2)
    c: Equal(g2,g9)
    c: Horizontal(g10)
    c: Coincident(g8,g2)
    c: DistanceY(g5,g5) = 15
    c: Equal(g6,g5)
    c: Coincident(g11,g12)
    c: Coincident(g12,g13)
    c: Coincident(g13,g14)
    c: Coincident(g13,g15)
    c: Coincident(g15,g16)
    c: Coincident(g16,g17)
    c: Coincident(g17,g18)
    c: Coincident(g18,g19)
    c: Coincident(g19,g15)
    c: Coincident(g18,g20)
    c: Coincident(g20,g21)
    c: Coincident(g21,g22)
    c: Coincident(g22,g23)
    c: Coincident(g23,g24)
    c: Coincident(g24,g20)
    c: Coincident(g23,g25)
    c: Coincident(g25,g26)
    c: Coincident(g26,g27)
    c: Coincident(g27,g28)
    c: Coincident(g28,g29)
    c: Coincident(g29,g25)
    c: Parallel(g29,g25)
    c: Parallel(g25,g24)
    c: Parallel(g24,g20)
    c: Parallel(g20,g19)
    c: Parallel(g19,g15)
    c: Parallel(g15,g14)
    c: Parallel(g14,g12)
    c: Parallel(g12,g17)
    c: Parallel(g17,g22)
    c: Parallel(g22,g27)
    c: Parallel(g23,g26)
    c: Parallel(g26,g28)
    c: Parallel(g28,g21)
    c: Parallel(g21,g18)
    c: Parallel(g18,g16)
    c: Parallel(g16,g13)
    c: Parallel(g13,g11)
    c: Equal(g13,g18)
    c: Equal(g18,g23)
    c: Equal(g23,g28)
    c: Equal(g15,g20)
    c: Equal(g20,g25)
    c: Equal(g29,g24)
    c: Equal(g24,g19)
    c: Equal(g19,g14)
    c: Distance(g11) = 3.2
    c: Coincident(g30,g31)
    c: Coincident(g31,g32)
    c: Coincident(g32,g33)
    c: Coincident(g33,g34)
    c: Coincident(g34,g30)
    c: Coincident(g33,g35)
    c: Coincident(g35,g36)
    c: Coincident(g36,g37)
    c: Coincident(g37,g38)
    c: Coincident(g38,g39)
    c: Coincident(g39,g35)
    c: Coincident(g38,g40)
    c: Coincident(g40,g41)
    c: Coincident(g41,g42)
    c: Coincident(g42,g43)
    c: Coincident(g43,g44)
    c: Coincident(g44,g40)
    c: Coincident(g43,g45)
    c: Coincident(g45,g46)
    c: Coincident(g46,g47)
    c: Coincident(g47,g48)
    c: Coincident(g48,g49)
    c: Coincident(g49,g45)
    c: Parallel(g49,g45)
    c: Parallel(g45,g44)
    c: Parallel(g40,g39)
    c: Parallel(g34,g30)
    c: Parallel(g34,g32)
    c: Parallel(g32,g37)
    c: Parallel(g37,g42)
    c: Parallel(g42,g47)
    c: Parallel(g43,g46)
    c: Parallel(g46,g48)
    c: Parallel(g48,g41)
    c: Parallel(g41,g38)
    c: Parallel(g38,g36)
    c: Parallel(g36,g33)
    c: Parallel(g33,g31)
    c: Perpendicular(g30,g31)
    c: Equal(g33,g38)
    c: Equal(g38,g43)
    c: Equal(g43,g48)
    c: Equal(g35,g40)
    c: Equal(g40,g45)
    c: Equal(g49,g44)
    c: Equal(g44,g39)
    c: Equal(g39,g34)
    c: Equal(g35,g15)
    c: Equal(g34,g14)
    c: Equal(g31,g11)
    c: Angle(g30) = 1.8326
    c: Distance(g14) = 10.2
    c: Distance(g25) = 15.13
    c: Parallel(g44,g40)
    c: Parallel(g35,g39)
    c: Parallel(g34,g35)
    c: Coincident(g14,g50)
    c: PointOnObject(g50,g0)
    c: DistanceX(g69,g50) = 3.1
    c: Distance(g50) = 14.9
    c: Parallel(g50,g14)
    c: Coincident(g11,g14)
    c: Perpendicular(g14,g11)
    c: Angle(g50) = -1.8326
    c: Symmetric(g50,g30,g-2)
    c: Equal(g30,g50)
    c: Coincident(g51,g52)
    c: Coincident(g52,g53)
    c: Coincident(g53,g54)
    c: Coincident(g54,g51)
    c: Coincident(g55,g56)
    c: Coincident(g56,g57)
    c: Coincident(g57,g58)
    c: Coincident(g58,g55)
    c: Coincident(g57,g59)
    c: Coincident(g59,g52)
    c: Parallel(g52,g59)
    c: Parallel(g59,g57)
    c: Equal(g57,g52)
    c: Parallel(g52,g54)
    c: Parallel(g54,g55)
    c: Parallel(g56,g58)
    c: Parallel(g58,g53)
    c: Parallel(g53,g51)
    c: Perpendicular(g52,g51)
    c: PointOnObject(g27,g59)
    c: Parallel(g59,g27)
    c: Distance(g52) = 6.2
    c: Equal(g58,g53)
    c: Equal(g53,g28)
    c: Distance(g59) = 17.8
    c: Distance(g52,g27) = 1.8
    c: Coincident(g60,g61)
    c: Coincident(g61,g62)
    c: Coincident(g62,g63)
    c: Coincident(g63,g60)
    c: Coincident(g60,g64)
    c: Coincident(g64,g65)
    c: Coincident(g65,g66)
    c: Coincident(g66,g67)
    c: Coincident(g67,g68)
    c: Coincident(g68,g64)
    c: Parallel(g60,g64)
    c: Parallel(g64,g68)
    c: Parallel(g68,g62)
    c: Parallel(g62,g66)
    c: Parallel(g65,g63)
    c: Parallel(g63,g61)
    c: Parallel(g61,g67)
    c: Equal(g65,g63)
    c: Perpendicular(g68,g67)
    c: Equal(g65,g48)
    c: PointOnObject(g47,g64)
    c: Parallel(g64,g47)
    c: Equal(g62,g66)
    c: Equal(g64,g59)
    c: Equal(g52,g68)
    c: Horizontal(g67,g51)
    c: Vertical(g69)
    c: Diameter(g70) = 4
    c: DistanceY(g70,g5) = 4
    c: DistanceX(g3,g70) = 9
    c: Equal(g71,g70)
    c: Symmetric(g70,g71,g-2)
    c: PointOnObject(g72,g-2)
    c: Equal(g72,g71)
    c: Horizontal(g71,g72)
    c: Coincident(g3,g73)
    c: Coincident(g73,g5)
    c: Coincident(g69,g9)
    c: Coincident(g2,g1)
    c: Coincident(g6,g74)
    c: Coincident(g74,g2)
    c: Coincident(g75,g76)
    c: Coincident(g76,g77)
    c: Coincident(g77,g78)
    c: Coincident(g78,g75)
    c: Vertical(g75)
    c: Vertical(g77)
    c: Horizontal(g76)
    c: Symmetric(g75,g77,g-2)
    c: DistanceX(g78,g78) = 320
    c: DistanceY(g75,g75) = 73
    c: DistanceY(g0,g76) = 20
    c: DistanceX(g70,g71) = 360
FEATURE [PartDesign::Pad] Pad061
  Direction = (0,0,1)
  Length = 3
  Length2 = 10
  Profile = -> Sketch128
  ReferenceAxis = -> Sketch128 [N_Axis]
  Reversed = true
  Suppressed = false
  Type = 0
FEATURE [PartDesign::Body] Body062  label="Floor3mmD"
  AllowCompound = false
  Group = -> [Sketch128,Pad061]
  Origin = -> Origin067
  Placement = pos=(0,0,-3) rot=(0,0,1;0rad)
  Tip = -> Pad061
FEATURE [Sketcher::SketchObject] Sketch129
  AttachmentSupport = -> [XZ_Plane068]
  FullyConstrained = true
  MapMode = 5
  Placement = pos=(0,0,0) rot=(1,0,0;1.5708rad)
  sketch-geometry (25):
    g0: LineSegment StartX=-161.5 StartY=102.9 StartZ=0 EndX=-161.5 EndY=-2.9 EndZ=0
    g1: LineSegment StartX=-161.5 StartY=-2.9 StartZ=0 EndX=-112.5 EndY=-2.9 EndZ=0
    g2: LineSegment StartX=-112.5 StartY=-2.9 StartZ=0 EndX=-112.5 EndY=23.7 EndZ=0
    g3: ArcOfCircle CenterX=-106.5 CenterY=23.7 CenterZ=0 NormalX=0 NormalY=0 NormalZ=1 AngleXU=0 Radius=6 StartAngle=1.38579 EndAngle=3.14159
    g4: LineSegment StartX=-105.396 StartY=29.5976 StartZ=0 EndX=-64.8 EndY=22 EndZ=0
    g5: LineSegment StartX=-22 StartY=0 StartZ=0 EndX=60.8 EndY=0 EndZ=0
    g6: LineSegment StartX=60.8 StartY=0 StartZ=0 EndX=60.8 EndY=21.3 EndZ=0
    g7: LineSegment StartX=60.8 StartY=21.3 StartZ=0 EndX=106.8 EndY=30.5 EndZ=0
    g8: LineSegment StartX=127.5 StartY=43.1 StartZ=0 EndX=153.5 EndY=43.1 EndZ=0
    g9: LineSegment StartX=153.5 StartY=43.1 StartZ=0 EndX=153.5 EndY=-2.9 EndZ=0
    g10: LineSegment StartX=153.5 StartY=-2.9 StartZ=0 EndX=161.5 EndY=-2.9 EndZ=0
    g11: LineSegment StartX=161.5 StartY=-2.9 StartZ=0 EndX=161.5 EndY=102.9 EndZ=0
    g12: LineSegment StartX=161.5 StartY=102.9 StartZ=0 EndX=-161.5 EndY=102.9 EndZ=0
    g13: LineSegment StartX=119 StartY=82 StartZ=0 EndX=119 EndY=62 EndZ=0
    g14: LineSegment StartX=119 StartY=62 StartZ=0 EndX=157 EndY=62 EndZ=0
    g15: LineSegment StartX=157 StartY=62 StartZ=0 EndX=157 EndY=82 EndZ=0
    g16: LineSegment StartX=157 StartY=82 StartZ=0 EndX=119 EndY=82 EndZ=0
    g17: LineSegment StartX=-64.8 StartY=22 StartZ=0 EndX=-64.8 EndY=6.5 EndZ=0
    g18: LineSegment StartX=-64.8 StartY=6.5 StartZ=0 EndX=-37.8 EndY=6.5 EndZ=0
    g19: LineSegment StartX=-37.8 StartY=6.5 StartZ=0 EndX=-33.8 EndY=10.5 EndZ=0
    g20: LineSegment StartX=-33.8 StartY=10.5 StartZ=0 EndX=-26.5 EndY=10.5 EndZ=0
    g21: LineSegment StartX=-26.5 StartY=10.5 StartZ=0 EndX=-22 EndY=6 EndZ=0
    g22: LineSegment StartX=-22 StartY=6 StartZ=0 EndX=-22 EndY=0 EndZ=0
    g23: LineSegment StartX=106.8 StartY=30.5 StartZ=0 EndX=127.5 EndY=30.5 EndZ=0
    g24: LineSegment StartX=127.5 StartY=30.5 StartZ=0 EndX=127.5 EndY=43.1 EndZ=0
  constraints (73):
    c: Vertical(g0)
    c: Coincident(g0,g1)
    c: Horizontal(g1)
    c: Coincident(g1,g2)
    c: Vertical(g2)
    c: Tangent(g2,g3) = 1.5708
    c: Tangent(g3,g4) = 1.5708
    c: Coincident(g4,g17)
    c: Coincident(g22,g5)
    c: Coincident(g5,g6)
    c: Vertical(g6)
    c: Coincident(g6,g7)
    c: Coincident(g7,g23)
    c: Coincident(g24,g8)
    c: Horizontal(g8)
    c: Coincident(g8,g9)
    c: Vertical(g9)
    c: Coincident(g9,g10)
    c: Coincident(g10,g11)
    c: Vertical(g11)
    c: Coincident(g11,g12)
    c: Coincident(g12,g0)
    c: Horizontal(g12)
    c: Horizontal(g5)
    c: Horizontal(g10)
    c: Coincident(g13,g14)
    c: Coincident(g14,g15)
    c: Coincident(g15,g16)
    c: Coincident(g16,g13)
    c: Vertical(g13)
    c: Vertical(g15)
    c: Horizontal(g14)
    c: Horizontal(g16)
    c: DistanceY(g11,g11) = 105.8
    c: Diameter(g3) = 12
    c: DistanceY(g2,g2) = 26.6
    c: Coincident(g17,g18)
    c: Vertical(g17)
    c: Coincident(g18,g19)
    c: Coincident(g19,g20)
    c: Coincident(g20,g21)
    c: Coincident(g21,g22)
    c: Vertical(g22)
    c: Horizontal(g18)
    c: DistanceX(g1,g5) = 90.5
    c: Perpendicular(g19,g21)
    c: Angle(g21) = -0.785398
    c: DistanceX(g5) = -22
    c: Horizontal(g20)
    c: DistanceY(g22,g22) = 6
    c: DistanceY(g20) = 10.5
    c: DistanceX(g20,g20) = 7.3
    c: DistanceY(g18) = 6.5
    c: DistanceX(g18,g18) = 27
    c: DistanceY(g17,g17) = 15.5
    c: DistanceX(g1,g1) = 49
    c: DistanceX(g5,g5) = 82.8
    c: DistanceY(g6,g6) = 21.3
    c: Coincident(g23,g24)
    c: Horizontal(g23)
    c: Vertical(g24)
    c: DistanceY(g23) = 30.5
    c: DistanceX(g7,g7) = 46
    c: Symmetric(g10,g0,g-2)
    c: DistanceX(g10,g10) = 8
    c: DistanceY(g9,g9) = 46
    c: DistanceX(g8,g8) = 26
    c: DistanceY(g13,g13) = 20
    c: DistanceX(g14,g14) = 38
    c: DistanceX(g13) = 119
    c: DistanceY(g13) = 62
    c: DistanceY(g9) = -2.9
    c: PointOnObject(g5,g-1)
FEATURE [PartDesign::Pad] Pad062
  Direction = (0,-1,2e-16)
  Length = 3
  Length2 = 10
  Placement = pos=(0,0,0) rot=(1,0,0;1.5708rad)
  Profile = -> Sketch129
  ReferenceAxis = -> Sketch129 [N_Axis]
  Suppressed = false
  Type = 0
FEATURE [PartDesign::Body] Body063  label="BackMirror"
  AllowCompound = false
  Group = -> [Sketch129,Pad062]
  Origin = -> Origin068
  Placement = pos=(0,35.5,0) rot=(0,0,1;0rad)
  Tip = -> Pad062
FEATURE [Sketcher::SketchObject] Sketch130
  AttachmentSupport = -> [YZ_Plane069]
  FullyConstrained = true
  MapMode = 5
  Placement = pos=(0,0,0) rot=(0.57735,0.57735,0.57735;2.0944rad)
  sketch-geometry (17):
    g0: LineSegment StartX=-1.8 StartY=-10 StartZ=0 EndX=0 EndY=-10 EndZ=0
    g1: LineSegment StartX=0 StartY=-10 StartZ=0 EndX=0 EndY=0 EndZ=0
    g2: LineSegment StartX=0 StartY=0 StartZ=0 EndX=3 EndY=0 EndZ=0
    g3: LineSegment StartX=3 StartY=0 StartZ=0 EndX=3 EndY=-3 EndZ=0
    g4: LineSegment StartX=5 StartY=-3 StartZ=0 EndX=5 EndY=2.5 EndZ=0
    g5: LineSegment StartX=5 StartY=2.5 StartZ=0 EndX=-1.8 EndY=2.5 EndZ=0
    g6: LineSegment StartX=3 StartY=-3 StartZ=0 EndX=2.75 EndY=-3.25 EndZ=0
    g7: LineSegment StartX=2.75 StartY=-3.25 StartZ=0 EndX=3 EndY=-3.5 EndZ=0
    g8: LineSegment StartX=3 StartY=-3.5 StartZ=0 EndX=5 EndY=-3.5 EndZ=0
    g9: LineSegment StartX=5 StartY=-3.5 StartZ=0 EndX=5.25 EndY=-3.25 EndZ=0
    g10: LineSegment StartX=5.25 StartY=-3.25 StartZ=0 EndX=5 EndY=-3 EndZ=0
    g11: LineSegment StartX=-1.8 StartY=2.5 StartZ=0 EndX=-2.3 EndY=2 EndZ=0
    g12: LineSegment StartX=-2.3 StartY=2 StartZ=0 EndX=-2.3 EndY=-9.5 EndZ=0
    g13: LineSegment StartX=-2.3 StartY=-9.5 StartZ=0 EndX=-1.8 EndY=-10 EndZ=0
    g14: LineSegment StartX=0 StartY=0 StartZ=0 EndX=-8 EndY=0 EndZ=0
    g15: LineSegment StartX=-5 StartY=2 StartZ=0 EndX=-3 EndY=2 EndZ=0
    g16: LineSegment StartX=-4 StartY=2 StartZ=0 EndX=-4 EndY=0 EndZ=0
  constraints (50):
    c: Coincident(g13,g0)
    c: PointOnObject(g0,g-2)
    c: Horizontal(g0)
    c: Coincident(g0,g1)
    c: Coincident(g1,g-1)
    c: Coincident(g1,g2)
    c: PointOnObject(g2,g-1)
    c: Coincident(g2,g3)
    c: Vertical(g3)
    c: Coincident(g3,g6)
    c: Coincident(g10,g4)
    c: Vertical(g4)
    c: Coincident(g4,g5)
    c: Coincident(g5,g11)
    c: Horizontal(g5)
    c: DistanceY(g3,g3) = 3
    c: DistanceX(g2,g2) = 3
    c: DistanceX(g6,g10) = 2
    c: Coincident(g6,g7)
    c: Coincident(g7,g8)
    c: Coincident(g8,g9)
    c: Horizontal(g8)
    c: Coincident(g9,g10)
    c: PointOnObject(g8,g4)
    c: Perpendicular(g7,g6)
    c: Perpendicular(g10,g9)
    c: Equal(g7,g6)
    c: Equal(g10,g9)
    c: DistanceY(g8,g4) = 0.5
    c: Horizontal(g4,g3)
    c: DistanceY(g4) = 2.5
    c: Coincident(g11,g12)
    c: Coincident(g12,g13)
    c: Vertical(g12)
    c: Vertical(g5,g0)
    c: Perpendicular(g13,g11)
    c: Equal(g13,g11)
    c: DistanceX(g11,g5) = 0.5
    c: DistanceX(g12,g0) = 2.3
    c: DistanceY(g0) = -10
    c: PointOnObject(g14,g-1)
    c: DistanceX(g14,g14) = 8
    c: Horizontal(g15)
    c: DistanceX(g15,g15) = 2
    c: PointOnObject(g16,g15)
    c: Symmetric(g14,g14,g16)
    c: Symmetric(g15,g15,g16)
    c: Coincident(g14,g1)
    c: Equal(g15,g16)
    c: Vertical(g7,g3)
FEATURE [PartDesign::Pad] Pad063
  Direction = (1,0,0)
  Length = 19
  Length2 = 10
  Placement = pos=(0,0,0) rot=(0.57735,0.57735,0.57735;2.0944rad)
  Profile = -> Sketch130
  ReferenceAxis = -> Sketch130 [N_Axis]
  Suppressed = false
  Type = 0
FEATURE [PartDesign::Body] Body064  label="Gleiter"
  AllowCompound = false
  Group = -> [Sketch130,Pad063]
  Origin = -> Origin069
  Placement = pos=(-69.5,26,103) rot=(0,0,1;0rad)
  Tip = -> Pad063
FEATURE [Sketcher::SketchObject] Sketch131
  AttachmentSupport = -> [XY_Plane070]
  FullyConstrained = true
  MapMode = 5
  sketch-geometry (12):
    g0: LineSegment StartX=9 StartY=35.5 StartZ=0 EndX=2 EndY=35.5 EndZ=0
    g1: LineSegment StartX=-3 StartY=30.5 StartZ=0 EndX=-3 EndY=-74.5 EndZ=0
    g2: LineSegment StartX=2 StartY=-79.5 StartZ=0 EndX=3.5 EndY=-79.5 EndZ=0
    g3: LineSegment StartX=3.5 StartY=-79.5 StartZ=0 EndX=3.5 EndY=-77.5 EndZ=0
    g4: LineSegment StartX=0 StartY=-74 StartZ=0 EndX=9 EndY=-40.4115 EndZ=0
    g5: LineSegment StartX=9 StartY=-40.4115 StartZ=0 EndX=9 EndY=35.5 EndZ=0
    g6: LineSegment StartX=3.5 StartY=-77.5 StartZ=0 EndX=0 EndY=-77.5 EndZ=0
    g7: LineSegment StartX=0 StartY=-77.5 StartZ=0 EndX=0 EndY=-74 EndZ=0
    g8: ArcOfCircle CenterX=2 CenterY=30.5 CenterZ=0 NormalX=0 NormalY=0 NormalZ=1 AngleXU=0 Radius=5 StartAngle=1.5708 EndAngle=3.14159
    g9: GeomPoint X=-3 Y=35.5 Z=0
    g10: ArcOfCircle CenterX=2 CenterY=-74.5 CenterZ=0 NormalX=0 NormalY=0 NormalZ=1 AngleXU=0 Radius=5 StartAngle=3.14159 EndAngle=4.71239
    g11: GeomPoint X=-3 Y=-79.5 Z=0
  constraints (32):
    c: Horizontal(g0)
    c: Vertical(g1)
    c: Horizontal(g2)
    c: Coincident(g2,g3)
    c: Coincident(g3,g6)
    c: PointOnObject(g7,g-2)
    c: Coincident(g7,g4)
    c: Coincident(g4,g5)
    c: Coincident(g5,g0)
    c: Vertical(g5)
    c: DistanceX(g9) = -3
    c: DistanceY(g9) = 35.5
    c: DistanceX(g0) = 9
    c: Angle(g4) = 1.309
    c: DistanceY(g7) = -74
    c: Coincident(g6,g7)
    c: PointOnObject(g6,g-2)
    c: DistanceY(g6) = -77.5
    c: Horizontal(g6)
    c: DistanceX(g6,g6) = 3.5
    c: Vertical(g3)
    c: DistanceY(g3,g3) = 2
    c: PointOnObject(g9,g0)
    c: PointOnObject(g9,g1)
    c: Tangent(g0,g8) = -1.5708
    c: Tangent(g1,g8) = -1.5708
    c: PointOnObject(g11,g1)
    c: PointOnObject(g11,g2)
    c: Tangent(g1,g10) = -1.5708
    c: Tangent(g2,g10) = -1.5708
    c: Equal(g10,g8)
    c: Radius(g8) = 5
FEATURE [PartDesign::Pad] Pad064
  Direction = (0,0,1)
  Length = 56.5
  Length2 = 58.5
  Midplane = true
  Profile = -> Sketch131
  ReferenceAxis = -> Sketch131 [N_Axis]
  Refine = true
  Suppressed = false
  Type = 4
FEATURE [Sketcher::SketchObject] Sketch132
  AttachmentOffset = pos=(0,0,-49.8) rot=(0,0,1;0rad)
  AttachmentSupport = -> [XY_Plane070]
  FullyConstrained = true
  MapMode = 5
  Placement = pos=(0,0,-49.8) rot=(0,0,1;0rad)
  sketch-geometry (12):
    g0: LineSegment StartX=0 StartY=35.5 StartZ=0 EndX=0 EndY=-77.5 EndZ=0
    g1: LineSegment StartX=0 StartY=-77.5 StartZ=0 EndX=10 EndY=-77.5 EndZ=0
    g2: LineSegment StartX=10 StartY=-77.5 StartZ=0 EndX=10 EndY=-35 EndZ=0
    g3: LineSegment StartX=10 StartY=35.5 StartZ=0 EndX=0 EndY=35.5 EndZ=0
    g4: LineSegment StartX=6.2 StartY=-27 StartZ=0 EndX=6.2 EndY=-35 EndZ=0
    g5: LineSegment StartX=6.2 StartY=-35 StartZ=0 EndX=10 EndY=-35 EndZ=0
    g6: LineSegment StartX=10 StartY=-27 StartZ=0 EndX=6.2 EndY=-27 EndZ=0
    g7: LineSegment StartX=6.2 StartY=28.6 StartZ=0 EndX=6.2 EndY=20.6 EndZ=0
    g8: LineSegment StartX=6.2 StartY=20.6 StartZ=0 EndX=10 EndY=20.6 EndZ=0
    g9: LineSegment StartX=10 StartY=28.6 StartZ=0 EndX=6.2 EndY=28.6 EndZ=0
    g10: LineSegment StartX=10 StartY=-27 StartZ=0 EndX=10 EndY=20.6 EndZ=0
    g11: LineSegment StartX=10 StartY=28.6 StartZ=0 EndX=10 EndY=35.5 EndZ=0
  constraints (36):
    c: Coincident(g0,g1)
    c: Coincident(g1,g2)
    c: Coincident(g11,g3)
    c: Coincident(g3,g0)
    c: Vertical(g0)
    c: Vertical(g2)
    c: Horizontal(g1)
    c: Horizontal(g3)
    c: PointOnObject(g0,g-2)
    c: DistanceX(g3,g3) = 10
    c: DistanceY(g0) = 35.5
    c: DistanceY(g0) = -77.5
    c: Coincident(g4,g5)
    c: Coincident(g6,g4)
    c: Vertical(g4)
    c: Horizontal(g5)
    c: Horizontal(g6)
    c: Coincident(g7,g8)
    c: Coincident(g9,g7)
    c: Vertical(g7)
    c: Horizontal(g8)
    c: Horizontal(g9)
    c: Equal(g6,g8)
    c: DistanceY(g5,g6) = 8
    c: Vertical(g4,g7)
    c: Coincident(g2,g5)
    c: Vertical(g6,g2)
    c: Equal(g7,g4)
    c: Coincident(g10,g8)
    c: Coincident(g11,g9)
    c: Equal(g9,g8)
    c: DistanceX(g7) = 6.2
    c: DistanceY(g7) = 20.6
    c: Vertical(g11)
    c: DistanceY(g4) = -27
    c: Coincident(g10,g6)
FEATURE [PartDesign::Pocket] Pocket053
  BaseFeature = -> Pad064
  Direction = (0,0,-1)
  Length = 7
  Length2 = 5
  Profile = -> Sketch132
  ReferenceAxis = -> Sketch132 [N_Axis]
  Refine = true
  Suppressed = false
  Type = 1
FEATURE [PartDesign::Mirrored] Mirrored004
  BaseFeature = -> Pocket053
  MirrorPlane = -> XY_Plane070
  Originals = -> [Pocket053]
  Refine = true
  Suppressed = false
  TransformMode = 0
FEATURE [Sketcher::SketchObject] Sketch133
  AttachmentSupport = -> [XZ_Plane070]
  FullyConstrained = true
  MapMode = 5
  Placement = pos=(0,0,0) rot=(1,0,0;1.5708rad)
  sketch-geometry (12):
    g0: LineSegment StartX=0 StartY=62.5 StartZ=0 EndX=0 EndY=52.5 EndZ=0
    g1: LineSegment StartX=0 StartY=52.5 StartZ=0 EndX=10 EndY=52.5 EndZ=0
    g2: LineSegment StartX=10 StartY=52.5 StartZ=0 EndX=10 EndY=62.5 EndZ=0
    g3: LineSegment StartX=10 StartY=62.5 StartZ=0 EndX=0 EndY=62.5 EndZ=0
    g4: LineSegment StartX=0 StartY=35.5825 StartZ=0 EndX=0 EndY=-35.5825 EndZ=0
    g5: LineSegment StartX=0 StartY=-35.5825 StartZ=0 EndX=10 EndY=-47.5 EndZ=0
    g6: LineSegment StartX=10 StartY=-47.5 StartZ=0 EndX=10 EndY=47.5 EndZ=0
    g7: LineSegment StartX=10 StartY=47.5 StartZ=0 EndX=0 EndY=35.5825 EndZ=0
    g8: LineSegment StartX=0 StartY=-62.5 StartZ=0 EndX=10 EndY=-62.5 EndZ=0
    g9: LineSegment StartX=10 StartY=-62.5 StartZ=0 EndX=10 EndY=-52.5 EndZ=0
    g10: LineSegment StartX=10 StartY=-52.5 StartZ=0 EndX=0 EndY=-52.5 EndZ=0
    g11: LineSegment StartX=0 StartY=-52.5 StartZ=0 EndX=0 EndY=-62.5 EndZ=0
  constraints (34):
    c: Coincident(g0,g1)
    c: Coincident(g1,g2)
    c: Coincident(g2,g3)
    c: Coincident(g3,g0)
    c: Vertical(g0)
    c: Vertical(g2)
    c: Horizontal(g1)
    c: Horizontal(g3)
    c: PointOnObject(g0,g-2)
    c: Equal(g1,g2)
    c: DistanceX(g1,g1) = 10
    c: Coincident(g4,g5)
    c: Coincident(g5,g6)
    c: Coincident(g6,g7)
    c: Coincident(g7,g4)
    c: Vertical(g6)
    c: PointOnObject(g4,g-2)
    c: Coincident(g8,g9)
    c: Coincident(g9,g10)
    c: Coincident(g10,g11)
    c: Coincident(g11,g8)
    c: Horizontal(g8)
    c: Horizontal(g10)
    c: Vertical(g9)
    c: Vertical(g11)
    c: Equal(g11,g8)
    c: Symmetric(g4,g4,g-1)
    c: Symmetric(g0,g10,g-1)
    c: DistanceY(g10,g0) = 105
    c: Angle(g-2,g5) = 0.698132
    c: Angle(g7,g-2) = 0.698132
    c: Vertical(g5,g9)
    c: Vertical(g6,g1)
    c: DistanceY(g6,g6) = 95
FEATURE [PartDesign::Pocket] Pocket054
  BaseFeature = -> Mirrored004
  Direction = (0,1,-2e-16)
  Length = 33
  Length2 = 76
  Midplane = true
  Profile = -> Sketch133
  ReferenceAxis = -> Sketch133 [N_Axis]
  Refine = true
  Suppressed = false
  Type = 4
FEATURE [Sketcher::SketchObject] Sketch134
  AttachmentSupport = -> [XY_Plane070]
  FullyConstrained = true
  MapMode = 5
  sketch-geometry (6):
    g0: LineSegment StartX=10 StartY=19 StartZ=0 EndX=2 EndY=19 EndZ=0
    g1: LineSegment StartX=2 StartY=19 StartZ=0 EndX=-1.53553 EndY=15.4645 EndZ=0
    g2: LineSegment StartX=-1.53553 StartY=15.4645 StartZ=0 EndX=-1.53553 EndY=-21.9645 EndZ=0
    g3: LineSegment StartX=-1.53553 StartY=-21.9645 StartZ=0 EndX=2 EndY=-25.5 EndZ=0
    g4: LineSegment StartX=2 StartY=-25.5 StartZ=0 EndX=10 EndY=-25.5 EndZ=0
    g5: LineSegment StartX=10 StartY=-25.5 StartZ=0 EndX=10 EndY=19 EndZ=0
  constraints (18):
    c: Coincident(g0,g1)
    c: Coincident(g1,g2)
    c: Coincident(g2,g3)
    c: Coincident(g3,g4)
    c: Coincident(g4,g5)
    c: Coincident(g5,g0)
    c: Vertical(g5)
    c: Equal(g1,g3)
    c: Vertical(g3,g0)
    c: Perpendicular(g3,g1)
    c: Horizontal(g4)
    c: DistanceX(g4) = 10
    c: Distance(g1) = 5
    c: Horizontal(g0)
    c: DistanceY(g0) = 19
    c: DistanceY(g5,g5) = 44.5
    c: DistanceX(g0) = 2
    c: Vertical(g2)
FEATURE [PartDesign::Pocket] Pocket055  label="SeilTasche"
  BaseFeature = -> Pocket054
  Direction = (0,0,-1)
  Length = 57.7
  Length2 = 53
  Midplane = true
  Profile = -> Sketch134
  ReferenceAxis = -> Sketch134 [N_Axis]
  Refine = true
  Suppressed = false
  Type = 4
FEATURE [Sketcher::SketchObject] Sketch135
  AttachmentOffset = pos=(0,0,-58.5) rot=(0,0,1;0rad)
  AttachmentSupport = -> [XY_Plane070]
  FullyConstrained = true
  MapMode = 5
  Placement = pos=(0,0,-58.5) rot=(0,0,1;0rad)
  sketch-geometry (5):
    g0: LineSegment StartX=2e-16 StartY=35.0826 StartZ=0 EndX=2e-16 EndY=-78 EndZ=0
    g1: LineSegment StartX=2e-16 StartY=-78 StartZ=0 EndX=3.5 EndY=-78 EndZ=0
    g2: LineSegment StartX=3.5 StartY=-78 StartZ=0 EndX=3.5 EndY=35.5 EndZ=0
    g3: LineSegment StartX=3.5 StartY=35.5 StartZ=0 EndX=2 EndY=35.5 EndZ=0
    g4: ArcOfCircle CenterX=2 CenterY=30.5 CenterZ=0 NormalX=0 NormalY=0 NormalZ=1 AngleXU=0 Radius=5 StartAngle=1.5708 EndAngle=1.98231
  constraints (15):
    c: Coincident(g0,g1)
    c: Coincident(g1,g2)
    c: Coincident(g2,g3)
    c: Vertical(g0)
    c: Vertical(g2)
    c: Horizontal(g1)
    c: Horizontal(g3)
    c: PointOnObject(g0,g-2)
    c: DistanceX(g1,g1) = 3.5
    c: DistanceY(g0) = -78
    c: DistanceY(g2,g2) = 113.5
    c: Coincident(g4,g0)
    c: Radius(g4) = 5
    c: DistanceX(g4) = 2
    c: Tangent(g4,g3) = -1.5708
FEATURE [PartDesign::Pad] Pad065  label="Bodenkante"
  BaseFeature = -> Pocket055
  Direction = (0,0,1)
  Length = 1
  Length2 = 10
  Profile = -> Sketch135
  ReferenceAxis = -> Sketch135 [N_Axis]
  Refine = true
  Suppressed = false
  Type = 0
FEATURE [PartDesign::Fillet] Fillet002
  Base = -> Pad065 [Edge105]
  BaseFeature = -> Pad065
  Radius = 0.99
  SupportTransform = false
  Suppressed = false
  UseAllEdges = false
FEATURE [PartDesign::Body] Body065  label="SeitenDeckel"
  AllowCompound = false
  Group = -> [Sketch131,Pad064,Sketch132,Pocket053,Mirrored004,Sketch133,Pocket054,Sketch134,Pocket055,Sketch135,Pad065,Fillet002]
  Origin = -> Origin070
  Placement = pos=(-195.2,0,50) rot=(0,0,1;0rad)
  Tip = -> Fillet002
FEATURE [Part::Mirroring] Mirror  label="SeitenDeckelR"
  Base = (0,0,0)
  Normal = (1,0,0)
  Source = -> Body065
FEATURE [Sketcher::SketchObject] Sketch136
  AttachmentSupport = -> [YZ_Plane071]
  FullyConstrained = true
  MapMode = 5
  Placement = pos=(0,0,0) rot=(0.57735,0.57735,0.57735;2.0944rad)
  sketch-geometry (15):
    g0: LineSegment StartX=-77.5 StartY=0 StartZ=0 EndX=-77.5 EndY=6.3 EndZ=0
    g1: LineSegment StartX=-77.5 StartY=6.3 StartZ=0 EndX=-79.5 EndY=6.3 EndZ=0
    g2: LineSegment StartX=-79.5 StartY=6.3 StartZ=0 EndX=-79.5 EndY=-1.3 EndZ=0
    g3: ArcOfCircle CenterX=-78.5 CenterY=-1.3 CenterZ=0 NormalX=0 NormalY=0 NormalZ=1 AngleXU=0 Radius=1 StartAngle=3.14159 EndAngle=4.71239
    g4: LineSegment StartX=-78.5 StartY=-2.3 StartZ=0 EndX=35.5 EndY=-2.3 EndZ=0
    g5: LineSegment StartX=35.5 StartY=-2.3 StartZ=0 EndX=35.5 EndY=0 EndZ=0
    g6: LineSegment StartX=35.5 StartY=0 StartZ=0 EndX=15.4 EndY=0 EndZ=0
    g7: LineSegment StartX=15.4 StartY=0 StartZ=0 EndX=15.4 EndY=2.9 EndZ=0
    g8: LineSegment StartX=15.4 StartY=2.9 StartZ=0 EndX=9.4 EndY=2.9 EndZ=0
    g9: LineSegment StartX=9.4 StartY=2.9 StartZ=0 EndX=9.4 EndY=0 EndZ=0
    g10: LineSegment StartX=9.4 StartY=0 StartZ=0 EndX=-51.4 EndY=0 EndZ=0
    g11: LineSegment StartX=-51.4 StartY=0 StartZ=0 EndX=-51.4 EndY=2.9 EndZ=0
    g12: LineSegment StartX=-51.4 StartY=2.9 StartZ=0 EndX=-57.4 EndY=2.9 EndZ=0
    g13: LineSegment StartX=-57.4 StartY=2.9 StartZ=0 EndX=-57.4 EndY=0 EndZ=0
    g14: LineSegment StartX=-57.4 StartY=0 StartZ=0 EndX=-77.5 EndY=0 EndZ=0
  constraints (44):
    c: Vertical(g0)
    c: Coincident(g0,g1)
    c: Horizontal(g1)
    c: Coincident(g1,g2)
    c: Vertical(g2)
    c: Tangent(g2,g3) = -1.5708
    c: Tangent(g3,g4) = -1.5708
    c: Coincident(g4,g5)
    c: Vertical(g5)
    c: Coincident(g5,g6)
    c: Horizontal(g6)
    c: Coincident(g6,g7)
    c: Vertical(g7)
    c: Coincident(g7,g8)
    c: Horizontal(g8)
    c: Coincident(g8,g9)
    c: Vertical(g9)
    c: Coincident(g9,g10)
    c: Horizontal(g10)
    c: Coincident(g10,g11)
    c: Vertical(g11)
    c: Coincident(g11,g12)
    c: Horizontal(g12)
    c: Coincident(g12,g13)
    c: Vertical(g13)
    c: Coincident(g13,g14)
    c: Coincident(g14,g0)
    c: Horizontal(g13,g10)
    c: DistanceX(g12,g12) = 6
    c: DistanceY(g11,g11) = 2.9
    c: Equal(g12,g8)
    c: Horizontal(g9,g6)
    c: Equal(g9,g11)
    c: Horizontal(g14)
    c: PointOnObject(g13,g-1)
    c: Radius(g3) = 1
    c: Horizontal(g4)
    c: DistanceX(g2) = -79.5
    c: DistanceY(g3) = -2.3
    c: DistanceX(g1,g1) = 2
    c: DistanceY(g0,g0) = 6.3
    c: DistanceX(g14,g14) = 20.1
    c: DistanceX(g5) = 35.5
    c: DistanceX(g6,g6) = 20.1
FEATURE [PartDesign::Pad] Pad066  label="Profil001"
  Direction = (1,0,0)
  Length = 46.4
  Length2 = 10
  Midplane = true
  Placement = pos=(0,0,0) rot=(1,1,1;2.0944rad)
  Profile = -> Sketch136
  ReferenceAxis = -> Sketch136 [N_Axis]
  Refine = true
  Suppressed = false
  Type = 0
FEATURE [Sketcher::SketchObject] Sketch137
  AttachmentOffset = pos=(0,0,20) rot=(0,0,1;0rad)
  AttachmentSupport = -> [YZ_Plane071]
  FullyConstrained = true
  MapMode = 5
  Placement = pos=(20,0,0) rot=(0.57735,0.57735,0.57735;2.0944rad)
  sketch-geometry (4):
    g0: LineSegment StartX=-78.6 StartY=8.5 StartZ=0 EndX=-78.6 EndY=-1.5 EndZ=0
    g1: LineSegment StartX=-78.6 StartY=-1.5 StartZ=0 EndX=78.6 EndY=-1.5 EndZ=0
    g2: LineSegment StartX=78.6 StartY=-1.5 StartZ=0 EndX=78.6 EndY=8.5 EndZ=0
    g3: LineSegment StartX=78.6 StartY=8.5 StartZ=0 EndX=-78.6 EndY=8.5 EndZ=0
  constraints (11):
    c: Coincident(g0,g1)
    c: Coincident(g1,g2)
    c: Coincident(g2,g3)
    c: Coincident(g3,g0)
    c: Vertical(g0)
    c: Vertical(g2)
    c: Horizontal(g1)
    c: DistanceY(g2,g2) = 10
    c: DistanceY(g0) = -1.5
    c: DistanceX(g0) = -78.6
    c: Symmetric(g0,g2,g-2)
FEATURE [PartDesign::Pocket] Pocket056  label="Absatz001"
  BaseFeature = -> Pad066
  Direction = (-1,0,0)
  Length = 5
  Length2 = 5
  Placement = pos=(0,0,0) rot=(1,1,1;2.0944rad)
  Profile = -> Sketch137
  ReferenceAxis = -> Sketch137 [N_Axis]
  Refine = true
  Reversed = true
  Suppressed = false
  Type = 1
FEATURE [PartDesign::Mirrored] Mirrored005
  BaseFeature = -> Pocket056
  MirrorPlane = -> YZ_Plane071
  Originals = -> [Pocket056]
  Placement = pos=(0,0,0) rot=(1,1,1;2.0944rad)
  Refine = true
  Suppressed = false
  TransformMode = 0
FEATURE [Sketcher::SketchObject] Sketch138
  AttachmentSupport = -> [XY_Plane071]
  FullyConstrained = true
  MapMode = 5
  sketch-geometry (1):
    g0: Circle CenterX=0 CenterY=31.5 CenterZ=0 NormalX=0 NormalY=0 NormalZ=1 AngleXU=0 Radius=2.1
  constraints (3):
    c: Diameter(g0) = 4.2
    c: PointOnObject(g0,g-2)
    c: DistanceY(g0) = 31.5
FEATURE [PartDesign::Pocket] Pocket057  label="Schraubenloch"
  BaseFeature = -> Mirrored005
  Direction = (0,0,-1)
  Length = 5
  Length2 = 5
  Midplane = true
  Placement = pos=(0,0,0) rot=(1,1,1;2.0944rad)
  Profile = -> Sketch138
  ReferenceAxis = -> Sketch138 [N_Axis]
  Refine = true
  Suppressed = false
  Type = 1
FEATURE [Sketcher::SketchObject] Sketch140
  AttachmentSupport = -> [YZ_Plane072]
  FullyConstrained = true
  MapMode = 5
  Placement = pos=(0,0,0) rot=(0.57735,0.57735,0.57735;2.0944rad)
  sketch-geometry (7):
    g0: LineSegment StartX=-77.5 StartY=0 StartZ=0 EndX=-77.5 EndY=6.3 EndZ=0
    g1: LineSegment StartX=-77.5 StartY=6.3 StartZ=0 EndX=-79.5 EndY=6.3 EndZ=0
    g2: LineSegment StartX=-79.5 StartY=6.3 StartZ=0 EndX=-79.5 EndY=-1.3 EndZ=0
    g3: ArcOfCircle CenterX=-78.5 CenterY=-1.3 CenterZ=0 NormalX=0 NormalY=0 NormalZ=1 AngleXU=0 Radius=1 StartAngle=3.14159 EndAngle=4.71239
    g4: LineSegment StartX=-78.5 StartY=-2.3 StartZ=0 EndX=35.5 EndY=-2.3 EndZ=0
    g5: LineSegment StartX=35.5 StartY=-2.3 StartZ=0 EndX=35.5 EndY=0 EndZ=0
    g6: LineSegment StartX=35.5 StartY=0 StartZ=0 EndX=-77.5 EndY=0 EndZ=0
  constraints (20):
    c: Vertical(g0)
    c: Coincident(g0,g1)
    c: Horizontal(g1)
    c: Coincident(g1,g2)
    c: Vertical(g2)
    c: Tangent(g2,g3) = -1.5708
    c: Tangent(g3,g4) = -1.5708
    c: Coincident(g4,g5)
    c: Vertical(g5)
    c: Coincident(g6,g0)
    c: Horizontal(g6)
    c: Radius(g3) = 1
    c: Horizontal(g4)
    c: DistanceX(g2) = -79.5
    c: DistanceY(g3) = -2.3
    c: DistanceX(g1,g1) = 2
    c: DistanceY(g0,g0) = 6.3
    c: DistanceX(g5) = 35.5
    c: Coincident(g6,g5)
    c: PointOnObject(g5,g-1)
FEATURE [PartDesign::Pad] Pad067  label="Profil"
  Direction = (1,0,0)
  Length = 173.6
  Length2 = 10
  Midplane = true
  Placement = pos=(0,0,0) rot=(1,1,1;2.0944rad)
  Profile = -> Sketch140
  ReferenceAxis = -> Sketch140 [N_Axis]
  Refine = true
  Suppressed = false
  Type = 0
FEATURE [Sketcher::SketchObject] Sketch141
  AttachmentOffset = pos=(0,0,84.3) rot=(0,0,1;0rad)
  AttachmentSupport = -> [YZ_Plane072]
  FullyConstrained = true
  MapMode = 5
  Placement = pos=(84.3,0,0) rot=(0.57735,0.57735,0.57735;2.0944rad)
  sketch-geometry (8):
    g0: LineSegment StartX=-78.4 StartY=-3.2 StartZ=0 EndX=-78.4 EndY=-1.2 EndZ=0
    g1: LineSegment StartX=-78.4 StartY=-1.2 StartZ=0 EndX=78.4 EndY=-1.2 EndZ=0
    g2: LineSegment StartX=78.4 StartY=-1.2 StartZ=0 EndX=78.4 EndY=-3.2 EndZ=0
    g3: LineSegment StartX=78.4 StartY=-3.2 StartZ=0 EndX=-78.4 EndY=-3.2 EndZ=0
    g4: LineSegment StartX=-78.4 StartY=-1.2 StartZ=0 EndX=-78.4 EndY=6.8 EndZ=0
    g5: LineSegment StartX=-78.4 StartY=6.8 StartZ=0 EndX=-88.4 EndY=6.8 EndZ=0
    g6: LineSegment StartX=-88.4 StartY=6.8 StartZ=0 EndX=-88.4 EndY=-3.2 EndZ=0
    g7: LineSegment StartX=-88.4 StartY=-3.2 StartZ=0 EndX=-78.4 EndY=-3.2 EndZ=0
  constraints (22):
    c: Coincident(g0,g1)
    c: Coincident(g1,g2)
    c: Coincident(g2,g3)
    c: Coincident(g3,g0)
    c: Vertical(g0)
    c: Vertical(g2)
    c: Horizontal(g1)
    c: DistanceY(g0) = -1.2
    c: DistanceX(g0) = -78.4
    c: Symmetric(g0,g2,g-2)
    c: DistanceY(g2,g2) = 2
    c: Coincident(g0,g4)
    c: Vertical(g4)
    c: Coincident(g4,g5)
    c: Coincident(g5,g6)
    c: Vertical(g6)
    c: Coincident(g6,g7)
    c: Coincident(g7,g0)
    c: Horizontal(g7)
    c: Horizontal(g5)
    c: Equal(g5,g6)
    c: DistanceY(g6,g6) = 10
FEATURE [PartDesign::Pocket] Pocket059  label="Absatz"
  BaseFeature = -> Pad067
  Direction = (-1,0,0)
  Length = 5
  Length2 = 5
  Placement = pos=(0,0,0) rot=(1,1,1;2.0944rad)
  Profile = -> Sketch141
  ReferenceAxis = -> Sketch141 [N_Axis]
  Refine = true
  Reversed = true
  Suppressed = false
  Type = 1
FEATURE [PartDesign::Mirrored] Mirrored006
  BaseFeature = -> Pocket059
  MirrorPlane = -> YZ_Plane072
  Originals = -> [Pocket059]
  Placement = pos=(0,0,0) rot=(1,1,1;2.0944rad)
  Refine = true
  Suppressed = false
  TransformMode = 0
FEATURE [Sketcher::SketchObject] Sketch142
  AttachmentSupport = -> [XY_Plane072]
  FullyConstrained = true
  MapMode = 5
  sketch-geometry (5):
    g0: Circle CenterX=72.6 CenterY=31.5 CenterZ=0 NormalX=0 NormalY=0 NormalZ=1 AngleXU=0 Radius=2.1
    g1: LineSegment StartX=84.3 StartY=-77.4 StartZ=0 EndX=84.3 EndY=-82.4 EndZ=0
    g2: LineSegment StartX=84.3 StartY=-82.4 StartZ=0 EndX=89.3 EndY=-82.4 EndZ=0
    g3: LineSegment StartX=89.3 StartY=-82.4 StartZ=0 EndX=89.3 EndY=-77.4 EndZ=0
    g4: LineSegment StartX=89.3 StartY=-77.4 StartZ=0 EndX=84.3 EndY=-77.4 EndZ=0
  constraints (15):
    c: Diameter(g0) = 4.2
    c: DistanceY(g0) = 31.5
    c: DistanceX(g0) = 72.6
    c: Coincident(g1,g2)
    c: Coincident(g2,g3)
    c: Coincident(g3,g4)
    c: Coincident(g4,g1)
    c: Vertical(g1)
    c: Vertical(g3)
    c: Horizontal(g2)
    c: Horizontal(g4)
    c: Equal(g1,g4)
    c: DistanceX(g4,g4) = 5
    c: DistanceX(g1) = 84.3
    c: DistanceY(g1) = -77.4
FEATURE [PartDesign::Pocket] Pocket060
  BaseFeature = -> Mirrored006
  Direction = (0,0,-1)
  Length = 5
  Length2 = 5
  Midplane = true
  Placement = pos=(0,0,0) rot=(1,1,1;2.0944rad)
  Profile = -> Sketch142
  ReferenceAxis = -> Sketch142 [N_Axis]
  Refine = true
  Suppressed = false
  Type = 1
FEATURE [PartDesign::Body] Body067  label="BodenDeckelL"
  AllowCompound = false
  Group = -> [Sketch140,Pad067,Sketch141,Pocket059,Mirrored006,Sketch142,Pocket060]
  Origin = -> Origin072
  Placement = pos=(107.4,0,-6.2) rot=(0,0,1;0rad)
  Tip = -> Pocket060
FEATURE [Part::Mirroring] Part__Mirroring  label="BodenDeckelR"
  Base = (0,0,0)
  Normal = (1,0,0)
  Source = -> Body067
FEATURE [Sketcher::SketchObject] Sketch143
  AttachmentOffset = pos=(0,-21,1.5) rot=(0,0,1;0rad)
  AttachmentSupport = -> [XY_Plane071]
  FullyConstrained = true
  MapMode = 5
  Placement = pos=(0,-21,1.5) rot=(0,0,1;0rad)
  sketch-geometry (12):
    g0: LineSegment StartX=-15 StartY=37.5 StartZ=0 EndX=-36.6506 EndY=0 EndZ=0
    g1: LineSegment StartX=-36.6506 StartY=0 StartZ=0 EndX=-15 EndY=-37.5 EndZ=0
    g2: LineSegment StartX=-15 StartY=-37.5 StartZ=0 EndX=-12 EndY=-37.5 EndZ=0
    g3: LineSegment StartX=-12 StartY=-37.5 StartZ=0 EndX=-33.6506 EndY=0 EndZ=0
    g4: LineSegment StartX=-33.6506 StartY=0 StartZ=0 EndX=-12 EndY=37.5 EndZ=0
    g5: LineSegment StartX=-12 StartY=37.5 StartZ=0 EndX=-15 EndY=37.5 EndZ=0
    g6: LineSegment StartX=12 StartY=37.5 StartZ=0 EndX=33.6506 EndY=0 EndZ=0
    g7: LineSegment StartX=33.6506 StartY=0 StartZ=0 EndX=12 EndY=-37.5 EndZ=0
    g8: LineSegment StartX=12 StartY=-37.5 StartZ=0 EndX=15 EndY=-37.5 EndZ=0
    g9: LineSegment StartX=15 StartY=-37.5 StartZ=0 EndX=36.6506 EndY=0 EndZ=0
    g10: LineSegment StartX=36.6506 StartY=0 StartZ=0 EndX=15 EndY=37.5 EndZ=0
    g11: LineSegment StartX=15 StartY=37.5 StartZ=0 EndX=12 EndY=37.5 EndZ=0
  constraints (34):
    c: PointOnObject(g0,g-1)
    c: Coincident(g0,g1)
    c: Coincident(g1,g2)
    c: Horizontal(g2)
    c: Coincident(g2,g3)
    c: PointOnObject(g3,g-1)
    c: Coincident(g3,g4)
    c: Coincident(g4,g5)
    c: Coincident(g5,g0)
    c: PointOnObject(g6,g-1)
    c: Coincident(g6,g7)
    c: Coincident(g7,g8)
    c: Horizontal(g8)
    c: Coincident(g8,g9)
    c: PointOnObject(g9,g-1)
    c: Coincident(g9,g10)
    c: Coincident(g10,g11)
    c: Coincident(g11,g6)
    c: Horizontal(g11)
    c: Equal(g11,g5)
    c: Symmetric(g4,g6,g-2)
    c: Parallel(g4,g0)
    c: Parallel(g0,g7)
    c: Parallel(g7,g9)
    c: Parallel(g1,g3)
    c: Parallel(g3,g6)
    c: Parallel(g6,g10)
    c: Symmetric(g2,g4,g-1)
    c: Horizontal(g5)
    c: Horizontal(g7,g2)
    c: DistanceX(g11,g11) = 3
    c: DistanceY(g8,g10) = 75
    c: DistanceX(g0,g10) = 30
    c: Angle(g-2,g6) = 0.523599
FEATURE [PartDesign::Pocket] Pocket061  label="InnenNadelTaschen"
  BaseFeature = -> Pocket057
  Direction = (0,0,-1)
  Length = 1.3
  Length2 = 5
  Midplane = true
  Placement = pos=(0,0,0) rot=(1,1,1;2.0944rad)
  Profile = -> Sketch143
  ReferenceAxis = -> Sketch143 [N_Axis]
  Suppressed = false
  Type = 0
FEATURE [PartDesign::Body] Body066  label="BodenDeckelMitte"
  AllowCompound = false
  Group = -> [Sketch136,Pad066,Sketch137,Pocket056,Mirrored005,Sketch138,Pocket057,Sketch143,Pocket061]
  Origin = -> Origin071
  Placement = pos=(0,0,-6.2) rot=(0,0,1;0rad)
  Tip = -> Pocket061
FEATURE [App::Part] Part002  label="Box"
  Group = -> [Body052,Body053,Body054,Body056,Body057,Body058,Body059,Body060,Body061,Body062,Body063,Body064,Body065,Mirror,Body066,Body067,Part__Mirroring]
  Origin = -> Origin058
  Placement = pos=(-40,0,-35) rot=(0,0,1;0rad)
FEATURE [Part::Cylinder] Cylinder  label="Zylinder"
  Angle = 360
  AttacherType = Attacher::AttachEngine3D
  FirstAngle = 0
  Height = 100
  Placement = pos=(-40,-60,435) rot=(1,0,0;4.71239rad)
  Radius = 2
  SecondAngle = 0
FEATURE [Image::ImagePlane] Turm001
  Placement = pos=(-1,0,-197) rot=(1,0,0;1.5708rad)
  XSize = 268
  YSize = 495
FEATURE [App::Part] Part003  label="Bild3_transp"
  Group = -> [Turm001]
  Origin = -> Origin073
  Placement = pos=(-40,22,435) rot=(0,1,0;0.041888rad)
FEATURE [Sketcher::SketchObject] Sketch144
  AttachmentSupport = -> [XZ_Plane]
  FullyConstrained = true
  MapMode = 5
  Placement = pos=(0,0,0) rot=(1,0,0;1.5708rad)
  Support = -> [XZ_Plane]
  sketch-geometry (15):
    g0: LineSegment StartX=0 StartY=13 StartZ=0 EndX=0 EndY=10 EndZ=0
    g1: LineSegment StartX=0 StartY=10 StartZ=0 EndX=3.5 EndY=10 EndZ=0
    g2: LineSegment StartX=3.5 StartY=10 StartZ=0 EndX=3.5 EndY=3 EndZ=0
    g3: LineSegment StartX=3.5 StartY=3 StartZ=0 EndX=176.5 EndY=3 EndZ=0
    g4: LineSegment StartX=176.5 StartY=3 StartZ=0 EndX=176.5 EndY=10 EndZ=0
    g5: LineSegment StartX=176.5 StartY=10 StartZ=0 EndX=180 EndY=10 EndZ=0
    g6: LineSegment StartX=180 StartY=10 StartZ=0 EndX=180 EndY=13 EndZ=0
    g7: LineSegment StartX=180 StartY=13 StartZ=0 EndX=220 EndY=112 EndZ=0
    g8: LineSegment StartX=220 StartY=112 StartZ=0 EndX=270 EndY=127 EndZ=0
    g9: LineSegment StartX=270 StartY=127 StartZ=0 EndX=270 EndY=138 EndZ=0
    g10: LineSegment StartX=270 StartY=138 StartZ=0 EndX=-48 EndY=138 EndZ=0
    g11: LineSegment StartX=-48 StartY=138 StartZ=0 EndX=-48 EndY=125 EndZ=0
    g12: LineSegment StartX=-48 StartY=125 StartZ=0 EndX=-5 EndY=110 EndZ=0
    g13: LineSegment StartX=-5 StartY=110 StartZ=0 EndX=0 EndY=13 EndZ=0
    g14: LineSegment StartX=90 StartY=3 StartZ=0 EndX=90 EndY=138 EndZ=0
  constraints (45):
    c: PointOnObject(g0,g-2)
    c: Coincident(g0,g1)
    c: Horizontal(g1)
    c: Coincident(g1,g2)
    c: Vertical(g2)
    c: Coincident(g2,g3)
    c: Horizontal(g3)
    c: Coincident(g3,g4)
    c: Coincident(g4,g5)
    c: Coincident(g5,g6)
    c: Coincident(g6,g7)
    c: Coincident(g7,g8)
    c: Coincident(g8,g9)
    c: Vertical(g9)
    c: Coincident(g9,g10)
    c: Horizontal(g10)
    c: Coincident(g10,g11)
    c: Coincident(g11,g12)
    c: Coincident(g12,g13)
    c: Coincident(g13,g0)
    c: Vertical(g4)
    c: Horizontal(g5)
    c: Vertical(g6)
    c: Vertical(g0)
    c: Equal(g2,g4)
    c: Equal(g5,g1)
    c: Equal(g0,g6)
    c: DistanceX(g1,g1) = 3.5
    c: DistanceY(g0,g0) = 3
    c: Symmetric(g3,g3,g14)
    c: DistanceX(g12) = -5
    c: DistanceY(g12,g11) = 15
    c: DistanceY(g12) = 110
    c: Vertical(g14)
    c: DistanceX(g5) = 180
    c: DistanceX(g5,g7) = 40
    c: DistanceY(g5,g7) = 102
    c: Vertical(g11)
    c: DistanceY(g7,g8) = 15
    c: DistanceY(g0) = 10
    c: DistanceY(g2,g2) = 7
    c: DistanceY(g14,g14) = 135
    c: DistanceX(g7,g8) = 50
    c: DistanceX(g10) = -48
    c: PointOnObject(g14,g10)
FEATURE [PartDesign::Pad] Pad068
  Direction = (0,-1,2e-16)
  Length = 1
  Length2 = 10
  Placement = pos=(0,0,0) rot=(1,0,0;1.5708rad)
  Profile = -> Sketch144
  ReferenceAxis = -> Sketch144 [N_Axis]
  Suppressed = false
  Type = 0
FEATURE [PartDesign::Body] Body  label="Bild2Sketch"
  AllowCompound = false
  Group = -> [Sketch144,Pad068]
  Origin = -> Origin
  Placement = pos=(-147,-20,6.8) rot=(0,0,1;0rad)
  Tip = -> Pad068
FEATURE [App::Part] Part005  label="Bottm_Link_Bild2"
  Group = -> [Body008,Body007,Body]
  Origin = -> Origin075
  Placement = pos=(-16.0035,0,-6.35836) rot=(0,1,0;6.21337rad)
FEATURE [Sketcher::SketchObject] Sketch145
  AttachmentSupport = -> [XZ_Plane076]
  FullyConstrained = true
  MapMode = 5
  Placement = pos=(0,0,0) rot=(1,0,0;1.5708rad)
  Support = -> [XZ_Plane076]
  sketch-geometry (15):
    g0: LineSegment StartX=0 StartY=13 StartZ=0 EndX=0 EndY=10 EndZ=0
    g1: LineSegment StartX=0 StartY=10 StartZ=0 EndX=3.5 EndY=10 EndZ=0
    g2: LineSegment StartX=3.5 StartY=10 StartZ=0 EndX=3.5 EndY=3 EndZ=0
    g3: LineSegment StartX=3.5 StartY=3 StartZ=0 EndX=176.5 EndY=3 EndZ=0
    g4: LineSegment StartX=176.5 StartY=3 StartZ=0 EndX=176.5 EndY=10 EndZ=0
    g5: LineSegment StartX=176.5 StartY=10 StartZ=0 EndX=180 EndY=10 EndZ=0
    g6: LineSegment StartX=180 StartY=10 StartZ=0 EndX=180 EndY=13 EndZ=0
    g7: LineSegment StartX=180 StartY=13 StartZ=0 EndX=210 EndY=89 EndZ=0
    g8: LineSegment StartX=210 StartY=89 StartZ=0 EndX=272 EndY=97 EndZ=0
    g9: LineSegment StartX=272 StartY=97 StartZ=0 EndX=272 EndY=138 EndZ=0
    g10: LineSegment StartX=272 StartY=138 StartZ=0 EndX=-92 EndY=138 EndZ=0
    g11: LineSegment StartX=-92 StartY=138 StartZ=0 EndX=-92 EndY=125 EndZ=0
    g12: LineSegment StartX=-92 StartY=125 StartZ=0 EndX=-30 EndY=114 EndZ=0
    g13: LineSegment StartX=-30 StartY=114 StartZ=0 EndX=0 EndY=13 EndZ=0
    g14: LineSegment StartX=90 StartY=3 StartZ=0 EndX=90 EndY=138 EndZ=0
  constraints (45):
    c: PointOnObject(g0,g-2)
    c: Coincident(g0,g1)
    c: Horizontal(g1)
    c: Coincident(g1,g2)
    c: Vertical(g2)
    c: Coincident(g2,g3)
    c: Horizontal(g3)
    c: Coincident(g3,g4)
    c: Coincident(g4,g5)
    c: Coincident(g5,g6)
    c: Coincident(g6,g7)
    c: Coincident(g7,g8)
    c: Coincident(g8,g9)
    c: Vertical(g9)
    c: Coincident(g9,g10)
    c: Horizontal(g10)
    c: Coincident(g10,g11)
    c: Coincident(g11,g12)
    c: Coincident(g12,g13)
    c: Coincident(g13,g0)
    c: Vertical(g4)
    c: Horizontal(g5)
    c: Vertical(g0)
    c: Equal(g2,g4)
    c: Equal(g5,g1)
    c: Equal(g0,g6)
    c: DistanceX(g1,g1) = 3.5
    c: DistanceY(g0,g0) = 3
    c: Symmetric(g3,g3,g14)
    c: DistanceX(g12) = -30
    c: DistanceY(g12,g11) = 11
    c: DistanceY(g12) = 114
    c: Vertical(g14)
    c: DistanceX(g5) = 180
    c: DistanceX(g5,g7) = 30
    c: DistanceY(g5,g7) = 79
    c: Vertical(g11)
    c: DistanceY(g7,g8) = 8
    c: DistanceY(g0) = 10
    c: DistanceY(g2,g2) = 7
    c: DistanceY(g14,g14) = 135
    c: DistanceX(g7,g8) = 62
    c: DistanceX(g10) = -92
    c: PointOnObject(g14,g10)
    c: Vertical(g6)
FEATURE [PartDesign::Pad] Pad069
  Direction = (0,-1,2e-16)
  Length = 1
  Length2 = 10
  Placement = pos=(0,0,0) rot=(1,0,0;1.5708rad)
  Profile = -> Sketch145
  ReferenceAxis = -> Sketch145 [N_Axis]
  Suppressed = false
  Type = 0
FEATURE [PartDesign::Body] Body068  label="Bild1Sketch"
  AllowCompound = false
  Group = -> [Sketch145,Pad069]
  Origin = -> Origin076
  Placement = pos=(-157,0,10.8) rot=(0,0,1;0rad)
  Tip = -> Pad069
FEATURE [App::Part] Part006  label="Bottom_Link_Bild1"
  Group = -> [Body068,Body024]
  Origin = -> Origin077
  Placement = pos=(30,-58,-14.5) rot=(0,-1,0;6.14356rad)
FEATURE [App::Part] Part001  label="Getriebe"
  Group = -> [Body016,Body003,Body050,Body049,Body048,Body046,Body045,Body044,Body041,Body038,Body039,Body037,Body043,DatumPlane001,Slice001,Slice001_child0,Slice001_child1,GrExplode_Slice001,Motor_GW370_Motor_Gearbox,Motor_GW370_Motor_Gearbox001,Body032,Body031,Body033,Body029,Body028,Body027,Body026,Body025,Body023,Body022,Body034,Body021,Body020,Body047,Body019,Body018,Body017,Body051,Body014,Body013,+14 more]
  Origin = -> Origin057
FEATURE [PartDesign::FeatureBase] Clone007
  BaseFeature = -> Body007
  Placement = pos=(-147,-18,7) rot=(0,0,1;0rad)
  Suppressed = false
FEATURE [PartDesign::Body] Body069
  AllowCompound = false
  Group = -> [Clone007]
  Origin = -> Origin078
  Placement = pos=(0,-149,0) rot=(0,0,1;0rad)
  Tip = -> Clone007
FEATURE [Sketcher::SketchObject] Sketch
  AttachmentSupport = -> [XY_Plane079]
  FullyConstrained = true
  MapMode = 5
  Support = -> [XY_Plane079]
  sketch-geometry (8):
    g0: LineSegment StartX=-92 StartY=5 StartZ=0 EndX=-92 EndY=-5 EndZ=0
    g1: LineSegment StartX=-92 StartY=-5 StartZ=0 EndX=92 EndY=-5 EndZ=0
    g2: LineSegment StartX=92 StartY=-5 StartZ=0 EndX=92 EndY=5 EndZ=0
    g3: LineSegment StartX=92 StartY=5 StartZ=0 EndX=-92 EndY=5 EndZ=0
    g4: LineSegment StartX=-90.2 StartY=3.25 StartZ=0 EndX=-90.2 EndY=-3.25 EndZ=0
    g5: LineSegment StartX=-90.2 StartY=-3.25 StartZ=0 EndX=90.2 EndY=-3.25 EndZ=0
    g6: LineSegment StartX=90.2 StartY=-3.25 StartZ=0 EndX=90.2 EndY=3.25 EndZ=0
    g7: LineSegment StartX=90.2 StartY=3.25 StartZ=0 EndX=-90.2 EndY=3.25 EndZ=0
  constraints (22):
    c: Coincident(g0,g1)
    c: Coincident(g1,g2)
    c: Coincident(g2,g3)
    c: Coincident(g3,g0)
    c: Vertical(g0)
    c: Vertical(g2)
    c: Horizontal(g1)
    c: Horizontal(g3)
    c: Coincident(g4,g5)
    c: Coincident(g5,g6)
    c: Coincident(g6,g7)
    c: Coincident(g7,g4)
    c: Vertical(g4)
    c: Vertical(g6)
    c: Horizontal(g5)
    c: Horizontal(g7)
    c: Symmetric(g5,g4,g-1)
    c: Symmetric(g0,g2,g-1)
    c: DistanceX(g5,g5) = 180.4
    c: DistanceY(g6,g6) = 6.5
    c: DistanceY(g2,g2) = 10
    c: DistanceX(g1,g1) = 184
FEATURE [PartDesign::Pad] Pad070
  Direction = (0,0,1)
  Length = 6
  Length2 = 10
  Profile = -> Sketch
  ReferenceAxis = -> Sketch [N_Axis]
  Suppressed = false
  Type = 0
FEATURE [PartDesign::Chamfer] Chamfer003
  Angle = 45
  Base = -> Pad070 [Edge21,Edge23,Edge18,Edge15]
  BaseFeature = -> Pad070
  ChamferType = 0
  FlipDirection = false
  Size = 1.5
  Size2 = 1
  SupportTransform = false
  Suppressed = false
  UseAllEdges = false
FEATURE [Sketcher::SketchObject] Sketch146
  AttachmentSupport = -> [XZ_Plane079]
  FullyConstrained = true
  MapMode = 5
  Placement = pos=(0,0,0) rot=(1,0,0;1.5708rad)
  Support = -> [XZ_Plane079]
  sketch-geometry (14):
    g0: LineSegment StartX=88.0774 StartY=1 StartZ=0 EndX=88.6547 EndY=2 EndZ=0
    g1: LineSegment StartX=88.6547 StartY=2 StartZ=0 EndX=88.0774 EndY=3 EndZ=0
    g2: LineSegment StartX=88.0774 StartY=3 StartZ=0 EndX=86.9226 EndY=3 EndZ=0
    g3: LineSegment StartX=86.9226 StartY=3 StartZ=0 EndX=86.3453 EndY=2 EndZ=0
    g4: LineSegment StartX=86.3453 StartY=2 StartZ=0 EndX=86.9226 EndY=1 EndZ=0
    g5: LineSegment StartX=86.9226 StartY=1 StartZ=0 EndX=88.0774 EndY=1 EndZ=0
    g6: Circle CenterX=87.5 CenterY=2 CenterZ=0 NormalX=0 NormalY=0 NormalZ=1 AngleXU=0 Radius=1.1547
    g7: LineSegment StartX=-86.9226 StartY=1 StartZ=0 EndX=-86.3453 EndY=2 EndZ=0
    g8: LineSegment StartX=-86.3453 StartY=2 StartZ=0 EndX=-86.9226 EndY=3 EndZ=0
    g9: LineSegment StartX=-86.9226 StartY=3 StartZ=0 EndX=-88.0774 EndY=3 EndZ=0
    g10: LineSegment StartX=-88.0774 StartY=3 StartZ=0 EndX=-88.6547 EndY=2 EndZ=0
    g11: LineSegment StartX=-88.6547 StartY=2 StartZ=0 EndX=-88.0774 EndY=1 EndZ=0
    g12: LineSegment StartX=-88.0774 StartY=1 StartZ=0 EndX=-86.9226 EndY=1 EndZ=0
    g13: Circle CenterX=-87.5 CenterY=2 CenterZ=0 NormalX=0 NormalY=0 NormalZ=1 AngleXU=0 Radius=1.1547
  constraints (33):
    c: Coincident(g0,g1)
    c: Coincident(g1,g2)
    c: Coincident(g2,g3)
    c: Coincident(g3,g4)
    c: Coincident(g4,g5)
    c: Coincident(g5,g0)
    c: Equal(g0, g1-g5) x5
    c: PointOnObject(g0,g6)
    c: PointOnObject(g1,g6)
    c: PointOnObject(g2,g6)
    c: PointOnObject(g3,g6)
    c: PointOnObject(g4,g6)
    c: PointOnObject(g5,g6)
    c: Coincident(g7,g8)
    c: Coincident(g8,g9)
    c: Coincident(g9,g10)
    c: Coincident(g10,g11)
    c: Coincident(g11,g12)
    c: Coincident(g12,g7)
    c: Equal(g7, g8-g12) x5
    c: PointOnObject(g7,g13)
    c: PointOnObject(g8,g13)
    c: PointOnObject(g9,g13)
    c: PointOnObject(g10,g13)
    c: PointOnObject(g11,g13)
    c: PointOnObject(g12,g13)
    c: Horizontal(g12)
    c: Horizontal(g5)
    c: Equal(g6,g13)
    c: DistanceY(g0,g1) = 2
    c: Symmetric(g13,g6,g-2)
    c: DistanceX(g13,g6) = 175
    c: DistanceY(g6) = 2
FEATURE [PartDesign::Pocket] Pocket062
  BaseFeature = -> Chamfer003
  Direction = (0,1,-2e-16)
  Length = 5
  Length2 = 5
  Midplane = true
  Profile = -> Sketch146
  ReferenceAxis = -> Sketch146 [N_Axis]
  Suppressed = false
  Type = 1
FEATURE [PartDesign::Body] Body070  label="LED-Kragen"
  AllowCompound = false
  Group = -> [Sketch,Pad070,Chamfer003,Sketch146,Pocket062]
  Origin = -> Origin079
  Placement = pos=(-57,-167,14) rot=(0,0,1;0rad)
  Tip = -> Pocket062
FEATURE [Sketcher::SketchObject] Sketch147
  AttachmentSupport = -> [XY_Plane080]
  FullyConstrained = true
  MapMode = 5
  Support = -> [XY_Plane080]
  sketch-geometry (4):
    g0: LineSegment StartX=2.67949 StartY=10 StartZ=0 EndX=40 EndY=10 EndZ=0
    g1: LineSegment StartX=40 StartY=10 StartZ=0 EndX=40 EndY=-75 EndZ=0
    g2: LineSegment StartX=40 StartY=-75 StartZ=0 EndX=-20.0962 EndY=-75 EndZ=0
    g3: LineSegment StartX=-20.0962 StartY=-75 StartZ=0 EndX=2.67949 EndY=10 EndZ=0
  constraints (12):
    c: Coincident(g0,g1)
    c: Vertical(g1)
    c: Coincident(g1,g2)
    c: Horizontal(g2)
    c: Coincident(g2,g3)
    c: Angle(g3) = 1.309
    c: DistanceY(g2) = -75
    c: DistanceX(g1) = 40
    c: PointOnObject(g-1,g3)
    c: Coincident(g3,g0)
    c: Horizontal(g0)
    c: DistanceY(g1,g1) = 85
FEATURE [PartDesign::Pad] Pad071
  Direction = (0,0,1)
  Length = 45
  Length2 = 10
  Profile = -> Sketch147
  ReferenceAxis = -> Sketch147 [N_Axis]
  Suppressed = false
  Type = 0
FEATURE [PartDesign::Chamfer] Chamfer004
  Angle = 45
  Base = -> Pad071 [Edge10,Edge5,Edge7]
  BaseFeature = -> Pad071
  ChamferType = 0
  FlipDirection = false
  Size = 6
  Size2 = 1
  SupportTransform = false
  Suppressed = false
  UseAllEdges = false
FEATURE [PartDesign::Thickness] Thickness
  Base = -> Chamfer004 [Face6,Face1,Face4]
  BaseFeature = -> Chamfer004
  Intersection = true
  Join = 0
  Mode = 0
  Reversed = true
  SupportTransform = false
  Suppressed = false
  Value = 1.5
FEATURE [Image::ImagePlane] Screenshot_from_2024_06_28_10_08_40  label="Screenshot from 2024-06-28 10-08-40"
  Placement = pos=(-186.5,-73,-208.5) rot=(0,-0.707107,0.707107;3.14159rad)
  XSize = 10.8793
  YSize = 24.5667
FEATURE [Sketcher::SketchObject] Sketch148
  AttachmentOffset = pos=(16,20,76) rot=(0,0,1;0rad)
  AttachmentSupport = -> [XZ_Plane080]
  FullyConstrained = true
  MapMode = 5
  Placement = pos=(16,-76,20) rot=(1,0,0;1.5708rad)
  Support = -> [XZ_Plane080]
  sketch-geometry (4):
    g0: LineSegment StartX=0 StartY=0 StartZ=0 EndX=2.54 EndY=0 EndZ=0
    g1: LineSegment StartX=2.54 StartY=0 StartZ=0 EndX=2.54 EndY=12.7 EndZ=0
    g2: LineSegment StartX=2.54 StartY=12.7 StartZ=0 EndX=0 EndY=12.7 EndZ=0
    g3: LineSegment StartX=0 StartY=12.7 StartZ=0 EndX=0 EndY=0 EndZ=0
  constraints (11):
    c: Coincident(g0,g1)
    c: Coincident(g1,g2)
    c: Coincident(g2,g3)
    c: Coincident(g3,g0)
    c: Horizontal(g0)
    c: Horizontal(g2)
    c: Vertical(g1)
    c: Vertical(g3)
    c: Distance(g1,g3) = 2.54
    c: Distance(g0,g2) = 12.7
    c: Coincident(g0,g-1)
FEATURE [Sketcher::SketchObject] Sketch149
  AttachmentOffset = pos=(0,0,80) rot=(0,0,1;0rad)
  AttachmentSupport = -> [XZ_Plane080]
  FullyConstrained = true
  MapMode = 5
  Placement = pos=(0,-80,1.78e-14) rot=(1,0,0;1.5708rad)
  Support = -> [XZ_Plane080]
  sketch-geometry (4):
    g0: LineSegment StartX=19.5 StartY=29.5 StartZ=0 EndX=19.5 EndY=22.5 EndZ=0
    g1: LineSegment StartX=19.5 StartY=22.5 StartZ=0 EndX=23 EndY=22.5 EndZ=0
    g2: LineSegment StartX=23 StartY=22.5 StartZ=0 EndX=23 EndY=29.5 EndZ=0
    g3: LineSegment StartX=23 StartY=29.5 StartZ=0 EndX=19.5 EndY=29.5 EndZ=0
  constraints (12):
    c: Coincident(g0,g1)
    c: Coincident(g1,g2)
    c: Coincident(g2,g3)
    c: Coincident(g3,g0)
    c: Vertical(g0)
    c: Vertical(g2)
    c: Horizontal(g1)
    c: Horizontal(g3)
    c: Distance(g0,g2) = 3.5
    c: Distance(g1,g3) = 7
    c: DistanceX(g0) = 19.5
    c: DistanceY(g0) = 22.5
FEATURE [PartDesign::Pocket] Pocket063
  BaseFeature = -> Thickness
  Direction = (0,1,-2e-16)
  Length = 5
  Length2 = 5
  Midplane = true
  Profile = -> Sketch149
  ReferenceAxis = -> Sketch149 [N_Axis]
  Suppressed = false
  Type = 1
FEATURE [Sketcher::SketchObject] Sketch150
  AttachmentOffset = pos=(0,0,74.2) rot=(0,0,1;0rad)
  AttachmentSupport = -> [XZ_Plane080]
  FullyConstrained = true
  MapMode = 5
  Placement = pos=(0,-74.2,1.65e-14) rot=(1,0,0;1.5708rad)
  Support = -> [XZ_Plane080]
  sketch-geometry (4):
    g0: LineSegment StartX=17 StartY=38.5 StartZ=0 EndX=17 EndY=13 EndZ=0
    g1: LineSegment StartX=17 StartY=13 StartZ=0 EndX=28.5 EndY=13 EndZ=0
    g2: LineSegment StartX=28.5 StartY=13 StartZ=0 EndX=28.5 EndY=38.5 EndZ=0
    g3: LineSegment StartX=28.5 StartY=38.5 StartZ=0 EndX=17 EndY=38.5 EndZ=0
  constraints (12):
    c: Coincident(g0,g1)
    c: Coincident(g1,g2)
    c: Coincident(g2,g3)
    c: Coincident(g3,g0)
    c: Vertical(g0)
    c: Vertical(g2)
    c: Horizontal(g1)
    c: Horizontal(g3)
    c: DistanceX(g1,g1) = 11.5
    c: DistanceY(g2,g2) = 25.5
    c: DistanceX(g0) = 17
    c: DistanceY(g0) = 13
FEATURE [PartDesign::Pocket] Pocket064
  BaseFeature = -> Pocket063
  Direction = (0,1,-2e-16)
  Length = 5
  Length2 = 5
  Profile = -> Sketch150
  ReferenceAxis = -> Sketch150 [N_Axis]
  Suppressed = false
  Type = 0
FEATURE [PartDesign::Body] Body071  label="Schaltschrank"
  AllowCompound = false
  Group = -> [Sketch147,Pad071,Chamfer004,Thickness,Sketch148,Sketch149,Pocket063,Sketch150,Pocket064]
  Origin = -> Origin080
  Placement = pos=(-209.5,0,-234) rot=(0,0,1;0rad)
  Tip = -> Pocket064
FEATURE [App::Part] Part007  label="Electronics"
  Group = -> [Screenshot_from_2024_06_28_10_08_40,Body071]
  Origin = -> Origin081
  Placement = pos=(0,0,200) rot=(0,0,1;0rad)
